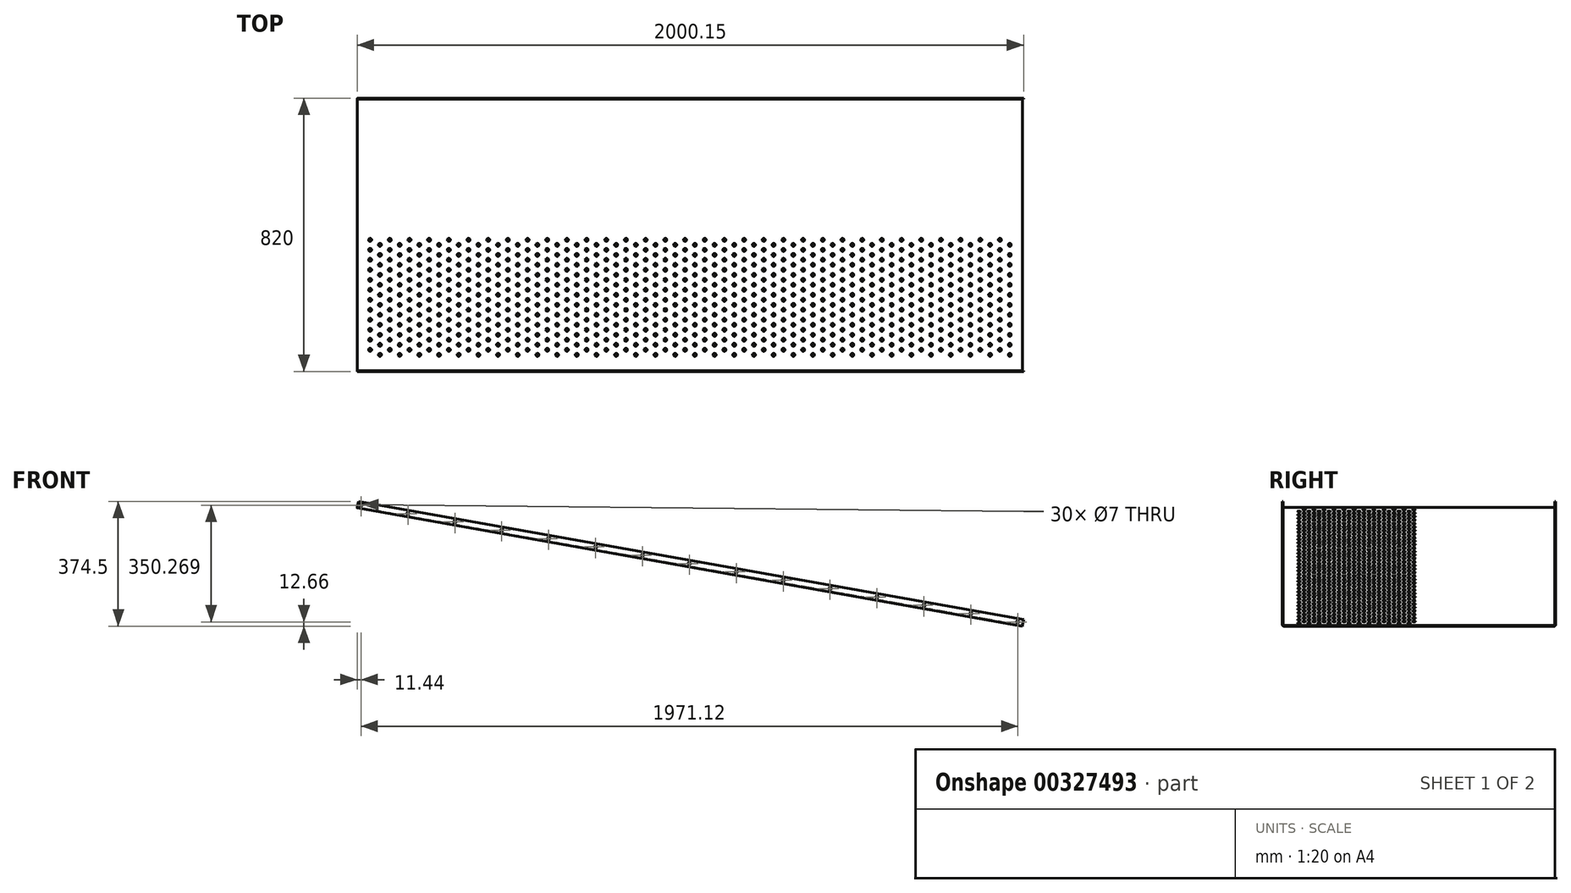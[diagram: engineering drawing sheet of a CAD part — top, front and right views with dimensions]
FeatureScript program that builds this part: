
annotation { "Feature Type Name" : "Feature", "Feature Type Description" : "" }
export const myFeature = defineFeature(function(context is Context, id is Id, definition is map)
    precondition{}
    {
        {
            var Q0;
            Q0=qCreatedBy(makeId("Front.planeOp"),FACE);
            var sketch = newSketch(context, id + "F0", { "sketchPlane" : qUnion([Q0])});
            skLineSegment(sketch, "E0", {"start": v(1435.35, 1.97) * mm, "end": v(-561.3, 356.77) * mm});
            skLineSegment(sketch, "E1", {"start": v(-561.3, 356.77) * mm, "end": v(-561.65, 354.8) * mm});
            skLineSegment(sketch, "E2", {"start": v(-561.65, 354.8) * mm, "end": v(0, 255) * mm});
            skLineSegment(sketch, "E3", {"start": v(1435, 0) * mm, "end": v(1435.35, 1.97) * mm});
            skLineSegment(sketch, "E4", {"start": v(0, 255) * mm, "end": v(1435, 0) * mm});
            skLineSegment(sketch, "E5", {"start": v(0, 255) * mm, "end": v(0, 0) * mm, "construction": true});
            skLineSegment(sketch, "E6", {"start": v(0, 0) * mm, "end": v(1435, 0) * mm, "construction": true});
            skSolve(sketch);
        }
        {
            var Q0;
            Q0=makeQuery(id+"F0.imprint","IMPRINT",FACE,{"disambiguationData":[TD([[makeQuery(id+"F0.imprint","IMPRINT",EDGE,{"derivedFrom":sQuery(id+"F0.wireOp",EDGE,"E0")}),1.0]])]});
            extrude(context, id + "F1", {"entities" : qUnion([Q0]), "depth" : 820 * mm, "symmetric" : true});
        }
        {
            var Q0;
            Q0=makeQuery(id+"F1.opExtrude","CAP_FACE",FACE,{"disambiguationData":[OSD([sQuery(id+"F0.wireOp",EDGE,"E0"),sQuery(id+"F0.wireOp",EDGE,"E1"),sQuery(id+"F0.wireOp",EDGE,"E2"),sQuery(id+"F0.wireOp",EDGE,"E3")])],"isStart":false});
            var sketch = newSketch(context, id + "F2", { "sketchPlane" : qUnion([Q0])});
            skLineSegment(sketch, "E7", {"start": v(-561.65, 354.8) * mm, "end": v(-558.15, 374.5) * mm});
            skLineSegment(sketch, "E8", {"start": v(-558.15, 374.5) * mm, "end": v(1438.5, 19.7) * mm});
            skLineSegment(sketch, "E9", {"start": v(1438.5, 19.7) * mm, "end": v(1435, 0) * mm});
            skLineSegment(sketch, "E10", {"start": v(1435, 0) * mm, "end": v(-561.65, 354.8) * mm});
            skLineSegment(sketch, "E11", {"start": v(-561.65, 354.8) * mm, "end": v(-564.65, 355.34) * mm, "construction": true});
            skLineSegment(sketch, "E12", {"start": v(-564.65, 355.34) * mm, "end": v(-564.65, 375.65) * mm, "construction": true});
            skLineSegment(sketch, "E13", {"start": v(-564.65, 375.65) * mm, "end": v(-558.15, 374.5) * mm, "construction": true});
            skLineSegment(sketch, "E14", {"start": v(1435.35, 20.25) * mm, "end": v(1435.35, 1.97) * mm, "construction": true});
            skLineSegment(sketch, "E15", {"start": v(1435.35, 10.1) * mm, "end": v(1420.91, 12.66) * mm, "construction": true});
            skLineSegment(sketch, "E16", {"start": v(-550.21, 367) * mm, "end": v(-550.21, 358.87) * mm, "construction": true});
            skLineSegment(sketch, "E17", {"start": v(-550.21, 362.93) * mm, "end": v(-564.65, 365.5) * mm, "construction": true});
            skCircle(sketch, "E18", {"center": v(-550.21, 362.93) * mm, "radius": 3.5 * mm});
            skCircle(sketch, "E19.1.0.0", {"center": v(-409.42, 337.91) * mm, "radius": 3.5 * mm});
            skLineSegment(sketch, "E19.1.0.1", {"start": v(-409.42, 341.97) * mm, "end": v(-409.42, 333.85) * mm, "construction": true});
            skCircle(sketch, "E19.2.0.0", {"center": v(-268.62, 312.9) * mm, "radius": 3.5 * mm});
            skLineSegment(sketch, "E19.2.0.1", {"start": v(-268.62, 316.95) * mm, "end": v(-268.62, 308.83) * mm, "construction": true});
            skCircle(sketch, "E19.3.0.0", {"center": v(-127.83, 287.87) * mm, "radius": 3.5 * mm});
            skLineSegment(sketch, "E19.3.0.1", {"start": v(-127.83, 291.93) * mm, "end": v(-127.83, 283.8) * mm, "construction": true});
            skCircle(sketch, "E19.4.0.0", {"center": v(12.97, 262.85) * mm, "radius": 3.5 * mm});
            skLineSegment(sketch, "E19.4.0.1", {"start": v(12.97, 266.92) * mm, "end": v(12.97, 258.79) * mm, "construction": true});
            skCircle(sketch, "E19.5.0.0", {"center": v(153.76, 237.83) * mm, "radius": 3.5 * mm});
            skLineSegment(sketch, "E19.5.0.1", {"start": v(153.76, 241.9) * mm, "end": v(153.76, 233.77) * mm, "construction": true});
            skCircle(sketch, "E19.6.0.0", {"center": v(294.56, 212.81) * mm, "radius": 3.5 * mm});
            skLineSegment(sketch, "E19.6.0.1", {"start": v(294.56, 216.88) * mm, "end": v(294.56, 208.75) * mm, "construction": true});
            skCircle(sketch, "E19.7.0.0", {"center": v(435.35, 187.8) * mm, "radius": 3.5 * mm});
            skLineSegment(sketch, "E19.7.0.1", {"start": v(435.35, 191.86) * mm, "end": v(435.35, 183.73) * mm, "construction": true});
            skCircle(sketch, "E19.8.0.0", {"center": v(576.14, 162.78) * mm, "radius": 3.5 * mm});
            skLineSegment(sketch, "E19.8.0.1", {"start": v(576.14, 166.84) * mm, "end": v(576.14, 158.71) * mm, "construction": true});
            skCircle(sketch, "E19.9.0.0", {"center": v(716.94, 137.76) * mm, "radius": 3.5 * mm});
            skLineSegment(sketch, "E19.9.0.1", {"start": v(716.94, 141.82) * mm, "end": v(716.94, 133.7) * mm, "construction": true});
            skCircle(sketch, "E19.10.0.0", {"center": v(857.73, 112.74) * mm, "radius": 3.5 * mm});
            skLineSegment(sketch, "E19.10.0.1", {"start": v(857.73, 116.8) * mm, "end": v(857.73, 108.67) * mm, "construction": true});
            skCircle(sketch, "E19.11.0.0", {"center": v(998.53, 87.72) * mm, "radius": 3.5 * mm});
            skLineSegment(sketch, "E19.11.0.1", {"start": v(998.53, 91.78) * mm, "end": v(998.53, 83.66) * mm, "construction": true});
            skCircle(sketch, "E19.12.0.0", {"center": v(1139.32, 62.7) * mm, "radius": 3.5 * mm});
            skLineSegment(sketch, "E19.12.0.1", {"start": v(1139.32, 66.76) * mm, "end": v(1139.32, 58.64) * mm, "construction": true});
            skCircle(sketch, "E19.13.0.0", {"center": v(1280.12, 37.68) * mm, "radius": 3.5 * mm});
            skLineSegment(sketch, "E19.13.0.1", {"start": v(1280.12, 41.74) * mm, "end": v(1280.12, 33.62) * mm, "construction": true});
            skCircle(sketch, "E19.14.0.0", {"center": v(1420.91, 12.66) * mm, "radius": 3.5 * mm});
            skLineSegment(sketch, "E19.14.0.1", {"start": v(1420.91, 16.72) * mm, "end": v(1420.91, 8.6) * mm, "construction": true});
            skLineSegment(sketch, "E19.direction1", {"start": v(-550.21, 362.93) * mm, "end": v(-409.42, 337.91) * mm, "construction": true});
            skPoint(sketch, "E20.orphan", {"position": v(1436.75, 9.85) * mm});
            skLineSegment(sketch, "E21.trimOffspring", {"start": v(1420.91, 12.66) * mm, "end": v(-550.21, 362.93) * mm, "construction": true});
            skSolve(sketch);
        }
        {
            var Q0;
            Q0=qSketchRegion(id+"F2",true);
            extrude(context, id + "F3", {"entities" : qUnion([Q0]), "operationType" : NewBodyOperationType.ADD, "oppositeDirection" : true, "depth" : 2 * mm});
        }
        {
            var Q0;
            Q0=makeQuery(id+"F1.opExtrude","CAP_FACE",FACE,{"disambiguationData":[OSD([sQuery(id+"F0.wireOp",EDGE,"E0"),sQuery(id+"F0.wireOp",EDGE,"E1"),sQuery(id+"F0.wireOp",EDGE,"E2"),sQuery(id+"F0.wireOp",EDGE,"E3")])],"isStart":true});
            var sketch = newSketch(context, id + "F4", { "sketchPlane" : qUnion([Q0])});
            skLineSegment(sketch, "E22", {"start": v(561.65, 354.8) * mm, "end": v(558.15, 374.5) * mm});
            skLineSegment(sketch, "E23", {"start": v(558.15, 374.5) * mm, "end": v(-1438.5, 19.7) * mm});
            skLineSegment(sketch, "E24", {"start": v(-1438.5, 19.7) * mm, "end": v(-1435, 0) * mm});
            skLineSegment(sketch, "E25", {"start": v(-1435, 0) * mm, "end": v(561.65, 354.8) * mm});
            skLineSegment(sketch, "E26", {"start": v(561.65, 354.8) * mm, "end": v(564.65, 355.34) * mm, "construction": true});
            skLineSegment(sketch, "E27", {"start": v(564.65, 355.34) * mm, "end": v(564.65, 375.65) * mm, "construction": true});
            skLineSegment(sketch, "E28", {"start": v(564.65, 375.65) * mm, "end": v(558.15, 374.5) * mm, "construction": true});
            skLineSegment(sketch, "E29", {"start": v(-1435.35, 20.25) * mm, "end": v(-1435.35, 1.97) * mm, "construction": true});
            skLineSegment(sketch, "E30", {"start": v(-1435.35, 10.1) * mm, "end": v(-1420.91, 12.66) * mm, "construction": true});
            skLineSegment(sketch, "E31", {"start": v(550.21, 367) * mm, "end": v(550.21, 358.87) * mm, "construction": true});
            skLineSegment(sketch, "E32", {"start": v(550.21, 362.93) * mm, "end": v(564.65, 365.5) * mm, "construction": true});
            skCircle(sketch, "E33", {"center": v(550.21, 362.93) * mm, "radius": 3.5 * mm});
            skCircle(sketch, "E34.1.0.0", {"center": v(409.42, 337.91) * mm, "radius": 3.5 * mm});
            skLineSegment(sketch, "E34.1.0.1", {"start": v(409.42, 341.97) * mm, "end": v(409.42, 333.85) * mm, "construction": true});
            skCircle(sketch, "E34.2.0.0", {"center": v(268.62, 312.9) * mm, "radius": 3.5 * mm});
            skLineSegment(sketch, "E34.2.0.1", {"start": v(268.62, 316.95) * mm, "end": v(268.62, 308.83) * mm, "construction": true});
            skCircle(sketch, "E34.3.0.0", {"center": v(127.83, 287.87) * mm, "radius": 3.5 * mm});
            skLineSegment(sketch, "E34.3.0.1", {"start": v(127.83, 291.93) * mm, "end": v(127.83, 283.8) * mm, "construction": true});
            skCircle(sketch, "E34.4.0.0", {"center": v(-12.97, 262.85) * mm, "radius": 3.5 * mm});
            skLineSegment(sketch, "E34.4.0.1", {"start": v(-12.97, 266.92) * mm, "end": v(-12.97, 258.79) * mm, "construction": true});
            skCircle(sketch, "E34.5.0.0", {"center": v(-153.76, 237.83) * mm, "radius": 3.5 * mm});
            skLineSegment(sketch, "E34.5.0.1", {"start": v(-153.76, 241.9) * mm, "end": v(-153.76, 233.77) * mm, "construction": true});
            skCircle(sketch, "E34.6.0.0", {"center": v(-294.56, 212.81) * mm, "radius": 3.5 * mm});
            skLineSegment(sketch, "E34.6.0.1", {"start": v(-294.56, 216.88) * mm, "end": v(-294.56, 208.75) * mm, "construction": true});
            skCircle(sketch, "E34.7.0.0", {"center": v(-435.35, 187.8) * mm, "radius": 3.5 * mm});
            skLineSegment(sketch, "E34.7.0.1", {"start": v(-435.35, 191.86) * mm, "end": v(-435.35, 183.73) * mm, "construction": true});
            skCircle(sketch, "E34.8.0.0", {"center": v(-576.14, 162.78) * mm, "radius": 3.5 * mm});
            skLineSegment(sketch, "E34.8.0.1", {"start": v(-576.14, 166.84) * mm, "end": v(-576.14, 158.71) * mm, "construction": true});
            skCircle(sketch, "E34.9.0.0", {"center": v(-716.94, 137.76) * mm, "radius": 3.5 * mm});
            skLineSegment(sketch, "E34.9.0.1", {"start": v(-716.94, 141.82) * mm, "end": v(-716.94, 133.7) * mm, "construction": true});
            skCircle(sketch, "E34.10.0.0", {"center": v(-857.73, 112.74) * mm, "radius": 3.5 * mm});
            skLineSegment(sketch, "E34.10.0.1", {"start": v(-857.73, 116.8) * mm, "end": v(-857.73, 108.67) * mm, "construction": true});
            skCircle(sketch, "E34.11.0.0", {"center": v(-998.53, 87.72) * mm, "radius": 3.5 * mm});
            skLineSegment(sketch, "E34.11.0.1", {"start": v(-998.53, 91.78) * mm, "end": v(-998.53, 83.66) * mm, "construction": true});
            skCircle(sketch, "E34.12.0.0", {"center": v(-1139.32, 62.7) * mm, "radius": 3.5 * mm});
            skLineSegment(sketch, "E34.12.0.1", {"start": v(-1139.32, 66.76) * mm, "end": v(-1139.32, 58.64) * mm, "construction": true});
            skCircle(sketch, "E34.13.0.0", {"center": v(-1280.12, 37.68) * mm, "radius": 3.5 * mm});
            skLineSegment(sketch, "E34.13.0.1", {"start": v(-1280.12, 41.74) * mm, "end": v(-1280.12, 33.62) * mm, "construction": true});
            skCircle(sketch, "E34.14.0.0", {"center": v(-1420.91, 12.66) * mm, "radius": 3.5 * mm});
            skLineSegment(sketch, "E34.14.0.1", {"start": v(-1420.91, 16.72) * mm, "end": v(-1420.91, 8.6) * mm, "construction": true});
            skLineSegment(sketch, "E34.direction1", {"start": v(550.21, 362.93) * mm, "end": v(409.42, 337.91) * mm, "construction": true});
            skPoint(sketch, "E35.orphan", {"position": v(-1436.75, 9.85) * mm});
            skLineSegment(sketch, "E36.trimOffspring", {"start": v(-1420.91, 12.66) * mm, "end": v(550.21, 362.93) * mm, "construction": true});
            skSolve(sketch);
        }
        {
            var Q0;
            Q0=qSketchRegion(id+"F4",true);
            extrude(context, id + "F5", {"entities" : qUnion([Q0]), "operationType" : NewBodyOperationType.ADD, "oppositeDirection" : true, "depth" : 2 * mm});
        }
        {
            var Q0;
            Q0=makeQuery(id+"F1.opExtrude","SWEPT_FACE",FACE,{"disambiguationData":[OSD([sQuery(id+"F0.wireOp",EDGE,"E0")])]});
            var sketch = newSketch(context, id + "F6", { "sketchPlane" : qUnion([Q0])});
            skCircle(sketch, "E37", {"center": v(1373.9, -360) * mm, "radius": 4.5 * mm});
            skCircle(sketch, "E38", {"center": v(1343.9, -345) * mm, "radius": 4.5 * mm});
            skLineSegment(sketch, "E39", {"start": v(1412.87, 0) * mm, "end": v(-615.06, 0) * mm, "construction": true});
            skCircle(sketch, "E40.0.1.0", {"center": v(1373.9, -330) * mm, "radius": 4.5 * mm});
            skCircle(sketch, "E40.0.2.0", {"center": v(1373.9, -300) * mm, "radius": 4.5 * mm});
            skCircle(sketch, "E40.0.3.0", {"center": v(1373.9, -270) * mm, "radius": 4.5 * mm});
            skCircle(sketch, "E40.0.4.0", {"center": v(1373.9, -240) * mm, "radius": 4.5 * mm});
            skCircle(sketch, "E40.0.5.0", {"center": v(1373.9, -210) * mm, "radius": 4.5 * mm});
            skCircle(sketch, "E40.0.6.0", {"center": v(1373.9, -180) * mm, "radius": 4.5 * mm});
            skCircle(sketch, "E40.0.7.0", {"center": v(1373.9, -150) * mm, "radius": 4.5 * mm});
            skCircle(sketch, "E40.0.8.0", {"center": v(1373.9, -120) * mm, "radius": 4.5 * mm});
            skCircle(sketch, "E40.0.9.0", {"center": v(1373.9, -90) * mm, "radius": 4.5 * mm});
            skCircle(sketch, "E40.0.10.0", {"center": v(1373.9, -60) * mm, "radius": 4.5 * mm});
            skCircle(sketch, "E40.0.11.0", {"center": v(1373.9, -30) * mm, "radius": 4.5 * mm});
            skCircle(sketch, "E40.0.12.0", {"center": v(1373.9, 0) * mm, "radius": 4.5 * mm});
            skLineSegment(sketch, "E40.direction1", {"start": v(1373.9, -360) * mm, "end": v(1373.9, -360) * mm});
            skLineSegment(sketch, "E40.direction2", {"start": v(1373.9, -360) * mm, "end": v(1373.9, -330) * mm, "construction": true});
            skCircle(sketch, "E41.0.1.0", {"center": v(1343.9, -315) * mm, "radius": 4.5 * mm});
            skCircle(sketch, "E41.0.2.0", {"center": v(1343.9, -285) * mm, "radius": 4.5 * mm});
            skCircle(sketch, "E41.0.3.0", {"center": v(1343.9, -255) * mm, "radius": 4.5 * mm});
            skCircle(sketch, "E41.0.4.0", {"center": v(1343.9, -225) * mm, "radius": 4.5 * mm});
            skCircle(sketch, "E41.0.5.0", {"center": v(1343.9, -195) * mm, "radius": 4.5 * mm});
            skCircle(sketch, "E41.0.6.0", {"center": v(1343.9, -165) * mm, "radius": 4.5 * mm});
            skCircle(sketch, "E41.0.7.0", {"center": v(1343.9, -135) * mm, "radius": 4.5 * mm});
            skCircle(sketch, "E41.0.8.0", {"center": v(1343.9, -105) * mm, "radius": 4.5 * mm});
            skCircle(sketch, "E41.0.9.0", {"center": v(1343.9, -75) * mm, "radius": 4.5 * mm});
            skCircle(sketch, "E41.0.10.0", {"center": v(1343.9, -45) * mm, "radius": 4.5 * mm});
            skCircle(sketch, "E41.0.11.0", {"center": v(1343.9, -15) * mm, "radius": 4.5 * mm});
            skLineSegment(sketch, "E41.direction1", {"start": v(1343.9, -345) * mm, "end": v(1343.9, -345) * mm});
            skLineSegment(sketch, "E41.direction2", {"start": v(1343.9, -345) * mm, "end": v(1343.9, -315) * mm, "construction": true});
            skLineSegment(sketch, "E42.1.0.0", {"start": v(1313.9, -360) * mm, "end": v(1313.9, -330) * mm, "construction": true});
            skCircle(sketch, "E42.1.0.1", {"center": v(1313.9, -60) * mm, "radius": 4.5 * mm});
            skCircle(sketch, "E42.1.0.2", {"center": v(1313.9, -30) * mm, "radius": 4.5 * mm});
            skCircle(sketch, "E42.1.0.3", {"center": v(1313.9, 0) * mm, "radius": 4.5 * mm});
            skCircle(sketch, "E42.1.0.4", {"center": v(1313.9, -240) * mm, "radius": 4.5 * mm});
            skCircle(sketch, "E42.1.0.5", {"center": v(1313.9, -300) * mm, "radius": 4.5 * mm});
            skCircle(sketch, "E42.1.0.6", {"center": v(1283.9, -75) * mm, "radius": 4.5 * mm});
            skCircle(sketch, "E42.1.0.7", {"center": v(1283.9, -285) * mm, "radius": 4.5 * mm});
            skCircle(sketch, "E42.1.0.8", {"center": v(1283.9, -105) * mm, "radius": 4.5 * mm});
            skCircle(sketch, "E42.1.0.9", {"center": v(1283.9, -255) * mm, "radius": 4.5 * mm});
            skCircle(sketch, "E42.1.0.10", {"center": v(1283.9, -195) * mm, "radius": 4.5 * mm});
            skLineSegment(sketch, "E42.1.0.11", {"start": v(1283.9, -345) * mm, "end": v(1283.9, -315) * mm, "construction": true});
            skCircle(sketch, "E42.1.0.12", {"center": v(1283.9, -15) * mm, "radius": 4.5 * mm});
            skCircle(sketch, "E42.1.0.13", {"center": v(1313.9, -120) * mm, "radius": 4.5 * mm});
            skCircle(sketch, "E42.1.0.14", {"center": v(1283.9, -45) * mm, "radius": 4.5 * mm});
            skCircle(sketch, "E42.1.0.15", {"center": v(1313.9, -180) * mm, "radius": 4.5 * mm});
            skCircle(sketch, "E42.1.0.16", {"center": v(1313.9, -150) * mm, "radius": 4.5 * mm});
            skCircle(sketch, "E42.1.0.17", {"center": v(1313.9, -90) * mm, "radius": 4.5 * mm});
            skCircle(sketch, "E42.1.0.18", {"center": v(1283.9, -135) * mm, "radius": 4.5 * mm});
            skCircle(sketch, "E42.1.0.19", {"center": v(1283.9, -225) * mm, "radius": 4.5 * mm});
            skCircle(sketch, "E42.1.0.20", {"center": v(1313.9, -210) * mm, "radius": 4.5 * mm});
            skCircle(sketch, "E42.1.0.21", {"center": v(1283.9, -165) * mm, "radius": 4.5 * mm});
            skCircle(sketch, "E42.1.0.22", {"center": v(1313.9, -270) * mm, "radius": 4.5 * mm});
            skCircle(sketch, "E42.1.0.23", {"center": v(1313.9, -330) * mm, "radius": 4.5 * mm});
            skCircle(sketch, "E42.1.0.24", {"center": v(1283.9, -315) * mm, "radius": 4.5 * mm});
            skCircle(sketch, "E42.1.0.25", {"center": v(1283.9, -345) * mm, "radius": 4.5 * mm});
            skCircle(sketch, "E42.1.0.26", {"center": v(1313.9, -360) * mm, "radius": 4.5 * mm});
            skLineSegment(sketch, "E42.2.0.0", {"start": v(1253.9, -360) * mm, "end": v(1253.9, -330) * mm, "construction": true});
            skCircle(sketch, "E42.2.0.1", {"center": v(1253.9, -60) * mm, "radius": 4.5 * mm});
            skCircle(sketch, "E42.2.0.2", {"center": v(1253.9, -30) * mm, "radius": 4.5 * mm});
            skCircle(sketch, "E42.2.0.3", {"center": v(1253.9, 0) * mm, "radius": 4.5 * mm});
            skCircle(sketch, "E42.2.0.4", {"center": v(1253.9, -240) * mm, "radius": 4.5 * mm});
            skCircle(sketch, "E42.2.0.5", {"center": v(1253.9, -300) * mm, "radius": 4.5 * mm});
            skCircle(sketch, "E42.2.0.6", {"center": v(1223.9, -75) * mm, "radius": 4.5 * mm});
            skCircle(sketch, "E42.2.0.7", {"center": v(1223.9, -285) * mm, "radius": 4.5 * mm});
            skCircle(sketch, "E42.2.0.8", {"center": v(1223.9, -105) * mm, "radius": 4.5 * mm});
            skCircle(sketch, "E42.2.0.9", {"center": v(1223.9, -255) * mm, "radius": 4.5 * mm});
            skCircle(sketch, "E42.2.0.10", {"center": v(1223.9, -195) * mm, "radius": 4.5 * mm});
            skLineSegment(sketch, "E42.2.0.11", {"start": v(1223.9, -345) * mm, "end": v(1223.9, -315) * mm, "construction": true});
            skCircle(sketch, "E42.2.0.12", {"center": v(1223.9, -15) * mm, "radius": 4.5 * mm});
            skCircle(sketch, "E42.2.0.13", {"center": v(1253.9, -120) * mm, "radius": 4.5 * mm});
            skCircle(sketch, "E42.2.0.14", {"center": v(1223.9, -45) * mm, "radius": 4.5 * mm});
            skCircle(sketch, "E42.2.0.15", {"center": v(1253.9, -180) * mm, "radius": 4.5 * mm});
            skCircle(sketch, "E42.2.0.16", {"center": v(1253.9, -150) * mm, "radius": 4.5 * mm});
            skCircle(sketch, "E42.2.0.17", {"center": v(1253.9, -90) * mm, "radius": 4.5 * mm});
            skCircle(sketch, "E42.2.0.18", {"center": v(1223.9, -135) * mm, "radius": 4.5 * mm});
            skCircle(sketch, "E42.2.0.19", {"center": v(1223.9, -225) * mm, "radius": 4.5 * mm});
            skCircle(sketch, "E42.2.0.20", {"center": v(1253.9, -210) * mm, "radius": 4.5 * mm});
            skCircle(sketch, "E42.2.0.21", {"center": v(1223.9, -165) * mm, "radius": 4.5 * mm});
            skCircle(sketch, "E42.2.0.22", {"center": v(1253.9, -270) * mm, "radius": 4.5 * mm});
            skCircle(sketch, "E42.2.0.23", {"center": v(1253.9, -330) * mm, "radius": 4.5 * mm});
            skCircle(sketch, "E42.2.0.24", {"center": v(1223.9, -315) * mm, "radius": 4.5 * mm});
            skCircle(sketch, "E42.2.0.25", {"center": v(1223.9, -345) * mm, "radius": 4.5 * mm});
            skCircle(sketch, "E42.2.0.26", {"center": v(1253.9, -360) * mm, "radius": 4.5 * mm});
            skLineSegment(sketch, "E42.3.0.0", {"start": v(1193.9, -360) * mm, "end": v(1193.9, -330) * mm, "construction": true});
            skCircle(sketch, "E42.3.0.1", {"center": v(1193.9, -60) * mm, "radius": 4.5 * mm});
            skCircle(sketch, "E42.3.0.2", {"center": v(1193.9, -30) * mm, "radius": 4.5 * mm});
            skCircle(sketch, "E42.3.0.3", {"center": v(1193.9, 0) * mm, "radius": 4.5 * mm});
            skCircle(sketch, "E42.3.0.4", {"center": v(1193.9, -240) * mm, "radius": 4.5 * mm});
            skCircle(sketch, "E42.3.0.5", {"center": v(1193.9, -300) * mm, "radius": 4.5 * mm});
            skCircle(sketch, "E42.3.0.6", {"center": v(1163.9, -75) * mm, "radius": 4.5 * mm});
            skCircle(sketch, "E42.3.0.7", {"center": v(1163.9, -285) * mm, "radius": 4.5 * mm});
            skCircle(sketch, "E42.3.0.8", {"center": v(1163.9, -105) * mm, "radius": 4.5 * mm});
            skCircle(sketch, "E42.3.0.9", {"center": v(1163.9, -255) * mm, "radius": 4.5 * mm});
            skCircle(sketch, "E42.3.0.10", {"center": v(1163.9, -195) * mm, "radius": 4.5 * mm});
            skLineSegment(sketch, "E42.3.0.11", {"start": v(1163.9, -345) * mm, "end": v(1163.9, -315) * mm, "construction": true});
            skCircle(sketch, "E42.3.0.12", {"center": v(1163.9, -15) * mm, "radius": 4.5 * mm});
            skCircle(sketch, "E42.3.0.13", {"center": v(1193.9, -120) * mm, "radius": 4.5 * mm});
            skCircle(sketch, "E42.3.0.14", {"center": v(1163.9, -45) * mm, "radius": 4.5 * mm});
            skCircle(sketch, "E42.3.0.15", {"center": v(1193.9, -180) * mm, "radius": 4.5 * mm});
            skCircle(sketch, "E42.3.0.16", {"center": v(1193.9, -150) * mm, "radius": 4.5 * mm});
            skCircle(sketch, "E42.3.0.17", {"center": v(1193.9, -90) * mm, "radius": 4.5 * mm});
            skCircle(sketch, "E42.3.0.18", {"center": v(1163.9, -135) * mm, "radius": 4.5 * mm});
            skCircle(sketch, "E42.3.0.19", {"center": v(1163.9, -225) * mm, "radius": 4.5 * mm});
            skCircle(sketch, "E42.3.0.20", {"center": v(1193.9, -210) * mm, "radius": 4.5 * mm});
            skCircle(sketch, "E42.3.0.21", {"center": v(1163.9, -165) * mm, "radius": 4.5 * mm});
            skCircle(sketch, "E42.3.0.22", {"center": v(1193.9, -270) * mm, "radius": 4.5 * mm});
            skCircle(sketch, "E42.3.0.23", {"center": v(1193.9, -330) * mm, "radius": 4.5 * mm});
            skCircle(sketch, "E42.3.0.24", {"center": v(1163.9, -315) * mm, "radius": 4.5 * mm});
            skCircle(sketch, "E42.3.0.25", {"center": v(1163.9, -345) * mm, "radius": 4.5 * mm});
            skCircle(sketch, "E42.3.0.26", {"center": v(1193.9, -360) * mm, "radius": 4.5 * mm});
            skLineSegment(sketch, "E42.4.0.0", {"start": v(1133.9, -360) * mm, "end": v(1133.9, -330) * mm, "construction": true});
            skCircle(sketch, "E42.4.0.1", {"center": v(1133.9, -60) * mm, "radius": 4.5 * mm});
            skCircle(sketch, "E42.4.0.2", {"center": v(1133.9, -30) * mm, "radius": 4.5 * mm});
            skCircle(sketch, "E42.4.0.3", {"center": v(1133.9, 0) * mm, "radius": 4.5 * mm});
            skCircle(sketch, "E42.4.0.4", {"center": v(1133.9, -240) * mm, "radius": 4.5 * mm});
            skCircle(sketch, "E42.4.0.5", {"center": v(1133.9, -300) * mm, "radius": 4.5 * mm});
            skCircle(sketch, "E42.4.0.6", {"center": v(1103.9, -75) * mm, "radius": 4.5 * mm});
            skCircle(sketch, "E42.4.0.7", {"center": v(1103.9, -285) * mm, "radius": 4.5 * mm});
            skCircle(sketch, "E42.4.0.8", {"center": v(1103.9, -105) * mm, "radius": 4.5 * mm});
            skCircle(sketch, "E42.4.0.9", {"center": v(1103.9, -255) * mm, "radius": 4.5 * mm});
            skCircle(sketch, "E42.4.0.10", {"center": v(1103.9, -195) * mm, "radius": 4.5 * mm});
            skLineSegment(sketch, "E42.4.0.11", {"start": v(1103.9, -345) * mm, "end": v(1103.9, -315) * mm, "construction": true});
            skCircle(sketch, "E42.4.0.12", {"center": v(1103.9, -15) * mm, "radius": 4.5 * mm});
            skCircle(sketch, "E42.4.0.13", {"center": v(1133.9, -120) * mm, "radius": 4.5 * mm});
            skCircle(sketch, "E42.4.0.14", {"center": v(1103.9, -45) * mm, "radius": 4.5 * mm});
            skCircle(sketch, "E42.4.0.15", {"center": v(1133.9, -180) * mm, "radius": 4.5 * mm});
            skCircle(sketch, "E42.4.0.16", {"center": v(1133.9, -150) * mm, "radius": 4.5 * mm});
            skCircle(sketch, "E42.4.0.17", {"center": v(1133.9, -90) * mm, "radius": 4.5 * mm});
            skCircle(sketch, "E42.4.0.18", {"center": v(1103.9, -135) * mm, "radius": 4.5 * mm});
            skCircle(sketch, "E42.4.0.19", {"center": v(1103.9, -225) * mm, "radius": 4.5 * mm});
            skCircle(sketch, "E42.4.0.20", {"center": v(1133.9, -210) * mm, "radius": 4.5 * mm});
            skCircle(sketch, "E42.4.0.21", {"center": v(1103.9, -165) * mm, "radius": 4.5 * mm});
            skCircle(sketch, "E42.4.0.22", {"center": v(1133.9, -270) * mm, "radius": 4.5 * mm});
            skCircle(sketch, "E42.4.0.23", {"center": v(1133.9, -330) * mm, "radius": 4.5 * mm});
            skCircle(sketch, "E42.4.0.24", {"center": v(1103.9, -315) * mm, "radius": 4.5 * mm});
            skCircle(sketch, "E42.4.0.25", {"center": v(1103.9, -345) * mm, "radius": 4.5 * mm});
            skCircle(sketch, "E42.4.0.26", {"center": v(1133.9, -360) * mm, "radius": 4.5 * mm});
            skLineSegment(sketch, "E42.5.0.0", {"start": v(1073.9, -360) * mm, "end": v(1073.9, -330) * mm, "construction": true});
            skCircle(sketch, "E42.5.0.1", {"center": v(1073.9, -60) * mm, "radius": 4.5 * mm});
            skCircle(sketch, "E42.5.0.2", {"center": v(1073.9, -30) * mm, "radius": 4.5 * mm});
            skCircle(sketch, "E42.5.0.3", {"center": v(1073.9, 0) * mm, "radius": 4.5 * mm});
            skCircle(sketch, "E42.5.0.4", {"center": v(1073.9, -240) * mm, "radius": 4.5 * mm});
            skCircle(sketch, "E42.5.0.5", {"center": v(1073.9, -300) * mm, "radius": 4.5 * mm});
            skCircle(sketch, "E42.5.0.6", {"center": v(1043.9, -75) * mm, "radius": 4.5 * mm});
            skCircle(sketch, "E42.5.0.7", {"center": v(1043.9, -285) * mm, "radius": 4.5 * mm});
            skCircle(sketch, "E42.5.0.8", {"center": v(1043.9, -105) * mm, "radius": 4.5 * mm});
            skCircle(sketch, "E42.5.0.9", {"center": v(1043.9, -255) * mm, "radius": 4.5 * mm});
            skCircle(sketch, "E42.5.0.10", {"center": v(1043.9, -195) * mm, "radius": 4.5 * mm});
            skLineSegment(sketch, "E42.5.0.11", {"start": v(1043.9, -345) * mm, "end": v(1043.9, -315) * mm, "construction": true});
            skCircle(sketch, "E42.5.0.12", {"center": v(1043.9, -15) * mm, "radius": 4.5 * mm});
            skCircle(sketch, "E42.5.0.13", {"center": v(1073.9, -120) * mm, "radius": 4.5 * mm});
            skCircle(sketch, "E42.5.0.14", {"center": v(1043.9, -45) * mm, "radius": 4.5 * mm});
            skCircle(sketch, "E42.5.0.15", {"center": v(1073.9, -180) * mm, "radius": 4.5 * mm});
            skCircle(sketch, "E42.5.0.16", {"center": v(1073.9, -150) * mm, "radius": 4.5 * mm});
            skCircle(sketch, "E42.5.0.17", {"center": v(1073.9, -90) * mm, "radius": 4.5 * mm});
            skCircle(sketch, "E42.5.0.18", {"center": v(1043.9, -135) * mm, "radius": 4.5 * mm});
            skCircle(sketch, "E42.5.0.19", {"center": v(1043.9, -225) * mm, "radius": 4.5 * mm});
            skCircle(sketch, "E42.5.0.20", {"center": v(1073.9, -210) * mm, "radius": 4.5 * mm});
            skCircle(sketch, "E42.5.0.21", {"center": v(1043.9, -165) * mm, "radius": 4.5 * mm});
            skCircle(sketch, "E42.5.0.22", {"center": v(1073.9, -270) * mm, "radius": 4.5 * mm});
            skCircle(sketch, "E42.5.0.23", {"center": v(1073.9, -330) * mm, "radius": 4.5 * mm});
            skCircle(sketch, "E42.5.0.24", {"center": v(1043.9, -315) * mm, "radius": 4.5 * mm});
            skCircle(sketch, "E42.5.0.25", {"center": v(1043.9, -345) * mm, "radius": 4.5 * mm});
            skCircle(sketch, "E42.5.0.26", {"center": v(1073.9, -360) * mm, "radius": 4.5 * mm});
            skLineSegment(sketch, "E42.6.0.0", {"start": v(1013.9, -360) * mm, "end": v(1013.9, -330) * mm, "construction": true});
            skCircle(sketch, "E42.6.0.1", {"center": v(1013.9, -60) * mm, "radius": 4.5 * mm});
            skCircle(sketch, "E42.6.0.2", {"center": v(1013.9, -30) * mm, "radius": 4.5 * mm});
            skCircle(sketch, "E42.6.0.3", {"center": v(1013.9, 0) * mm, "radius": 4.5 * mm});
            skCircle(sketch, "E42.6.0.4", {"center": v(1013.9, -240) * mm, "radius": 4.5 * mm});
            skCircle(sketch, "E42.6.0.5", {"center": v(1013.9, -300) * mm, "radius": 4.5 * mm});
            skCircle(sketch, "E42.6.0.6", {"center": v(983.9, -75) * mm, "radius": 4.5 * mm});
            skCircle(sketch, "E42.6.0.7", {"center": v(983.9, -285) * mm, "radius": 4.5 * mm});
            skCircle(sketch, "E42.6.0.8", {"center": v(983.9, -105) * mm, "radius": 4.5 * mm});
            skCircle(sketch, "E42.6.0.9", {"center": v(983.9, -255) * mm, "radius": 4.5 * mm});
            skCircle(sketch, "E42.6.0.10", {"center": v(983.9, -195) * mm, "radius": 4.5 * mm});
            skLineSegment(sketch, "E42.6.0.11", {"start": v(983.9, -345) * mm, "end": v(983.9, -315) * mm, "construction": true});
            skCircle(sketch, "E42.6.0.12", {"center": v(983.9, -15) * mm, "radius": 4.5 * mm});
            skCircle(sketch, "E42.6.0.13", {"center": v(1013.9, -120) * mm, "radius": 4.5 * mm});
            skCircle(sketch, "E42.6.0.14", {"center": v(983.9, -45) * mm, "radius": 4.5 * mm});
            skCircle(sketch, "E42.6.0.15", {"center": v(1013.9, -180) * mm, "radius": 4.5 * mm});
            skCircle(sketch, "E42.6.0.16", {"center": v(1013.9, -150) * mm, "radius": 4.5 * mm});
            skCircle(sketch, "E42.6.0.17", {"center": v(1013.9, -90) * mm, "radius": 4.5 * mm});
            skCircle(sketch, "E42.6.0.18", {"center": v(983.9, -135) * mm, "radius": 4.5 * mm});
            skCircle(sketch, "E42.6.0.19", {"center": v(983.9, -225) * mm, "radius": 4.5 * mm});
            skCircle(sketch, "E42.6.0.20", {"center": v(1013.9, -210) * mm, "radius": 4.5 * mm});
            skCircle(sketch, "E42.6.0.21", {"center": v(983.9, -165) * mm, "radius": 4.5 * mm});
            skCircle(sketch, "E42.6.0.22", {"center": v(1013.9, -270) * mm, "radius": 4.5 * mm});
            skCircle(sketch, "E42.6.0.23", {"center": v(1013.9, -330) * mm, "radius": 4.5 * mm});
            skCircle(sketch, "E42.6.0.24", {"center": v(983.9, -315) * mm, "radius": 4.5 * mm});
            skCircle(sketch, "E42.6.0.25", {"center": v(983.9, -345) * mm, "radius": 4.5 * mm});
            skCircle(sketch, "E42.6.0.26", {"center": v(1013.9, -360) * mm, "radius": 4.5 * mm});
            skLineSegment(sketch, "E42.7.0.0", {"start": v(953.9, -360) * mm, "end": v(953.9, -330) * mm, "construction": true});
            skCircle(sketch, "E42.7.0.1", {"center": v(953.9, -60) * mm, "radius": 4.5 * mm});
            skCircle(sketch, "E42.7.0.2", {"center": v(953.9, -30) * mm, "radius": 4.5 * mm});
            skCircle(sketch, "E42.7.0.3", {"center": v(953.9, 0) * mm, "radius": 4.5 * mm});
            skCircle(sketch, "E42.7.0.4", {"center": v(953.9, -240) * mm, "radius": 4.5 * mm});
            skCircle(sketch, "E42.7.0.5", {"center": v(953.9, -300) * mm, "radius": 4.5 * mm});
            skCircle(sketch, "E42.7.0.6", {"center": v(923.9, -75) * mm, "radius": 4.5 * mm});
            skCircle(sketch, "E42.7.0.7", {"center": v(923.9, -285) * mm, "radius": 4.5 * mm});
            skCircle(sketch, "E42.7.0.8", {"center": v(923.9, -105) * mm, "radius": 4.5 * mm});
            skCircle(sketch, "E42.7.0.9", {"center": v(923.9, -255) * mm, "radius": 4.5 * mm});
            skCircle(sketch, "E42.7.0.10", {"center": v(923.9, -195) * mm, "radius": 4.5 * mm});
            skLineSegment(sketch, "E42.7.0.11", {"start": v(923.9, -345) * mm, "end": v(923.9, -315) * mm, "construction": true});
            skCircle(sketch, "E42.7.0.12", {"center": v(923.9, -15) * mm, "radius": 4.5 * mm});
            skCircle(sketch, "E42.7.0.13", {"center": v(953.9, -120) * mm, "radius": 4.5 * mm});
            skCircle(sketch, "E42.7.0.14", {"center": v(923.9, -45) * mm, "radius": 4.5 * mm});
            skCircle(sketch, "E42.7.0.15", {"center": v(953.9, -180) * mm, "radius": 4.5 * mm});
            skCircle(sketch, "E42.7.0.16", {"center": v(953.9, -150) * mm, "radius": 4.5 * mm});
            skCircle(sketch, "E42.7.0.17", {"center": v(953.9, -90) * mm, "radius": 4.5 * mm});
            skCircle(sketch, "E42.7.0.18", {"center": v(923.9, -135) * mm, "radius": 4.5 * mm});
            skCircle(sketch, "E42.7.0.19", {"center": v(923.9, -225) * mm, "radius": 4.5 * mm});
            skCircle(sketch, "E42.7.0.20", {"center": v(953.9, -210) * mm, "radius": 4.5 * mm});
            skCircle(sketch, "E42.7.0.21", {"center": v(923.9, -165) * mm, "radius": 4.5 * mm});
            skCircle(sketch, "E42.7.0.22", {"center": v(953.9, -270) * mm, "radius": 4.5 * mm});
            skCircle(sketch, "E42.7.0.23", {"center": v(953.9, -330) * mm, "radius": 4.5 * mm});
            skCircle(sketch, "E42.7.0.24", {"center": v(923.9, -315) * mm, "radius": 4.5 * mm});
            skCircle(sketch, "E42.7.0.25", {"center": v(923.9, -345) * mm, "radius": 4.5 * mm});
            skCircle(sketch, "E42.7.0.26", {"center": v(953.9, -360) * mm, "radius": 4.5 * mm});
            skLineSegment(sketch, "E42.8.0.0", {"start": v(893.9, -360) * mm, "end": v(893.9, -330) * mm, "construction": true});
            skCircle(sketch, "E42.8.0.1", {"center": v(893.9, -60) * mm, "radius": 4.5 * mm});
            skCircle(sketch, "E42.8.0.2", {"center": v(893.9, -30) * mm, "radius": 4.5 * mm});
            skCircle(sketch, "E42.8.0.3", {"center": v(893.9, 0) * mm, "radius": 4.5 * mm});
            skCircle(sketch, "E42.8.0.4", {"center": v(893.9, -240) * mm, "radius": 4.5 * mm});
            skCircle(sketch, "E42.8.0.5", {"center": v(893.9, -300) * mm, "radius": 4.5 * mm});
            skCircle(sketch, "E42.8.0.6", {"center": v(863.9, -75) * mm, "radius": 4.5 * mm});
            skCircle(sketch, "E42.8.0.7", {"center": v(863.9, -285) * mm, "radius": 4.5 * mm});
            skCircle(sketch, "E42.8.0.8", {"center": v(863.9, -105) * mm, "radius": 4.5 * mm});
            skCircle(sketch, "E42.8.0.9", {"center": v(863.9, -255) * mm, "radius": 4.5 * mm});
            skCircle(sketch, "E42.8.0.10", {"center": v(863.9, -195) * mm, "radius": 4.5 * mm});
            skLineSegment(sketch, "E42.8.0.11", {"start": v(863.9, -345) * mm, "end": v(863.9, -315) * mm, "construction": true});
            skCircle(sketch, "E42.8.0.12", {"center": v(863.9, -15) * mm, "radius": 4.5 * mm});
            skCircle(sketch, "E42.8.0.13", {"center": v(893.9, -120) * mm, "radius": 4.5 * mm});
            skCircle(sketch, "E42.8.0.14", {"center": v(863.9, -45) * mm, "radius": 4.5 * mm});
            skCircle(sketch, "E42.8.0.15", {"center": v(893.9, -180) * mm, "radius": 4.5 * mm});
            skCircle(sketch, "E42.8.0.16", {"center": v(893.9, -150) * mm, "radius": 4.5 * mm});
            skCircle(sketch, "E42.8.0.17", {"center": v(893.9, -90) * mm, "radius": 4.5 * mm});
            skCircle(sketch, "E42.8.0.18", {"center": v(863.9, -135) * mm, "radius": 4.5 * mm});
            skCircle(sketch, "E42.8.0.19", {"center": v(863.9, -225) * mm, "radius": 4.5 * mm});
            skCircle(sketch, "E42.8.0.20", {"center": v(893.9, -210) * mm, "radius": 4.5 * mm});
            skCircle(sketch, "E42.8.0.21", {"center": v(863.9, -165) * mm, "radius": 4.5 * mm});
            skCircle(sketch, "E42.8.0.22", {"center": v(893.9, -270) * mm, "radius": 4.5 * mm});
            skCircle(sketch, "E42.8.0.23", {"center": v(893.9, -330) * mm, "radius": 4.5 * mm});
            skCircle(sketch, "E42.8.0.24", {"center": v(863.9, -315) * mm, "radius": 4.5 * mm});
            skCircle(sketch, "E42.8.0.25", {"center": v(863.9, -345) * mm, "radius": 4.5 * mm});
            skCircle(sketch, "E42.8.0.26", {"center": v(893.9, -360) * mm, "radius": 4.5 * mm});
            skLineSegment(sketch, "E42.9.0.0", {"start": v(833.9, -360) * mm, "end": v(833.9, -330) * mm, "construction": true});
            skCircle(sketch, "E42.9.0.1", {"center": v(833.9, -60) * mm, "radius": 4.5 * mm});
            skCircle(sketch, "E42.9.0.2", {"center": v(833.9, -30) * mm, "radius": 4.5 * mm});
            skCircle(sketch, "E42.9.0.3", {"center": v(833.9, 0) * mm, "radius": 4.5 * mm});
            skCircle(sketch, "E42.9.0.4", {"center": v(833.9, -240) * mm, "radius": 4.5 * mm});
            skCircle(sketch, "E42.9.0.5", {"center": v(833.9, -300) * mm, "radius": 4.5 * mm});
            skCircle(sketch, "E42.9.0.6", {"center": v(803.9, -75) * mm, "radius": 4.5 * mm});
            skCircle(sketch, "E42.9.0.7", {"center": v(803.9, -285) * mm, "radius": 4.5 * mm});
            skCircle(sketch, "E42.9.0.8", {"center": v(803.9, -105) * mm, "radius": 4.5 * mm});
            skCircle(sketch, "E42.9.0.9", {"center": v(803.9, -255) * mm, "radius": 4.5 * mm});
            skCircle(sketch, "E42.9.0.10", {"center": v(803.9, -195) * mm, "radius": 4.5 * mm});
            skLineSegment(sketch, "E42.9.0.11", {"start": v(803.9, -345) * mm, "end": v(803.9, -315) * mm, "construction": true});
            skCircle(sketch, "E42.9.0.12", {"center": v(803.9, -15) * mm, "radius": 4.5 * mm});
            skCircle(sketch, "E42.9.0.13", {"center": v(833.9, -120) * mm, "radius": 4.5 * mm});
            skCircle(sketch, "E42.9.0.14", {"center": v(803.9, -45) * mm, "radius": 4.5 * mm});
            skCircle(sketch, "E42.9.0.15", {"center": v(833.9, -180) * mm, "radius": 4.5 * mm});
            skCircle(sketch, "E42.9.0.16", {"center": v(833.9, -150) * mm, "radius": 4.5 * mm});
            skCircle(sketch, "E42.9.0.17", {"center": v(833.9, -90) * mm, "radius": 4.5 * mm});
            skCircle(sketch, "E42.9.0.18", {"center": v(803.9, -135) * mm, "radius": 4.5 * mm});
            skCircle(sketch, "E42.9.0.19", {"center": v(803.9, -225) * mm, "radius": 4.5 * mm});
            skCircle(sketch, "E42.9.0.20", {"center": v(833.9, -210) * mm, "radius": 4.5 * mm});
            skCircle(sketch, "E42.9.0.21", {"center": v(803.9, -165) * mm, "radius": 4.5 * mm});
            skCircle(sketch, "E42.9.0.22", {"center": v(833.9, -270) * mm, "radius": 4.5 * mm});
            skCircle(sketch, "E42.9.0.23", {"center": v(833.9, -330) * mm, "radius": 4.5 * mm});
            skCircle(sketch, "E42.9.0.24", {"center": v(803.9, -315) * mm, "radius": 4.5 * mm});
            skCircle(sketch, "E42.9.0.25", {"center": v(803.9, -345) * mm, "radius": 4.5 * mm});
            skCircle(sketch, "E42.9.0.26", {"center": v(833.9, -360) * mm, "radius": 4.5 * mm});
            skLineSegment(sketch, "E42.10.0.0", {"start": v(773.9, -360) * mm, "end": v(773.9, -330) * mm, "construction": true});
            skCircle(sketch, "E42.10.0.1", {"center": v(773.9, -60) * mm, "radius": 4.5 * mm});
            skCircle(sketch, "E42.10.0.2", {"center": v(773.9, -30) * mm, "radius": 4.5 * mm});
            skCircle(sketch, "E42.10.0.3", {"center": v(773.9, 0) * mm, "radius": 4.5 * mm});
            skCircle(sketch, "E42.10.0.4", {"center": v(773.9, -240) * mm, "radius": 4.5 * mm});
            skCircle(sketch, "E42.10.0.5", {"center": v(773.9, -300) * mm, "radius": 4.5 * mm});
            skCircle(sketch, "E42.10.0.6", {"center": v(743.9, -75) * mm, "radius": 4.5 * mm});
            skCircle(sketch, "E42.10.0.7", {"center": v(743.9, -285) * mm, "radius": 4.5 * mm});
            skCircle(sketch, "E42.10.0.8", {"center": v(743.9, -105) * mm, "radius": 4.5 * mm});
            skCircle(sketch, "E42.10.0.9", {"center": v(743.9, -255) * mm, "radius": 4.5 * mm});
            skCircle(sketch, "E42.10.0.10", {"center": v(743.9, -195) * mm, "radius": 4.5 * mm});
            skLineSegment(sketch, "E42.10.0.11", {"start": v(743.9, -345) * mm, "end": v(743.9, -315) * mm, "construction": true});
            skCircle(sketch, "E42.10.0.12", {"center": v(743.9, -15) * mm, "radius": 4.5 * mm});
            skCircle(sketch, "E42.10.0.13", {"center": v(773.9, -120) * mm, "radius": 4.5 * mm});
            skCircle(sketch, "E42.10.0.14", {"center": v(743.9, -45) * mm, "radius": 4.5 * mm});
            skCircle(sketch, "E42.10.0.15", {"center": v(773.9, -180) * mm, "radius": 4.5 * mm});
            skCircle(sketch, "E42.10.0.16", {"center": v(773.9, -150) * mm, "radius": 4.5 * mm});
            skCircle(sketch, "E42.10.0.17", {"center": v(773.9, -90) * mm, "radius": 4.5 * mm});
            skCircle(sketch, "E42.10.0.18", {"center": v(743.9, -135) * mm, "radius": 4.5 * mm});
            skCircle(sketch, "E42.10.0.19", {"center": v(743.9, -225) * mm, "radius": 4.5 * mm});
            skCircle(sketch, "E42.10.0.20", {"center": v(773.9, -210) * mm, "radius": 4.5 * mm});
            skCircle(sketch, "E42.10.0.21", {"center": v(743.9, -165) * mm, "radius": 4.5 * mm});
            skCircle(sketch, "E42.10.0.22", {"center": v(773.9, -270) * mm, "radius": 4.5 * mm});
            skCircle(sketch, "E42.10.0.23", {"center": v(773.9, -330) * mm, "radius": 4.5 * mm});
            skCircle(sketch, "E42.10.0.24", {"center": v(743.9, -315) * mm, "radius": 4.5 * mm});
            skCircle(sketch, "E42.10.0.25", {"center": v(743.9, -345) * mm, "radius": 4.5 * mm});
            skCircle(sketch, "E42.10.0.26", {"center": v(773.9, -360) * mm, "radius": 4.5 * mm});
            skLineSegment(sketch, "E42.11.0.0", {"start": v(713.9, -360) * mm, "end": v(713.9, -330) * mm, "construction": true});
            skCircle(sketch, "E42.11.0.1", {"center": v(713.9, -60) * mm, "radius": 4.5 * mm});
            skCircle(sketch, "E42.11.0.2", {"center": v(713.9, -30) * mm, "radius": 4.5 * mm});
            skCircle(sketch, "E42.11.0.3", {"center": v(713.9, 0) * mm, "radius": 4.5 * mm});
            skCircle(sketch, "E42.11.0.4", {"center": v(713.9, -240) * mm, "radius": 4.5 * mm});
            skCircle(sketch, "E42.11.0.5", {"center": v(713.9, -300) * mm, "radius": 4.5 * mm});
            skCircle(sketch, "E42.11.0.6", {"center": v(683.9, -75) * mm, "radius": 4.5 * mm});
            skCircle(sketch, "E42.11.0.7", {"center": v(683.9, -285) * mm, "radius": 4.5 * mm});
            skCircle(sketch, "E42.11.0.8", {"center": v(683.9, -105) * mm, "radius": 4.5 * mm});
            skCircle(sketch, "E42.11.0.9", {"center": v(683.9, -255) * mm, "radius": 4.5 * mm});
            skCircle(sketch, "E42.11.0.10", {"center": v(683.9, -195) * mm, "radius": 4.5 * mm});
            skLineSegment(sketch, "E42.11.0.11", {"start": v(683.9, -345) * mm, "end": v(683.9, -315) * mm, "construction": true});
            skCircle(sketch, "E42.11.0.12", {"center": v(683.9, -15) * mm, "radius": 4.5 * mm});
            skCircle(sketch, "E42.11.0.13", {"center": v(713.9, -120) * mm, "radius": 4.5 * mm});
            skCircle(sketch, "E42.11.0.14", {"center": v(683.9, -45) * mm, "radius": 4.5 * mm});
            skCircle(sketch, "E42.11.0.15", {"center": v(713.9, -180) * mm, "radius": 4.5 * mm});
            skCircle(sketch, "E42.11.0.16", {"center": v(713.9, -150) * mm, "radius": 4.5 * mm});
            skCircle(sketch, "E42.11.0.17", {"center": v(713.9, -90) * mm, "radius": 4.5 * mm});
            skCircle(sketch, "E42.11.0.18", {"center": v(683.9, -135) * mm, "radius": 4.5 * mm});
            skCircle(sketch, "E42.11.0.19", {"center": v(683.9, -225) * mm, "radius": 4.5 * mm});
            skCircle(sketch, "E42.11.0.20", {"center": v(713.9, -210) * mm, "radius": 4.5 * mm});
            skCircle(sketch, "E42.11.0.21", {"center": v(683.9, -165) * mm, "radius": 4.5 * mm});
            skCircle(sketch, "E42.11.0.22", {"center": v(713.9, -270) * mm, "radius": 4.5 * mm});
            skCircle(sketch, "E42.11.0.23", {"center": v(713.9, -330) * mm, "radius": 4.5 * mm});
            skCircle(sketch, "E42.11.0.24", {"center": v(683.9, -315) * mm, "radius": 4.5 * mm});
            skCircle(sketch, "E42.11.0.25", {"center": v(683.9, -345) * mm, "radius": 4.5 * mm});
            skCircle(sketch, "E42.11.0.26", {"center": v(713.9, -360) * mm, "radius": 4.5 * mm});
            skLineSegment(sketch, "E42.12.0.0", {"start": v(653.9, -360) * mm, "end": v(653.9, -330) * mm, "construction": true});
            skCircle(sketch, "E42.12.0.1", {"center": v(653.9, -60) * mm, "radius": 4.5 * mm});
            skCircle(sketch, "E42.12.0.2", {"center": v(653.9, -30) * mm, "radius": 4.5 * mm});
            skCircle(sketch, "E42.12.0.3", {"center": v(653.9, 0) * mm, "radius": 4.5 * mm});
            skCircle(sketch, "E42.12.0.4", {"center": v(653.9, -240) * mm, "radius": 4.5 * mm});
            skCircle(sketch, "E42.12.0.5", {"center": v(653.9, -300) * mm, "radius": 4.5 * mm});
            skCircle(sketch, "E42.12.0.6", {"center": v(623.9, -75) * mm, "radius": 4.5 * mm});
            skCircle(sketch, "E42.12.0.7", {"center": v(623.9, -285) * mm, "radius": 4.5 * mm});
            skCircle(sketch, "E42.12.0.8", {"center": v(623.9, -105) * mm, "radius": 4.5 * mm});
            skCircle(sketch, "E42.12.0.9", {"center": v(623.9, -255) * mm, "radius": 4.5 * mm});
            skCircle(sketch, "E42.12.0.10", {"center": v(623.9, -195) * mm, "radius": 4.5 * mm});
            skLineSegment(sketch, "E42.12.0.11", {"start": v(623.9, -345) * mm, "end": v(623.9, -315) * mm, "construction": true});
            skCircle(sketch, "E42.12.0.12", {"center": v(623.9, -15) * mm, "radius": 4.5 * mm});
            skCircle(sketch, "E42.12.0.13", {"center": v(653.9, -120) * mm, "radius": 4.5 * mm});
            skCircle(sketch, "E42.12.0.14", {"center": v(623.9, -45) * mm, "radius": 4.5 * mm});
            skCircle(sketch, "E42.12.0.15", {"center": v(653.9, -180) * mm, "radius": 4.5 * mm});
            skCircle(sketch, "E42.12.0.16", {"center": v(653.9, -150) * mm, "radius": 4.5 * mm});
            skCircle(sketch, "E42.12.0.17", {"center": v(653.9, -90) * mm, "radius": 4.5 * mm});
            skCircle(sketch, "E42.12.0.18", {"center": v(623.9, -135) * mm, "radius": 4.5 * mm});
            skCircle(sketch, "E42.12.0.19", {"center": v(623.9, -225) * mm, "radius": 4.5 * mm});
            skCircle(sketch, "E42.12.0.20", {"center": v(653.9, -210) * mm, "radius": 4.5 * mm});
            skCircle(sketch, "E42.12.0.21", {"center": v(623.9, -165) * mm, "radius": 4.5 * mm});
            skCircle(sketch, "E42.12.0.22", {"center": v(653.9, -270) * mm, "radius": 4.5 * mm});
            skCircle(sketch, "E42.12.0.23", {"center": v(653.9, -330) * mm, "radius": 4.5 * mm});
            skCircle(sketch, "E42.12.0.24", {"center": v(623.9, -315) * mm, "radius": 4.5 * mm});
            skCircle(sketch, "E42.12.0.25", {"center": v(623.9, -345) * mm, "radius": 4.5 * mm});
            skCircle(sketch, "E42.12.0.26", {"center": v(653.9, -360) * mm, "radius": 4.5 * mm});
            skLineSegment(sketch, "E42.13.0.0", {"start": v(593.9, -360) * mm, "end": v(593.9, -330) * mm, "construction": true});
            skCircle(sketch, "E42.13.0.1", {"center": v(593.9, -60) * mm, "radius": 4.5 * mm});
            skCircle(sketch, "E42.13.0.2", {"center": v(593.9, -30) * mm, "radius": 4.5 * mm});
            skCircle(sketch, "E42.13.0.3", {"center": v(593.9, 0) * mm, "radius": 4.5 * mm});
            skCircle(sketch, "E42.13.0.4", {"center": v(593.9, -240) * mm, "radius": 4.5 * mm});
            skCircle(sketch, "E42.13.0.5", {"center": v(593.9, -300) * mm, "radius": 4.5 * mm});
            skCircle(sketch, "E42.13.0.6", {"center": v(563.9, -75) * mm, "radius": 4.5 * mm});
            skCircle(sketch, "E42.13.0.7", {"center": v(563.9, -285) * mm, "radius": 4.5 * mm});
            skCircle(sketch, "E42.13.0.8", {"center": v(563.9, -105) * mm, "radius": 4.5 * mm});
            skCircle(sketch, "E42.13.0.9", {"center": v(563.9, -255) * mm, "radius": 4.5 * mm});
            skCircle(sketch, "E42.13.0.10", {"center": v(563.9, -195) * mm, "radius": 4.5 * mm});
            skLineSegment(sketch, "E42.13.0.11", {"start": v(563.9, -345) * mm, "end": v(563.9, -315) * mm, "construction": true});
            skCircle(sketch, "E42.13.0.12", {"center": v(563.9, -15) * mm, "radius": 4.5 * mm});
            skCircle(sketch, "E42.13.0.13", {"center": v(593.9, -120) * mm, "radius": 4.5 * mm});
            skCircle(sketch, "E42.13.0.14", {"center": v(563.9, -45) * mm, "radius": 4.5 * mm});
            skCircle(sketch, "E42.13.0.15", {"center": v(593.9, -180) * mm, "radius": 4.5 * mm});
            skCircle(sketch, "E42.13.0.16", {"center": v(593.9, -150) * mm, "radius": 4.5 * mm});
            skCircle(sketch, "E42.13.0.17", {"center": v(593.9, -90) * mm, "radius": 4.5 * mm});
            skCircle(sketch, "E42.13.0.18", {"center": v(563.9, -135) * mm, "radius": 4.5 * mm});
            skCircle(sketch, "E42.13.0.19", {"center": v(563.9, -225) * mm, "radius": 4.5 * mm});
            skCircle(sketch, "E42.13.0.20", {"center": v(593.9, -210) * mm, "radius": 4.5 * mm});
            skCircle(sketch, "E42.13.0.21", {"center": v(563.9, -165) * mm, "radius": 4.5 * mm});
            skCircle(sketch, "E42.13.0.22", {"center": v(593.9, -270) * mm, "radius": 4.5 * mm});
            skCircle(sketch, "E42.13.0.23", {"center": v(593.9, -330) * mm, "radius": 4.5 * mm});
            skCircle(sketch, "E42.13.0.24", {"center": v(563.9, -315) * mm, "radius": 4.5 * mm});
            skCircle(sketch, "E42.13.0.25", {"center": v(563.9, -345) * mm, "radius": 4.5 * mm});
            skCircle(sketch, "E42.13.0.26", {"center": v(593.9, -360) * mm, "radius": 4.5 * mm});
            skLineSegment(sketch, "E42.14.0.0", {"start": v(533.9, -360) * mm, "end": v(533.9, -330) * mm, "construction": true});
            skCircle(sketch, "E42.14.0.1", {"center": v(533.9, -60) * mm, "radius": 4.5 * mm});
            skCircle(sketch, "E42.14.0.2", {"center": v(533.9, -30) * mm, "radius": 4.5 * mm});
            skCircle(sketch, "E42.14.0.3", {"center": v(533.9, 0) * mm, "radius": 4.5 * mm});
            skCircle(sketch, "E42.14.0.4", {"center": v(533.9, -240) * mm, "radius": 4.5 * mm});
            skCircle(sketch, "E42.14.0.5", {"center": v(533.9, -300) * mm, "radius": 4.5 * mm});
            skCircle(sketch, "E42.14.0.6", {"center": v(503.9, -75) * mm, "radius": 4.5 * mm});
            skCircle(sketch, "E42.14.0.7", {"center": v(503.9, -285) * mm, "radius": 4.5 * mm});
            skCircle(sketch, "E42.14.0.8", {"center": v(503.9, -105) * mm, "radius": 4.5 * mm});
            skCircle(sketch, "E42.14.0.9", {"center": v(503.9, -255) * mm, "radius": 4.5 * mm});
            skCircle(sketch, "E42.14.0.10", {"center": v(503.9, -195) * mm, "radius": 4.5 * mm});
            skLineSegment(sketch, "E42.14.0.11", {"start": v(503.9, -345) * mm, "end": v(503.9, -315) * mm, "construction": true});
            skCircle(sketch, "E42.14.0.12", {"center": v(503.9, -15) * mm, "radius": 4.5 * mm});
            skCircle(sketch, "E42.14.0.13", {"center": v(533.9, -120) * mm, "radius": 4.5 * mm});
            skCircle(sketch, "E42.14.0.14", {"center": v(503.9, -45) * mm, "radius": 4.5 * mm});
            skCircle(sketch, "E42.14.0.15", {"center": v(533.9, -180) * mm, "radius": 4.5 * mm});
            skCircle(sketch, "E42.14.0.16", {"center": v(533.9, -150) * mm, "radius": 4.5 * mm});
            skCircle(sketch, "E42.14.0.17", {"center": v(533.9, -90) * mm, "radius": 4.5 * mm});
            skCircle(sketch, "E42.14.0.18", {"center": v(503.9, -135) * mm, "radius": 4.5 * mm});
            skCircle(sketch, "E42.14.0.19", {"center": v(503.9, -225) * mm, "radius": 4.5 * mm});
            skCircle(sketch, "E42.14.0.20", {"center": v(533.9, -210) * mm, "radius": 4.5 * mm});
            skCircle(sketch, "E42.14.0.21", {"center": v(503.9, -165) * mm, "radius": 4.5 * mm});
            skCircle(sketch, "E42.14.0.22", {"center": v(533.9, -270) * mm, "radius": 4.5 * mm});
            skCircle(sketch, "E42.14.0.23", {"center": v(533.9, -330) * mm, "radius": 4.5 * mm});
            skCircle(sketch, "E42.14.0.24", {"center": v(503.9, -315) * mm, "radius": 4.5 * mm});
            skCircle(sketch, "E42.14.0.25", {"center": v(503.9, -345) * mm, "radius": 4.5 * mm});
            skCircle(sketch, "E42.14.0.26", {"center": v(533.9, -360) * mm, "radius": 4.5 * mm});
            skLineSegment(sketch, "E42.15.0.0", {"start": v(473.9, -360) * mm, "end": v(473.9, -330) * mm, "construction": true});
            skCircle(sketch, "E42.15.0.1", {"center": v(473.9, -60) * mm, "radius": 4.5 * mm});
            skCircle(sketch, "E42.15.0.2", {"center": v(473.9, -30) * mm, "radius": 4.5 * mm});
            skCircle(sketch, "E42.15.0.3", {"center": v(473.9, 0) * mm, "radius": 4.5 * mm});
            skCircle(sketch, "E42.15.0.4", {"center": v(473.9, -240) * mm, "radius": 4.5 * mm});
            skCircle(sketch, "E42.15.0.5", {"center": v(473.9, -300) * mm, "radius": 4.5 * mm});
            skCircle(sketch, "E42.15.0.6", {"center": v(443.9, -75) * mm, "radius": 4.5 * mm});
            skCircle(sketch, "E42.15.0.7", {"center": v(443.9, -285) * mm, "radius": 4.5 * mm});
            skCircle(sketch, "E42.15.0.8", {"center": v(443.9, -105) * mm, "radius": 4.5 * mm});
            skCircle(sketch, "E42.15.0.9", {"center": v(443.9, -255) * mm, "radius": 4.5 * mm});
            skCircle(sketch, "E42.15.0.10", {"center": v(443.9, -195) * mm, "radius": 4.5 * mm});
            skLineSegment(sketch, "E42.15.0.11", {"start": v(443.9, -345) * mm, "end": v(443.9, -315) * mm, "construction": true});
            skCircle(sketch, "E42.15.0.12", {"center": v(443.9, -15) * mm, "radius": 4.5 * mm});
            skCircle(sketch, "E42.15.0.13", {"center": v(473.9, -120) * mm, "radius": 4.5 * mm});
            skCircle(sketch, "E42.15.0.14", {"center": v(443.9, -45) * mm, "radius": 4.5 * mm});
            skCircle(sketch, "E42.15.0.15", {"center": v(473.9, -180) * mm, "radius": 4.5 * mm});
            skCircle(sketch, "E42.15.0.16", {"center": v(473.9, -150) * mm, "radius": 4.5 * mm});
            skCircle(sketch, "E42.15.0.17", {"center": v(473.9, -90) * mm, "radius": 4.5 * mm});
            skCircle(sketch, "E42.15.0.18", {"center": v(443.9, -135) * mm, "radius": 4.5 * mm});
            skCircle(sketch, "E42.15.0.19", {"center": v(443.9, -225) * mm, "radius": 4.5 * mm});
            skCircle(sketch, "E42.15.0.20", {"center": v(473.9, -210) * mm, "radius": 4.5 * mm});
            skCircle(sketch, "E42.15.0.21", {"center": v(443.9, -165) * mm, "radius": 4.5 * mm});
            skCircle(sketch, "E42.15.0.22", {"center": v(473.9, -270) * mm, "radius": 4.5 * mm});
            skCircle(sketch, "E42.15.0.23", {"center": v(473.9, -330) * mm, "radius": 4.5 * mm});
            skCircle(sketch, "E42.15.0.24", {"center": v(443.9, -315) * mm, "radius": 4.5 * mm});
            skCircle(sketch, "E42.15.0.25", {"center": v(443.9, -345) * mm, "radius": 4.5 * mm});
            skCircle(sketch, "E42.15.0.26", {"center": v(473.9, -360) * mm, "radius": 4.5 * mm});
            skLineSegment(sketch, "E42.16.0.0", {"start": v(413.9, -360) * mm, "end": v(413.9, -330) * mm, "construction": true});
            skCircle(sketch, "E42.16.0.1", {"center": v(413.9, -60) * mm, "radius": 4.5 * mm});
            skCircle(sketch, "E42.16.0.2", {"center": v(413.9, -30) * mm, "radius": 4.5 * mm});
            skCircle(sketch, "E42.16.0.3", {"center": v(413.9, 0) * mm, "radius": 4.5 * mm});
            skCircle(sketch, "E42.16.0.4", {"center": v(413.9, -240) * mm, "radius": 4.5 * mm});
            skCircle(sketch, "E42.16.0.5", {"center": v(413.9, -300) * mm, "radius": 4.5 * mm});
            skCircle(sketch, "E42.16.0.6", {"center": v(383.9, -75) * mm, "radius": 4.5 * mm});
            skCircle(sketch, "E42.16.0.7", {"center": v(383.9, -285) * mm, "radius": 4.5 * mm});
            skCircle(sketch, "E42.16.0.8", {"center": v(383.9, -105) * mm, "radius": 4.5 * mm});
            skCircle(sketch, "E42.16.0.9", {"center": v(383.9, -255) * mm, "radius": 4.5 * mm});
            skCircle(sketch, "E42.16.0.10", {"center": v(383.9, -195) * mm, "radius": 4.5 * mm});
            skLineSegment(sketch, "E42.16.0.11", {"start": v(383.9, -345) * mm, "end": v(383.9, -315) * mm, "construction": true});
            skCircle(sketch, "E42.16.0.12", {"center": v(383.9, -15) * mm, "radius": 4.5 * mm});
            skCircle(sketch, "E42.16.0.13", {"center": v(413.9, -120) * mm, "radius": 4.5 * mm});
            skCircle(sketch, "E42.16.0.14", {"center": v(383.9, -45) * mm, "radius": 4.5 * mm});
            skCircle(sketch, "E42.16.0.15", {"center": v(413.9, -180) * mm, "radius": 4.5 * mm});
            skCircle(sketch, "E42.16.0.16", {"center": v(413.9, -150) * mm, "radius": 4.5 * mm});
            skCircle(sketch, "E42.16.0.17", {"center": v(413.9, -90) * mm, "radius": 4.5 * mm});
            skCircle(sketch, "E42.16.0.18", {"center": v(383.9, -135) * mm, "radius": 4.5 * mm});
            skCircle(sketch, "E42.16.0.19", {"center": v(383.9, -225) * mm, "radius": 4.5 * mm});
            skCircle(sketch, "E42.16.0.20", {"center": v(413.9, -210) * mm, "radius": 4.5 * mm});
            skCircle(sketch, "E42.16.0.21", {"center": v(383.9, -165) * mm, "radius": 4.5 * mm});
            skCircle(sketch, "E42.16.0.22", {"center": v(413.9, -270) * mm, "radius": 4.5 * mm});
            skCircle(sketch, "E42.16.0.23", {"center": v(413.9, -330) * mm, "radius": 4.5 * mm});
            skCircle(sketch, "E42.16.0.24", {"center": v(383.9, -315) * mm, "radius": 4.5 * mm});
            skCircle(sketch, "E42.16.0.25", {"center": v(383.9, -345) * mm, "radius": 4.5 * mm});
            skCircle(sketch, "E42.16.0.26", {"center": v(413.9, -360) * mm, "radius": 4.5 * mm});
            skLineSegment(sketch, "E42.17.0.0", {"start": v(353.9, -360) * mm, "end": v(353.9, -330) * mm, "construction": true});
            skCircle(sketch, "E42.17.0.1", {"center": v(353.9, -60) * mm, "radius": 4.5 * mm});
            skCircle(sketch, "E42.17.0.2", {"center": v(353.9, -30) * mm, "radius": 4.5 * mm});
            skCircle(sketch, "E42.17.0.3", {"center": v(353.9, 0) * mm, "radius": 4.5 * mm});
            skCircle(sketch, "E42.17.0.4", {"center": v(353.9, -240) * mm, "radius": 4.5 * mm});
            skCircle(sketch, "E42.17.0.5", {"center": v(353.9, -300) * mm, "radius": 4.5 * mm});
            skCircle(sketch, "E42.17.0.6", {"center": v(323.9, -75) * mm, "radius": 4.5 * mm});
            skCircle(sketch, "E42.17.0.7", {"center": v(323.9, -285) * mm, "radius": 4.5 * mm});
            skCircle(sketch, "E42.17.0.8", {"center": v(323.9, -105) * mm, "radius": 4.5 * mm});
            skCircle(sketch, "E42.17.0.9", {"center": v(323.9, -255) * mm, "radius": 4.5 * mm});
            skCircle(sketch, "E42.17.0.10", {"center": v(323.9, -195) * mm, "radius": 4.5 * mm});
            skLineSegment(sketch, "E42.17.0.11", {"start": v(323.9, -345) * mm, "end": v(323.9, -315) * mm, "construction": true});
            skCircle(sketch, "E42.17.0.12", {"center": v(323.9, -15) * mm, "radius": 4.5 * mm});
            skCircle(sketch, "E42.17.0.13", {"center": v(353.9, -120) * mm, "radius": 4.5 * mm});
            skCircle(sketch, "E42.17.0.14", {"center": v(323.9, -45) * mm, "radius": 4.5 * mm});
            skCircle(sketch, "E42.17.0.15", {"center": v(353.9, -180) * mm, "radius": 4.5 * mm});
            skCircle(sketch, "E42.17.0.16", {"center": v(353.9, -150) * mm, "radius": 4.5 * mm});
            skCircle(sketch, "E42.17.0.17", {"center": v(353.9, -90) * mm, "radius": 4.5 * mm});
            skCircle(sketch, "E42.17.0.18", {"center": v(323.9, -135) * mm, "radius": 4.5 * mm});
            skCircle(sketch, "E42.17.0.19", {"center": v(323.9, -225) * mm, "radius": 4.5 * mm});
            skCircle(sketch, "E42.17.0.20", {"center": v(353.9, -210) * mm, "radius": 4.5 * mm});
            skCircle(sketch, "E42.17.0.21", {"center": v(323.9, -165) * mm, "radius": 4.5 * mm});
            skCircle(sketch, "E42.17.0.22", {"center": v(353.9, -270) * mm, "radius": 4.5 * mm});
            skCircle(sketch, "E42.17.0.23", {"center": v(353.9, -330) * mm, "radius": 4.5 * mm});
            skCircle(sketch, "E42.17.0.24", {"center": v(323.9, -315) * mm, "radius": 4.5 * mm});
            skCircle(sketch, "E42.17.0.25", {"center": v(323.9, -345) * mm, "radius": 4.5 * mm});
            skCircle(sketch, "E42.17.0.26", {"center": v(353.9, -360) * mm, "radius": 4.5 * mm});
            skLineSegment(sketch, "E42.18.0.0", {"start": v(293.9, -360) * mm, "end": v(293.9, -330) * mm, "construction": true});
            skCircle(sketch, "E42.18.0.1", {"center": v(293.9, -60) * mm, "radius": 4.5 * mm});
            skCircle(sketch, "E42.18.0.2", {"center": v(293.9, -30) * mm, "radius": 4.5 * mm});
            skCircle(sketch, "E42.18.0.3", {"center": v(293.9, 0) * mm, "radius": 4.5 * mm});
            skCircle(sketch, "E42.18.0.4", {"center": v(293.9, -240) * mm, "radius": 4.5 * mm});
            skCircle(sketch, "E42.18.0.5", {"center": v(293.9, -300) * mm, "radius": 4.5 * mm});
            skCircle(sketch, "E42.18.0.6", {"center": v(263.9, -75) * mm, "radius": 4.5 * mm});
            skCircle(sketch, "E42.18.0.7", {"center": v(263.9, -285) * mm, "radius": 4.5 * mm});
            skCircle(sketch, "E42.18.0.8", {"center": v(263.9, -105) * mm, "radius": 4.5 * mm});
            skCircle(sketch, "E42.18.0.9", {"center": v(263.9, -255) * mm, "radius": 4.5 * mm});
            skCircle(sketch, "E42.18.0.10", {"center": v(263.9, -195) * mm, "radius": 4.5 * mm});
            skLineSegment(sketch, "E42.18.0.11", {"start": v(263.9, -345) * mm, "end": v(263.9, -315) * mm, "construction": true});
            skCircle(sketch, "E42.18.0.12", {"center": v(263.9, -15) * mm, "radius": 4.5 * mm});
            skCircle(sketch, "E42.18.0.13", {"center": v(293.9, -120) * mm, "radius": 4.5 * mm});
            skCircle(sketch, "E42.18.0.14", {"center": v(263.9, -45) * mm, "radius": 4.5 * mm});
            skCircle(sketch, "E42.18.0.15", {"center": v(293.9, -180) * mm, "radius": 4.5 * mm});
            skCircle(sketch, "E42.18.0.16", {"center": v(293.9, -150) * mm, "radius": 4.5 * mm});
            skCircle(sketch, "E42.18.0.17", {"center": v(293.9, -90) * mm, "radius": 4.5 * mm});
            skCircle(sketch, "E42.18.0.18", {"center": v(263.9, -135) * mm, "radius": 4.5 * mm});
            skCircle(sketch, "E42.18.0.19", {"center": v(263.9, -225) * mm, "radius": 4.5 * mm});
            skCircle(sketch, "E42.18.0.20", {"center": v(293.9, -210) * mm, "radius": 4.5 * mm});
            skCircle(sketch, "E42.18.0.21", {"center": v(263.9, -165) * mm, "radius": 4.5 * mm});
            skCircle(sketch, "E42.18.0.22", {"center": v(293.9, -270) * mm, "radius": 4.5 * mm});
            skCircle(sketch, "E42.18.0.23", {"center": v(293.9, -330) * mm, "radius": 4.5 * mm});
            skCircle(sketch, "E42.18.0.24", {"center": v(263.9, -315) * mm, "radius": 4.5 * mm});
            skCircle(sketch, "E42.18.0.25", {"center": v(263.9, -345) * mm, "radius": 4.5 * mm});
            skCircle(sketch, "E42.18.0.26", {"center": v(293.9, -360) * mm, "radius": 4.5 * mm});
            skLineSegment(sketch, "E42.19.0.0", {"start": v(233.9, -360) * mm, "end": v(233.9, -330) * mm, "construction": true});
            skCircle(sketch, "E42.19.0.1", {"center": v(233.9, -60) * mm, "radius": 4.5 * mm});
            skCircle(sketch, "E42.19.0.2", {"center": v(233.9, -30) * mm, "radius": 4.5 * mm});
            skCircle(sketch, "E42.19.0.3", {"center": v(233.9, 0) * mm, "radius": 4.5 * mm});
            skCircle(sketch, "E42.19.0.4", {"center": v(233.9, -240) * mm, "radius": 4.5 * mm});
            skCircle(sketch, "E42.19.0.5", {"center": v(233.9, -300) * mm, "radius": 4.5 * mm});
            skCircle(sketch, "E42.19.0.6", {"center": v(203.9, -75) * mm, "radius": 4.5 * mm});
            skCircle(sketch, "E42.19.0.7", {"center": v(203.9, -285) * mm, "radius": 4.5 * mm});
            skCircle(sketch, "E42.19.0.8", {"center": v(203.9, -105) * mm, "radius": 4.5 * mm});
            skCircle(sketch, "E42.19.0.9", {"center": v(203.9, -255) * mm, "radius": 4.5 * mm});
            skCircle(sketch, "E42.19.0.10", {"center": v(203.9, -195) * mm, "radius": 4.5 * mm});
            skLineSegment(sketch, "E42.19.0.11", {"start": v(203.9, -345) * mm, "end": v(203.9, -315) * mm, "construction": true});
            skCircle(sketch, "E42.19.0.12", {"center": v(203.9, -15) * mm, "radius": 4.5 * mm});
            skCircle(sketch, "E42.19.0.13", {"center": v(233.9, -120) * mm, "radius": 4.5 * mm});
            skCircle(sketch, "E42.19.0.14", {"center": v(203.9, -45) * mm, "radius": 4.5 * mm});
            skCircle(sketch, "E42.19.0.15", {"center": v(233.9, -180) * mm, "radius": 4.5 * mm});
            skCircle(sketch, "E42.19.0.16", {"center": v(233.9, -150) * mm, "radius": 4.5 * mm});
            skCircle(sketch, "E42.19.0.17", {"center": v(233.9, -90) * mm, "radius": 4.5 * mm});
            skCircle(sketch, "E42.19.0.18", {"center": v(203.9, -135) * mm, "radius": 4.5 * mm});
            skCircle(sketch, "E42.19.0.19", {"center": v(203.9, -225) * mm, "radius": 4.5 * mm});
            skCircle(sketch, "E42.19.0.20", {"center": v(233.9, -210) * mm, "radius": 4.5 * mm});
            skCircle(sketch, "E42.19.0.21", {"center": v(203.9, -165) * mm, "radius": 4.5 * mm});
            skCircle(sketch, "E42.19.0.22", {"center": v(233.9, -270) * mm, "radius": 4.5 * mm});
            skCircle(sketch, "E42.19.0.23", {"center": v(233.9, -330) * mm, "radius": 4.5 * mm});
            skCircle(sketch, "E42.19.0.24", {"center": v(203.9, -315) * mm, "radius": 4.5 * mm});
            skCircle(sketch, "E42.19.0.25", {"center": v(203.9, -345) * mm, "radius": 4.5 * mm});
            skCircle(sketch, "E42.19.0.26", {"center": v(233.9, -360) * mm, "radius": 4.5 * mm});
            skLineSegment(sketch, "E42.20.0.0", {"start": v(173.9, -360) * mm, "end": v(173.9, -330) * mm, "construction": true});
            skCircle(sketch, "E42.20.0.1", {"center": v(173.9, -60) * mm, "radius": 4.5 * mm});
            skCircle(sketch, "E42.20.0.2", {"center": v(173.9, -30) * mm, "radius": 4.5 * mm});
            skCircle(sketch, "E42.20.0.3", {"center": v(173.9, 0) * mm, "radius": 4.5 * mm});
            skCircle(sketch, "E42.20.0.4", {"center": v(173.9, -240) * mm, "radius": 4.5 * mm});
            skCircle(sketch, "E42.20.0.5", {"center": v(173.9, -300) * mm, "radius": 4.5 * mm});
            skCircle(sketch, "E42.20.0.6", {"center": v(143.9, -75) * mm, "radius": 4.5 * mm});
            skCircle(sketch, "E42.20.0.7", {"center": v(143.9, -285) * mm, "radius": 4.5 * mm});
            skCircle(sketch, "E42.20.0.8", {"center": v(143.9, -105) * mm, "radius": 4.5 * mm});
            skCircle(sketch, "E42.20.0.9", {"center": v(143.9, -255) * mm, "radius": 4.5 * mm});
            skCircle(sketch, "E42.20.0.10", {"center": v(143.9, -195) * mm, "radius": 4.5 * mm});
            skLineSegment(sketch, "E42.20.0.11", {"start": v(143.9, -345) * mm, "end": v(143.9, -315) * mm, "construction": true});
            skCircle(sketch, "E42.20.0.12", {"center": v(143.9, -15) * mm, "radius": 4.5 * mm});
            skCircle(sketch, "E42.20.0.13", {"center": v(173.9, -120) * mm, "radius": 4.5 * mm});
            skCircle(sketch, "E42.20.0.14", {"center": v(143.9, -45) * mm, "radius": 4.5 * mm});
            skCircle(sketch, "E42.20.0.15", {"center": v(173.9, -180) * mm, "radius": 4.5 * mm});
            skCircle(sketch, "E42.20.0.16", {"center": v(173.9, -150) * mm, "radius": 4.5 * mm});
            skCircle(sketch, "E42.20.0.17", {"center": v(173.9, -90) * mm, "radius": 4.5 * mm});
            skCircle(sketch, "E42.20.0.18", {"center": v(143.9, -135) * mm, "radius": 4.5 * mm});
            skCircle(sketch, "E42.20.0.19", {"center": v(143.9, -225) * mm, "radius": 4.5 * mm});
            skCircle(sketch, "E42.20.0.20", {"center": v(173.9, -210) * mm, "radius": 4.5 * mm});
            skCircle(sketch, "E42.20.0.21", {"center": v(143.9, -165) * mm, "radius": 4.5 * mm});
            skCircle(sketch, "E42.20.0.22", {"center": v(173.9, -270) * mm, "radius": 4.5 * mm});
            skCircle(sketch, "E42.20.0.23", {"center": v(173.9, -330) * mm, "radius": 4.5 * mm});
            skCircle(sketch, "E42.20.0.24", {"center": v(143.9, -315) * mm, "radius": 4.5 * mm});
            skCircle(sketch, "E42.20.0.25", {"center": v(143.9, -345) * mm, "radius": 4.5 * mm});
            skCircle(sketch, "E42.20.0.26", {"center": v(173.9, -360) * mm, "radius": 4.5 * mm});
            skLineSegment(sketch, "E42.21.0.0", {"start": v(113.9, -360) * mm, "end": v(113.9, -330) * mm, "construction": true});
            skCircle(sketch, "E42.21.0.1", {"center": v(113.9, -60) * mm, "radius": 4.5 * mm});
            skCircle(sketch, "E42.21.0.2", {"center": v(113.9, -30) * mm, "radius": 4.5 * mm});
            skCircle(sketch, "E42.21.0.3", {"center": v(113.9, 0) * mm, "radius": 4.5 * mm});
            skCircle(sketch, "E42.21.0.4", {"center": v(113.9, -240) * mm, "radius": 4.5 * mm});
            skCircle(sketch, "E42.21.0.5", {"center": v(113.9, -300) * mm, "radius": 4.5 * mm});
            skCircle(sketch, "E42.21.0.6", {"center": v(83.9, -75) * mm, "radius": 4.5 * mm});
            skCircle(sketch, "E42.21.0.7", {"center": v(83.9, -285) * mm, "radius": 4.5 * mm});
            skCircle(sketch, "E42.21.0.8", {"center": v(83.9, -105) * mm, "radius": 4.5 * mm});
            skCircle(sketch, "E42.21.0.9", {"center": v(83.9, -255) * mm, "radius": 4.5 * mm});
            skCircle(sketch, "E42.21.0.10", {"center": v(83.9, -195) * mm, "radius": 4.5 * mm});
            skLineSegment(sketch, "E42.21.0.11", {"start": v(83.9, -345) * mm, "end": v(83.9, -315) * mm, "construction": true});
            skCircle(sketch, "E42.21.0.12", {"center": v(83.9, -15) * mm, "radius": 4.5 * mm});
            skCircle(sketch, "E42.21.0.13", {"center": v(113.9, -120) * mm, "radius": 4.5 * mm});
            skCircle(sketch, "E42.21.0.14", {"center": v(83.9, -45) * mm, "radius": 4.5 * mm});
            skCircle(sketch, "E42.21.0.15", {"center": v(113.9, -180) * mm, "radius": 4.5 * mm});
            skCircle(sketch, "E42.21.0.16", {"center": v(113.9, -150) * mm, "radius": 4.5 * mm});
            skCircle(sketch, "E42.21.0.17", {"center": v(113.9, -90) * mm, "radius": 4.5 * mm});
            skCircle(sketch, "E42.21.0.18", {"center": v(83.9, -135) * mm, "radius": 4.5 * mm});
            skCircle(sketch, "E42.21.0.19", {"center": v(83.9, -225) * mm, "radius": 4.5 * mm});
            skCircle(sketch, "E42.21.0.20", {"center": v(113.9, -210) * mm, "radius": 4.5 * mm});
            skCircle(sketch, "E42.21.0.21", {"center": v(83.9, -165) * mm, "radius": 4.5 * mm});
            skCircle(sketch, "E42.21.0.22", {"center": v(113.9, -270) * mm, "radius": 4.5 * mm});
            skCircle(sketch, "E42.21.0.23", {"center": v(113.9, -330) * mm, "radius": 4.5 * mm});
            skCircle(sketch, "E42.21.0.24", {"center": v(83.9, -315) * mm, "radius": 4.5 * mm});
            skCircle(sketch, "E42.21.0.25", {"center": v(83.9, -345) * mm, "radius": 4.5 * mm});
            skCircle(sketch, "E42.21.0.26", {"center": v(113.9, -360) * mm, "radius": 4.5 * mm});
            skLineSegment(sketch, "E42.22.0.0", {"start": v(53.9, -360) * mm, "end": v(53.9, -330) * mm, "construction": true});
            skCircle(sketch, "E42.22.0.1", {"center": v(53.9, -60) * mm, "radius": 4.5 * mm});
            skCircle(sketch, "E42.22.0.2", {"center": v(53.9, -30) * mm, "radius": 4.5 * mm});
            skCircle(sketch, "E42.22.0.3", {"center": v(53.9, 0) * mm, "radius": 4.5 * mm});
            skCircle(sketch, "E42.22.0.4", {"center": v(53.9, -240) * mm, "radius": 4.5 * mm});
            skCircle(sketch, "E42.22.0.5", {"center": v(53.9, -300) * mm, "radius": 4.5 * mm});
            skCircle(sketch, "E42.22.0.6", {"center": v(23.9, -75) * mm, "radius": 4.5 * mm});
            skCircle(sketch, "E42.22.0.7", {"center": v(23.9, -285) * mm, "radius": 4.5 * mm});
            skCircle(sketch, "E42.22.0.8", {"center": v(23.9, -105) * mm, "radius": 4.5 * mm});
            skCircle(sketch, "E42.22.0.9", {"center": v(23.9, -255) * mm, "radius": 4.5 * mm});
            skCircle(sketch, "E42.22.0.10", {"center": v(23.9, -195) * mm, "radius": 4.5 * mm});
            skLineSegment(sketch, "E42.22.0.11", {"start": v(23.9, -345) * mm, "end": v(23.9, -315) * mm, "construction": true});
            skCircle(sketch, "E42.22.0.12", {"center": v(23.9, -15) * mm, "radius": 4.5 * mm});
            skCircle(sketch, "E42.22.0.13", {"center": v(53.9, -120) * mm, "radius": 4.5 * mm});
            skCircle(sketch, "E42.22.0.14", {"center": v(23.9, -45) * mm, "radius": 4.5 * mm});
            skCircle(sketch, "E42.22.0.15", {"center": v(53.9, -180) * mm, "radius": 4.5 * mm});
            skCircle(sketch, "E42.22.0.16", {"center": v(53.9, -150) * mm, "radius": 4.5 * mm});
            skCircle(sketch, "E42.22.0.17", {"center": v(53.9, -90) * mm, "radius": 4.5 * mm});
            skCircle(sketch, "E42.22.0.18", {"center": v(23.9, -135) * mm, "radius": 4.5 * mm});
            skCircle(sketch, "E42.22.0.19", {"center": v(23.9, -225) * mm, "radius": 4.5 * mm});
            skCircle(sketch, "E42.22.0.20", {"center": v(53.9, -210) * mm, "radius": 4.5 * mm});
            skCircle(sketch, "E42.22.0.21", {"center": v(23.9, -165) * mm, "radius": 4.5 * mm});
            skCircle(sketch, "E42.22.0.22", {"center": v(53.9, -270) * mm, "radius": 4.5 * mm});
            skCircle(sketch, "E42.22.0.23", {"center": v(53.9, -330) * mm, "radius": 4.5 * mm});
            skCircle(sketch, "E42.22.0.24", {"center": v(23.9, -315) * mm, "radius": 4.5 * mm});
            skCircle(sketch, "E42.22.0.25", {"center": v(23.9, -345) * mm, "radius": 4.5 * mm});
            skCircle(sketch, "E42.22.0.26", {"center": v(53.9, -360) * mm, "radius": 4.5 * mm});
            skLineSegment(sketch, "E42.23.0.0", {"start": v(-6.1, -360) * mm, "end": v(-6.1, -330) * mm, "construction": true});
            skCircle(sketch, "E42.23.0.1", {"center": v(-6.1, -60) * mm, "radius": 4.5 * mm});
            skCircle(sketch, "E42.23.0.2", {"center": v(-6.1, -30) * mm, "radius": 4.5 * mm});
            skCircle(sketch, "E42.23.0.3", {"center": v(-6.1, 0) * mm, "radius": 4.5 * mm});
            skCircle(sketch, "E42.23.0.4", {"center": v(-6.1, -240) * mm, "radius": 4.5 * mm});
            skCircle(sketch, "E42.23.0.5", {"center": v(-6.1, -300) * mm, "radius": 4.5 * mm});
            skCircle(sketch, "E42.23.0.6", {"center": v(-36.1, -75) * mm, "radius": 4.5 * mm});
            skCircle(sketch, "E42.23.0.7", {"center": v(-36.1, -285) * mm, "radius": 4.5 * mm});
            skCircle(sketch, "E42.23.0.8", {"center": v(-36.1, -105) * mm, "radius": 4.5 * mm});
            skCircle(sketch, "E42.23.0.9", {"center": v(-36.1, -255) * mm, "radius": 4.5 * mm});
            skCircle(sketch, "E42.23.0.10", {"center": v(-36.1, -195) * mm, "radius": 4.5 * mm});
            skLineSegment(sketch, "E42.23.0.11", {"start": v(-36.1, -345) * mm, "end": v(-36.1, -315) * mm, "construction": true});
            skCircle(sketch, "E42.23.0.12", {"center": v(-36.1, -15) * mm, "radius": 4.5 * mm});
            skCircle(sketch, "E42.23.0.13", {"center": v(-6.1, -120) * mm, "radius": 4.5 * mm});
            skCircle(sketch, "E42.23.0.14", {"center": v(-36.1, -45) * mm, "radius": 4.5 * mm});
            skCircle(sketch, "E42.23.0.15", {"center": v(-6.1, -180) * mm, "radius": 4.5 * mm});
            skCircle(sketch, "E42.23.0.16", {"center": v(-6.1, -150) * mm, "radius": 4.5 * mm});
            skCircle(sketch, "E42.23.0.17", {"center": v(-6.1, -90) * mm, "radius": 4.5 * mm});
            skCircle(sketch, "E42.23.0.18", {"center": v(-36.1, -135) * mm, "radius": 4.5 * mm});
            skCircle(sketch, "E42.23.0.19", {"center": v(-36.1, -225) * mm, "radius": 4.5 * mm});
            skCircle(sketch, "E42.23.0.20", {"center": v(-6.1, -210) * mm, "radius": 4.5 * mm});
            skCircle(sketch, "E42.23.0.21", {"center": v(-36.1, -165) * mm, "radius": 4.5 * mm});
            skCircle(sketch, "E42.23.0.22", {"center": v(-6.1, -270) * mm, "radius": 4.5 * mm});
            skCircle(sketch, "E42.23.0.23", {"center": v(-6.1, -330) * mm, "radius": 4.5 * mm});
            skCircle(sketch, "E42.23.0.24", {"center": v(-36.1, -315) * mm, "radius": 4.5 * mm});
            skCircle(sketch, "E42.23.0.25", {"center": v(-36.1, -345) * mm, "radius": 4.5 * mm});
            skCircle(sketch, "E42.23.0.26", {"center": v(-6.1, -360) * mm, "radius": 4.5 * mm});
            skLineSegment(sketch, "E42.24.0.0", {"start": v(-66.1, -360) * mm, "end": v(-66.1, -330) * mm, "construction": true});
            skCircle(sketch, "E42.24.0.1", {"center": v(-66.1, -60) * mm, "radius": 4.5 * mm});
            skCircle(sketch, "E42.24.0.2", {"center": v(-66.1, -30) * mm, "radius": 4.5 * mm});
            skCircle(sketch, "E42.24.0.3", {"center": v(-66.1, 0) * mm, "radius": 4.5 * mm});
            skCircle(sketch, "E42.24.0.4", {"center": v(-66.1, -240) * mm, "radius": 4.5 * mm});
            skCircle(sketch, "E42.24.0.5", {"center": v(-66.1, -300) * mm, "radius": 4.5 * mm});
            skCircle(sketch, "E42.24.0.6", {"center": v(-96.1, -75) * mm, "radius": 4.5 * mm});
            skCircle(sketch, "E42.24.0.7", {"center": v(-96.1, -285) * mm, "radius": 4.5 * mm});
            skCircle(sketch, "E42.24.0.8", {"center": v(-96.1, -105) * mm, "radius": 4.5 * mm});
            skCircle(sketch, "E42.24.0.9", {"center": v(-96.1, -255) * mm, "radius": 4.5 * mm});
            skCircle(sketch, "E42.24.0.10", {"center": v(-96.1, -195) * mm, "radius": 4.5 * mm});
            skLineSegment(sketch, "E42.24.0.11", {"start": v(-96.1, -345) * mm, "end": v(-96.1, -315) * mm, "construction": true});
            skCircle(sketch, "E42.24.0.12", {"center": v(-96.1, -15) * mm, "radius": 4.5 * mm});
            skCircle(sketch, "E42.24.0.13", {"center": v(-66.1, -120) * mm, "radius": 4.5 * mm});
            skCircle(sketch, "E42.24.0.14", {"center": v(-96.1, -45) * mm, "radius": 4.5 * mm});
            skCircle(sketch, "E42.24.0.15", {"center": v(-66.1, -180) * mm, "radius": 4.5 * mm});
            skCircle(sketch, "E42.24.0.16", {"center": v(-66.1, -150) * mm, "radius": 4.5 * mm});
            skCircle(sketch, "E42.24.0.17", {"center": v(-66.1, -90) * mm, "radius": 4.5 * mm});
            skCircle(sketch, "E42.24.0.18", {"center": v(-96.1, -135) * mm, "radius": 4.5 * mm});
            skCircle(sketch, "E42.24.0.19", {"center": v(-96.1, -225) * mm, "radius": 4.5 * mm});
            skCircle(sketch, "E42.24.0.20", {"center": v(-66.1, -210) * mm, "radius": 4.5 * mm});
            skCircle(sketch, "E42.24.0.21", {"center": v(-96.1, -165) * mm, "radius": 4.5 * mm});
            skCircle(sketch, "E42.24.0.22", {"center": v(-66.1, -270) * mm, "radius": 4.5 * mm});
            skCircle(sketch, "E42.24.0.23", {"center": v(-66.1, -330) * mm, "radius": 4.5 * mm});
            skCircle(sketch, "E42.24.0.24", {"center": v(-96.1, -315) * mm, "radius": 4.5 * mm});
            skCircle(sketch, "E42.24.0.25", {"center": v(-96.1, -345) * mm, "radius": 4.5 * mm});
            skCircle(sketch, "E42.24.0.26", {"center": v(-66.1, -360) * mm, "radius": 4.5 * mm});
            skLineSegment(sketch, "E42.25.0.0", {"start": v(-126.1, -360) * mm, "end": v(-126.1, -330) * mm, "construction": true});
            skCircle(sketch, "E42.25.0.1", {"center": v(-126.1, -60) * mm, "radius": 4.5 * mm});
            skCircle(sketch, "E42.25.0.2", {"center": v(-126.1, -30) * mm, "radius": 4.5 * mm});
            skCircle(sketch, "E42.25.0.3", {"center": v(-126.1, 0) * mm, "radius": 4.5 * mm});
            skCircle(sketch, "E42.25.0.4", {"center": v(-126.1, -240) * mm, "radius": 4.5 * mm});
            skCircle(sketch, "E42.25.0.5", {"center": v(-126.1, -300) * mm, "radius": 4.5 * mm});
            skCircle(sketch, "E42.25.0.6", {"center": v(-156.1, -75) * mm, "radius": 4.5 * mm});
            skCircle(sketch, "E42.25.0.7", {"center": v(-156.1, -285) * mm, "radius": 4.5 * mm});
            skCircle(sketch, "E42.25.0.8", {"center": v(-156.1, -105) * mm, "radius": 4.5 * mm});
            skCircle(sketch, "E42.25.0.9", {"center": v(-156.1, -255) * mm, "radius": 4.5 * mm});
            skCircle(sketch, "E42.25.0.10", {"center": v(-156.1, -195) * mm, "radius": 4.5 * mm});
            skLineSegment(sketch, "E42.25.0.11", {"start": v(-156.1, -345) * mm, "end": v(-156.1, -315) * mm, "construction": true});
            skCircle(sketch, "E42.25.0.12", {"center": v(-156.1, -15) * mm, "radius": 4.5 * mm});
            skCircle(sketch, "E42.25.0.13", {"center": v(-126.1, -120) * mm, "radius": 4.5 * mm});
            skCircle(sketch, "E42.25.0.14", {"center": v(-156.1, -45) * mm, "radius": 4.5 * mm});
            skCircle(sketch, "E42.25.0.15", {"center": v(-126.1, -180) * mm, "radius": 4.5 * mm});
            skCircle(sketch, "E42.25.0.16", {"center": v(-126.1, -150) * mm, "radius": 4.5 * mm});
            skCircle(sketch, "E42.25.0.17", {"center": v(-126.1, -90) * mm, "radius": 4.5 * mm});
            skCircle(sketch, "E42.25.0.18", {"center": v(-156.1, -135) * mm, "radius": 4.5 * mm});
            skCircle(sketch, "E42.25.0.19", {"center": v(-156.1, -225) * mm, "radius": 4.5 * mm});
            skCircle(sketch, "E42.25.0.20", {"center": v(-126.1, -210) * mm, "radius": 4.5 * mm});
            skCircle(sketch, "E42.25.0.21", {"center": v(-156.1, -165) * mm, "radius": 4.5 * mm});
            skCircle(sketch, "E42.25.0.22", {"center": v(-126.1, -270) * mm, "radius": 4.5 * mm});
            skCircle(sketch, "E42.25.0.23", {"center": v(-126.1, -330) * mm, "radius": 4.5 * mm});
            skCircle(sketch, "E42.25.0.24", {"center": v(-156.1, -315) * mm, "radius": 4.5 * mm});
            skCircle(sketch, "E42.25.0.25", {"center": v(-156.1, -345) * mm, "radius": 4.5 * mm});
            skCircle(sketch, "E42.25.0.26", {"center": v(-126.1, -360) * mm, "radius": 4.5 * mm});
            skLineSegment(sketch, "E42.26.0.0", {"start": v(-186.1, -360) * mm, "end": v(-186.1, -330) * mm, "construction": true});
            skCircle(sketch, "E42.26.0.1", {"center": v(-186.1, -60) * mm, "radius": 4.5 * mm});
            skCircle(sketch, "E42.26.0.2", {"center": v(-186.1, -30) * mm, "radius": 4.5 * mm});
            skCircle(sketch, "E42.26.0.3", {"center": v(-186.1, 0) * mm, "radius": 4.5 * mm});
            skCircle(sketch, "E42.26.0.4", {"center": v(-186.1, -240) * mm, "radius": 4.5 * mm});
            skCircle(sketch, "E42.26.0.5", {"center": v(-186.1, -300) * mm, "radius": 4.5 * mm});
            skCircle(sketch, "E42.26.0.6", {"center": v(-216.1, -75) * mm, "radius": 4.5 * mm});
            skCircle(sketch, "E42.26.0.7", {"center": v(-216.1, -285) * mm, "radius": 4.5 * mm});
            skCircle(sketch, "E42.26.0.8", {"center": v(-216.1, -105) * mm, "radius": 4.5 * mm});
            skCircle(sketch, "E42.26.0.9", {"center": v(-216.1, -255) * mm, "radius": 4.5 * mm});
            skCircle(sketch, "E42.26.0.10", {"center": v(-216.1, -195) * mm, "radius": 4.5 * mm});
            skLineSegment(sketch, "E42.26.0.11", {"start": v(-216.1, -345) * mm, "end": v(-216.1, -315) * mm, "construction": true});
            skCircle(sketch, "E42.26.0.12", {"center": v(-216.1, -15) * mm, "radius": 4.5 * mm});
            skCircle(sketch, "E42.26.0.13", {"center": v(-186.1, -120) * mm, "radius": 4.5 * mm});
            skCircle(sketch, "E42.26.0.14", {"center": v(-216.1, -45) * mm, "radius": 4.5 * mm});
            skCircle(sketch, "E42.26.0.15", {"center": v(-186.1, -180) * mm, "radius": 4.5 * mm});
            skCircle(sketch, "E42.26.0.16", {"center": v(-186.1, -150) * mm, "radius": 4.5 * mm});
            skCircle(sketch, "E42.26.0.17", {"center": v(-186.1, -90) * mm, "radius": 4.5 * mm});
            skCircle(sketch, "E42.26.0.18", {"center": v(-216.1, -135) * mm, "radius": 4.5 * mm});
            skCircle(sketch, "E42.26.0.19", {"center": v(-216.1, -225) * mm, "radius": 4.5 * mm});
            skCircle(sketch, "E42.26.0.20", {"center": v(-186.1, -210) * mm, "radius": 4.5 * mm});
            skCircle(sketch, "E42.26.0.21", {"center": v(-216.1, -165) * mm, "radius": 4.5 * mm});
            skCircle(sketch, "E42.26.0.22", {"center": v(-186.1, -270) * mm, "radius": 4.5 * mm});
            skCircle(sketch, "E42.26.0.23", {"center": v(-186.1, -330) * mm, "radius": 4.5 * mm});
            skCircle(sketch, "E42.26.0.24", {"center": v(-216.1, -315) * mm, "radius": 4.5 * mm});
            skCircle(sketch, "E42.26.0.25", {"center": v(-216.1, -345) * mm, "radius": 4.5 * mm});
            skCircle(sketch, "E42.26.0.26", {"center": v(-186.1, -360) * mm, "radius": 4.5 * mm});
            skLineSegment(sketch, "E42.27.0.0", {"start": v(-246.1, -360) * mm, "end": v(-246.1, -330) * mm, "construction": true});
            skCircle(sketch, "E42.27.0.1", {"center": v(-246.1, -60) * mm, "radius": 4.5 * mm});
            skCircle(sketch, "E42.27.0.2", {"center": v(-246.1, -30) * mm, "radius": 4.5 * mm});
            skCircle(sketch, "E42.27.0.3", {"center": v(-246.1, 0) * mm, "radius": 4.5 * mm});
            skCircle(sketch, "E42.27.0.4", {"center": v(-246.1, -240) * mm, "radius": 4.5 * mm});
            skCircle(sketch, "E42.27.0.5", {"center": v(-246.1, -300) * mm, "radius": 4.5 * mm});
            skCircle(sketch, "E42.27.0.6", {"center": v(-276.1, -75) * mm, "radius": 4.5 * mm});
            skCircle(sketch, "E42.27.0.7", {"center": v(-276.1, -285) * mm, "radius": 4.5 * mm});
            skCircle(sketch, "E42.27.0.8", {"center": v(-276.1, -105) * mm, "radius": 4.5 * mm});
            skCircle(sketch, "E42.27.0.9", {"center": v(-276.1, -255) * mm, "radius": 4.5 * mm});
            skCircle(sketch, "E42.27.0.10", {"center": v(-276.1, -195) * mm, "radius": 4.5 * mm});
            skLineSegment(sketch, "E42.27.0.11", {"start": v(-276.1, -345) * mm, "end": v(-276.1, -315) * mm, "construction": true});
            skCircle(sketch, "E42.27.0.12", {"center": v(-276.1, -15) * mm, "radius": 4.5 * mm});
            skCircle(sketch, "E42.27.0.13", {"center": v(-246.1, -120) * mm, "radius": 4.5 * mm});
            skCircle(sketch, "E42.27.0.14", {"center": v(-276.1, -45) * mm, "radius": 4.5 * mm});
            skCircle(sketch, "E42.27.0.15", {"center": v(-246.1, -180) * mm, "radius": 4.5 * mm});
            skCircle(sketch, "E42.27.0.16", {"center": v(-246.1, -150) * mm, "radius": 4.5 * mm});
            skCircle(sketch, "E42.27.0.17", {"center": v(-246.1, -90) * mm, "radius": 4.5 * mm});
            skCircle(sketch, "E42.27.0.18", {"center": v(-276.1, -135) * mm, "radius": 4.5 * mm});
            skCircle(sketch, "E42.27.0.19", {"center": v(-276.1, -225) * mm, "radius": 4.5 * mm});
            skCircle(sketch, "E42.27.0.20", {"center": v(-246.1, -210) * mm, "radius": 4.5 * mm});
            skCircle(sketch, "E42.27.0.21", {"center": v(-276.1, -165) * mm, "radius": 4.5 * mm});
            skCircle(sketch, "E42.27.0.22", {"center": v(-246.1, -270) * mm, "radius": 4.5 * mm});
            skCircle(sketch, "E42.27.0.23", {"center": v(-246.1, -330) * mm, "radius": 4.5 * mm});
            skCircle(sketch, "E42.27.0.24", {"center": v(-276.1, -315) * mm, "radius": 4.5 * mm});
            skCircle(sketch, "E42.27.0.25", {"center": v(-276.1, -345) * mm, "radius": 4.5 * mm});
            skCircle(sketch, "E42.27.0.26", {"center": v(-246.1, -360) * mm, "radius": 4.5 * mm});
            skLineSegment(sketch, "E42.28.0.0", {"start": v(-306.1, -360) * mm, "end": v(-306.1, -330) * mm, "construction": true});
            skCircle(sketch, "E42.28.0.1", {"center": v(-306.1, -60) * mm, "radius": 4.5 * mm});
            skCircle(sketch, "E42.28.0.2", {"center": v(-306.1, -30) * mm, "radius": 4.5 * mm});
            skCircle(sketch, "E42.28.0.3", {"center": v(-306.1, 0) * mm, "radius": 4.5 * mm});
            skCircle(sketch, "E42.28.0.4", {"center": v(-306.1, -240) * mm, "radius": 4.5 * mm});
            skCircle(sketch, "E42.28.0.5", {"center": v(-306.1, -300) * mm, "radius": 4.5 * mm});
            skCircle(sketch, "E42.28.0.6", {"center": v(-336.1, -75) * mm, "radius": 4.5 * mm});
            skCircle(sketch, "E42.28.0.7", {"center": v(-336.1, -285) * mm, "radius": 4.5 * mm});
            skCircle(sketch, "E42.28.0.8", {"center": v(-336.1, -105) * mm, "radius": 4.5 * mm});
            skCircle(sketch, "E42.28.0.9", {"center": v(-336.1, -255) * mm, "radius": 4.5 * mm});
            skCircle(sketch, "E42.28.0.10", {"center": v(-336.1, -195) * mm, "radius": 4.5 * mm});
            skLineSegment(sketch, "E42.28.0.11", {"start": v(-336.1, -345) * mm, "end": v(-336.1, -315) * mm, "construction": true});
            skCircle(sketch, "E42.28.0.12", {"center": v(-336.1, -15) * mm, "radius": 4.5 * mm});
            skCircle(sketch, "E42.28.0.13", {"center": v(-306.1, -120) * mm, "radius": 4.5 * mm});
            skCircle(sketch, "E42.28.0.14", {"center": v(-336.1, -45) * mm, "radius": 4.5 * mm});
            skCircle(sketch, "E42.28.0.15", {"center": v(-306.1, -180) * mm, "radius": 4.5 * mm});
            skCircle(sketch, "E42.28.0.16", {"center": v(-306.1, -150) * mm, "radius": 4.5 * mm});
            skCircle(sketch, "E42.28.0.17", {"center": v(-306.1, -90) * mm, "radius": 4.5 * mm});
            skCircle(sketch, "E42.28.0.18", {"center": v(-336.1, -135) * mm, "radius": 4.5 * mm});
            skCircle(sketch, "E42.28.0.19", {"center": v(-336.1, -225) * mm, "radius": 4.5 * mm});
            skCircle(sketch, "E42.28.0.20", {"center": v(-306.1, -210) * mm, "radius": 4.5 * mm});
            skCircle(sketch, "E42.28.0.21", {"center": v(-336.1, -165) * mm, "radius": 4.5 * mm});
            skCircle(sketch, "E42.28.0.22", {"center": v(-306.1, -270) * mm, "radius": 4.5 * mm});
            skCircle(sketch, "E42.28.0.23", {"center": v(-306.1, -330) * mm, "radius": 4.5 * mm});
            skCircle(sketch, "E42.28.0.24", {"center": v(-336.1, -315) * mm, "radius": 4.5 * mm});
            skCircle(sketch, "E42.28.0.25", {"center": v(-336.1, -345) * mm, "radius": 4.5 * mm});
            skCircle(sketch, "E42.28.0.26", {"center": v(-306.1, -360) * mm, "radius": 4.5 * mm});
            skLineSegment(sketch, "E42.29.0.0", {"start": v(-366.1, -360) * mm, "end": v(-366.1, -330) * mm, "construction": true});
            skCircle(sketch, "E42.29.0.1", {"center": v(-366.1, -60) * mm, "radius": 4.5 * mm});
            skCircle(sketch, "E42.29.0.2", {"center": v(-366.1, -30) * mm, "radius": 4.5 * mm});
            skCircle(sketch, "E42.29.0.3", {"center": v(-366.1, 0) * mm, "radius": 4.5 * mm});
            skCircle(sketch, "E42.29.0.4", {"center": v(-366.1, -240) * mm, "radius": 4.5 * mm});
            skCircle(sketch, "E42.29.0.5", {"center": v(-366.1, -300) * mm, "radius": 4.5 * mm});
            skCircle(sketch, "E42.29.0.6", {"center": v(-396.1, -75) * mm, "radius": 4.5 * mm});
            skCircle(sketch, "E42.29.0.7", {"center": v(-396.1, -285) * mm, "radius": 4.5 * mm});
            skCircle(sketch, "E42.29.0.8", {"center": v(-396.1, -105) * mm, "radius": 4.5 * mm});
            skCircle(sketch, "E42.29.0.9", {"center": v(-396.1, -255) * mm, "radius": 4.5 * mm});
            skCircle(sketch, "E42.29.0.10", {"center": v(-396.1, -195) * mm, "radius": 4.5 * mm});
            skLineSegment(sketch, "E42.29.0.11", {"start": v(-396.1, -345) * mm, "end": v(-396.1, -315) * mm, "construction": true});
            skCircle(sketch, "E42.29.0.12", {"center": v(-396.1, -15) * mm, "radius": 4.5 * mm});
            skCircle(sketch, "E42.29.0.13", {"center": v(-366.1, -120) * mm, "radius": 4.5 * mm});
            skCircle(sketch, "E42.29.0.14", {"center": v(-396.1, -45) * mm, "radius": 4.5 * mm});
            skCircle(sketch, "E42.29.0.15", {"center": v(-366.1, -180) * mm, "radius": 4.5 * mm});
            skCircle(sketch, "E42.29.0.16", {"center": v(-366.1, -150) * mm, "radius": 4.5 * mm});
            skCircle(sketch, "E42.29.0.17", {"center": v(-366.1, -90) * mm, "radius": 4.5 * mm});
            skCircle(sketch, "E42.29.0.18", {"center": v(-396.1, -135) * mm, "radius": 4.5 * mm});
            skCircle(sketch, "E42.29.0.19", {"center": v(-396.1, -225) * mm, "radius": 4.5 * mm});
            skCircle(sketch, "E42.29.0.20", {"center": v(-366.1, -210) * mm, "radius": 4.5 * mm});
            skCircle(sketch, "E42.29.0.21", {"center": v(-396.1, -165) * mm, "radius": 4.5 * mm});
            skCircle(sketch, "E42.29.0.22", {"center": v(-366.1, -270) * mm, "radius": 4.5 * mm});
            skCircle(sketch, "E42.29.0.23", {"center": v(-366.1, -330) * mm, "radius": 4.5 * mm});
            skCircle(sketch, "E42.29.0.24", {"center": v(-396.1, -315) * mm, "radius": 4.5 * mm});
            skCircle(sketch, "E42.29.0.25", {"center": v(-396.1, -345) * mm, "radius": 4.5 * mm});
            skCircle(sketch, "E42.29.0.26", {"center": v(-366.1, -360) * mm, "radius": 4.5 * mm});
            skLineSegment(sketch, "E42.30.0.0", {"start": v(-426.1, -360) * mm, "end": v(-426.1, -330) * mm, "construction": true});
            skCircle(sketch, "E42.30.0.1", {"center": v(-426.1, -60) * mm, "radius": 4.5 * mm});
            skCircle(sketch, "E42.30.0.2", {"center": v(-426.1, -30) * mm, "radius": 4.5 * mm});
            skCircle(sketch, "E42.30.0.3", {"center": v(-426.1, 0) * mm, "radius": 4.5 * mm});
            skCircle(sketch, "E42.30.0.4", {"center": v(-426.1, -240) * mm, "radius": 4.5 * mm});
            skCircle(sketch, "E42.30.0.5", {"center": v(-426.1, -300) * mm, "radius": 4.5 * mm});
            skCircle(sketch, "E42.30.0.6", {"center": v(-456.1, -75) * mm, "radius": 4.5 * mm});
            skCircle(sketch, "E42.30.0.7", {"center": v(-456.1, -285) * mm, "radius": 4.5 * mm});
            skCircle(sketch, "E42.30.0.8", {"center": v(-456.1, -105) * mm, "radius": 4.5 * mm});
            skCircle(sketch, "E42.30.0.9", {"center": v(-456.1, -255) * mm, "radius": 4.5 * mm});
            skCircle(sketch, "E42.30.0.10", {"center": v(-456.1, -195) * mm, "radius": 4.5 * mm});
            skLineSegment(sketch, "E42.30.0.11", {"start": v(-456.1, -345) * mm, "end": v(-456.1, -315) * mm, "construction": true});
            skCircle(sketch, "E42.30.0.12", {"center": v(-456.1, -15) * mm, "radius": 4.5 * mm});
            skCircle(sketch, "E42.30.0.13", {"center": v(-426.1, -120) * mm, "radius": 4.5 * mm});
            skCircle(sketch, "E42.30.0.14", {"center": v(-456.1, -45) * mm, "radius": 4.5 * mm});
            skCircle(sketch, "E42.30.0.15", {"center": v(-426.1, -180) * mm, "radius": 4.5 * mm});
            skCircle(sketch, "E42.30.0.16", {"center": v(-426.1, -150) * mm, "radius": 4.5 * mm});
            skCircle(sketch, "E42.30.0.17", {"center": v(-426.1, -90) * mm, "radius": 4.5 * mm});
            skCircle(sketch, "E42.30.0.18", {"center": v(-456.1, -135) * mm, "radius": 4.5 * mm});
            skCircle(sketch, "E42.30.0.19", {"center": v(-456.1, -225) * mm, "radius": 4.5 * mm});
            skCircle(sketch, "E42.30.0.20", {"center": v(-426.1, -210) * mm, "radius": 4.5 * mm});
            skCircle(sketch, "E42.30.0.21", {"center": v(-456.1, -165) * mm, "radius": 4.5 * mm});
            skCircle(sketch, "E42.30.0.22", {"center": v(-426.1, -270) * mm, "radius": 4.5 * mm});
            skCircle(sketch, "E42.30.0.23", {"center": v(-426.1, -330) * mm, "radius": 4.5 * mm});
            skCircle(sketch, "E42.30.0.24", {"center": v(-456.1, -315) * mm, "radius": 4.5 * mm});
            skCircle(sketch, "E42.30.0.25", {"center": v(-456.1, -345) * mm, "radius": 4.5 * mm});
            skCircle(sketch, "E42.30.0.26", {"center": v(-426.1, -360) * mm, "radius": 4.5 * mm});
            skLineSegment(sketch, "E42.31.0.0", {"start": v(-486.1, -360) * mm, "end": v(-486.1, -330) * mm, "construction": true});
            skCircle(sketch, "E42.31.0.1", {"center": v(-486.1, -60) * mm, "radius": 4.5 * mm});
            skCircle(sketch, "E42.31.0.2", {"center": v(-486.1, -30) * mm, "radius": 4.5 * mm});
            skCircle(sketch, "E42.31.0.3", {"center": v(-486.1, 0) * mm, "radius": 4.5 * mm});
            skCircle(sketch, "E42.31.0.4", {"center": v(-486.1, -240) * mm, "radius": 4.5 * mm});
            skCircle(sketch, "E42.31.0.5", {"center": v(-486.1, -300) * mm, "radius": 4.5 * mm});
            skCircle(sketch, "E42.31.0.6", {"center": v(-516.1, -75) * mm, "radius": 4.5 * mm});
            skCircle(sketch, "E42.31.0.7", {"center": v(-516.1, -285) * mm, "radius": 4.5 * mm});
            skCircle(sketch, "E42.31.0.8", {"center": v(-516.1, -105) * mm, "radius": 4.5 * mm});
            skCircle(sketch, "E42.31.0.9", {"center": v(-516.1, -255) * mm, "radius": 4.5 * mm});
            skCircle(sketch, "E42.31.0.10", {"center": v(-516.1, -195) * mm, "radius": 4.5 * mm});
            skLineSegment(sketch, "E42.31.0.11", {"start": v(-516.1, -345) * mm, "end": v(-516.1, -315) * mm, "construction": true});
            skCircle(sketch, "E42.31.0.12", {"center": v(-516.1, -15) * mm, "radius": 4.5 * mm});
            skCircle(sketch, "E42.31.0.13", {"center": v(-486.1, -120) * mm, "radius": 4.5 * mm});
            skCircle(sketch, "E42.31.0.14", {"center": v(-516.1, -45) * mm, "radius": 4.5 * mm});
            skCircle(sketch, "E42.31.0.15", {"center": v(-486.1, -180) * mm, "radius": 4.5 * mm});
            skCircle(sketch, "E42.31.0.16", {"center": v(-486.1, -150) * mm, "radius": 4.5 * mm});
            skCircle(sketch, "E42.31.0.17", {"center": v(-486.1, -90) * mm, "radius": 4.5 * mm});
            skCircle(sketch, "E42.31.0.18", {"center": v(-516.1, -135) * mm, "radius": 4.5 * mm});
            skCircle(sketch, "E42.31.0.19", {"center": v(-516.1, -225) * mm, "radius": 4.5 * mm});
            skCircle(sketch, "E42.31.0.20", {"center": v(-486.1, -210) * mm, "radius": 4.5 * mm});
            skCircle(sketch, "E42.31.0.21", {"center": v(-516.1, -165) * mm, "radius": 4.5 * mm});
            skCircle(sketch, "E42.31.0.22", {"center": v(-486.1, -270) * mm, "radius": 4.5 * mm});
            skCircle(sketch, "E42.31.0.23", {"center": v(-486.1, -330) * mm, "radius": 4.5 * mm});
            skCircle(sketch, "E42.31.0.24", {"center": v(-516.1, -315) * mm, "radius": 4.5 * mm});
            skCircle(sketch, "E42.31.0.25", {"center": v(-516.1, -345) * mm, "radius": 4.5 * mm});
            skCircle(sketch, "E42.31.0.26", {"center": v(-486.1, -360) * mm, "radius": 4.5 * mm});
            skLineSegment(sketch, "E42.32.0.0", {"start": v(-546.1, -360) * mm, "end": v(-546.1, -330) * mm, "construction": true});
            skCircle(sketch, "E42.32.0.1", {"center": v(-546.1, -60) * mm, "radius": 4.5 * mm});
            skCircle(sketch, "E42.32.0.2", {"center": v(-546.1, -30) * mm, "radius": 4.5 * mm});
            skCircle(sketch, "E42.32.0.3", {"center": v(-546.1, 0) * mm, "radius": 4.5 * mm});
            skCircle(sketch, "E42.32.0.4", {"center": v(-546.1, -240) * mm, "radius": 4.5 * mm});
            skCircle(sketch, "E42.32.0.5", {"center": v(-546.1, -300) * mm, "radius": 4.5 * mm});
            skCircle(sketch, "E42.32.0.6", {"center": v(-576.1, -75) * mm, "radius": 4.5 * mm});
            skCircle(sketch, "E42.32.0.7", {"center": v(-576.1, -285) * mm, "radius": 4.5 * mm});
            skCircle(sketch, "E42.32.0.8", {"center": v(-576.1, -105) * mm, "radius": 4.5 * mm});
            skCircle(sketch, "E42.32.0.9", {"center": v(-576.1, -255) * mm, "radius": 4.5 * mm});
            skCircle(sketch, "E42.32.0.10", {"center": v(-576.1, -195) * mm, "radius": 4.5 * mm});
            skLineSegment(sketch, "E42.32.0.11", {"start": v(-576.1, -345) * mm, "end": v(-576.1, -315) * mm, "construction": true});
            skCircle(sketch, "E42.32.0.12", {"center": v(-576.1, -15) * mm, "radius": 4.5 * mm});
            skCircle(sketch, "E42.32.0.13", {"center": v(-546.1, -120) * mm, "radius": 4.5 * mm});
            skCircle(sketch, "E42.32.0.14", {"center": v(-576.1, -45) * mm, "radius": 4.5 * mm});
            skCircle(sketch, "E42.32.0.15", {"center": v(-546.1, -180) * mm, "radius": 4.5 * mm});
            skCircle(sketch, "E42.32.0.16", {"center": v(-546.1, -150) * mm, "radius": 4.5 * mm});
            skCircle(sketch, "E42.32.0.17", {"center": v(-546.1, -90) * mm, "radius": 4.5 * mm});
            skCircle(sketch, "E42.32.0.18", {"center": v(-576.1, -135) * mm, "radius": 4.5 * mm});
            skCircle(sketch, "E42.32.0.19", {"center": v(-576.1, -225) * mm, "radius": 4.5 * mm});
            skCircle(sketch, "E42.32.0.20", {"center": v(-546.1, -210) * mm, "radius": 4.5 * mm});
            skCircle(sketch, "E42.32.0.21", {"center": v(-576.1, -165) * mm, "radius": 4.5 * mm});
            skCircle(sketch, "E42.32.0.22", {"center": v(-546.1, -270) * mm, "radius": 4.5 * mm});
            skCircle(sketch, "E42.32.0.23", {"center": v(-546.1, -330) * mm, "radius": 4.5 * mm});
            skCircle(sketch, "E42.32.0.24", {"center": v(-576.1, -315) * mm, "radius": 4.5 * mm});
            skCircle(sketch, "E42.32.0.25", {"center": v(-576.1, -345) * mm, "radius": 4.5 * mm});
            skCircle(sketch, "E42.32.0.26", {"center": v(-546.1, -360) * mm, "radius": 4.5 * mm});
            skLineSegment(sketch, "E42.direction1", {"start": v(1343.9, -345) * mm, "end": v(1283.9, -345) * mm, "construction": true});
            skLineSegment(sketch, "E43", {"start": v(-576.1, -345) * mm, "end": v(-615.06, -345) * mm, "construction": true});
            skLineSegment(sketch, "E44", {"start": v(1373.9, -330) * mm, "end": v(1412.87, -330) * mm, "construction": true});
            skCircle(sketch, "E45.MirrorC", {"center": v(1343.9, 345) * mm, "radius": 4.5 * mm});
            skLineSegment(sketch, "E46.MirrorCS", {"start": v(1343.9, 345) * mm, "end": v(1283.9, 345) * mm, "construction": true});
            skLineSegment(sketch, "E47.MirrorCS", {"start": v(1373.9, 360) * mm, "end": v(1373.9, 330) * mm, "construction": true});
            skCircle(sketch, "E48.MirrorC", {"center": v(1373.9, 360) * mm, "radius": 4.5 * mm});
            skCircle(sketch, "E49.MirrorC", {"center": v(1373.9, 330) * mm, "radius": 4.5 * mm});
            skCircle(sketch, "E50.MirrorC", {"center": v(-576.1, 345) * mm, "radius": 4.5 * mm});
            skCircle(sketch, "E51.MirrorC", {"center": v(1283.9, 345) * mm, "radius": 4.5 * mm});
            skCircle(sketch, "E52.MirrorC", {"center": v(653.9, 330) * mm, "radius": 4.5 * mm});
            skCircle(sketch, "E53.MirrorC", {"center": v(-546.1, 360) * mm, "radius": 4.5 * mm});
            skCircle(sketch, "E54.MirrorC", {"center": v(23.9, 315) * mm, "radius": 4.5 * mm});
            skCircle(sketch, "E55.MirrorC", {"center": v(203.9, 345) * mm, "radius": 4.5 * mm});
            skLineSegment(sketch, "E56.MirrorCS", {"start": v(1313.9, 360) * mm, "end": v(1313.9, 330) * mm, "construction": true});
            skLineSegment(sketch, "E57.MirrorCS", {"start": v(1343.9, 345) * mm, "end": v(1343.9, 315) * mm, "construction": true});
            skLineSegment(sketch, "E58.MirrorCS", {"start": v(-576.1, 345) * mm, "end": v(-576.1, 315) * mm, "construction": true});
            skCircle(sketch, "E59.MirrorC", {"center": v(1193.9, 360) * mm, "radius": 4.5 * mm});
            skCircle(sketch, "E60.MirrorC", {"center": v(413.9, 360) * mm, "radius": 4.5 * mm});
            skCircle(sketch, "E61.MirrorC", {"center": v(1163.9, 345) * mm, "radius": 4.5 * mm});
            skCircle(sketch, "E62.MirrorC", {"center": v(-486.1, 330) * mm, "radius": 4.5 * mm});
            skCircle(sketch, "E63.MirrorC", {"center": v(-126.1, 330) * mm, "radius": 4.5 * mm});
            skCircle(sketch, "E64.MirrorC", {"center": v(1013.9, 360) * mm, "radius": 4.5 * mm});
            skCircle(sketch, "E65.MirrorC", {"center": v(803.9, 345) * mm, "radius": 4.5 * mm});
            skCircle(sketch, "E66.MirrorC", {"center": v(473.9, 330) * mm, "radius": 4.5 * mm});
            skLineSegment(sketch, "E67.MirrorCS", {"start": v(-426.1, 360) * mm, "end": v(-426.1, 330) * mm, "construction": true});
            skLineSegment(sketch, "E68.MirrorCS", {"start": v(-396.1, 345) * mm, "end": v(-396.1, 315) * mm, "construction": true});
            skCircle(sketch, "E69.MirrorC", {"center": v(623.9, 315) * mm, "radius": 4.5 * mm});
            skCircle(sketch, "E70.MirrorC", {"center": v(983.9, 345) * mm, "radius": 4.5 * mm});
            skCircle(sketch, "E71.MirrorC", {"center": v(593.9, 360) * mm, "radius": 4.5 * mm});
            skLineSegment(sketch, "E72.MirrorCS", {"start": v(743.9, 345) * mm, "end": v(743.9, 315) * mm, "construction": true});
            skLineSegment(sketch, "E73.MirrorCS", {"start": v(713.9, 360) * mm, "end": v(713.9, 330) * mm, "construction": true});
            skLineSegment(sketch, "E74.MirrorCS", {"start": v(173.9, 360) * mm, "end": v(173.9, 330) * mm, "construction": true});
            skCircle(sketch, "E75.MirrorC", {"center": v(1013.9, 330) * mm, "radius": 4.5 * mm});
            skCircle(sketch, "E76.MirrorC", {"center": v(-366.1, 360) * mm, "radius": 4.5 * mm});
            skLineSegment(sketch, "E77.MirrorCS", {"start": v(-216.1, 345) * mm, "end": v(-216.1, 315) * mm, "construction": true});
            skLineSegment(sketch, "E78.MirrorCS", {"start": v(-246.1, 360) * mm, "end": v(-246.1, 330) * mm, "construction": true});
            skCircle(sketch, "E79.MirrorC", {"center": v(53.9, 330) * mm, "radius": 4.5 * mm});
            skCircle(sketch, "E80.MirrorC", {"center": v(1163.9, 315) * mm, "radius": 4.5 * mm});
            skCircle(sketch, "E81.MirrorC", {"center": v(383.9, 315) * mm, "radius": 4.5 * mm});
            skCircle(sketch, "E82.MirrorC", {"center": v(563.9, 345) * mm, "radius": 4.5 * mm});
            skCircle(sketch, "E83.MirrorC", {"center": v(773.9, 360) * mm, "radius": 4.5 * mm});
            skLineSegment(sketch, "E84.MirrorCS", {"start": v(893.9, 360) * mm, "end": v(893.9, 330) * mm, "construction": true});
            skLineSegment(sketch, "E85.MirrorCS", {"start": v(923.9, 345) * mm, "end": v(923.9, 315) * mm, "construction": true});
            skCircle(sketch, "E86.MirrorC", {"center": v(1193.9, 330) * mm, "radius": 4.5 * mm});
            skCircle(sketch, "E87.MirrorC", {"center": v(-396.1, 345) * mm, "radius": 4.5 * mm});
            skCircle(sketch, "E88.MirrorC", {"center": v(-186.1, 360) * mm, "radius": 4.5 * mm});
            skLineSegment(sketch, "E89.MirrorCS", {"start": v(-36.1, 345) * mm, "end": v(-36.1, 315) * mm, "construction": true});
            skLineSegment(sketch, "E90.MirrorCS", {"start": v(-66.1, 360) * mm, "end": v(-66.1, 330) * mm, "construction": true});
            skCircle(sketch, "E91.MirrorC", {"center": v(233.9, 330) * mm, "radius": 4.5 * mm});
            skCircle(sketch, "E92.MirrorC", {"center": v(-576.1, 315) * mm, "radius": 4.5 * mm});
            skLineSegment(sketch, "E93.MirrorCS", {"start": v(203.9, 345) * mm, "end": v(203.9, 315) * mm, "construction": true});
            skCircle(sketch, "E94.MirrorC", {"center": v(563.9, 315) * mm, "radius": 4.5 * mm});
            skCircle(sketch, "E95.MirrorC", {"center": v(743.9, 345) * mm, "radius": 4.5 * mm});
            skCircle(sketch, "E96.MirrorC", {"center": v(953.9, 360) * mm, "radius": 4.5 * mm});
            skCircle(sketch, "E97.MirrorC", {"center": v(623.9, 345) * mm, "radius": 4.5 * mm});
            skLineSegment(sketch, "E98.MirrorCS", {"start": v(1103.9, 345) * mm, "end": v(1103.9, 315) * mm, "construction": true});
            skLineSegment(sketch, "E99.MirrorCS", {"start": v(1073.9, 360) * mm, "end": v(1073.9, 330) * mm, "construction": true});
            skCircle(sketch, "E100.MirrorC", {"center": v(-396.1, 315) * mm, "radius": 4.5 * mm});
            skCircle(sketch, "E101.MirrorC", {"center": v(-216.1, 345) * mm, "radius": 4.5 * mm});
            skCircle(sketch, "E102.MirrorC", {"center": v(-6.1, 360) * mm, "radius": 4.5 * mm});
            skLineSegment(sketch, "E103.MirrorCS", {"start": v(113.9, 360) * mm, "end": v(113.9, 330) * mm, "construction": true});
            skLineSegment(sketch, "E104.MirrorCS", {"start": v(143.9, 345) * mm, "end": v(143.9, 315) * mm, "construction": true});
            skCircle(sketch, "E105.MirrorC", {"center": v(413.9, 330) * mm, "radius": 4.5 * mm});
            skCircle(sketch, "E106.MirrorC", {"center": v(-546.1, 330) * mm, "radius": 4.5 * mm});
            skCircle(sketch, "E107.MirrorC", {"center": v(593.9, 330) * mm, "radius": 4.5 * mm});
            skCircle(sketch, "E108.MirrorC", {"center": v(743.9, 315) * mm, "radius": 4.5 * mm});
            skCircle(sketch, "E109.MirrorC", {"center": v(923.9, 345) * mm, "radius": 4.5 * mm});
            skCircle(sketch, "E110.MirrorC", {"center": v(1133.9, 360) * mm, "radius": 4.5 * mm});
            skLineSegment(sketch, "E111.MirrorCS", {"start": v(1283.9, 345) * mm, "end": v(1283.9, 315) * mm, "construction": true});
            skLineSegment(sketch, "E112.MirrorCS", {"start": v(1253.9, 360) * mm, "end": v(1253.9, 330) * mm, "construction": true});
            skCircle(sketch, "E113.MirrorC", {"center": v(-366.1, 330) * mm, "radius": 4.5 * mm});
            skCircle(sketch, "E114.MirrorC", {"center": v(-216.1, 315) * mm, "radius": 4.5 * mm});
            skCircle(sketch, "E115.MirrorC", {"center": v(-36.1, 345) * mm, "radius": 4.5 * mm});
            skCircle(sketch, "E116.MirrorC", {"center": v(173.9, 360) * mm, "radius": 4.5 * mm});
            skLineSegment(sketch, "E117.MirrorCS", {"start": v(323.9, 345) * mm, "end": v(323.9, 315) * mm, "construction": true});
            skCircle(sketch, "E118.MirrorC", {"center": v(833.9, 360) * mm, "radius": 4.5 * mm});
            skLineSegment(sketch, "E119.MirrorCS", {"start": v(-456.1, 345) * mm, "end": v(-456.1, 315) * mm, "construction": true});
            skCircle(sketch, "E120.MirrorC", {"center": v(-186.1, 330) * mm, "radius": 4.5 * mm});
            skCircle(sketch, "E121.MirrorC", {"center": v(773.9, 330) * mm, "radius": 4.5 * mm});
            skCircle(sketch, "E122.MirrorC", {"center": v(923.9, 315) * mm, "radius": 4.5 * mm});
            skCircle(sketch, "E123.MirrorC", {"center": v(1103.9, 345) * mm, "radius": 4.5 * mm});
            skCircle(sketch, "E124.MirrorC", {"center": v(1313.9, 360) * mm, "radius": 4.5 * mm});
            skCircle(sketch, "E125.MirrorC", {"center": v(-36.1, 315) * mm, "radius": 4.5 * mm});
            skCircle(sketch, "E126.MirrorC", {"center": v(143.9, 345) * mm, "radius": 4.5 * mm});
            skCircle(sketch, "E127.MirrorC", {"center": v(353.9, 360) * mm, "radius": 4.5 * mm});
            skLineSegment(sketch, "E128.MirrorCS", {"start": v(503.9, 345) * mm, "end": v(503.9, 315) * mm, "construction": true});
            skLineSegment(sketch, "E129.MirrorCS", {"start": v(473.9, 360) * mm, "end": v(473.9, 330) * mm, "construction": true});
            skLineSegment(sketch, "E130.MirrorCS", {"start": v(-306.1, 360) * mm, "end": v(-306.1, 330) * mm, "construction": true});
            skLineSegment(sketch, "E131.MirrorCS", {"start": v(-276.1, 345) * mm, "end": v(-276.1, 315) * mm, "construction": true});
            skLineSegment(sketch, "E132.MirrorCS", {"start": v(-486.1, 360) * mm, "end": v(-486.1, 330) * mm, "construction": true});
            skCircle(sketch, "E133.MirrorC", {"center": v(-336.1, 315) * mm, "radius": 4.5 * mm});
            skCircle(sketch, "E134.MirrorC", {"center": v(953.9, 330) * mm, "radius": 4.5 * mm});
            skCircle(sketch, "E135.MirrorC", {"center": v(1103.9, 315) * mm, "radius": 4.5 * mm});
            skCircle(sketch, "E136.MirrorC", {"center": v(-426.1, 360) * mm, "radius": 4.5 * mm});
            skCircle(sketch, "E137.MirrorC", {"center": v(-6.1, 330) * mm, "radius": 4.5 * mm});
            skCircle(sketch, "E138.MirrorC", {"center": v(143.9, 315) * mm, "radius": 4.5 * mm});
            skCircle(sketch, "E139.MirrorC", {"center": v(323.9, 345) * mm, "radius": 4.5 * mm});
            skCircle(sketch, "E140.MirrorC", {"center": v(533.9, 360) * mm, "radius": 4.5 * mm});
            skLineSegment(sketch, "E141.MirrorCS", {"start": v(683.9, 345) * mm, "end": v(683.9, 315) * mm, "construction": true});
            skLineSegment(sketch, "E142.MirrorCS", {"start": v(653.9, 360) * mm, "end": v(653.9, 330) * mm, "construction": true});
            skCircle(sketch, "E143.MirrorC", {"center": v(-246.1, 360) * mm, "radius": 4.5 * mm});
            skLineSegment(sketch, "E144.MirrorCS", {"start": v(-126.1, 360) * mm, "end": v(-126.1, 330) * mm, "construction": true});
            skLineSegment(sketch, "E145.MirrorCS", {"start": v(-96.1, 345) * mm, "end": v(-96.1, 315) * mm, "construction": true});
            skCircle(sketch, "E146.MirrorC", {"center": v(1133.9, 330) * mm, "radius": 4.5 * mm});
            skCircle(sketch, "E147.MirrorC", {"center": v(1283.9, 315) * mm, "radius": 4.5 * mm});
            skCircle(sketch, "E148.MirrorC", {"center": v(-456.1, 345) * mm, "radius": 4.5 * mm});
            skCircle(sketch, "E149.MirrorC", {"center": v(173.9, 330) * mm, "radius": 4.5 * mm});
            skCircle(sketch, "E150.MirrorC", {"center": v(323.9, 315) * mm, "radius": 4.5 * mm});
            skCircle(sketch, "E151.MirrorC", {"center": v(503.9, 345) * mm, "radius": 4.5 * mm});
            skCircle(sketch, "E152.MirrorC", {"center": v(713.9, 360) * mm, "radius": 4.5 * mm});
            skLineSegment(sketch, "E153.MirrorCS", {"start": v(833.9, 360) * mm, "end": v(833.9, 330) * mm, "construction": true});
            skLineSegment(sketch, "E154.MirrorCS", {"start": v(863.9, 345) * mm, "end": v(863.9, 315) * mm, "construction": true});
            skCircle(sketch, "E155.MirrorC", {"center": v(-276.1, 345) * mm, "radius": 4.5 * mm});
            skCircle(sketch, "E156.MirrorC", {"center": v(-66.1, 360) * mm, "radius": 4.5 * mm});
            skLineSegment(sketch, "E157.MirrorCS", {"start": v(53.9, 360) * mm, "end": v(53.9, 330) * mm, "construction": true});
            skLineSegment(sketch, "E158.MirrorCS", {"start": v(83.9, 345) * mm, "end": v(83.9, 315) * mm, "construction": true});
            skCircle(sketch, "E159.MirrorC", {"center": v(1313.9, 330) * mm, "radius": 4.5 * mm});
            skCircle(sketch, "E160.MirrorC", {"center": v(-456.1, 315) * mm, "radius": 4.5 * mm});
            skCircle(sketch, "E161.MirrorC", {"center": v(353.9, 330) * mm, "radius": 4.5 * mm});
            skCircle(sketch, "E162.MirrorC", {"center": v(503.9, 315) * mm, "radius": 4.5 * mm});
            skCircle(sketch, "E163.MirrorC", {"center": v(683.9, 345) * mm, "radius": 4.5 * mm});
            skCircle(sketch, "E164.MirrorC", {"center": v(893.9, 360) * mm, "radius": 4.5 * mm});
            skLineSegment(sketch, "E165.MirrorCS", {"start": v(1043.9, 345) * mm, "end": v(1043.9, 315) * mm, "construction": true});
            skLineSegment(sketch, "E166.MirrorCS", {"start": v(1013.9, 360) * mm, "end": v(1013.9, 330) * mm, "construction": true});
            skCircle(sketch, "E167.MirrorC", {"center": v(-276.1, 315) * mm, "radius": 4.5 * mm});
            skCircle(sketch, "E168.MirrorC", {"center": v(-96.1, 345) * mm, "radius": 4.5 * mm});
            skCircle(sketch, "E169.MirrorC", {"center": v(113.9, 360) * mm, "radius": 4.5 * mm});
            skLineSegment(sketch, "E170.MirrorCS", {"start": v(263.9, 345) * mm, "end": v(263.9, 315) * mm, "construction": true});
            skLineSegment(sketch, "E171.MirrorCS", {"start": v(233.9, 360) * mm, "end": v(233.9, 330) * mm, "construction": true});
            skCircle(sketch, "E172.MirrorC", {"center": v(-426.1, 330) * mm, "radius": 4.5 * mm});
            skCircle(sketch, "E173.MirrorC", {"center": v(533.9, 330) * mm, "radius": 4.5 * mm});
            skCircle(sketch, "E174.MirrorC", {"center": v(683.9, 315) * mm, "radius": 4.5 * mm});
            skCircle(sketch, "E175.MirrorC", {"center": v(863.9, 345) * mm, "radius": 4.5 * mm});
            skCircle(sketch, "E176.MirrorC", {"center": v(1073.9, 360) * mm, "radius": 4.5 * mm});
            skLineSegment(sketch, "E177.MirrorCS", {"start": v(1223.9, 345) * mm, "end": v(1223.9, 315) * mm, "construction": true});
            skLineSegment(sketch, "E178.MirrorCS", {"start": v(293.9, 360) * mm, "end": v(293.9, 330) * mm, "construction": true});
            skLineSegment(sketch, "E179.MirrorCS", {"start": v(1193.9, 360) * mm, "end": v(1193.9, 330) * mm, "construction": true});
            skCircle(sketch, "E180.MirrorC", {"center": v(-156.1, 345) * mm, "radius": 4.5 * mm});
            skCircle(sketch, "E181.MirrorC", {"center": v(-246.1, 330) * mm, "radius": 4.5 * mm});
            skCircle(sketch, "E182.MirrorC", {"center": v(-96.1, 315) * mm, "radius": 4.5 * mm});
            skCircle(sketch, "E183.MirrorC", {"center": v(83.9, 345) * mm, "radius": 4.5 * mm});
            skLineSegment(sketch, "E184.MirrorCS", {"start": v(443.9, 345) * mm, "end": v(443.9, 315) * mm, "construction": true});
            skCircle(sketch, "E185.MirrorC", {"center": v(293.9, 360) * mm, "radius": 4.5 * mm});
            skLineSegment(sketch, "E186.MirrorCS", {"start": v(413.9, 360) * mm, "end": v(413.9, 330) * mm, "construction": true});
            skLineSegment(sketch, "E187.MirrorCS", {"start": v(-516.1, 345) * mm, "end": v(-516.1, 315) * mm, "construction": true});
            skLineSegment(sketch, "E188.MirrorCS", {"start": v(-546.1, 360) * mm, "end": v(-546.1, 330) * mm, "construction": true});
            skCircle(sketch, "E189.MirrorC", {"center": v(713.9, 330) * mm, "radius": 4.5 * mm});
            skCircle(sketch, "E190.MirrorC", {"center": v(863.9, 315) * mm, "radius": 4.5 * mm});
            skCircle(sketch, "E191.MirrorC", {"center": v(53.9, 360) * mm, "radius": 4.5 * mm});
            skCircle(sketch, "E192.MirrorC", {"center": v(1043.9, 345) * mm, "radius": 4.5 * mm});
            skCircle(sketch, "E193.MirrorC", {"center": v(1253.9, 360) * mm, "radius": 4.5 * mm});
            skLineSegment(sketch, "E194.MirrorCS", {"start": v(-366.1, 360) * mm, "end": v(-366.1, 330) * mm, "construction": true});
            skLineSegment(sketch, "E195.MirrorCS", {"start": v(-336.1, 345) * mm, "end": v(-336.1, 315) * mm, "construction": true});
            skCircle(sketch, "E196.MirrorC", {"center": v(-66.1, 330) * mm, "radius": 4.5 * mm});
            skCircle(sketch, "E197.MirrorC", {"center": v(83.9, 315) * mm, "radius": 4.5 * mm});
            skCircle(sketch, "E198.MirrorC", {"center": v(263.9, 345) * mm, "radius": 4.5 * mm});
            skCircle(sketch, "E199.MirrorC", {"center": v(473.9, 360) * mm, "radius": 4.5 * mm});
            skCircle(sketch, "E200.MirrorC", {"center": v(-486.1, 360) * mm, "radius": 4.5 * mm});
            skLineSegment(sketch, "E201.MirrorCS", {"start": v(623.9, 345) * mm, "end": v(623.9, 315) * mm, "construction": true});
            skLineSegment(sketch, "E202.MirrorCS", {"start": v(593.9, 360) * mm, "end": v(593.9, 330) * mm, "construction": true});
            skCircle(sketch, "E203.MirrorC", {"center": v(893.9, 330) * mm, "radius": 4.5 * mm});
            skCircle(sketch, "E204.MirrorC", {"center": v(1043.9, 315) * mm, "radius": 4.5 * mm});
            skCircle(sketch, "E205.MirrorC", {"center": v(1223.9, 345) * mm, "radius": 4.5 * mm});
            skCircle(sketch, "E206.MirrorC", {"center": v(1343.9, 315) * mm, "radius": 4.5 * mm});
            skLineSegment(sketch, "E207.MirrorCS", {"start": v(533.9, 360) * mm, "end": v(533.9, 330) * mm, "construction": true});
            skCircle(sketch, "E208.MirrorC", {"center": v(383.9, 345) * mm, "radius": 4.5 * mm});
            skCircle(sketch, "E209.MirrorC", {"center": v(23.9, 345) * mm, "radius": 4.5 * mm});
            skCircle(sketch, "E210.MirrorC", {"center": v(983.9, 315) * mm, "radius": 4.5 * mm});
            skLineSegment(sketch, "E211.MirrorCS", {"start": v(353.9, 360) * mm, "end": v(353.9, 330) * mm, "construction": true});
            skCircle(sketch, "E212.MirrorC", {"center": v(-156.1, 315) * mm, "radius": 4.5 * mm});
            skCircle(sketch, "E213.MirrorC", {"center": v(-306.1, 330) * mm, "radius": 4.5 * mm});
            skCircle(sketch, "E214.MirrorC", {"center": v(203.9, 315) * mm, "radius": 4.5 * mm});
            skLineSegment(sketch, "E215.MirrorCS", {"start": v(1163.9, 345) * mm, "end": v(1163.9, 315) * mm, "construction": true});
            skCircle(sketch, "E216.MirrorC", {"center": v(-516.1, 315) * mm, "radius": 4.5 * mm});
            skLineSegment(sketch, "E217.MirrorCS", {"start": v(23.9, 345) * mm, "end": v(23.9, 315) * mm, "construction": true});
            skLineSegment(sketch, "E218.MirrorCS", {"start": v(983.9, 345) * mm, "end": v(983.9, 315) * mm, "construction": true});
            skLineSegment(sketch, "E219.MirrorCS", {"start": v(953.9, 360) * mm, "end": v(953.9, 330) * mm, "construction": true});
            skCircle(sketch, "E220.MirrorC", {"center": v(-516.1, 345) * mm, "radius": 4.5 * mm});
            skCircle(sketch, "E221.MirrorC", {"center": v(-336.1, 345) * mm, "radius": 4.5 * mm});
            skCircle(sketch, "E222.MirrorC", {"center": v(653.9, 360) * mm, "radius": 4.5 * mm});
            skCircle(sketch, "E223.MirrorC", {"center": v(263.9, 315) * mm, "radius": 4.5 * mm});
            skCircle(sketch, "E224.MirrorC", {"center": v(443.9, 345) * mm, "radius": 4.5 * mm});
            skLineSegment(sketch, "E225.MirrorCS", {"start": v(-186.1, 360) * mm, "end": v(-186.1, 330) * mm, "construction": true});
            skCircle(sketch, "E226.MirrorC", {"center": v(113.9, 330) * mm, "radius": 4.5 * mm});
            skLineSegment(sketch, "E227.MirrorCS", {"start": v(-156.1, 345) * mm, "end": v(-156.1, 315) * mm, "construction": true});
            skCircle(sketch, "E228.MirrorC", {"center": v(233.9, 360) * mm, "radius": 4.5 * mm});
            skLineSegment(sketch, "E229.MirrorCS", {"start": v(383.9, 345) * mm, "end": v(383.9, 315) * mm, "construction": true});
            skCircle(sketch, "E230.MirrorC", {"center": v(833.9, 330) * mm, "radius": 4.5 * mm});
            skCircle(sketch, "E231.MirrorC", {"center": v(1223.9, 315) * mm, "radius": 4.5 * mm});
            skCircle(sketch, "E232.MirrorC", {"center": v(-126.1, 360) * mm, "radius": 4.5 * mm});
            skCircle(sketch, "E233.MirrorC", {"center": v(803.9, 315) * mm, "radius": 4.5 * mm});
            skLineSegment(sketch, "E234.MirrorCS", {"start": v(773.9, 360) * mm, "end": v(773.9, 330) * mm, "construction": true});
            skLineSegment(sketch, "E235.MirrorCS", {"start": v(803.9, 345) * mm, "end": v(803.9, 315) * mm, "construction": true});
            skCircle(sketch, "E236.MirrorC", {"center": v(1073.9, 330) * mm, "radius": 4.5 * mm});
            skLineSegment(sketch, "E237.MirrorCS", {"start": v(563.9, 345) * mm, "end": v(563.9, 315) * mm, "construction": true});
            skCircle(sketch, "E238.MirrorC", {"center": v(-306.1, 360) * mm, "radius": 4.5 * mm});
            skCircle(sketch, "E239.MirrorC", {"center": v(1253.9, 330) * mm, "radius": 4.5 * mm});
            skCircle(sketch, "E240.MirrorC", {"center": v(443.9, 315) * mm, "radius": 4.5 * mm});
            skLineSegment(sketch, "E241.MirrorCS", {"start": v(1133.9, 360) * mm, "end": v(1133.9, 330) * mm, "construction": true});
            skCircle(sketch, "E242.MirrorC", {"center": v(293.9, 330) * mm, "radius": 4.5 * mm});
            skLineSegment(sketch, "E243.MirrorCS", {"start": v(-6.1, 360) * mm, "end": v(-6.1, 330) * mm, "construction": true});
            skCircle(sketch, "E244.MirrorC", {"center": v(83.9, 165) * mm, "radius": 4.5 * mm});
            skCircle(sketch, "E245.MirrorC", {"center": v(113.9, 240) * mm, "radius": 4.5 * mm});
            skCircle(sketch, "E246.MirrorC", {"center": v(473.9, 270) * mm, "radius": 4.5 * mm});
            skCircle(sketch, "E247.MirrorC", {"center": v(443.9, 75) * mm, "radius": 4.5 * mm});
            skCircle(sketch, "E248.MirrorC", {"center": v(533.9, 90) * mm, "radius": 4.5 * mm});
            skCircle(sketch, "E249.MirrorC", {"center": v(-516.1, 75) * mm, "radius": 4.5 * mm});
            skCircle(sketch, "E250.MirrorC", {"center": v(1253.9, 240) * mm, "radius": 4.5 * mm});
            skCircle(sketch, "E251.MirrorC", {"center": v(-426.1, 60) * mm, "radius": 4.5 * mm});
            skCircle(sketch, "E252.MirrorC", {"center": v(353.9, 150) * mm, "radius": 4.5 * mm});
            skCircle(sketch, "E253.MirrorC", {"center": v(173.9, 180) * mm, "radius": 4.5 * mm});
            skCircle(sketch, "E254.MirrorC", {"center": v(203.9, 105) * mm, "radius": 4.5 * mm});
            skCircle(sketch, "E255.MirrorC", {"center": v(293.9, 240) * mm, "radius": 4.5 * mm});
            skCircle(sketch, "E256.MirrorC", {"center": v(443.9, 165) * mm, "radius": 4.5 * mm});
            skCircle(sketch, "E257.MirrorC", {"center": v(143.9, 45) * mm, "radius": 4.5 * mm});
            skCircle(sketch, "E258.MirrorC", {"center": v(383.9, 255) * mm, "radius": 4.5 * mm});
            skCircle(sketch, "E259.MirrorC", {"center": v(1313.9, 180) * mm, "radius": 4.5 * mm});
            skCircle(sketch, "E260.MirrorC", {"center": v(-156.1, 285) * mm, "radius": 4.5 * mm});
            skCircle(sketch, "E261.MirrorC", {"center": v(-66.1, 30) * mm, "radius": 4.5 * mm});
            skCircle(sketch, "E262.MirrorC", {"center": v(-516.1, 165) * mm, "radius": 4.5 * mm});
            skCircle(sketch, "E263.MirrorC", {"center": v(1133.9, 180) * mm, "radius": 4.5 * mm});
            skCircle(sketch, "E264.MirrorC", {"center": v(923.9, 45) * mm, "radius": 4.5 * mm});
            skCircle(sketch, "E265.MirrorC", {"center": v(-246.1, 60) * mm, "radius": 4.5 * mm});
            skCircle(sketch, "E266.MirrorC", {"center": v(-6.1, 120) * mm, "radius": 4.5 * mm});
            skCircle(sketch, "E267.MirrorC", {"center": v(173.9, 120) * mm, "radius": 4.5 * mm});
            skCircle(sketch, "E268.MirrorC", {"center": v(473.9, 210) * mm, "radius": 4.5 * mm});
            skCircle(sketch, "E269.MirrorC", {"center": v(503.9, 225) * mm, "radius": 4.5 * mm});
            skCircle(sketch, "E270.MirrorC", {"center": v(473.9, 300) * mm, "radius": 4.5 * mm});
            skCircle(sketch, "E271.MirrorC", {"center": v(383.9, 195) * mm, "radius": 4.5 * mm});
            skCircle(sketch, "E272.MirrorC", {"center": v(353.9, 180) * mm, "radius": 4.5 * mm});
            skCircle(sketch, "E273.MirrorC", {"center": v(203.9, 255) * mm, "radius": 4.5 * mm});
            skCircle(sketch, "E274.MirrorC", {"center": v(-426.1, 150) * mm, "radius": 4.5 * mm});
            skCircle(sketch, "E275.MirrorC", {"center": v(1253.9, 210) * mm, "radius": 4.5 * mm});
            skCircle(sketch, "E276.MirrorC", {"center": v(953.9, 120) * mm, "radius": 4.5 * mm});
            skCircle(sketch, "E277.MirrorC", {"center": v(1073.9, 240) * mm, "radius": 4.5 * mm});
            skCircle(sketch, "E278.MirrorC", {"center": v(1163.9, 255) * mm, "radius": 4.5 * mm});
            skCircle(sketch, "E279.MirrorC", {"center": v(1223.9, 165) * mm, "radius": 4.5 * mm});
            skCircle(sketch, "E280.MirrorC", {"center": v(1253.9, 300) * mm, "radius": 4.5 * mm});
            skCircle(sketch, "E281.MirrorC", {"center": v(1313.9, 150) * mm, "radius": 4.5 * mm});
            skCircle(sketch, "E282.MirrorC", {"center": v(-576.1, 195) * mm, "radius": 4.5 * mm});
            skCircle(sketch, "E283.MirrorC", {"center": v(-216.1, 15) * mm, "radius": 4.5 * mm});
            skCircle(sketch, "E284.MirrorC", {"center": v(803.9, 255) * mm, "radius": 4.5 * mm});
            skCircle(sketch, "E285.MirrorC", {"center": v(-246.1, 90) * mm, "radius": 4.5 * mm});
            skCircle(sketch, "E286.MirrorC", {"center": v(383.9, 15) * mm, "radius": 4.5 * mm});
            skCircle(sketch, "E287.MirrorC", {"center": v(443.9, 285) * mm, "radius": 4.5 * mm});
            skCircle(sketch, "E288.MirrorC", {"center": v(293.9, 270) * mm, "radius": 4.5 * mm});
            skCircle(sketch, "E289.MirrorC", {"center": v(-306.1, 270) * mm, "radius": 4.5 * mm});
            skCircle(sketch, "E290.MirrorC", {"center": v(-336.1, 75) * mm, "radius": 4.5 * mm});
            skCircle(sketch, "E291.MirrorC", {"center": v(-486.1, 300) * mm, "radius": 4.5 * mm});
            skCircle(sketch, "E292.MirrorC", {"center": v(-96.1, 135) * mm, "radius": 4.5 * mm});
            skCircle(sketch, "E293.MirrorC", {"center": v(263.9, 75) * mm, "radius": 4.5 * mm});
            skCircle(sketch, "E294.MirrorC", {"center": v(353.9, 90) * mm, "radius": 4.5 * mm});
            skCircle(sketch, "E295.MirrorC", {"center": v(1373.9, 90) * mm, "radius": 4.5 * mm});
            skCircle(sketch, "E296.MirrorC", {"center": v(1373.9, 120) * mm, "radius": 4.5 * mm});
            skCircle(sketch, "E297.MirrorC", {"center": v(1373.9, 150) * mm, "radius": 4.5 * mm});
            skCircle(sketch, "E298.MirrorC", {"center": v(-516.1, 285) * mm, "radius": 4.5 * mm});
            skCircle(sketch, "E299.MirrorC", {"center": v(503.9, 135) * mm, "radius": 4.5 * mm});
            skCircle(sketch, "E300.MirrorC", {"center": v(1373.9, 60) * mm, "radius": 4.5 * mm});
            skCircle(sketch, "E301.MirrorC", {"center": v(1163.9, 195) * mm, "radius": 4.5 * mm});
            skCircle(sketch, "E302.MirrorC", {"center": v(743.9, 45) * mm, "radius": 4.5 * mm});
            skCircle(sketch, "E303.MirrorC", {"center": v(953.9, 180) * mm, "radius": 4.5 * mm});
            skCircle(sketch, "E304.MirrorC", {"center": v(893.9, 240) * mm, "radius": 4.5 * mm});
            skCircle(sketch, "E305.MirrorC", {"center": v(623.9, 105) * mm, "radius": 4.5 * mm});
            skCircle(sketch, "E306.MirrorC", {"center": v(983.9, 195) * mm, "radius": 4.5 * mm});
            skCircle(sketch, "E307.MirrorC", {"center": v(443.9, 105) * mm, "radius": 4.5 * mm});
            skCircle(sketch, "E308.MirrorC", {"center": v(893.9, 210) * mm, "radius": 4.5 * mm});
            skCircle(sketch, "E309.MirrorC", {"center": v(983.9, 255) * mm, "radius": 4.5 * mm});
            skCircle(sketch, "E310.MirrorC", {"center": v(1103.9, 45) * mm, "radius": 4.5 * mm});
            skCircle(sketch, "E311.MirrorC", {"center": v(683.9, 225) * mm, "radius": 4.5 * mm});
            skCircle(sketch, "E312.MirrorC", {"center": v(563.9, 195) * mm, "radius": 4.5 * mm});
            skCircle(sketch, "E313.MirrorC", {"center": v(533.9, 180) * mm, "radius": 4.5 * mm});
            skCircle(sketch, "E314.MirrorC", {"center": v(713.9, 150) * mm, "radius": 4.5 * mm});
            skCircle(sketch, "E315.MirrorC", {"center": v(893.9, 60) * mm, "radius": 4.5 * mm});
            skCircle(sketch, "E316.MirrorC", {"center": v(653.9, 300) * mm, "radius": 4.5 * mm});
            skCircle(sketch, "E317.MirrorC", {"center": v(893.9, 90) * mm, "radius": 4.5 * mm});
            skCircle(sketch, "E318.MirrorC", {"center": v(533.9, 30) * mm, "radius": 4.5 * mm});
            skCircle(sketch, "E319.MirrorC", {"center": v(353.9, 60) * mm, "radius": 4.5 * mm});
            skCircle(sketch, "E320.MirrorC", {"center": v(173.9, 150) * mm, "radius": 4.5 * mm});
            skCircle(sketch, "E321.MirrorC", {"center": v(113.9, 300) * mm, "radius": 4.5 * mm});
            skCircle(sketch, "E322.MirrorC", {"center": v(803.9, 75) * mm, "radius": 4.5 * mm});
            skCircle(sketch, "E323.MirrorC", {"center": v(833.9, 270) * mm, "radius": 4.5 * mm});
            skCircle(sketch, "E324.MirrorC", {"center": v(1043.9, 135) * mm, "radius": 4.5 * mm});
            skCircle(sketch, "E325.MirrorC", {"center": v(983.9, 285) * mm, "radius": 4.5 * mm});
            skCircle(sketch, "E326.MirrorC", {"center": v(923.9, 15) * mm, "radius": 4.5 * mm});
            skCircle(sketch, "E327.MirrorC", {"center": v(-426.1, 180) * mm, "radius": 4.5 * mm});
            skCircle(sketch, "E328.MirrorC", {"center": v(-306.1, 300) * mm, "radius": 4.5 * mm});
            skCircle(sketch, "E329.MirrorC", {"center": v(-336.1, 165) * mm, "radius": 4.5 * mm});
            skCircle(sketch, "E330.MirrorC", {"center": v(-396.1, 195) * mm, "radius": 4.5 * mm});
            skCircle(sketch, "E331.MirrorC", {"center": v(-126.1, 270) * mm, "radius": 4.5 * mm});
            skCircle(sketch, "E332.MirrorC", {"center": v(-246.1, 150) * mm, "radius": 4.5 * mm});
            skCircle(sketch, "E333.MirrorC", {"center": v(-36.1, 15) * mm, "radius": 4.5 * mm});
            skCircle(sketch, "E334.MirrorC", {"center": v(-66.1, 60) * mm, "radius": 4.5 * mm});
            skCircle(sketch, "E335.MirrorC", {"center": v(-66.1, 90) * mm, "radius": 4.5 * mm});
            skCircle(sketch, "E336.MirrorC", {"center": v(-156.1, 75) * mm, "radius": 4.5 * mm});
            skCircle(sketch, "E337.MirrorC", {"center": v(83.9, 135) * mm, "radius": 4.5 * mm});
            skCircle(sketch, "E338.MirrorC", {"center": v(113.9, 30) * mm, "radius": 4.5 * mm});
            skCircle(sketch, "E339.MirrorC", {"center": v(23.9, 285) * mm, "radius": 4.5 * mm});
            skCircle(sketch, "E340.MirrorC", {"center": v(1373.9, 30) * mm, "radius": 4.5 * mm});
            skCircle(sketch, "E341.MirrorC", {"center": v(1373.9, 300) * mm, "radius": 4.5 * mm});
            skCircle(sketch, "E342.MirrorC", {"center": v(1373.9, 270) * mm, "radius": 4.5 * mm});
            skCircle(sketch, "E343.MirrorC", {"center": v(1373.9, 240) * mm, "radius": 4.5 * mm});
            skCircle(sketch, "E344.MirrorC", {"center": v(1373.9, 180) * mm, "radius": 4.5 * mm});
            skCircle(sketch, "E345.MirrorC", {"center": v(1373.9, 210) * mm, "radius": 4.5 * mm});
            skCircle(sketch, "E346.MirrorC", {"center": v(1163.9, 105) * mm, "radius": 4.5 * mm});
            skCircle(sketch, "E347.MirrorC", {"center": v(1133.9, 120) * mm, "radius": 4.5 * mm});
            skCircle(sketch, "E348.MirrorC", {"center": v(713.9, 240) * mm, "radius": 4.5 * mm});
            skCircle(sketch, "E349.MirrorC", {"center": v(1073.9, 30) * mm, "radius": 4.5 * mm});
            skCircle(sketch, "E350.MirrorC", {"center": v(1283.9, 45) * mm, "radius": 4.5 * mm});
            skCircle(sketch, "E351.MirrorC", {"center": v(1343.9, 15) * mm, "radius": 4.5 * mm});
            skCircle(sketch, "E352.MirrorC", {"center": v(1223.9, 225) * mm, "radius": 4.5 * mm});
            skCircle(sketch, "E353.MirrorC", {"center": v(-576.1, 255) * mm, "radius": 4.5 * mm});
            skCircle(sketch, "E354.MirrorC", {"center": v(-486.1, 240) * mm, "radius": 4.5 * mm});
            skCircle(sketch, "E355.MirrorC", {"center": v(-486.1, 210) * mm, "radius": 4.5 * mm});
            skCircle(sketch, "E356.MirrorC", {"center": v(383.9, 105) * mm, "radius": 4.5 * mm});
            skCircle(sketch, "E357.MirrorC", {"center": v(293.9, 30) * mm, "radius": 4.5 * mm});
            skCircle(sketch, "E358.MirrorC", {"center": v(443.9, 225) * mm, "radius": 4.5 * mm});
            skCircle(sketch, "E359.MirrorC", {"center": v(353.9, 120) * mm, "radius": 4.5 * mm});
            skCircle(sketch, "E360.MirrorC", {"center": v(653.9, 210) * mm, "radius": 4.5 * mm});
            skCircle(sketch, "E361.MirrorC", {"center": v(563.9, 255) * mm, "radius": 4.5 * mm});
            skCircle(sketch, "E362.MirrorC", {"center": v(503.9, 45) * mm, "radius": 4.5 * mm});
            skCircle(sketch, "E363.MirrorC", {"center": v(743.9, 195) * mm, "radius": 4.5 * mm});
            skCircle(sketch, "E364.MirrorC", {"center": v(713.9, 180) * mm, "radius": 4.5 * mm});
            skCircle(sketch, "E365.MirrorC", {"center": v(653.9, 240) * mm, "radius": 4.5 * mm});
            skCircle(sketch, "E366.MirrorC", {"center": v(893.9, 150) * mm, "radius": 4.5 * mm});
            skCircle(sketch, "E367.MirrorC", {"center": v(833.9, 300) * mm, "radius": 4.5 * mm});
            skCircle(sketch, "E368.MirrorC", {"center": v(803.9, 165) * mm, "radius": 4.5 * mm});
            skCircle(sketch, "E369.MirrorC", {"center": v(1073.9, 90) * mm, "radius": 4.5 * mm});
            skCircle(sketch, "E370.MirrorC", {"center": v(983.9, 75) * mm, "radius": 4.5 * mm});
            skCircle(sketch, "E371.MirrorC", {"center": v(1013.9, 270) * mm, "radius": 4.5 * mm});
            skCircle(sketch, "E372.MirrorC", {"center": v(1163.9, 285) * mm, "radius": 4.5 * mm});
            skCircle(sketch, "E373.MirrorC", {"center": v(1103.9, 15) * mm, "radius": 4.5 * mm});
            skCircle(sketch, "E374.MirrorC", {"center": v(1073.9, 60) * mm, "radius": 4.5 * mm});
            skCircle(sketch, "E375.MirrorC", {"center": v(-456.1, 45) * mm, "radius": 4.5 * mm});
            skCircle(sketch, "E376.MirrorC", {"center": v(-306.1, 240) * mm, "radius": 4.5 * mm});
            skCircle(sketch, "E377.MirrorC", {"center": v(-306.1, 210) * mm, "radius": 4.5 * mm});
            skCircle(sketch, "E378.MirrorC", {"center": v(-396.1, 255) * mm, "radius": 4.5 * mm});
            skCircle(sketch, "E379.MirrorC", {"center": v(-216.1, 195) * mm, "radius": 4.5 * mm});
            skCircle(sketch, "E380.MirrorC", {"center": v(-156.1, 165) * mm, "radius": 4.5 * mm});
            skCircle(sketch, "E381.MirrorC", {"center": v(-246.1, 180) * mm, "radius": 4.5 * mm});
            skCircle(sketch, "E382.MirrorC", {"center": v(-66.1, 150) * mm, "radius": 4.5 * mm});
            skCircle(sketch, "E383.MirrorC", {"center": v(113.9, 60) * mm, "radius": 4.5 * mm});
            skCircle(sketch, "E384.MirrorC", {"center": v(-126.1, 300) * mm, "radius": 4.5 * mm});
            skCircle(sketch, "E385.MirrorC", {"center": v(23.9, 75) * mm, "radius": 4.5 * mm});
            skCircle(sketch, "E386.MirrorC", {"center": v(113.9, 90) * mm, "radius": 4.5 * mm});
            skCircle(sketch, "E387.MirrorC", {"center": v(53.9, 270) * mm, "radius": 4.5 * mm});
            skCircle(sketch, "E388.MirrorC", {"center": v(713.9, 210) * mm, "radius": 4.5 * mm});
            skCircle(sketch, "E389.MirrorC", {"center": v(263.9, 135) * mm, "radius": 4.5 * mm});
            skCircle(sketch, "E390.MirrorC", {"center": v(203.9, 285) * mm, "radius": 4.5 * mm});
            skCircle(sketch, "E391.MirrorC", {"center": v(143.9, 15) * mm, "radius": 4.5 * mm});
            skCircle(sketch, "E392.MirrorC", {"center": v(1343.9, 45) * mm, "radius": 4.5 * mm});
            skCircle(sketch, "E393.MirrorC", {"center": v(1313.9, 120) * mm, "radius": 4.5 * mm});
            skCircle(sketch, "E394.MirrorC", {"center": v(1253.9, 30) * mm, "radius": 4.5 * mm});
            skCircle(sketch, "E395.MirrorC", {"center": v(623.9, 255) * mm, "radius": 4.5 * mm});
            skCircle(sketch, "E396.MirrorC", {"center": v(1223.9, 135) * mm, "radius": 4.5 * mm});
            skCircle(sketch, "E397.MirrorC", {"center": v(-576.1, 105) * mm, "radius": 4.5 * mm});
            skCircle(sketch, "E398.MirrorC", {"center": v(-516.1, 225) * mm, "radius": 4.5 * mm});
            skCircle(sketch, "E399.MirrorC", {"center": v(443.9, 135) * mm, "radius": 4.5 * mm});
            skCircle(sketch, "E400.MirrorC", {"center": v(473.9, 30) * mm, "radius": 4.5 * mm});
            skCircle(sketch, "E401.MirrorC", {"center": v(623.9, 225) * mm, "radius": 4.5 * mm});
            skCircle(sketch, "E402.MirrorC", {"center": v(563.9, 105) * mm, "radius": 4.5 * mm});
            skCircle(sketch, "E403.MirrorC", {"center": v(533.9, 120) * mm, "radius": 4.5 * mm});
            skCircle(sketch, "E404.MirrorC", {"center": v(743.9, 255) * mm, "radius": 4.5 * mm});
            skCircle(sketch, "E405.MirrorC", {"center": v(683.9, 45) * mm, "radius": 4.5 * mm});
            skCircle(sketch, "E406.MirrorC", {"center": v(893.9, 180) * mm, "radius": 4.5 * mm});
            skCircle(sketch, "E407.MirrorC", {"center": v(833.9, 240) * mm, "radius": 4.5 * mm});
            skCircle(sketch, "E408.MirrorC", {"center": v(1073.9, 150) * mm, "radius": 4.5 * mm});
            skCircle(sketch, "E409.MirrorC", {"center": v(833.9, 210) * mm, "radius": 4.5 * mm});
            skCircle(sketch, "E410.MirrorC", {"center": v(1013.9, 300) * mm, "radius": 4.5 * mm});
            skCircle(sketch, "E411.MirrorC", {"center": v(983.9, 165) * mm, "radius": 4.5 * mm});
            skCircle(sketch, "E412.MirrorC", {"center": v(923.9, 195) * mm, "radius": 4.5 * mm});
            skCircle(sketch, "E413.MirrorC", {"center": v(1193.9, 270) * mm, "radius": 4.5 * mm});
            skCircle(sketch, "E414.MirrorC", {"center": v(1163.9, 75) * mm, "radius": 4.5 * mm});
            skCircle(sketch, "E415.MirrorC", {"center": v(1343.9, 75) * mm, "radius": 4.5 * mm});
            skCircle(sketch, "E416.MirrorC", {"center": v(1253.9, 60) * mm, "radius": 4.5 * mm});
            skCircle(sketch, "E417.MirrorC", {"center": v(1283.9, 15) * mm, "radius": 4.5 * mm});
            skCircle(sketch, "E418.MirrorC", {"center": v(1253.9, 90) * mm, "radius": 4.5 * mm});
            skCircle(sketch, "E419.MirrorC", {"center": v(-336.1, 225) * mm, "radius": 4.5 * mm});
            skCircle(sketch, "E420.MirrorC", {"center": v(-426.1, 120) * mm, "radius": 4.5 * mm});
            skCircle(sketch, "E421.MirrorC", {"center": v(-396.1, 105) * mm, "radius": 4.5 * mm});
            skCircle(sketch, "E422.MirrorC", {"center": v(-126.1, 210) * mm, "radius": 4.5 * mm});
            skCircle(sketch, "E423.MirrorC", {"center": v(-216.1, 255) * mm, "radius": 4.5 * mm});
            skCircle(sketch, "E424.MirrorC", {"center": v(-276.1, 45) * mm, "radius": 4.5 * mm});
            skCircle(sketch, "E425.MirrorC", {"center": v(-36.1, 195) * mm, "radius": 4.5 * mm});
            skCircle(sketch, "E426.MirrorC", {"center": v(-66.1, 180) * mm, "radius": 4.5 * mm});
            skCircle(sketch, "E427.MirrorC", {"center": v(-126.1, 240) * mm, "radius": 4.5 * mm});
            skCircle(sketch, "E428.MirrorC", {"center": v(113.9, 150) * mm, "radius": 4.5 * mm});
            skCircle(sketch, "E429.MirrorC", {"center": v(53.9, 300) * mm, "radius": 4.5 * mm});
            skCircle(sketch, "E430.MirrorC", {"center": v(23.9, 165) * mm, "radius": 4.5 * mm});
            skCircle(sketch, "E431.MirrorC", {"center": v(293.9, 90) * mm, "radius": 4.5 * mm});
            skCircle(sketch, "E432.MirrorC", {"center": v(203.9, 75) * mm, "radius": 4.5 * mm});
            skCircle(sketch, "E433.MirrorC", {"center": v(233.9, 270) * mm, "radius": 4.5 * mm});
            skCircle(sketch, "E434.MirrorC", {"center": v(383.9, 285) * mm, "radius": 4.5 * mm});
            skCircle(sketch, "E435.MirrorC", {"center": v(323.9, 15) * mm, "radius": 4.5 * mm});
            skCircle(sketch, "E436.MirrorC", {"center": v(293.9, 60) * mm, "radius": 4.5 * mm});
            skCircle(sketch, "E437.MirrorC", {"center": v(863.9, 165) * mm, "radius": 4.5 * mm});
            skCircle(sketch, "E438.MirrorC", {"center": v(-576.1, 285) * mm, "radius": 4.5 * mm});
            skCircle(sketch, "E439.MirrorC", {"center": v(-486.1, 30) * mm, "radius": 4.5 * mm});
            skCircle(sketch, "E440.MirrorC", {"center": v(-516.1, 135) * mm, "radius": 4.5 * mm});
            skCircle(sketch, "E441.MirrorC", {"center": v(473.9, 60) * mm, "radius": 4.5 * mm});
            skCircle(sketch, "E442.MirrorC", {"center": v(623.9, 135) * mm, "radius": 4.5 * mm});
            skCircle(sketch, "E443.MirrorC", {"center": v(563.9, 285) * mm, "radius": 4.5 * mm});
            skCircle(sketch, "E444.MirrorC", {"center": v(743.9, 105) * mm, "radius": 4.5 * mm});
            skCircle(sketch, "E445.MirrorC", {"center": v(503.9, 15) * mm, "radius": 4.5 * mm});
            skCircle(sketch, "E446.MirrorC", {"center": v(713.9, 120) * mm, "radius": 4.5 * mm});
            skCircle(sketch, "E447.MirrorC", {"center": v(653.9, 30) * mm, "radius": 4.5 * mm});
            skCircle(sketch, "E448.MirrorC", {"center": v(863.9, 45) * mm, "radius": 4.5 * mm});
            skCircle(sketch, "E449.MirrorC", {"center": v(803.9, 225) * mm, "radius": 4.5 * mm});
            skCircle(sketch, "E450.MirrorC", {"center": v(1013.9, 240) * mm, "radius": 4.5 * mm});
            skCircle(sketch, "E451.MirrorC", {"center": v(1073.9, 180) * mm, "radius": 4.5 * mm});
            skCircle(sketch, "E452.MirrorC", {"center": v(1013.9, 210) * mm, "radius": 4.5 * mm});
            skCircle(sketch, "E453.MirrorC", {"center": v(923.9, 255) * mm, "radius": 4.5 * mm});
            skCircle(sketch, "E454.MirrorC", {"center": v(1163.9, 165) * mm, "radius": 4.5 * mm});
            skCircle(sketch, "E455.MirrorC", {"center": v(1193.9, 300) * mm, "radius": 4.5 * mm});
            skCircle(sketch, "E456.MirrorC", {"center": v(1103.9, 195) * mm, "radius": 4.5 * mm});
            skCircle(sketch, "E457.MirrorC", {"center": v(1343.9, 105) * mm, "radius": 4.5 * mm});
            skCircle(sketch, "E458.MirrorC", {"center": v(1253.9, 150) * mm, "radius": 4.5 * mm});
            skCircle(sketch, "E459.MirrorC", {"center": v(-456.1, 15) * mm, "radius": 4.5 * mm});
            skCircle(sketch, "E460.MirrorC", {"center": v(-336.1, 135) * mm, "radius": 4.5 * mm});
            skCircle(sketch, "E461.MirrorC", {"center": v(803.9, 195) * mm, "radius": 4.5 * mm});
            skCircle(sketch, "E462.MirrorC", {"center": v(-396.1, 285) * mm, "radius": 4.5 * mm});
            skCircle(sketch, "E463.MirrorC", {"center": v(-306.1, 30) * mm, "radius": 4.5 * mm});
            skCircle(sketch, "E464.MirrorC", {"center": v(-156.1, 225) * mm, "radius": 4.5 * mm});
            skCircle(sketch, "E465.MirrorC", {"center": v(-216.1, 105) * mm, "radius": 4.5 * mm});
            skCircle(sketch, "E466.MirrorC", {"center": v(-246.1, 120) * mm, "radius": 4.5 * mm});
            skCircle(sketch, "E467.MirrorC", {"center": v(-96.1, 45) * mm, "radius": 4.5 * mm});
            skCircle(sketch, "E468.MirrorC", {"center": v(-36.1, 255) * mm, "radius": 4.5 * mm});
            skCircle(sketch, "E469.MirrorC", {"center": v(113.9, 180) * mm, "radius": 4.5 * mm});
            skCircle(sketch, "E470.MirrorC", {"center": v(53.9, 240) * mm, "radius": 4.5 * mm});
            skCircle(sketch, "E471.MirrorC", {"center": v(53.9, 210) * mm, "radius": 4.5 * mm});
            skCircle(sketch, "E472.MirrorC", {"center": v(293.9, 150) * mm, "radius": 4.5 * mm});
            skCircle(sketch, "E473.MirrorC", {"center": v(233.9, 300) * mm, "radius": 4.5 * mm});
            skCircle(sketch, "E474.MirrorC", {"center": v(143.9, 195) * mm, "radius": 4.5 * mm});
            skCircle(sketch, "E475.MirrorC", {"center": v(383.9, 75) * mm, "radius": 4.5 * mm});
            skCircle(sketch, "E476.MirrorC", {"center": v(203.9, 165) * mm, "radius": 4.5 * mm});
            skCircle(sketch, "E477.MirrorC", {"center": v(413.9, 270) * mm, "radius": 4.5 * mm});
            skCircle(sketch, "E478.MirrorC", {"center": v(473.9, 90) * mm, "radius": 4.5 * mm});
            skCircle(sketch, "E479.MirrorC", {"center": v(-576.1, 75) * mm, "radius": 4.5 * mm});
            skCircle(sketch, "E480.MirrorC", {"center": v(-546.1, 270) * mm, "radius": 4.5 * mm});
            skCircle(sketch, "E481.MirrorC", {"center": v(-486.1, 60) * mm, "radius": 4.5 * mm});
            skCircle(sketch, "E482.MirrorC", {"center": v(-486.1, 90) * mm, "radius": 4.5 * mm});
            skCircle(sketch, "E483.MirrorC", {"center": v(-396.1, 75) * mm, "radius": 4.5 * mm});
            skCircle(sketch, "E484.MirrorC", {"center": v(-366.1, 270) * mm, "radius": 4.5 * mm});
            skCircle(sketch, "E485.MirrorC", {"center": v(-276.1, 15) * mm, "radius": 4.5 * mm});
            skCircle(sketch, "E486.MirrorC", {"center": v(-306.1, 60) * mm, "radius": 4.5 * mm});
            skCircle(sketch, "E487.MirrorC", {"center": v(833.9, 30) * mm, "radius": 4.5 * mm});
            skCircle(sketch, "E488.MirrorC", {"center": v(-306.1, 90) * mm, "radius": 4.5 * mm});
            skCircle(sketch, "E489.MirrorC", {"center": v(803.9, 135) * mm, "radius": 4.5 * mm});
            skCircle(sketch, "E490.MirrorC", {"center": v(743.9, 285) * mm, "radius": 4.5 * mm});
            skCircle(sketch, "E491.MirrorC", {"center": v(983.9, 225) * mm, "radius": 4.5 * mm});
            skCircle(sketch, "E492.MirrorC", {"center": v(923.9, 105) * mm, "radius": 4.5 * mm});
            skCircle(sketch, "E493.MirrorC", {"center": v(893.9, 120) * mm, "radius": 4.5 * mm});
            skCircle(sketch, "E494.MirrorC", {"center": v(1103.9, 255) * mm, "radius": 4.5 * mm});
            skCircle(sketch, "E495.MirrorC", {"center": v(773.9, 180) * mm, "radius": 4.5 * mm});
            skCircle(sketch, "E496.MirrorC", {"center": v(1043.9, 45) * mm, "radius": 4.5 * mm});
            skCircle(sketch, "E497.MirrorC", {"center": v(1253.9, 180) * mm, "radius": 4.5 * mm});
            skCircle(sketch, "E498.MirrorC", {"center": v(1193.9, 240) * mm, "radius": 4.5 * mm});
            skCircle(sketch, "E499.MirrorC", {"center": v(1193.9, 210) * mm, "radius": 4.5 * mm});
            skCircle(sketch, "E500.MirrorC", {"center": v(1343.9, 135) * mm, "radius": 4.5 * mm});
            skCircle(sketch, "E501.MirrorC", {"center": v(1283.9, 195) * mm, "radius": 4.5 * mm});
            skCircle(sketch, "E502.MirrorC", {"center": v(-66.1, 120) * mm, "radius": 4.5 * mm});
            skCircle(sketch, "E503.MirrorC", {"center": v(-126.1, 30) * mm, "radius": 4.5 * mm});
            skCircle(sketch, "E504.MirrorC", {"center": v(-156.1, 135) * mm, "radius": 4.5 * mm});
            skCircle(sketch, "E505.MirrorC", {"center": v(-216.1, 285) * mm, "radius": 4.5 * mm});
            skCircle(sketch, "E506.MirrorC", {"center": v(23.9, 225) * mm, "radius": 4.5 * mm});
            skCircle(sketch, "E507.MirrorC", {"center": v(233.9, 210) * mm, "radius": 4.5 * mm});
            skCircle(sketch, "E508.MirrorC", {"center": v(-36.1, 105) * mm, "radius": 4.5 * mm});
            skCircle(sketch, "E509.MirrorC", {"center": v(143.9, 255) * mm, "radius": 4.5 * mm});
            skCircle(sketch, "E510.MirrorC", {"center": v(323.9, 195) * mm, "radius": 4.5 * mm});
            skCircle(sketch, "E511.MirrorC", {"center": v(83.9, 45) * mm, "radius": 4.5 * mm});
            skCircle(sketch, "E512.MirrorC", {"center": v(293.9, 180) * mm, "radius": 4.5 * mm});
            skCircle(sketch, "E513.MirrorC", {"center": v(233.9, 240) * mm, "radius": 4.5 * mm});
            skCircle(sketch, "E514.MirrorC", {"center": v(473.9, 150) * mm, "radius": 4.5 * mm});
            skCircle(sketch, "E515.MirrorC", {"center": v(413.9, 300) * mm, "radius": 4.5 * mm});
            skCircle(sketch, "E516.MirrorC", {"center": v(383.9, 165) * mm, "radius": 4.5 * mm});
            skCircle(sketch, "E517.MirrorC", {"center": v(593.9, 270) * mm, "radius": 4.5 * mm});
            skCircle(sketch, "E518.MirrorC", {"center": v(683.9, 15) * mm, "radius": 4.5 * mm});
            skCircle(sketch, "E519.MirrorC", {"center": v(653.9, 60) * mm, "radius": 4.5 * mm});
            skCircle(sketch, "E520.MirrorC", {"center": v(653.9, 90) * mm, "radius": 4.5 * mm});
            skCircle(sketch, "E521.MirrorC", {"center": v(563.9, 75) * mm, "radius": 4.5 * mm});
            skCircle(sketch, "E522.MirrorC", {"center": v(-396.1, 165) * mm, "radius": 4.5 * mm});
            skCircle(sketch, "E523.MirrorC", {"center": v(-366.1, 300) * mm, "radius": 4.5 * mm});
            skCircle(sketch, "E524.MirrorC", {"center": v(-456.1, 195) * mm, "radius": 4.5 * mm});
            skCircle(sketch, "E525.MirrorC", {"center": v(-186.1, 270) * mm, "radius": 4.5 * mm});
            skCircle(sketch, "E526.MirrorC", {"center": v(-306.1, 150) * mm, "radius": 4.5 * mm});
            skCircle(sketch, "E527.MirrorC", {"center": v(-96.1, 15) * mm, "radius": 4.5 * mm});
            skCircle(sketch, "E528.MirrorC", {"center": v(-126.1, 60) * mm, "radius": 4.5 * mm});
            skCircle(sketch, "E529.MirrorC", {"center": v(-126.1, 90) * mm, "radius": 4.5 * mm});
            skCircle(sketch, "E530.MirrorC", {"center": v(-216.1, 75) * mm, "radius": 4.5 * mm});
            skCircle(sketch, "E531.MirrorC", {"center": v(-486.1, 150) * mm, "radius": 4.5 * mm});
            skCircle(sketch, "E532.MirrorC", {"center": v(-546.1, 300) * mm, "radius": 4.5 * mm});
            skCircle(sketch, "E533.MirrorC", {"center": v(-576.1, 15) * mm, "radius": 4.5 * mm});
            skCircle(sketch, "E534.MirrorC", {"center": v(-576.1, 165) * mm, "radius": 4.5 * mm});
            skCircle(sketch, "E535.MirrorC", {"center": v(983.9, 135) * mm, "radius": 4.5 * mm});
            skCircle(sketch, "E536.MirrorC", {"center": v(923.9, 285) * mm, "radius": 4.5 * mm});
            skCircle(sketch, "E537.MirrorC", {"center": v(863.9, 15) * mm, "radius": 4.5 * mm});
            skCircle(sketch, "E538.MirrorC", {"center": v(1103.9, 105) * mm, "radius": 4.5 * mm});
            skCircle(sketch, "E539.MirrorC", {"center": v(1073.9, 120) * mm, "radius": 4.5 * mm});
            skCircle(sketch, "E540.MirrorC", {"center": v(1013.9, 30) * mm, "radius": 4.5 * mm});
            skCircle(sketch, "E541.MirrorC", {"center": v(1223.9, 45) * mm, "radius": 4.5 * mm});
            skCircle(sketch, "E542.MirrorC", {"center": v(1163.9, 225) * mm, "radius": 4.5 * mm});
            skCircle(sketch, "E543.MirrorC", {"center": v(1343.9, 165) * mm, "radius": 4.5 * mm});
            skCircle(sketch, "E544.MirrorC", {"center": v(1283.9, 255) * mm, "radius": 4.5 * mm});
            skCircle(sketch, "E545.MirrorC", {"center": v(-366.1, 120) * mm, "radius": 4.5 * mm});
            skCircle(sketch, "E546.MirrorC", {"center": v(-486.1, 180) * mm, "radius": 4.5 * mm});
            skCircle(sketch, "E547.MirrorC", {"center": v(-546.1, 240) * mm, "radius": 4.5 * mm});
            skCircle(sketch, "E548.MirrorC", {"center": v(-546.1, 210) * mm, "radius": 4.5 * mm});
            skCircle(sketch, "E549.MirrorC", {"center": v(53.9, 30) * mm, "radius": 4.5 * mm});
            skCircle(sketch, "E550.MirrorC", {"center": v(23.9, 135) * mm, "radius": 4.5 * mm});
            skCircle(sketch, "E551.MirrorC", {"center": v(-426.1, 30) * mm, "radius": 4.5 * mm});
            skCircle(sketch, "E552.MirrorC", {"center": v(-36.1, 285) * mm, "radius": 4.5 * mm});
            skCircle(sketch, "E553.MirrorC", {"center": v(203.9, 225) * mm, "radius": 4.5 * mm});
            skCircle(sketch, "E554.MirrorC", {"center": v(143.9, 105) * mm, "radius": 4.5 * mm});
            skCircle(sketch, "E555.MirrorC", {"center": v(113.9, 120) * mm, "radius": 4.5 * mm});
            skCircle(sketch, "E556.MirrorC", {"center": v(323.9, 255) * mm, "radius": 4.5 * mm});
            skCircle(sketch, "E557.MirrorC", {"center": v(263.9, 45) * mm, "radius": 4.5 * mm});
            skCircle(sketch, "E558.MirrorC", {"center": v(473.9, 180) * mm, "radius": 4.5 * mm});
            skCircle(sketch, "E559.MirrorC", {"center": v(413.9, 240) * mm, "radius": 4.5 * mm});
            skCircle(sketch, "E560.MirrorC", {"center": v(413.9, 210) * mm, "radius": 4.5 * mm});
            skCircle(sketch, "E561.MirrorC", {"center": v(563.9, 165) * mm, "radius": 4.5 * mm});
            skCircle(sketch, "E562.MirrorC", {"center": v(503.9, 195) * mm, "radius": 4.5 * mm});
            skCircle(sketch, "E563.MirrorC", {"center": v(653.9, 150) * mm, "radius": 4.5 * mm});
            skCircle(sketch, "E564.MirrorC", {"center": v(593.9, 300) * mm, "radius": 4.5 * mm});
            skCircle(sketch, "E565.MirrorC", {"center": v(833.9, 60) * mm, "radius": 4.5 * mm});
            skCircle(sketch, "E566.MirrorC", {"center": v(833.9, 90) * mm, "radius": 4.5 * mm});
            skCircle(sketch, "E567.MirrorC", {"center": v(743.9, 75) * mm, "radius": 4.5 * mm});
            skCircle(sketch, "E568.MirrorC", {"center": v(773.9, 270) * mm, "radius": 4.5 * mm});
            skCircle(sketch, "E569.MirrorC", {"center": v(-366.1, 210) * mm, "radius": 4.5 * mm});
            skCircle(sketch, "E570.MirrorC", {"center": v(-366.1, 240) * mm, "radius": 4.5 * mm});
            skCircle(sketch, "E571.MirrorC", {"center": v(-456.1, 255) * mm, "radius": 4.5 * mm});
            skCircle(sketch, "E572.MirrorC", {"center": v(-216.1, 165) * mm, "radius": 4.5 * mm});
            skCircle(sketch, "E573.MirrorC", {"center": v(-276.1, 195) * mm, "radius": 4.5 * mm});
            skCircle(sketch, "E574.MirrorC", {"center": v(-306.1, 180) * mm, "radius": 4.5 * mm});
            skCircle(sketch, "E575.MirrorC", {"center": v(-186.1, 300) * mm, "radius": 4.5 * mm});
            skCircle(sketch, "E576.MirrorC", {"center": v(-126.1, 150) * mm, "radius": 4.5 * mm});
            skCircle(sketch, "E577.MirrorC", {"center": v(-36.1, 75) * mm, "radius": 4.5 * mm});
            skCircle(sketch, "E578.MirrorC", {"center": v(53.9, 60) * mm, "radius": 4.5 * mm});
            skCircle(sketch, "E579.MirrorC", {"center": v(53.9, 90) * mm, "radius": 4.5 * mm});
            skCircle(sketch, "E580.MirrorC", {"center": v(-6.1, 270) * mm, "radius": 4.5 * mm});
            skCircle(sketch, "E581.MirrorC", {"center": v(1103.9, 285) * mm, "radius": 4.5 * mm});
            skCircle(sketch, "E582.MirrorC", {"center": v(1043.9, 15) * mm, "radius": 4.5 * mm});
            skCircle(sketch, "E583.MirrorC", {"center": v(1013.9, 60) * mm, "radius": 4.5 * mm});
            skCircle(sketch, "E584.MirrorC", {"center": v(-456.1, 135) * mm, "radius": 4.5 * mm});
            skCircle(sketch, "E585.MirrorC", {"center": v(1253.9, 120) * mm, "radius": 4.5 * mm});
            skCircle(sketch, "E586.MirrorC", {"center": v(1193.9, 30) * mm, "radius": 4.5 * mm});
            skCircle(sketch, "E587.MirrorC", {"center": v(1163.9, 135) * mm, "radius": 4.5 * mm});
            skCircle(sketch, "E588.MirrorC", {"center": v(1343.9, 195) * mm, "radius": 4.5 * mm});
            skCircle(sketch, "E589.MirrorC", {"center": v(1283.9, 105) * mm, "radius": 4.5 * mm});
            skCircle(sketch, "E590.MirrorC", {"center": v(-216.1, 45) * mm, "radius": 4.5 * mm});
            skCircle(sketch, "E591.MirrorC", {"center": v(-516.1, 45) * mm, "radius": 4.5 * mm});
            skCircle(sketch, "E592.MirrorC", {"center": v(-576.1, 225) * mm, "radius": 4.5 * mm});
            skCircle(sketch, "E593.MirrorC", {"center": v(203.9, 135) * mm, "radius": 4.5 * mm});
            skCircle(sketch, "E594.MirrorC", {"center": v(143.9, 285) * mm, "radius": 4.5 * mm});
            skCircle(sketch, "E595.MirrorC", {"center": v(83.9, 15) * mm, "radius": 4.5 * mm});
            skCircle(sketch, "E596.MirrorC", {"center": v(323.9, 105) * mm, "radius": 4.5 * mm});
            skCircle(sketch, "E597.MirrorC", {"center": v(293.9, 120) * mm, "radius": 4.5 * mm});
            skCircle(sketch, "E598.MirrorC", {"center": v(443.9, 45) * mm, "radius": 4.5 * mm});
            skCircle(sketch, "E599.MirrorC", {"center": v(233.9, 30) * mm, "radius": 4.5 * mm});
            skCircle(sketch, "E600.MirrorC", {"center": v(383.9, 225) * mm, "radius": 4.5 * mm});
            skCircle(sketch, "E601.MirrorC", {"center": v(593.9, 210) * mm, "radius": 4.5 * mm});
            skCircle(sketch, "E602.MirrorC", {"center": v(503.9, 255) * mm, "radius": 4.5 * mm});
            skCircle(sketch, "E603.MirrorC", {"center": v(683.9, 195) * mm, "radius": 4.5 * mm});
            skCircle(sketch, "E604.MirrorC", {"center": v(653.9, 180) * mm, "radius": 4.5 * mm});
            skCircle(sketch, "E605.MirrorC", {"center": v(593.9, 240) * mm, "radius": 4.5 * mm});
            skCircle(sketch, "E606.MirrorC", {"center": v(833.9, 150) * mm, "radius": 4.5 * mm});
            skCircle(sketch, "E607.MirrorC", {"center": v(773.9, 300) * mm, "radius": 4.5 * mm});
            skCircle(sketch, "E608.MirrorC", {"center": v(743.9, 165) * mm, "radius": 4.5 * mm});
            skCircle(sketch, "E609.MirrorC", {"center": v(1013.9, 90) * mm, "radius": 4.5 * mm});
            skCircle(sketch, "E610.MirrorC", {"center": v(923.9, 75) * mm, "radius": 4.5 * mm});
            skCircle(sketch, "E611.MirrorC", {"center": v(953.9, 270) * mm, "radius": 4.5 * mm});
            skCircle(sketch, "E612.MirrorC", {"center": v(-456.1, 105) * mm, "radius": 4.5 * mm});
            skCircle(sketch, "E613.MirrorC", {"center": v(-396.1, 225) * mm, "radius": 4.5 * mm});
            skCircle(sketch, "E614.MirrorC", {"center": v(-276.1, 255) * mm, "radius": 4.5 * mm});
            skCircle(sketch, "E615.MirrorC", {"center": v(-186.1, 210) * mm, "radius": 4.5 * mm});
            skCircle(sketch, "E616.MirrorC", {"center": v(-336.1, 45) * mm, "radius": 4.5 * mm});
            skCircle(sketch, "E617.MirrorC", {"center": v(-96.1, 195) * mm, "radius": 4.5 * mm});
            skCircle(sketch, "E618.MirrorC", {"center": v(-126.1, 180) * mm, "radius": 4.5 * mm});
            skCircle(sketch, "E619.MirrorC", {"center": v(-186.1, 240) * mm, "radius": 4.5 * mm});
            skCircle(sketch, "E620.MirrorC", {"center": v(53.9, 150) * mm, "radius": 4.5 * mm});
            skCircle(sketch, "E621.MirrorC", {"center": v(-6.1, 300) * mm, "radius": 4.5 * mm});
            skCircle(sketch, "E622.MirrorC", {"center": v(-36.1, 165) * mm, "radius": 4.5 * mm});
            skCircle(sketch, "E623.MirrorC", {"center": v(233.9, 90) * mm, "radius": 4.5 * mm});
            skCircle(sketch, "E624.MirrorC", {"center": v(143.9, 75) * mm, "radius": 4.5 * mm});
            skCircle(sketch, "E625.MirrorC", {"center": v(173.9, 270) * mm, "radius": 4.5 * mm});
            skCircle(sketch, "E626.MirrorC", {"center": v(-276.1, 225) * mm, "radius": 4.5 * mm});
            skCircle(sketch, "E627.MirrorC", {"center": v(1223.9, 15) * mm, "radius": 4.5 * mm});
            skCircle(sketch, "E628.MirrorC", {"center": v(1193.9, 60) * mm, "radius": 4.5 * mm});
            skCircle(sketch, "E629.MirrorC", {"center": v(1193.9, 90) * mm, "radius": 4.5 * mm});
            skCircle(sketch, "E630.MirrorC", {"center": v(1343.9, 225) * mm, "radius": 4.5 * mm});
            skCircle(sketch, "E631.MirrorC", {"center": v(1283.9, 285) * mm, "radius": 4.5 * mm});
            skCircle(sketch, "E632.MirrorC", {"center": v(-336.1, 105) * mm, "radius": 4.5 * mm});
            skCircle(sketch, "E633.MirrorC", {"center": v(-486.1, 120) * mm, "radius": 4.5 * mm});
            skCircle(sketch, "E634.MirrorC", {"center": v(-546.1, 30) * mm, "radius": 4.5 * mm});
            skCircle(sketch, "E635.MirrorC", {"center": v(-576.1, 135) * mm, "radius": 4.5 * mm});
            skCircle(sketch, "E636.MirrorC", {"center": v(323.9, 285) * mm, "radius": 4.5 * mm});
            skCircle(sketch, "E637.MirrorC", {"center": v(263.9, 15) * mm, "radius": 4.5 * mm});
            skCircle(sketch, "E638.MirrorC", {"center": v(233.9, 60) * mm, "radius": 4.5 * mm});
            skCircle(sketch, "E639.MirrorC", {"center": v(473.9, 120) * mm, "radius": 4.5 * mm});
            skCircle(sketch, "E640.MirrorC", {"center": v(383.9, 135) * mm, "radius": 4.5 * mm});
            skCircle(sketch, "E641.MirrorC", {"center": v(413.9, 30) * mm, "radius": 4.5 * mm});
            skCircle(sketch, "E642.MirrorC", {"center": v(563.9, 225) * mm, "radius": 4.5 * mm});
            skCircle(sketch, "E643.MirrorC", {"center": v(503.9, 105) * mm, "radius": 4.5 * mm});
            skCircle(sketch, "E644.MirrorC", {"center": v(683.9, 255) * mm, "radius": 4.5 * mm});
            skCircle(sketch, "E645.MirrorC", {"center": v(623.9, 45) * mm, "radius": 4.5 * mm});
            skCircle(sketch, "E646.MirrorC", {"center": v(833.9, 180) * mm, "radius": 4.5 * mm});
            skCircle(sketch, "E647.MirrorC", {"center": v(773.9, 240) * mm, "radius": 4.5 * mm});
            skCircle(sketch, "E648.MirrorC", {"center": v(773.9, 210) * mm, "radius": 4.5 * mm});
            skCircle(sketch, "E649.MirrorC", {"center": v(1013.9, 150) * mm, "radius": 4.5 * mm});
            skCircle(sketch, "E650.MirrorC", {"center": v(953.9, 300) * mm, "radius": 4.5 * mm});
            skCircle(sketch, "E651.MirrorC", {"center": v(923.9, 165) * mm, "radius": 4.5 * mm});
            skCircle(sketch, "E652.MirrorC", {"center": v(863.9, 195) * mm, "radius": 4.5 * mm});
            skCircle(sketch, "E653.MirrorC", {"center": v(1103.9, 75) * mm, "radius": 4.5 * mm});
            skCircle(sketch, "E654.MirrorC", {"center": v(1133.9, 270) * mm, "radius": 4.5 * mm});
            skCircle(sketch, "E655.MirrorC", {"center": v(-366.1, 30) * mm, "radius": 4.5 * mm});
            skCircle(sketch, "E656.MirrorC", {"center": v(-396.1, 135) * mm, "radius": 4.5 * mm});
            skCircle(sketch, "E657.MirrorC", {"center": v(-216.1, 225) * mm, "radius": 4.5 * mm});
            skCircle(sketch, "E658.MirrorC", {"center": v(-456.1, 285) * mm, "radius": 4.5 * mm});
            skCircle(sketch, "E659.MirrorC", {"center": v(-276.1, 105) * mm, "radius": 4.5 * mm});
            skCircle(sketch, "E660.MirrorC", {"center": v(-306.1, 120) * mm, "radius": 4.5 * mm});
            skCircle(sketch, "E661.MirrorC", {"center": v(-96.1, 255) * mm, "radius": 4.5 * mm});
            skCircle(sketch, "E662.MirrorC", {"center": v(-156.1, 45) * mm, "radius": 4.5 * mm});
            skCircle(sketch, "E663.MirrorC", {"center": v(53.9, 180) * mm, "radius": 4.5 * mm});
            skCircle(sketch, "E664.MirrorC", {"center": v(-6.1, 240) * mm, "radius": 4.5 * mm});
            skCircle(sketch, "E665.MirrorC", {"center": v(-6.1, 210) * mm, "radius": 4.5 * mm});
            skCircle(sketch, "E666.MirrorC", {"center": v(233.9, 150) * mm, "radius": 4.5 * mm});
            skCircle(sketch, "E667.MirrorC", {"center": v(173.9, 300) * mm, "radius": 4.5 * mm});
            skCircle(sketch, "E668.MirrorC", {"center": v(143.9, 165) * mm, "radius": 4.5 * mm});
            skCircle(sketch, "E669.MirrorC", {"center": v(83.9, 195) * mm, "radius": 4.5 * mm});
            skCircle(sketch, "E670.MirrorC", {"center": v(323.9, 75) * mm, "radius": 4.5 * mm});
            skCircle(sketch, "E671.MirrorC", {"center": v(353.9, 270) * mm, "radius": 4.5 * mm});
            skCircle(sketch, "E672.MirrorC", {"center": v(-66.1, 210) * mm, "radius": 4.5 * mm});
            skCircle(sketch, "E673.MirrorC", {"center": v(-66.1, 240) * mm, "radius": 4.5 * mm});
            skCircle(sketch, "E674.MirrorC", {"center": v(1343.9, 255) * mm, "radius": 4.5 * mm});
            skCircle(sketch, "E675.MirrorC", {"center": v(1283.9, 75) * mm, "radius": 4.5 * mm});
            skCircle(sketch, "E676.MirrorC", {"center": v(-516.1, 15) * mm, "radius": 4.5 * mm});
            skCircle(sketch, "E677.MirrorC", {"center": v(-546.1, 60) * mm, "radius": 4.5 * mm});
            skCircle(sketch, "E678.MirrorC", {"center": v(-546.1, 90) * mm, "radius": 4.5 * mm});
            skCircle(sketch, "E679.MirrorC", {"center": v(443.9, 15) * mm, "radius": 4.5 * mm});
            skCircle(sketch, "E680.MirrorC", {"center": v(413.9, 60) * mm, "radius": 4.5 * mm});
            skCircle(sketch, "E681.MirrorC", {"center": v(413.9, 90) * mm, "radius": 4.5 * mm});
            skCircle(sketch, "E682.MirrorC", {"center": v(563.9, 135) * mm, "radius": 4.5 * mm});
            skCircle(sketch, "E683.MirrorC", {"center": v(503.9, 285) * mm, "radius": 4.5 * mm});
            skCircle(sketch, "E684.MirrorC", {"center": v(683.9, 105) * mm, "radius": 4.5 * mm});
            skCircle(sketch, "E685.MirrorC", {"center": v(653.9, 120) * mm, "radius": 4.5 * mm});
            skCircle(sketch, "E686.MirrorC", {"center": v(593.9, 30) * mm, "radius": 4.5 * mm});
            skCircle(sketch, "E687.MirrorC", {"center": v(803.9, 45) * mm, "radius": 4.5 * mm});
            skCircle(sketch, "E688.MirrorC", {"center": v(-156.1, 255) * mm, "radius": 4.5 * mm});
            skCircle(sketch, "E689.MirrorC", {"center": v(743.9, 225) * mm, "radius": 4.5 * mm});
            skCircle(sketch, "E690.MirrorC", {"center": v(1013.9, 180) * mm, "radius": 4.5 * mm});
            skCircle(sketch, "E691.MirrorC", {"center": v(953.9, 240) * mm, "radius": 4.5 * mm});
            skCircle(sketch, "E692.MirrorC", {"center": v(863.9, 255) * mm, "radius": 4.5 * mm});
            skCircle(sketch, "E693.MirrorC", {"center": v(953.9, 210) * mm, "radius": 4.5 * mm});
            skCircle(sketch, "E694.MirrorC", {"center": v(1133.9, 300) * mm, "radius": 4.5 * mm});
            skCircle(sketch, "E695.MirrorC", {"center": v(1103.9, 165) * mm, "radius": 4.5 * mm});
            skCircle(sketch, "E696.MirrorC", {"center": v(1043.9, 195) * mm, "radius": 4.5 * mm});
            skCircle(sketch, "E697.MirrorC", {"center": v(1313.9, 270) * mm, "radius": 4.5 * mm});
            skCircle(sketch, "E698.MirrorC", {"center": v(1193.9, 150) * mm, "radius": 4.5 * mm});
            skCircle(sketch, "E699.MirrorC", {"center": v(-366.1, 60) * mm, "radius": 4.5 * mm});
            skCircle(sketch, "E700.MirrorC", {"center": v(-456.1, 75) * mm, "radius": 4.5 * mm});
            skCircle(sketch, "E701.MirrorC", {"center": v(-366.1, 90) * mm, "radius": 4.5 * mm});
            skCircle(sketch, "E702.MirrorC", {"center": v(-276.1, 285) * mm, "radius": 4.5 * mm});
            skCircle(sketch, "E703.MirrorC", {"center": v(-216.1, 135) * mm, "radius": 4.5 * mm});
            skCircle(sketch, "E704.MirrorC", {"center": v(-96.1, 105) * mm, "radius": 4.5 * mm});
            skCircle(sketch, "E705.MirrorC", {"center": v(-336.1, 15) * mm, "radius": 4.5 * mm});
            skCircle(sketch, "E706.MirrorC", {"center": v(-186.1, 30) * mm, "radius": 4.5 * mm});
            skCircle(sketch, "E707.MirrorC", {"center": v(-126.1, 120) * mm, "radius": 4.5 * mm});
            skCircle(sketch, "E708.MirrorC", {"center": v(23.9, 45) * mm, "radius": 4.5 * mm});
            skCircle(sketch, "E709.MirrorC", {"center": v(-36.1, 225) * mm, "radius": 4.5 * mm});
            skCircle(sketch, "E710.MirrorC", {"center": v(233.9, 180) * mm, "radius": 4.5 * mm});
            skCircle(sketch, "E711.MirrorC", {"center": v(173.9, 210) * mm, "radius": 4.5 * mm});
            skCircle(sketch, "E712.MirrorC", {"center": v(173.9, 240) * mm, "radius": 4.5 * mm});
            skCircle(sketch, "E713.MirrorC", {"center": v(353.9, 300) * mm, "radius": 4.5 * mm});
            skCircle(sketch, "E714.MirrorC", {"center": v(263.9, 195) * mm, "radius": 4.5 * mm});
            skCircle(sketch, "E715.MirrorC", {"center": v(83.9, 255) * mm, "radius": 4.5 * mm});
            skCircle(sketch, "E716.MirrorC", {"center": v(323.9, 165) * mm, "radius": 4.5 * mm});
            skCircle(sketch, "E717.MirrorC", {"center": v(413.9, 150) * mm, "radius": 4.5 * mm});
            skCircle(sketch, "E718.MirrorC", {"center": v(-426.1, 270) * mm, "radius": 4.5 * mm});
            skCircle(sketch, "E719.MirrorC", {"center": v(-546.1, 150) * mm, "radius": 4.5 * mm});
            skCircle(sketch, "E720.MirrorC", {"center": v(23.9, 195) * mm, "radius": 4.5 * mm});
            skCircle(sketch, "E721.MirrorC", {"center": v(593.9, 90) * mm, "radius": 4.5 * mm});
            skCircle(sketch, "E722.MirrorC", {"center": v(503.9, 75) * mm, "radius": 4.5 * mm});
            skCircle(sketch, "E723.MirrorC", {"center": v(533.9, 270) * mm, "radius": 4.5 * mm});
            skCircle(sketch, "E724.MirrorC", {"center": v(683.9, 285) * mm, "radius": 4.5 * mm});
            skCircle(sketch, "E725.MirrorC", {"center": v(593.9, 60) * mm, "radius": 4.5 * mm});
            skCircle(sketch, "E726.MirrorC", {"center": v(623.9, 15) * mm, "radius": 4.5 * mm});
            skCircle(sketch, "E727.MirrorC", {"center": v(593.9, 120) * mm, "radius": 4.5 * mm});
            skCircle(sketch, "E728.MirrorC", {"center": v(833.9, 120) * mm, "radius": 4.5 * mm});
            skCircle(sketch, "E729.MirrorC", {"center": v(773.9, 30) * mm, "radius": 4.5 * mm});
            skCircle(sketch, "E730.MirrorC", {"center": v(743.9, 135) * mm, "radius": 4.5 * mm});
            skCircle(sketch, "E731.MirrorC", {"center": v(983.9, 45) * mm, "radius": 4.5 * mm});
            skCircle(sketch, "E732.MirrorC", {"center": v(923.9, 225) * mm, "radius": 4.5 * mm});
            skCircle(sketch, "E733.MirrorC", {"center": v(863.9, 105) * mm, "radius": 4.5 * mm});
            skCircle(sketch, "E734.MirrorC", {"center": v(1133.9, 240) * mm, "radius": 4.5 * mm});
            skCircle(sketch, "E735.MirrorC", {"center": v(1133.9, 210) * mm, "radius": 4.5 * mm});
            skCircle(sketch, "E736.MirrorC", {"center": v(-6.1, 180) * mm, "radius": 4.5 * mm});
            skCircle(sketch, "E737.MirrorC", {"center": v(1043.9, 255) * mm, "radius": 4.5 * mm});
            skCircle(sketch, "E738.MirrorC", {"center": v(1283.9, 165) * mm, "radius": 4.5 * mm});
            skCircle(sketch, "E739.MirrorC", {"center": v(1223.9, 195) * mm, "radius": 4.5 * mm});
            skCircle(sketch, "E740.MirrorC", {"center": v(1193.9, 180) * mm, "radius": 4.5 * mm});
            skCircle(sketch, "E741.MirrorC", {"center": v(1343.9, 285) * mm, "radius": 4.5 * mm});
            skCircle(sketch, "E742.MirrorC", {"center": v(1313.9, 300) * mm, "radius": 4.5 * mm});
            skCircle(sketch, "E743.MirrorC", {"center": v(-366.1, 150) * mm, "radius": 4.5 * mm});
            skCircle(sketch, "E744.MirrorC", {"center": v(-186.1, 90) * mm, "radius": 4.5 * mm});
            skCircle(sketch, "E745.MirrorC", {"center": v(-426.1, 300) * mm, "radius": 4.5 * mm});
            skCircle(sketch, "E746.MirrorC", {"center": v(-246.1, 270) * mm, "radius": 4.5 * mm});
            skCircle(sketch, "E747.MirrorC", {"center": v(-96.1, 285) * mm, "radius": 4.5 * mm});
            skCircle(sketch, "E748.MirrorC", {"center": v(-276.1, 75) * mm, "radius": 4.5 * mm});
            skCircle(sketch, "E749.MirrorC", {"center": v(-156.1, 15) * mm, "radius": 4.5 * mm});
            skCircle(sketch, "E750.MirrorC", {"center": v(-186.1, 60) * mm, "radius": 4.5 * mm});
            skCircle(sketch, "E751.MirrorC", {"center": v(53.9, 120) * mm, "radius": 4.5 * mm});
            skCircle(sketch, "E752.MirrorC", {"center": v(-6.1, 30) * mm, "radius": 4.5 * mm});
            skCircle(sketch, "E753.MirrorC", {"center": v(203.9, 45) * mm, "radius": 4.5 * mm});
            skCircle(sketch, "E754.MirrorC", {"center": v(-36.1, 135) * mm, "radius": 4.5 * mm});
            skCircle(sketch, "E755.MirrorC", {"center": v(143.9, 225) * mm, "radius": 4.5 * mm});
            skCircle(sketch, "E756.MirrorC", {"center": v(353.9, 240) * mm, "radius": 4.5 * mm});
            skCircle(sketch, "E757.MirrorC", {"center": v(83.9, 105) * mm, "radius": 4.5 * mm});
            skCircle(sketch, "E758.MirrorC", {"center": v(353.9, 210) * mm, "radius": 4.5 * mm});
            skCircle(sketch, "E759.MirrorC", {"center": v(263.9, 255) * mm, "radius": 4.5 * mm});
            skCircle(sketch, "E760.MirrorC", {"center": v(443.9, 195) * mm, "radius": 4.5 * mm});
            skCircle(sketch, "E761.MirrorC", {"center": v(413.9, 180) * mm, "radius": 4.5 * mm});
            skCircle(sketch, "E762.MirrorC", {"center": v(-456.1, 165) * mm, "radius": 4.5 * mm});
            skCircle(sketch, "E763.MirrorC", {"center": v(-516.1, 195) * mm, "radius": 4.5 * mm});
            skCircle(sketch, "E764.MirrorC", {"center": v(-546.1, 180) * mm, "radius": 4.5 * mm});
            skCircle(sketch, "E765.MirrorC", {"center": v(533.9, 300) * mm, "radius": 4.5 * mm});
            skCircle(sketch, "E766.MirrorC", {"center": v(593.9, 150) * mm, "radius": 4.5 * mm});
            skCircle(sketch, "E767.MirrorC", {"center": v(503.9, 165) * mm, "radius": 4.5 * mm});
            skCircle(sketch, "E768.MirrorC", {"center": v(683.9, 75) * mm, "radius": 4.5 * mm});
            skCircle(sketch, "E769.MirrorC", {"center": v(713.9, 270) * mm, "radius": 4.5 * mm});
            skCircle(sketch, "E770.MirrorC", {"center": v(803.9, 15) * mm, "radius": 4.5 * mm});
            skCircle(sketch, "E771.MirrorC", {"center": v(773.9, 60) * mm, "radius": 4.5 * mm});
            skCircle(sketch, "E772.MirrorC", {"center": v(773.9, 90) * mm, "radius": 4.5 * mm});
            skCircle(sketch, "E773.MirrorC", {"center": v(1013.9, 120) * mm, "radius": 4.5 * mm});
            skCircle(sketch, "E774.MirrorC", {"center": v(953.9, 30) * mm, "radius": 4.5 * mm});
            skCircle(sketch, "E775.MirrorC", {"center": v(923.9, 135) * mm, "radius": 4.5 * mm});
            skCircle(sketch, "E776.MirrorC", {"center": v(863.9, 285) * mm, "radius": 4.5 * mm});
            skCircle(sketch, "E777.MirrorC", {"center": v(1103.9, 225) * mm, "radius": 4.5 * mm});
            skCircle(sketch, "E778.MirrorC", {"center": v(1043.9, 105) * mm, "radius": 4.5 * mm});
            skCircle(sketch, "E779.MirrorC", {"center": v(1313.9, 210) * mm, "radius": 4.5 * mm});
            skCircle(sketch, "E780.MirrorC", {"center": v(1223.9, 255) * mm, "radius": 4.5 * mm});
            skCircle(sketch, "E781.MirrorC", {"center": v(1163.9, 45) * mm, "radius": 4.5 * mm});
            skCircle(sketch, "E782.MirrorC", {"center": v(1313.9, 240) * mm, "radius": 4.5 * mm});
            skCircle(sketch, "E783.MirrorC", {"center": v(1073.9, 210) * mm, "radius": 4.5 * mm});
            skCircle(sketch, "E784.MirrorC", {"center": v(863.9, 225) * mm, "radius": 4.5 * mm});
            skCircle(sketch, "E785.MirrorC", {"center": v(-246.1, 30) * mm, "radius": 4.5 * mm});
            skCircle(sketch, "E786.MirrorC", {"center": v(-96.1, 225) * mm, "radius": 4.5 * mm});
            skCircle(sketch, "E787.MirrorC", {"center": v(-276.1, 135) * mm, "radius": 4.5 * mm});
            skCircle(sketch, "E788.MirrorC", {"center": v(803.9, 285) * mm, "radius": 4.5 * mm});
            skCircle(sketch, "E789.MirrorC", {"center": v(563.9, 15) * mm, "radius": 4.5 * mm});
            skCircle(sketch, "E790.MirrorC", {"center": v(-186.1, 120) * mm, "radius": 4.5 * mm});
            skCircle(sketch, "E791.MirrorC", {"center": v(293.9, 210) * mm, "radius": 4.5 * mm});
            skCircle(sketch, "E792.MirrorC", {"center": v(-396.1, 15) * mm, "radius": 4.5 * mm});
            skCircle(sketch, "E793.MirrorC", {"center": v(203.9, 195) * mm, "radius": 4.5 * mm});
            skCircle(sketch, "E794.MirrorC", {"center": v(-426.1, 90) * mm, "radius": 4.5 * mm});
            skCircle(sketch, "E795.MirrorC", {"center": v(-336.1, 285) * mm, "radius": 4.5 * mm});
            skCircle(sketch, "E796.MirrorC", {"center": v(533.9, 60) * mm, "radius": 4.5 * mm});
            skCircle(sketch, "E797.MirrorC", {"center": v(1313.9, 60) * mm, "radius": 4.5 * mm});
            skCircle(sketch, "E798.MirrorC", {"center": v(-546.1, 120) * mm, "radius": 4.5 * mm});
            skCircle(sketch, "E799.MirrorC", {"center": v(413.9, 120) * mm, "radius": 4.5 * mm});
            skCircle(sketch, "E800.MirrorC", {"center": v(353.9, 30) * mm, "radius": 4.5 * mm});
            skCircle(sketch, "E801.MirrorC", {"center": v(-6.1, 150) * mm, "radius": 4.5 * mm});
            skCircle(sketch, "E802.MirrorC", {"center": v(-516.1, 105) * mm, "radius": 4.5 * mm});
            skCircle(sketch, "E803.MirrorC", {"center": v(1313.9, 90) * mm, "radius": 4.5 * mm});
            skCircle(sketch, "E804.MirrorC", {"center": v(203.9, 15) * mm, "radius": 4.5 * mm});
            skCircle(sketch, "E805.MirrorC", {"center": v(-576.1, 45) * mm, "radius": 4.5 * mm});
            skCircle(sketch, "E806.MirrorC", {"center": v(-516.1, 255) * mm, "radius": 4.5 * mm});
            skCircle(sketch, "E807.MirrorC", {"center": v(-396.1, 45) * mm, "radius": 4.5 * mm});
            skCircle(sketch, "E808.MirrorC", {"center": v(-186.1, 180) * mm, "radius": 4.5 * mm});
            skCircle(sketch, "E809.MirrorC", {"center": v(-246.1, 240) * mm, "radius": 4.5 * mm});
            skCircle(sketch, "E810.MirrorC", {"center": v(-246.1, 210) * mm, "radius": 4.5 * mm});
            skCircle(sketch, "E811.MirrorC", {"center": v(-456.1, 225) * mm, "radius": 4.5 * mm});
            skCircle(sketch, "E812.MirrorC", {"center": v(713.9, 300) * mm, "radius": 4.5 * mm});
            skCircle(sketch, "E813.MirrorC", {"center": v(623.9, 195) * mm, "radius": 4.5 * mm});
            skCircle(sketch, "E814.MirrorC", {"center": v(533.9, 210) * mm, "radius": 4.5 * mm});
            skCircle(sketch, "E815.MirrorC", {"center": v(443.9, 255) * mm, "radius": 4.5 * mm});
            skCircle(sketch, "E816.MirrorC", {"center": v(593.9, 180) * mm, "radius": 4.5 * mm});
            skCircle(sketch, "E817.MirrorC", {"center": v(323.9, 225) * mm, "radius": 4.5 * mm});
            skCircle(sketch, "E818.MirrorC", {"center": v(263.9, 105) * mm, "radius": 4.5 * mm});
            skCircle(sketch, "E819.MirrorC", {"center": v(143.9, 135) * mm, "radius": 4.5 * mm});
            skCircle(sketch, "E820.MirrorC", {"center": v(83.9, 285) * mm, "radius": 4.5 * mm});
            skCircle(sketch, "E821.MirrorC", {"center": v(383.9, 45) * mm, "radius": 4.5 * mm});
            skCircle(sketch, "E822.MirrorC", {"center": v(-66.1, 270) * mm, "radius": 4.5 * mm});
            skCircle(sketch, "E823.MirrorC", {"center": v(-6.1, 90) * mm, "radius": 4.5 * mm});
            skCircle(sketch, "E824.MirrorC", {"center": v(233.9, 120) * mm, "radius": 4.5 * mm});
            skCircle(sketch, "E825.MirrorC", {"center": v(173.9, 30) * mm, "radius": 4.5 * mm});
            skCircle(sketch, "E826.MirrorC", {"center": v(23.9, 15) * mm, "radius": 4.5 * mm});
            skCircle(sketch, "E827.MirrorC", {"center": v(-6.1, 60) * mm, "radius": 4.5 * mm});
            skCircle(sketch, "E828.MirrorC", {"center": v(-96.1, 75) * mm, "radius": 4.5 * mm});
            skCircle(sketch, "E829.MirrorC", {"center": v(-276.1, 165) * mm, "radius": 4.5 * mm});
            skCircle(sketch, "E830.MirrorC", {"center": v(893.9, 270) * mm, "radius": 4.5 * mm});
            skCircle(sketch, "E831.MirrorC", {"center": v(623.9, 75) * mm, "radius": 4.5 * mm});
            skCircle(sketch, "E832.MirrorC", {"center": v(893.9, 30) * mm, "radius": 4.5 * mm});
            skCircle(sketch, "E833.MirrorC", {"center": v(713.9, 90) * mm, "radius": 4.5 * mm});
            skCircle(sketch, "E834.MirrorC", {"center": v(263.9, 225) * mm, "radius": 4.5 * mm});
            skCircle(sketch, "E835.MirrorC", {"center": v(773.9, 120) * mm, "radius": 4.5 * mm});
            skCircle(sketch, "E836.MirrorC", {"center": v(713.9, 60) * mm, "radius": 4.5 * mm});
            skCircle(sketch, "E837.MirrorC", {"center": v(-156.1, 105) * mm, "radius": 4.5 * mm});
            skCircle(sketch, "E838.MirrorC", {"center": v(263.9, 165) * mm, "radius": 4.5 * mm});
            skCircle(sketch, "E839.MirrorC", {"center": v(113.9, 210) * mm, "radius": 4.5 * mm});
            skCircle(sketch, "E840.MirrorC", {"center": v(83.9, 225) * mm, "radius": 4.5 * mm});
            skCircle(sketch, "E841.MirrorC", {"center": v(623.9, 285) * mm, "radius": 4.5 * mm});
            skCircle(sketch, "E842.MirrorC", {"center": v(1253.9, 270) * mm, "radius": 4.5 * mm});
            skCircle(sketch, "E843.MirrorC", {"center": v(83.9, 75) * mm, "radius": 4.5 * mm});
            skCircle(sketch, "E844.MirrorC", {"center": v(1193.9, 120) * mm, "radius": 4.5 * mm});
            skCircle(sketch, "E845.MirrorC", {"center": v(683.9, 165) * mm, "radius": 4.5 * mm});
            skCircle(sketch, "E846.MirrorC", {"center": v(-96.1, 165) * mm, "radius": 4.5 * mm});
            skCircle(sketch, "E847.MirrorC", {"center": v(-66.1, 300) * mm, "radius": 4.5 * mm});
            skCircle(sketch, "E848.MirrorC", {"center": v(-336.1, 255) * mm, "radius": 4.5 * mm});
            skCircle(sketch, "E849.MirrorC", {"center": v(-156.1, 195) * mm, "radius": 4.5 * mm});
            skCircle(sketch, "E850.MirrorC", {"center": v(863.9, 135) * mm, "radius": 4.5 * mm});
            skCircle(sketch, "E851.MirrorC", {"center": v(-486.1, 270) * mm, "radius": 4.5 * mm});
            skCircle(sketch, "E852.MirrorC", {"center": v(1103.9, 135) * mm, "radius": 4.5 * mm});
            skCircle(sketch, "E853.MirrorC", {"center": v(1043.9, 285) * mm, "radius": 4.5 * mm});
            skCircle(sketch, "E854.MirrorC", {"center": v(863.9, 75) * mm, "radius": 4.5 * mm});
            skCircle(sketch, "E855.MirrorC", {"center": v(1133.9, 30) * mm, "radius": 4.5 * mm});
            skCircle(sketch, "E856.MirrorC", {"center": v(743.9, 15) * mm, "radius": 4.5 * mm});
            skCircle(sketch, "E857.MirrorC", {"center": v(23.9, 255) * mm, "radius": 4.5 * mm});
            skCircle(sketch, "E858.MirrorC", {"center": v(713.9, 30) * mm, "radius": 4.5 * mm});
            skCircle(sketch, "E859.MirrorC", {"center": v(323.9, 45) * mm, "radius": 4.5 * mm});
            skCircle(sketch, "E860.MirrorC", {"center": v(-36.1, 45) * mm, "radius": 4.5 * mm});
            skCircle(sketch, "E861.MirrorC", {"center": v(953.9, 90) * mm, "radius": 4.5 * mm});
            skCircle(sketch, "E862.MirrorC", {"center": v(953.9, 60) * mm, "radius": 4.5 * mm});
            skCircle(sketch, "E863.MirrorC", {"center": v(983.9, 105) * mm, "radius": 4.5 * mm});
            skCircle(sketch, "E864.MirrorC", {"center": v(983.9, 15) * mm, "radius": 4.5 * mm});
            skCircle(sketch, "E865.MirrorC", {"center": v(473.9, 240) * mm, "radius": 4.5 * mm});
            skCircle(sketch, "E866.MirrorC", {"center": v(533.9, 240) * mm, "radius": 4.5 * mm});
            skCircle(sketch, "E867.MirrorC", {"center": v(773.9, 150) * mm, "radius": 4.5 * mm});
            skCircle(sketch, "E868.MirrorC", {"center": v(23.9, 105) * mm, "radius": 4.5 * mm});
            skCircle(sketch, "E869.MirrorC", {"center": v(293.9, 300) * mm, "radius": 4.5 * mm});
            skCircle(sketch, "E870.MirrorC", {"center": v(-426.1, 210) * mm, "radius": 4.5 * mm});
            skCircle(sketch, "E871.MirrorC", {"center": v(1283.9, 225) * mm, "radius": 4.5 * mm});
            skCircle(sketch, "E872.MirrorC", {"center": v(1223.9, 105) * mm, "radius": 4.5 * mm});
            skCircle(sketch, "E873.MirrorC", {"center": v(683.9, 135) * mm, "radius": 4.5 * mm});
            skCircle(sketch, "E874.MirrorC", {"center": v(-246.1, 300) * mm, "radius": 4.5 * mm});
            skCircle(sketch, "E875.MirrorC", {"center": v(-336.1, 195) * mm, "radius": 4.5 * mm});
            skCircle(sketch, "E876.MirrorC", {"center": v(-186.1, 150) * mm, "radius": 4.5 * mm});
            skCircle(sketch, "E877.MirrorC", {"center": v(-426.1, 240) * mm, "radius": 4.5 * mm});
            skCircle(sketch, "E878.MirrorC", {"center": v(653.9, 270) * mm, "radius": 4.5 * mm});
            skCircle(sketch, "E879.MirrorC", {"center": v(1283.9, 135) * mm, "radius": 4.5 * mm});
            skCircle(sketch, "E880.MirrorC", {"center": v(893.9, 300) * mm, "radius": 4.5 * mm});
            skCircle(sketch, "E881.MirrorC", {"center": v(113.9, 270) * mm, "radius": 4.5 * mm});
            skCircle(sketch, "E882.MirrorC", {"center": v(1223.9, 75) * mm, "radius": 4.5 * mm});
            skCircle(sketch, "E883.MirrorC", {"center": v(1043.9, 165) * mm, "radius": 4.5 * mm});
            skCircle(sketch, "E884.MirrorC", {"center": v(1133.9, 90) * mm, "radius": 4.5 * mm});
            skCircle(sketch, "E885.MirrorC", {"center": v(1073.9, 270) * mm, "radius": 4.5 * mm});
            skCircle(sketch, "E886.MirrorC", {"center": v(1313.9, 30) * mm, "radius": 4.5 * mm});
            skCircle(sketch, "E887.MirrorC", {"center": v(263.9, 285) * mm, "radius": 4.5 * mm});
            skCircle(sketch, "E888.MirrorC", {"center": v(1073.9, 300) * mm, "radius": 4.5 * mm});
            skCircle(sketch, "E889.MirrorC", {"center": v(323.9, 135) * mm, "radius": 4.5 * mm});
            skCircle(sketch, "E890.MirrorC", {"center": v(533.9, 150) * mm, "radius": 4.5 * mm});
            skCircle(sketch, "E891.MirrorC", {"center": v(803.9, 105) * mm, "radius": 4.5 * mm});
            skCircle(sketch, "E892.MirrorC", {"center": v(-366.1, 180) * mm, "radius": 4.5 * mm});
            skCircle(sketch, "E893.MirrorC", {"center": v(1043.9, 225) * mm, "radius": 4.5 * mm});
            skCircle(sketch, "E894.MirrorC", {"center": v(173.9, 60) * mm, "radius": 4.5 * mm});
            skCircle(sketch, "E895.MirrorC", {"center": v(1133.9, 150) * mm, "radius": 4.5 * mm});
            skCircle(sketch, "E896.MirrorC", {"center": v(173.9, 90) * mm, "radius": 4.5 * mm});
            skCircle(sketch, "E897.MirrorC", {"center": v(563.9, 45) * mm, "radius": 4.5 * mm});
            skCircle(sketch, "E898.MirrorC", {"center": v(623.9, 165) * mm, "radius": 4.5 * mm});
            skCircle(sketch, "E899.MirrorC", {"center": v(953.9, 150) * mm, "radius": 4.5 * mm});
            skCircle(sketch, "E900.MirrorC", {"center": v(1043.9, 75) * mm, "radius": 4.5 * mm});
            skCircle(sketch, "E901.MirrorC", {"center": v(1223.9, 285) * mm, "radius": 4.5 * mm});
            skCircle(sketch, "E902.MirrorC", {"center": v(1133.9, 60) * mm, "radius": 4.5 * mm});
            skCircle(sketch, "E903.MirrorC", {"center": v(1163.9, 15) * mm, "radius": 4.5 * mm});
            skLineSegment(sketch, "E904.MirrorCS", {"start": v(1343.9, 345) * mm, "end": v(1343.9, 345) * mm});
            skLineSegment(sketch, "E905.MirrorCS", {"start": v(1373.9, 360) * mm, "end": v(1373.9, 360) * mm});
            skSolve(sketch);
        }
        {
            var Q0;
            Q0=makeQuery(id+"F6.imprint","IMPRINT",FACE,{"disambiguationData":[TD([[makeQuery(id+"F6.imprint","IMPRINT",EDGE,{"derivedFrom":sQuery(id+"F6.wireOp",EDGE,"E637.MirrorC")}),-1.0]])]});
            var Q1;
            Q1=makeQuery(id+"F6.imprint","IMPRINT",FACE,{"disambiguationData":[TD([[makeQuery(id+"F6.imprint","IMPRINT",EDGE,{"derivedFrom":sQuery(id+"F6.wireOp",EDGE,"E586.MirrorC")}),-1.0]])]});
            var Q2;
            Q2=makeQuery(id+"F6.imprint","IMPRINT",FACE,{"disambiguationData":[TD([[makeQuery(id+"F6.imprint","IMPRINT",EDGE,{"derivedFrom":sQuery(id+"F6.wireOp",EDGE,"E40.0.2.0")}),1.0]])]});
            var Q3;
            Q3=makeQuery(id+"F6.imprint","IMPRINT",FACE,{"disambiguationData":[TD([[makeQuery(id+"F6.imprint","IMPRINT",EDGE,{"derivedFrom":sQuery(id+"F6.wireOp",EDGE,"E392.MirrorC")}),-1.0]])]});
            var Q4;
            Q4=makeQuery(id+"F6.imprint","IMPRINT",FACE,{"disambiguationData":[TD([[makeQuery(id+"F6.imprint","IMPRINT",EDGE,{"derivedFrom":sQuery(id+"F6.wireOp",EDGE,"E40.0.3.0")}),1.0]])]});
            var Q5;
            Q5=makeQuery(id+"F6.imprint","IMPRINT",FACE,{"disambiguationData":[TD([[makeQuery(id+"F6.imprint","IMPRINT",EDGE,{"derivedFrom":sQuery(id+"F6.wireOp",EDGE,"E340.MirrorC")}),-1.0]])]});
            var Q6;
            Q6=makeQuery(id+"F6.imprint","IMPRINT",FACE,{"disambiguationData":[TD([[makeQuery(id+"F6.imprint","IMPRINT",EDGE,{"derivedFrom":sQuery(id+"F6.wireOp",EDGE,"E40.0.4.0")}),1.0]])]});
            var Q7;
            Q7=makeQuery(id+"F6.imprint","IMPRINT",FACE,{"disambiguationData":[TD([[makeQuery(id+"F6.imprint","IMPRINT",EDGE,{"derivedFrom":sQuery(id+"F6.wireOp",EDGE,"E40.0.5.0")}),1.0]])]});
            var Q8;
            Q8=makeQuery(id+"F6.imprint","IMPRINT",FACE,{"disambiguationData":[TD([[makeQuery(id+"F6.imprint","IMPRINT",EDGE,{"derivedFrom":sQuery(id+"F6.wireOp",EDGE,"E739.MirrorC")}),-1.0]])]});
            var Q9;
            Q9=makeQuery(id+"F6.imprint","IMPRINT",FACE,{"disambiguationData":[TD([[makeQuery(id+"F6.imprint","IMPRINT",EDGE,{"derivedFrom":sQuery(id+"F6.wireOp",EDGE,"E40.0.6.0")}),1.0]])]});
            var Q10;
            Q10=makeQuery(id+"F6.imprint","IMPRINT",FACE,{"disambiguationData":[TD([[makeQuery(id+"F6.imprint","IMPRINT",EDGE,{"derivedFrom":sQuery(id+"F6.wireOp",EDGE,"E40.0.7.0")}),1.0]])]});
            var Q11;
            Q11=makeQuery(id+"F6.imprint","IMPRINT",FACE,{"disambiguationData":[TD([[makeQuery(id+"F6.imprint","IMPRINT",EDGE,{"derivedFrom":sQuery(id+"F6.wireOp",EDGE,"E600.MirrorC")}),-1.0]])]});
            var Q12;
            Q12=makeQuery(id+"F6.imprint","IMPRINT",FACE,{"disambiguationData":[TD([[makeQuery(id+"F6.imprint","IMPRINT",EDGE,{"derivedFrom":sQuery(id+"F6.wireOp",EDGE,"E652.MirrorC")}),-1.0]])]});
            var Q13;
            Q13=makeQuery(id+"F6.imprint","IMPRINT",FACE,{"disambiguationData":[TD([[makeQuery(id+"F6.imprint","IMPRINT",EDGE,{"derivedFrom":sQuery(id+"F6.wireOp",EDGE,"E40.0.8.0")}),1.0]])]});
            var Q14;
            Q14=makeQuery(id+"F6.imprint","IMPRINT",FACE,{"disambiguationData":[TD([[makeQuery(id+"F6.imprint","IMPRINT",EDGE,{"derivedFrom":sQuery(id+"F6.wireOp",EDGE,"E354.MirrorC")}),-1.0]])]});
            var Q15;
            Q15=makeQuery(id+"F6.imprint","IMPRINT",FACE,{"disambiguationData":[TD([[makeQuery(id+"F6.imprint","IMPRINT",EDGE,{"derivedFrom":sQuery(id+"F6.wireOp",EDGE,"E40.0.9.0")}),1.0]])]});
            var Q16;
            Q16=makeQuery(id+"F6.imprint","IMPRINT",FACE,{"disambiguationData":[TD([[makeQuery(id+"F6.imprint","IMPRINT",EDGE,{"derivedFrom":sQuery(id+"F6.wireOp",EDGE,"E406.MirrorC")}),-1.0]])]});
            var Q17;
            Q17=makeQuery(id+"F6.imprint","IMPRINT",FACE,{"disambiguationData":[TD([[makeQuery(id+"F6.imprint","IMPRINT",EDGE,{"derivedFrom":sQuery(id+"F6.wireOp",EDGE,"E40.0.10.0")}),1.0]])]});
            var Q18;
            Q18=makeQuery(id+"F6.imprint","IMPRINT",FACE,{"disambiguationData":[TD([[makeQuery(id+"F6.imprint","IMPRINT",EDGE,{"derivedFrom":sQuery(id+"F6.wireOp",EDGE,"E40.0.11.0")}),1.0]])]});
            var Q19;
            Q19=makeQuery(id+"F6.imprint","IMPRINT",FACE,{"disambiguationData":[TD([[makeQuery(id+"F6.imprint","IMPRINT",EDGE,{"derivedFrom":sQuery(id+"F6.wireOp",EDGE,"E807.MirrorC")}),-1.0]])]});
            var Q20;
            Q20=makeQuery(id+"F6.imprint","IMPRINT",FACE,{"disambiguationData":[TD([[makeQuery(id+"F6.imprint","IMPRINT",EDGE,{"derivedFrom":sQuery(id+"F6.wireOp",EDGE,"E607.MirrorC")}),-1.0]])]});
            var Q21;
            Q21=makeQuery(id+"F6.imprint","IMPRINT",FACE,{"disambiguationData":[TD([[makeQuery(id+"F6.imprint","IMPRINT",EDGE,{"derivedFrom":sQuery(id+"F6.wireOp",EDGE,"E360.MirrorC")}),-1.0]])]});
            var Q22;
            Q22=makeQuery(id+"F6.imprint","IMPRINT",FACE,{"disambiguationData":[TD([[makeQuery(id+"F6.imprint","IMPRINT",EDGE,{"derivedFrom":sQuery(id+"F6.wireOp",EDGE,"E555.MirrorC")}),-1.0]])]});
            var Q23;
            Q23=makeQuery(id+"F6.imprint","IMPRINT",FACE,{"disambiguationData":[TD([[makeQuery(id+"F6.imprint","IMPRINT",EDGE,{"derivedFrom":sQuery(id+"F6.wireOp",EDGE,"E346.MirrorC")}),-1.0]])]});
            var Q24;
            Q24=makeQuery(id+"F6.imprint","IMPRINT",FACE,{"disambiguationData":[TD([[makeQuery(id+"F6.imprint","IMPRINT",EDGE,{"derivedFrom":sQuery(id+"F6.wireOp",EDGE,"E761.MirrorC")}),-1.0]])]});
            var Q25;
            Q25=makeQuery(id+"F6.imprint","IMPRINT",FACE,{"disambiguationData":[TD([[makeQuery(id+"F6.imprint","IMPRINT",EDGE,{"derivedFrom":sQuery(id+"F6.wireOp",EDGE,"E570.MirrorC")}),-1.0]])]});
            var Q26;
            Q26=makeQuery(id+"F6.imprint","IMPRINT",FACE,{"disambiguationData":[TD([[makeQuery(id+"F6.imprint","IMPRINT",EDGE,{"derivedFrom":sQuery(id+"F6.wireOp",EDGE,"E622.MirrorC")}),-1.0]])]});
            var Q27;
            Q27=makeQuery(id+"F6.imprint","IMPRINT",FACE,{"disambiguationData":[TD([[makeQuery(id+"F6.imprint","IMPRINT",EDGE,{"derivedFrom":sQuery(id+"F6.wireOp",EDGE,"E376.MirrorC")}),-1.0]])]});
            var Q28;
            Q28=makeQuery(id+"F6.imprint","IMPRINT",FACE,{"disambiguationData":[TD([[makeQuery(id+"F6.imprint","IMPRINT",EDGE,{"derivedFrom":sQuery(id+"F6.wireOp",EDGE,"E698.MirrorC")}),-1.0]])]});
            var Q29;
            Q29=makeQuery(id+"F6.imprint","IMPRINT",FACE,{"disambiguationData":[TD([[makeQuery(id+"F6.imprint","IMPRINT",EDGE,{"derivedFrom":sQuery(id+"F6.wireOp",EDGE,"E452.MirrorC")}),-1.0]])]});
            var Q30;
            Q30=makeQuery(id+"F6.imprint","IMPRINT",FACE,{"disambiguationData":[TD([[makeQuery(id+"F6.imprint","IMPRINT",EDGE,{"derivedFrom":sQuery(id+"F6.wireOp",EDGE,"E400.MirrorC")}),-1.0]])]});
            var Q31;
            Q31=makeQuery(id+"F6.imprint","IMPRINT",FACE,{"disambiguationData":[TD([[makeQuery(id+"F6.imprint","IMPRINT",EDGE,{"derivedFrom":sQuery(id+"F6.wireOp",EDGE,"E382.MirrorC")}),-1.0]])]});
            var Q32;
            Q32=makeQuery(id+"F6.imprint","IMPRINT",FACE,{"disambiguationData":[TD([[makeQuery(id+"F6.imprint","IMPRINT",EDGE,{"derivedFrom":sQuery(id+"F6.wireOp",EDGE,"E800.MirrorC")}),-1.0]])]});
            var Q33;
            Q33=makeQuery(id+"F6.imprint","IMPRINT",FACE,{"disambiguationData":[TD([[makeQuery(id+"F6.imprint","IMPRINT",EDGE,{"derivedFrom":sQuery(id+"F6.wireOp",EDGE,"E661.MirrorC")}),-1.0]])]});
            var Q34;
            Q34=makeQuery(id+"F6.imprint","IMPRINT",FACE,{"disambiguationData":[TD([[makeQuery(id+"F6.imprint","IMPRINT",EDGE,{"derivedFrom":sQuery(id+"F6.wireOp",EDGE,"E713.MirrorC")}),-1.0]])]});
            var Q35;
            Q35=makeQuery(id+"F6.imprint","IMPRINT",FACE,{"disambiguationData":[TD([[makeQuery(id+"F6.imprint","IMPRINT",EDGE,{"derivedFrom":sQuery(id+"F6.wireOp",EDGE,"E415.MirrorC")}),-1.0]])]});
            var Q36;
            Q36=makeQuery(id+"F6.imprint","IMPRINT",FACE,{"disambiguationData":[TD([[makeQuery(id+"F6.imprint","IMPRINT",EDGE,{"derivedFrom":sQuery(id+"F6.wireOp",EDGE,"E468.MirrorC")}),-1.0]])]});
            var Q37;
            Q37=makeQuery(id+"F6.imprint","IMPRINT",FACE,{"disambiguationData":[TD([[makeQuery(id+"F6.imprint","IMPRINT",EDGE,{"derivedFrom":sQuery(id+"F6.wireOp",EDGE,"E815.MirrorC")}),-1.0]])]});
            var Q38;
            Q38=makeQuery(id+"F6.imprint","IMPRINT",FACE,{"disambiguationData":[TD([[makeQuery(id+"F6.imprint","IMPRINT",EDGE,{"derivedFrom":sQuery(id+"F6.wireOp",EDGE,"E867.MirrorC")}),-1.0]])]});
            var Q39;
            Q39=makeQuery(id+"F6.imprint","IMPRINT",FACE,{"disambiguationData":[TD([[makeQuery(id+"F6.imprint","IMPRINT",EDGE,{"derivedFrom":sQuery(id+"F6.wireOp",EDGE,"E615.MirrorC")}),-1.0]])]});
            var Q40;
            Q40=makeQuery(id+"F6.imprint","IMPRINT",FACE,{"disambiguationData":[TD([[makeQuery(id+"F6.imprint","IMPRINT",EDGE,{"derivedFrom":sQuery(id+"F6.wireOp",EDGE,"E667.MirrorC")}),-1.0]])]});
            var Q41;
            Q41=makeQuery(id+"F6.imprint","IMPRINT",FACE,{"disambiguationData":[TD([[makeQuery(id+"F6.imprint","IMPRINT",EDGE,{"derivedFrom":sQuery(id+"F6.wireOp",EDGE,"E369.MirrorC")}),-1.0]])]});
            var Q42;
            Q42=makeQuery(id+"F6.imprint","IMPRINT",FACE,{"disambiguationData":[TD([[makeQuery(id+"F6.imprint","IMPRINT",EDGE,{"derivedFrom":sQuery(id+"F6.wireOp",EDGE,"E421.MirrorC")}),-1.0]])]});
            var Q43;
            Q43=makeQuery(id+"F6.imprint","IMPRINT",FACE,{"disambiguationData":[TD([[makeQuery(id+"F6.imprint","IMPRINT",EDGE,{"derivedFrom":sQuery(id+"F6.wireOp",EDGE,"E352.MirrorC")}),-1.0]])]});
            var Q44;
            Q44=makeQuery(id+"F6.imprint","IMPRINT",FACE,{"disambiguationData":[TD([[makeQuery(id+"F6.imprint","IMPRINT",EDGE,{"derivedFrom":sQuery(id+"F6.wireOp",EDGE,"E770.MirrorC")}),-1.0]])]});
            var Q45;
            Q45=makeQuery(id+"F6.imprint","IMPRINT",FACE,{"disambiguationData":[TD([[makeQuery(id+"F6.imprint","IMPRINT",EDGE,{"derivedFrom":sQuery(id+"F6.wireOp",EDGE,"E821.MirrorC")}),-1.0]])]});
            var Q46;
            Q46=makeQuery(id+"F6.imprint","IMPRINT",FACE,{"disambiguationData":[TD([[makeQuery(id+"F6.imprint","IMPRINT",EDGE,{"derivedFrom":sQuery(id+"F6.wireOp",EDGE,"E630.MirrorC")}),-1.0]])]});
            var Q47;
            Q47=makeQuery(id+"F6.imprint","IMPRINT",FACE,{"disambiguationData":[TD([[makeQuery(id+"F6.imprint","IMPRINT",EDGE,{"derivedFrom":sQuery(id+"F6.wireOp",EDGE,"E683.MirrorC")}),-1.0]])]});
            var Q48;
            Q48=makeQuery(id+"F6.imprint","IMPRINT",FACE,{"disambiguationData":[TD([[makeQuery(id+"F6.imprint","IMPRINT",EDGE,{"derivedFrom":sQuery(id+"F6.wireOp",EDGE,"E385.MirrorC")}),-1.0]])]});
            var Q49;
            Q49=makeQuery(id+"F6.imprint","IMPRINT",FACE,{"disambiguationData":[TD([[makeQuery(id+"F6.imprint","IMPRINT",EDGE,{"derivedFrom":sQuery(id+"F6.wireOp",EDGE,"E437.MirrorC")}),-1.0]])]});
            var Q50;
            Q50=makeQuery(id+"F6.imprint","IMPRINT",FACE,{"disambiguationData":[TD([[makeQuery(id+"F6.imprint","IMPRINT",EDGE,{"derivedFrom":sQuery(id+"F6.wireOp",EDGE,"E366.MirrorC")}),-1.0]])]});
            var Q51;
            Q51=makeQuery(id+"F6.imprint","IMPRINT",FACE,{"disambiguationData":[TD([[makeQuery(id+"F6.imprint","IMPRINT",EDGE,{"derivedFrom":sQuery(id+"F6.wireOp",EDGE,"E836.MirrorC")}),-1.0]])]});
            var Q52;
            Q52=makeQuery(id+"F6.imprint","IMPRINT",FACE,{"disambiguationData":[TD([[makeQuery(id+"F6.imprint","IMPRINT",EDGE,{"derivedFrom":sQuery(id+"F6.wireOp",EDGE,"E785.MirrorC")}),-1.0]])]});
            var Q53;
            Q53=makeQuery(id+"F6.imprint","IMPRINT",FACE,{"disambiguationData":[TD([[makeQuery(id+"F6.imprint","IMPRINT",EDGE,{"derivedFrom":sQuery(id+"F6.wireOp",EDGE,"E513.MirrorC")}),-1.0]])]});
            var Q54;
            Q54=makeQuery(id+"F6.imprint","IMPRINT",FACE,{"disambiguationData":[TD([[makeQuery(id+"F6.imprint","IMPRINT",EDGE,{"derivedFrom":sQuery(id+"F6.wireOp",EDGE,"E461.MirrorC")}),-1.0]])]});
            var Q55;
            Q55=makeQuery(id+"F6.imprint","IMPRINT",FACE,{"disambiguationData":[TD([[makeQuery(id+"F6.imprint","IMPRINT",EDGE,{"derivedFrom":sQuery(id+"F6.wireOp",EDGE,"E443.MirrorC")}),-1.0]])]});
            var Q56;
            Q56=makeQuery(id+"F6.imprint","IMPRINT",FACE,{"disambiguationData":[TD([[makeQuery(id+"F6.imprint","IMPRINT",EDGE,{"derivedFrom":sQuery(id+"F6.wireOp",EDGE,"E860.MirrorC")}),-1.0]])]});
            var Q57;
            Q57=makeQuery(id+"F6.imprint","IMPRINT",FACE,{"disambiguationData":[TD([[makeQuery(id+"F6.imprint","IMPRINT",EDGE,{"derivedFrom":sQuery(id+"F6.wireOp",EDGE,"E707.MirrorC")}),-1.0]])]});
            var Q58;
            Q58=makeQuery(id+"F6.imprint","IMPRINT",FACE,{"disambiguationData":[TD([[makeQuery(id+"F6.imprint","IMPRINT",EDGE,{"derivedFrom":sQuery(id+"F6.wireOp",EDGE,"E476.MirrorC")}),-1.0]])]});
            var Q59;
            Q59=makeQuery(id+"F6.imprint","IMPRINT",FACE,{"disambiguationData":[TD([[makeQuery(id+"F6.imprint","IMPRINT",EDGE,{"derivedFrom":sQuery(id+"F6.wireOp",EDGE,"E529.MirrorC")}),-1.0]])]});
            var Q60;
            Q60=makeQuery(id+"F6.imprint","IMPRINT",FACE,{"disambiguationData":[TD([[makeQuery(id+"F6.imprint","IMPRINT",EDGE,{"derivedFrom":sQuery(id+"F6.wireOp",EDGE,"E875.MirrorC")}),-1.0]])]});
            var Q61;
            Q61=makeQuery(id+"F6.imprint","IMPRINT",FACE,{"disambiguationData":[TD([[makeQuery(id+"F6.imprint","IMPRINT",EDGE,{"derivedFrom":sQuery(id+"F6.wireOp",EDGE,"E458.MirrorC")}),-1.0]])]});
            var Q62;
            Q62=makeQuery(id+"F6.imprint","IMPRINT",FACE,{"disambiguationData":[TD([[makeQuery(id+"F6.imprint","IMPRINT",EDGE,{"derivedFrom":sQuery(id+"F6.wireOp",EDGE,"E722.MirrorC")}),-1.0]])]});
            var Q63;
            Q63=makeQuery(id+"F6.imprint","IMPRINT",FACE,{"disambiguationData":[TD([[makeQuery(id+"F6.imprint","IMPRINT",EDGE,{"derivedFrom":sQuery(id+"F6.wireOp",EDGE,"E483.MirrorC")}),-1.0]])]});
            var Q64;
            Q64=makeQuery(id+"F6.imprint","IMPRINT",FACE,{"disambiguationData":[TD([[makeQuery(id+"F6.imprint","IMPRINT",EDGE,{"derivedFrom":sQuery(id+"F6.wireOp",EDGE,"E676.MirrorC")}),-1.0]])]});
            var Q65;
            Q65=makeQuery(id+"F6.imprint","IMPRINT",FACE,{"disambiguationData":[TD([[makeQuery(id+"F6.imprint","IMPRINT",EDGE,{"derivedFrom":sQuery(id+"F6.wireOp",EDGE,"E430.MirrorC")}),-1.0]])]});
            var Q66;
            Q66=makeQuery(id+"F6.imprint","IMPRINT",FACE,{"disambiguationData":[TD([[makeQuery(id+"F6.imprint","IMPRINT",EDGE,{"derivedFrom":sQuery(id+"F6.wireOp",EDGE,"E882.MirrorC")}),-1.0]])]});
            var Q67;
            Q67=makeQuery(id+"F6.imprint","IMPRINT",FACE,{"disambiguationData":[TD([[makeQuery(id+"F6.imprint","IMPRINT",EDGE,{"derivedFrom":sQuery(id+"F6.wireOp",EDGE,"E729.MirrorC")}),-1.0]])]});
            var Q68;
            Q68=makeQuery(id+"F6.imprint","IMPRINT",FACE,{"disambiguationData":[TD([[makeQuery(id+"F6.imprint","IMPRINT",EDGE,{"derivedFrom":sQuery(id+"F6.wireOp",EDGE,"E412.MirrorC")}),-1.0]])]});
            var Q69;
            Q69=makeQuery(id+"F6.imprint","IMPRINT",FACE,{"disambiguationData":[TD([[makeQuery(id+"F6.imprint","IMPRINT",EDGE,{"derivedFrom":sQuery(id+"F6.wireOp",EDGE,"E830.MirrorC")}),-1.0]])]});
            var Q70;
            Q70=makeQuery(id+"F6.imprint","IMPRINT",FACE,{"disambiguationData":[TD([[makeQuery(id+"F6.imprint","IMPRINT",EDGE,{"derivedFrom":sQuery(id+"F6.wireOp",EDGE,"E446.MirrorC")}),-1.0]])]});
            var Q71;
            Q71=makeQuery(id+"F6.imprint","IMPRINT",FACE,{"disambiguationData":[TD([[makeQuery(id+"F6.imprint","IMPRINT",EDGE,{"derivedFrom":sQuery(id+"F6.wireOp",EDGE,"E498.MirrorC")}),-1.0]])]});
            var Q72;
            Q72=makeQuery(id+"F6.imprint","IMPRINT",FACE,{"disambiguationData":[TD([[makeQuery(id+"F6.imprint","IMPRINT",EDGE,{"derivedFrom":sQuery(id+"F6.wireOp",EDGE,"E898.MirrorC")}),-1.0]])]});
            var Q73;
            Q73=makeQuery(id+"F6.imprint","IMPRINT",FACE,{"disambiguationData":[TD([[makeQuery(id+"F6.imprint","IMPRINT",EDGE,{"derivedFrom":sQuery(id+"F6.wireOp",EDGE,"E845.MirrorC")}),-1.0]])]});
            var Q74;
            Q74=makeQuery(id+"F6.imprint","IMPRINT",FACE,{"disambiguationData":[TD([[makeQuery(id+"F6.imprint","IMPRINT",EDGE,{"derivedFrom":sQuery(id+"F6.wireOp",EDGE,"E691.MirrorC")}),-1.0]])]});
            var Q75;
            Q75=makeQuery(id+"F6.imprint","IMPRINT",FACE,{"disambiguationData":[TD([[makeQuery(id+"F6.imprint","IMPRINT",EDGE,{"derivedFrom":sQuery(id+"F6.wireOp",EDGE,"E427.MirrorC")}),-1.0]])]});
            var Q76;
            Q76=makeQuery(id+"F6.imprint","IMPRINT",FACE,{"disambiguationData":[TD([[makeQuery(id+"F6.imprint","IMPRINT",EDGE,{"derivedFrom":sQuery(id+"F6.wireOp",EDGE,"E575.MirrorC")}),-1.0]])]});
            var Q77;
            Q77=makeQuery(id+"F6.imprint","IMPRINT",FACE,{"disambiguationData":[TD([[makeQuery(id+"F6.imprint","IMPRINT",EDGE,{"derivedFrom":sQuery(id+"F6.wireOp",EDGE,"E522.MirrorC")}),-1.0]])]});
            var Q78;
            Q78=makeQuery(id+"F6.imprint","IMPRINT",FACE,{"disambiguationData":[TD([[makeQuery(id+"F6.imprint","IMPRINT",EDGE,{"derivedFrom":sQuery(id+"F6.wireOp",EDGE,"E504.MirrorC")}),-1.0]])]});
            var Q79;
            Q79=makeQuery(id+"F6.imprint","IMPRINT",FACE,{"disambiguationData":[TD([[makeQuery(id+"F6.imprint","IMPRINT",EDGE,{"derivedFrom":sQuery(id+"F6.wireOp",EDGE,"E538.MirrorC")}),-1.0]])]});
            var Q80;
            Q80=makeQuery(id+"F6.imprint","IMPRINT",FACE,{"disambiguationData":[TD([[makeQuery(id+"F6.imprint","IMPRINT",EDGE,{"derivedFrom":sQuery(id+"F6.wireOp",EDGE,"E591.MirrorC")}),-1.0]])]});
            var Q81;
            Q81=makeQuery(id+"F6.imprint","IMPRINT",FACE,{"disambiguationData":[TD([[makeQuery(id+"F6.imprint","IMPRINT",EDGE,{"derivedFrom":sQuery(id+"F6.wireOp",EDGE,"E519.MirrorC")}),-1.0]])]});
            var Q82;
            Q82=makeQuery(id+"F6.imprint","IMPRINT",FACE,{"disambiguationData":[TD([[makeQuery(id+"F6.imprint","IMPRINT",EDGE,{"derivedFrom":sQuery(id+"F6.wireOp",EDGE,"E744.MirrorC")}),-1.0]])]});
            var Q83;
            Q83=makeQuery(id+"F6.imprint","IMPRINT",FACE,{"disambiguationData":[TD([[makeQuery(id+"F6.imprint","IMPRINT",EDGE,{"derivedFrom":sQuery(id+"F6.wireOp",EDGE,"E492.MirrorC")}),-1.0]])]});
            var Q84;
            Q84=makeQuery(id+"F6.imprint","IMPRINT",FACE,{"disambiguationData":[TD([[makeQuery(id+"F6.imprint","IMPRINT",EDGE,{"derivedFrom":sQuery(id+"F6.wireOp",EDGE,"E544.MirrorC")}),-1.0]])]});
            var Q85;
            Q85=makeQuery(id+"F6.imprint","IMPRINT",FACE,{"disambiguationData":[TD([[makeQuery(id+"F6.imprint","IMPRINT",EDGE,{"derivedFrom":sQuery(id+"F6.wireOp",EDGE,"E473.MirrorC")}),-1.0]])]});
            var Q86;
            Q86=makeQuery(id+"F6.imprint","IMPRINT",FACE,{"disambiguationData":[TD([[makeQuery(id+"F6.imprint","IMPRINT",EDGE,{"derivedFrom":sQuery(id+"F6.wireOp",EDGE,"E891.MirrorC")}),-1.0]])]});
            var Q87;
            Q87=makeQuery(id+"F6.imprint","IMPRINT",FACE,{"disambiguationData":[TD([[makeQuery(id+"F6.imprint","IMPRINT",EDGE,{"derivedFrom":sQuery(id+"F6.wireOp",EDGE,"E506.MirrorC")}),-1.0]])]});
            var Q88;
            Q88=makeQuery(id+"F6.imprint","IMPRINT",FACE,{"disambiguationData":[TD([[makeQuery(id+"F6.imprint","IMPRINT",EDGE,{"derivedFrom":sQuery(id+"F6.wireOp",EDGE,"E559.MirrorC")}),-1.0]])]});
            var Q89;
            Q89=makeQuery(id+"F6.imprint","IMPRINT",FACE,{"disambiguationData":[TD([[makeQuery(id+"F6.imprint","IMPRINT",EDGE,{"derivedFrom":sQuery(id+"F6.wireOp",EDGE,"E489.MirrorC")}),-1.0]])]});
            var Q90;
            Q90=makeQuery(id+"F6.imprint","IMPRINT",FACE,{"disambiguationData":[TD([[makeQuery(id+"F6.imprint","IMPRINT",EDGE,{"derivedFrom":sQuery(id+"F6.wireOp",EDGE,"E581.MirrorC")}),-1.0]])]});
            var Q91;
            Q91=makeQuery(id+"F6.imprint","IMPRINT",FACE,{"disambiguationData":[TD([[makeQuery(id+"F6.imprint","IMPRINT",EDGE,{"derivedFrom":sQuery(id+"F6.wireOp",EDGE,"E790.MirrorC")}),-1.0]])]});
            var Q92;
            Q92=makeQuery(id+"F6.imprint","IMPRINT",FACE,{"disambiguationData":[TD([[makeQuery(id+"F6.imprint","IMPRINT",EDGE,{"derivedFrom":sQuery(id+"F6.wireOp",EDGE,"E737.MirrorC")}),-1.0]])]});
            var Q93;
            Q93=makeQuery(id+"F6.imprint","IMPRINT",FACE,{"disambiguationData":[TD([[makeQuery(id+"F6.imprint","IMPRINT",EDGE,{"derivedFrom":sQuery(id+"F6.wireOp",EDGE,"E635.MirrorC")}),-1.0]])]});
            var Q94;
            Q94=makeQuery(id+"F6.imprint","IMPRINT",FACE,{"disambiguationData":[TD([[makeQuery(id+"F6.imprint","IMPRINT",EDGE,{"derivedFrom":sQuery(id+"F6.wireOp",EDGE,"E584.MirrorC")}),-1.0]])]});
            var Q95;
            Q95=makeQuery(id+"F6.imprint","IMPRINT",FACE,{"disambiguationData":[TD([[makeQuery(id+"F6.imprint","IMPRINT",EDGE,{"derivedFrom":sQuery(id+"F6.wireOp",EDGE,"E596.MirrorC")}),-1.0]])]});
            var Q96;
            Q96=makeQuery(id+"F6.imprint","IMPRINT",FACE,{"disambiguationData":[TD([[makeQuery(id+"F6.imprint","IMPRINT",EDGE,{"derivedFrom":sQuery(id+"F6.wireOp",EDGE,"E753.MirrorC")}),-1.0]])]});
            var Q97;
            Q97=makeQuery(id+"F6.imprint","IMPRINT",FACE,{"disambiguationData":[TD([[makeQuery(id+"F6.imprint","IMPRINT",EDGE,{"derivedFrom":sQuery(id+"F6.wireOp",EDGE,"E805.MirrorC")}),-1.0]])]});
            var Q98;
            Q98=makeQuery(id+"F6.imprint","IMPRINT",FACE,{"disambiguationData":[TD([[makeQuery(id+"F6.imprint","IMPRINT",EDGE,{"derivedFrom":sQuery(id+"F6.wireOp",EDGE,"E599.MirrorC")}),-1.0]])]});
            var Q99;
            Q99=makeQuery(id+"F6.imprint","IMPRINT",FACE,{"disambiguationData":[TD([[makeQuery(id+"F6.imprint","IMPRINT",EDGE,{"derivedFrom":sQuery(id+"F6.wireOp",EDGE,"E650.MirrorC")}),-1.0]])]});
            var Q100;
            Q100=makeQuery(id+"F6.imprint","IMPRINT",FACE,{"disambiguationData":[TD([[makeQuery(id+"F6.imprint","IMPRINT",EDGE,{"derivedFrom":sQuery(id+"F6.wireOp",EDGE,"E553.MirrorC")}),-1.0]])]});
            var Q101;
            Q101=makeQuery(id+"F6.imprint","IMPRINT",FACE,{"disambiguationData":[TD([[makeQuery(id+"F6.imprint","IMPRINT",EDGE,{"derivedFrom":sQuery(id+"F6.wireOp",EDGE,"E759.MirrorC")}),-1.0]])]});
            var Q102;
            Q102=makeQuery(id+"F6.imprint","IMPRINT",FACE,{"disambiguationData":[TD([[makeQuery(id+"F6.imprint","IMPRINT",EDGE,{"derivedFrom":sQuery(id+"F6.wireOp",EDGE,"E535.MirrorC")}),-1.0]])]});
            var Q103;
            Q103=makeQuery(id+"F6.imprint","IMPRINT",FACE,{"disambiguationData":[TD([[makeQuery(id+"F6.imprint","IMPRINT",EDGE,{"derivedFrom":sQuery(id+"F6.wireOp",EDGE,"E605.MirrorC")}),-1.0]])]});
            var Q104;
            Q104=makeQuery(id+"F6.imprint","IMPRINT",FACE,{"disambiguationData":[TD([[makeQuery(id+"F6.imprint","IMPRINT",EDGE,{"derivedFrom":sQuery(id+"F6.wireOp",EDGE,"E565.MirrorC")}),-1.0]])]});
            var Q105;
            Q105=makeQuery(id+"F6.imprint","IMPRINT",FACE,{"disambiguationData":[TD([[makeQuery(id+"F6.imprint","IMPRINT",EDGE,{"derivedFrom":sQuery(id+"F6.wireOp",EDGE,"E775.MirrorC")}),-1.0]])]});
            var Q106;
            Q106=makeQuery(id+"F6.imprint","IMPRINT",FACE,{"disambiguationData":[TD([[makeQuery(id+"F6.imprint","IMPRINT",EDGE,{"derivedFrom":sQuery(id+"F6.wireOp",EDGE,"E550.MirrorC")}),-1.0]])]});
            var Q107;
            Q107=makeQuery(id+"F6.imprint","IMPRINT",FACE,{"disambiguationData":[TD([[makeQuery(id+"F6.imprint","IMPRINT",EDGE,{"derivedFrom":sQuery(id+"F6.wireOp",EDGE,"E568.MirrorC")}),-1.0]])]});
            var Q108;
            Q108=makeQuery(id+"F6.imprint","IMPRINT",FACE,{"disambiguationData":[TD([[makeQuery(id+"F6.imprint","IMPRINT",EDGE,{"derivedFrom":sQuery(id+"F6.wireOp",EDGE,"E620.MirrorC")}),-1.0]])]});
            var Q109;
            Q109=makeQuery(id+"F6.imprint","IMPRINT",FACE,{"disambiguationData":[TD([[makeQuery(id+"F6.imprint","IMPRINT",EDGE,{"derivedFrom":sQuery(id+"F6.wireOp",EDGE,"E641.MirrorC")}),-1.0]])]});
            var Q110;
            Q110=makeQuery(id+"F6.imprint","IMPRINT",FACE,{"disambiguationData":[TD([[makeQuery(id+"F6.imprint","IMPRINT",EDGE,{"derivedFrom":sQuery(id+"F6.wireOp",EDGE,"E850.MirrorC")}),-1.0]])]});
            var Q111;
            Q111=makeQuery(id+"F6.imprint","IMPRINT",FACE,{"disambiguationData":[TD([[makeQuery(id+"F6.imprint","IMPRINT",EDGE,{"derivedFrom":sQuery(id+"F6.wireOp",EDGE,"E798.MirrorC")}),-1.0]])]});
            var Q112;
            Q112=makeQuery(id+"F6.imprint","IMPRINT",FACE,{"disambiguationData":[TD([[makeQuery(id+"F6.imprint","IMPRINT",EDGE,{"derivedFrom":sQuery(id+"F6.wireOp",EDGE,"E696.MirrorC")}),-1.0]])]});
            var Q113;
            Q113=makeQuery(id+"F6.imprint","IMPRINT",FACE,{"disambiguationData":[TD([[makeQuery(id+"F6.imprint","IMPRINT",EDGE,{"derivedFrom":sQuery(id+"F6.wireOp",EDGE,"E644.MirrorC")}),-1.0]])]});
            var Q114;
            Q114=makeQuery(id+"F6.imprint","IMPRINT",FACE,{"disambiguationData":[TD([[makeQuery(id+"F6.imprint","IMPRINT",EDGE,{"derivedFrom":sQuery(id+"F6.wireOp",EDGE,"E880.MirrorC")}),-1.0]])]});
            var Q115;
            Q115=makeQuery(id+"F6.imprint","IMPRINT",FACE,{"disambiguationData":[TD([[makeQuery(id+"F6.imprint","IMPRINT",EDGE,{"derivedFrom":sQuery(id+"F6.wireOp",EDGE,"E656.MirrorC")}),-1.0]])]});
            var Q116;
            Q116=makeQuery(id+"F6.imprint","IMPRINT",FACE,{"disambiguationData":[TD([[makeQuery(id+"F6.imprint","IMPRINT",EDGE,{"derivedFrom":sQuery(id+"F6.wireOp",EDGE,"E813.MirrorC")}),-1.0]])]});
            var Q117;
            Q117=makeQuery(id+"F6.imprint","IMPRINT",FACE,{"disambiguationData":[TD([[makeQuery(id+"F6.imprint","IMPRINT",EDGE,{"derivedFrom":sQuery(id+"F6.wireOp",EDGE,"E865.MirrorC")}),-1.0]])]});
            var Q118;
            Q118=makeQuery(id+"F6.imprint","IMPRINT",FACE,{"disambiguationData":[TD([[makeQuery(id+"F6.imprint","IMPRINT",EDGE,{"derivedFrom":sQuery(id+"F6.wireOp",EDGE,"E659.MirrorC")}),-1.0]])]});
            var Q119;
            Q119=makeQuery(id+"F6.imprint","IMPRINT",FACE,{"disambiguationData":[TD([[makeQuery(id+"F6.imprint","IMPRINT",EDGE,{"derivedFrom":sQuery(id+"F6.wireOp",EDGE,"E711.MirrorC")}),-1.0]])]});
            var Q120;
            Q120=makeQuery(id+"F6.imprint","IMPRINT",FACE,{"disambiguationData":[TD([[makeQuery(id+"F6.imprint","IMPRINT",EDGE,{"derivedFrom":sQuery(id+"F6.wireOp",EDGE,"E611.MirrorC")}),-1.0]])]});
            var Q121;
            Q121=makeQuery(id+"F6.imprint","IMPRINT",FACE,{"disambiguationData":[TD([[makeQuery(id+"F6.imprint","IMPRINT",EDGE,{"derivedFrom":sQuery(id+"F6.wireOp",EDGE,"E768.MirrorC")}),-1.0]])]});
            var Q122;
            Q122=makeQuery(id+"F6.imprint","IMPRINT",FACE,{"disambiguationData":[TD([[makeQuery(id+"F6.imprint","IMPRINT",EDGE,{"derivedFrom":sQuery(id+"F6.wireOp",EDGE,"E820.MirrorC")}),-1.0]])]});
            var Q123;
            Q123=makeQuery(id+"F6.imprint","IMPRINT",FACE,{"disambiguationData":[TD([[makeQuery(id+"F6.imprint","IMPRINT",EDGE,{"derivedFrom":sQuery(id+"F6.wireOp",EDGE,"E613.MirrorC")}),-1.0]])]});
            var Q124;
            Q124=makeQuery(id+"F6.imprint","IMPRINT",FACE,{"disambiguationData":[TD([[makeQuery(id+"F6.imprint","IMPRINT",EDGE,{"derivedFrom":sQuery(id+"F6.wireOp",EDGE,"E665.MirrorC")}),-1.0]])]});
            var Q125;
            Q125=makeQuery(id+"F6.imprint","IMPRINT",FACE,{"disambiguationData":[TD([[makeQuery(id+"F6.imprint","IMPRINT",EDGE,{"derivedFrom":sQuery(id+"F6.wireOp",EDGE,"E783.MirrorC")}),-1.0]])]});
            var Q126;
            Q126=makeQuery(id+"F6.imprint","IMPRINT",FACE,{"disambiguationData":[TD([[makeQuery(id+"F6.imprint","IMPRINT",EDGE,{"derivedFrom":sQuery(id+"F6.wireOp",EDGE,"E834.MirrorC")}),-1.0]])]});
            var Q127;
            Q127=makeQuery(id+"F6.imprint","IMPRINT",FACE,{"disambiguationData":[TD([[makeQuery(id+"F6.imprint","IMPRINT",EDGE,{"derivedFrom":sQuery(id+"F6.wireOp",EDGE,"E628.MirrorC")}),-1.0]])]});
            var Q128;
            Q128=makeQuery(id+"F6.imprint","IMPRINT",FACE,{"disambiguationData":[TD([[makeQuery(id+"F6.imprint","IMPRINT",EDGE,{"derivedFrom":sQuery(id+"F6.wireOp",EDGE,"E681.MirrorC")}),-1.0]])]});
            var Q129;
            Q129=makeQuery(id+"F6.imprint","IMPRINT",FACE,{"disambiguationData":[TD([[makeQuery(id+"F6.imprint","IMPRINT",EDGE,{"derivedFrom":sQuery(id+"F6.wireOp",EDGE,"E702.MirrorC")}),-1.0]])]});
            var Q130;
            Q130=makeQuery(id+"F6.imprint","IMPRINT",FACE,{"disambiguationData":[TD([[makeQuery(id+"F6.imprint","IMPRINT",EDGE,{"derivedFrom":sQuery(id+"F6.wireOp",EDGE,"E874.MirrorC")}),-1.0]])]});
            var Q131;
            Q131=makeQuery(id+"F6.imprint","IMPRINT",FACE,{"disambiguationData":[TD([[makeQuery(id+"F6.imprint","IMPRINT",EDGE,{"derivedFrom":sQuery(id+"F6.wireOp",EDGE,"E705.MirrorC")}),-1.0]])]});
            var Q132;
            Q132=makeQuery(id+"F6.imprint","IMPRINT",FACE,{"disambiguationData":[TD([[makeQuery(id+"F6.imprint","IMPRINT",EDGE,{"derivedFrom":sQuery(id+"F6.wireOp",EDGE,"E717.MirrorC")}),-1.0]])]});
            var Q133;
            Q133=makeQuery(id+"F6.imprint","IMPRINT",FACE,{"disambiguationData":[TD([[makeQuery(id+"F6.imprint","IMPRINT",EDGE,{"derivedFrom":sQuery(id+"F6.wireOp",EDGE,"E889.MirrorC")}),-1.0]])]});
            var Q134;
            Q134=makeQuery(id+"F6.imprint","IMPRINT",FACE,{"disambiguationData":[TD([[makeQuery(id+"F6.imprint","IMPRINT",EDGE,{"derivedFrom":sQuery(id+"F6.wireOp",EDGE,"E720.MirrorC")}),-1.0]])]});
            var Q135;
            Q135=makeQuery(id+"F6.imprint","IMPRINT",FACE,{"disambiguationData":[TD([[makeQuery(id+"F6.imprint","IMPRINT",EDGE,{"derivedFrom":sQuery(id+"F6.wireOp",EDGE,"E843.MirrorC")}),-1.0]])]});
            var Q136;
            Q136=makeQuery(id+"F6.imprint","IMPRINT",FACE,{"disambiguationData":[TD([[makeQuery(id+"F6.imprint","IMPRINT",EDGE,{"derivedFrom":sQuery(id+"F6.wireOp",EDGE,"E896.MirrorC")}),-1.0]])]});
            var Q137;
            Q137=makeQuery(id+"F6.imprint","IMPRINT",FACE,{"disambiguationData":[TD([[makeQuery(id+"F6.imprint","IMPRINT",EDGE,{"derivedFrom":sQuery(id+"F6.wireOp",EDGE,"E671.MirrorC")}),-1.0]])]});
            var Q138;
            Q138=makeQuery(id+"F6.imprint","IMPRINT",FACE,{"disambiguationData":[TD([[makeQuery(id+"F6.imprint","IMPRINT",EDGE,{"derivedFrom":sQuery(id+"F6.wireOp",EDGE,"E727.MirrorC")}),-1.0]])]});
            var Q139;
            Q139=makeQuery(id+"F6.imprint","IMPRINT",FACE,{"disambiguationData":[TD([[makeQuery(id+"F6.imprint","IMPRINT",EDGE,{"derivedFrom":sQuery(id+"F6.wireOp",EDGE,"E828.MirrorC")}),-1.0]])]});
            var Q140;
            Q140=makeQuery(id+"F6.imprint","IMPRINT",FACE,{"disambiguationData":[TD([[makeQuery(id+"F6.imprint","IMPRINT",EDGE,{"derivedFrom":sQuery(id+"F6.wireOp",EDGE,"E674.MirrorC")}),-1.0]])]});
            var Q141;
            Q141=makeQuery(id+"F6.imprint","IMPRINT",FACE,{"disambiguationData":[TD([[makeQuery(id+"F6.imprint","IMPRINT",EDGE,{"derivedFrom":sQuery(id+"F6.wireOp",EDGE,"E687.MirrorC")}),-1.0]])]});
            var Q142;
            Q142=makeQuery(id+"F6.imprint","IMPRINT",FACE,{"disambiguationData":[TD([[makeQuery(id+"F6.imprint","IMPRINT",EDGE,{"derivedFrom":sQuery(id+"F6.wireOp",EDGE,"E858.MirrorC")}),-1.0]])]});
            var Q143;
            Q143=makeQuery(id+"F6.imprint","IMPRINT",FACE,{"disambiguationData":[TD([[makeQuery(id+"F6.imprint","IMPRINT",EDGE,{"derivedFrom":sQuery(id+"F6.wireOp",EDGE,"E689.MirrorC")}),-1.0]])]});
            var Q144;
            Q144=makeQuery(id+"F6.imprint","IMPRINT",FACE,{"disambiguationData":[TD([[makeQuery(id+"F6.imprint","IMPRINT",EDGE,{"derivedFrom":sQuery(id+"F6.wireOp",EDGE,"E757.MirrorC")}),-1.0]])]});
            var Q145;
            Q145=makeQuery(id+"F6.imprint","IMPRINT",FACE,{"disambiguationData":[TD([[makeQuery(id+"F6.imprint","IMPRINT",EDGE,{"derivedFrom":sQuery(id+"F6.wireOp",EDGE,"E742.MirrorC")}),-1.0]])]});
            var Q146;
            Q146=makeQuery(id+"F6.imprint","IMPRINT",FACE,{"disambiguationData":[TD([[makeQuery(id+"F6.imprint","IMPRINT",EDGE,{"derivedFrom":sQuery(id+"F6.wireOp",EDGE,"E732.MirrorC")}),-1.0]])]});
            var Q147;
            Q147=makeQuery(id+"F6.imprint","IMPRINT",FACE,{"disambiguationData":[TD([[makeQuery(id+"F6.imprint","IMPRINT",EDGE,{"derivedFrom":sQuery(id+"F6.wireOp",EDGE,"E380.MirrorC")}),-1.0]])]});
            var Q148;
            Q148=makeQuery(id+"F6.imprint","IMPRINT",FACE,{"disambiguationData":[TD([[makeQuery(id+"F6.imprint","IMPRINT",EDGE,{"derivedFrom":sQuery(id+"F6.wireOp",EDGE,"E343.MirrorC")}),-1.0]])]});
            var Q149;
            Q149=makeQuery(id+"F6.imprint","IMPRINT",FACE,{"disambiguationData":[TD([[makeQuery(id+"F6.imprint","IMPRINT",EDGE,{"derivedFrom":sQuery(id+"F6.wireOp",EDGE,"E396.MirrorC")}),-1.0]])]});
            var Q150;
            Q150=makeQuery(id+"F6.imprint","IMPRINT",FACE,{"disambiguationData":[TD([[makeQuery(id+"F6.imprint","IMPRINT",EDGE,{"derivedFrom":sQuery(id+"F6.wireOp",EDGE,"E350.MirrorC")}),-1.0]])]});
            var Q151;
            Q151=makeQuery(id+"F6.imprint","IMPRINT",FACE,{"disambiguationData":[TD([[makeQuery(id+"F6.imprint","IMPRINT",EDGE,{"derivedFrom":sQuery(id+"F6.wireOp",EDGE,"E364.MirrorC")}),-1.0]])]});
            var Q152;
            Q152=makeQuery(id+"F6.imprint","IMPRINT",FACE,{"disambiguationData":[TD([[makeQuery(id+"F6.imprint","IMPRINT",EDGE,{"derivedFrom":sQuery(id+"F6.wireOp",EDGE,"E441.MirrorC")}),-1.0]])]});
            var Q153;
            Q153=makeQuery(id+"F6.imprint","IMPRINT",FACE,{"disambiguationData":[TD([[makeQuery(id+"F6.imprint","IMPRINT",EDGE,{"derivedFrom":sQuery(id+"F6.wireOp",EDGE,"E389.MirrorC")}),-1.0]])]});
            var Q154;
            Q154=makeQuery(id+"F6.imprint","IMPRINT",FACE,{"disambiguationData":[TD([[makeQuery(id+"F6.imprint","IMPRINT",EDGE,{"derivedFrom":sQuery(id+"F6.wireOp",EDGE,"E456.MirrorC")}),-1.0]])]});
            var Q155;
            Q155=makeQuery(id+"F6.imprint","IMPRINT",FACE,{"disambiguationData":[TD([[makeQuery(id+"F6.imprint","IMPRINT",EDGE,{"derivedFrom":sQuery(id+"F6.wireOp",EDGE,"E404.MirrorC")}),-1.0]])]});
            var Q156;
            Q156=makeQuery(id+"F6.imprint","IMPRINT",FACE,{"disambiguationData":[TD([[makeQuery(id+"F6.imprint","IMPRINT",EDGE,{"derivedFrom":sQuery(id+"F6.wireOp",EDGE,"E358.MirrorC")}),-1.0]])]});
            var Q157;
            Q157=makeQuery(id+"F6.imprint","IMPRINT",FACE,{"disambiguationData":[TD([[makeQuery(id+"F6.imprint","IMPRINT",EDGE,{"derivedFrom":sQuery(id+"F6.wireOp",EDGE,"E410.MirrorC")}),-1.0]])]});
            var Q158;
            Q158=makeQuery(id+"F6.imprint","IMPRINT",FACE,{"disambiguationData":[TD([[makeQuery(id+"F6.imprint","IMPRINT",EDGE,{"derivedFrom":sQuery(id+"F6.wireOp",EDGE,"E373.MirrorC")}),-1.0]])]});
            var Q159;
            Q159=makeQuery(id+"F6.imprint","IMPRINT",FACE,{"disambiguationData":[TD([[makeQuery(id+"F6.imprint","IMPRINT",EDGE,{"derivedFrom":sQuery(id+"F6.wireOp",EDGE,"E425.MirrorC")}),-1.0]])]});
            var Q160;
            Q160=makeQuery(id+"F6.imprint","IMPRINT",FACE,{"disambiguationData":[TD([[makeQuery(id+"F6.imprint","IMPRINT",EDGE,{"derivedFrom":sQuery(id+"F6.wireOp",EDGE,"E502.MirrorC")}),-1.0]])]});
            var Q161;
            Q161=makeQuery(id+"F6.imprint","IMPRINT",FACE,{"disambiguationData":[TD([[makeQuery(id+"F6.imprint","IMPRINT",EDGE,{"derivedFrom":sQuery(id+"F6.wireOp",EDGE,"E449.MirrorC")}),-1.0]])]});
            var Q162;
            Q162=makeQuery(id+"F6.imprint","IMPRINT",FACE,{"disambiguationData":[TD([[makeQuery(id+"F6.imprint","IMPRINT",EDGE,{"derivedFrom":sQuery(id+"F6.wireOp",EDGE,"E517.MirrorC")}),-1.0]])]});
            var Q163;
            Q163=makeQuery(id+"F6.imprint","IMPRINT",FACE,{"disambiguationData":[TD([[makeQuery(id+"F6.imprint","IMPRINT",EDGE,{"derivedFrom":sQuery(id+"F6.wireOp",EDGE,"E465.MirrorC")}),-1.0]])]});
            var Q164;
            Q164=makeQuery(id+"F6.imprint","IMPRINT",FACE,{"disambiguationData":[TD([[makeQuery(id+"F6.imprint","IMPRINT",EDGE,{"derivedFrom":sQuery(id+"F6.wireOp",EDGE,"E471.MirrorC")}),-1.0]])]});
            var Q165;
            Q165=makeQuery(id+"F6.imprint","IMPRINT",FACE,{"disambiguationData":[TD([[makeQuery(id+"F6.imprint","IMPRINT",EDGE,{"derivedFrom":sQuery(id+"F6.wireOp",EDGE,"E487.MirrorC")}),-1.0]])]});
            var Q166;
            Q166=makeQuery(id+"F6.imprint","IMPRINT",FACE,{"disambiguationData":[TD([[makeQuery(id+"F6.imprint","IMPRINT",EDGE,{"derivedFrom":sQuery(id+"F6.wireOp",EDGE,"E434.MirrorC")}),-1.0]])]});
            var Q167;
            Q167=makeQuery(id+"F6.imprint","IMPRINT",FACE,{"disambiguationData":[TD([[makeQuery(id+"F6.imprint","IMPRINT",EDGE,{"derivedFrom":sQuery(id+"F6.wireOp",EDGE,"E563.MirrorC")}),-1.0]])]});
            var Q168;
            Q168=makeQuery(id+"F6.imprint","IMPRINT",FACE,{"disambiguationData":[TD([[makeQuery(id+"F6.imprint","IMPRINT",EDGE,{"derivedFrom":sQuery(id+"F6.wireOp",EDGE,"E510.MirrorC")}),-1.0]])]});
            var Q169;
            Q169=makeQuery(id+"F6.imprint","IMPRINT",FACE,{"disambiguationData":[TD([[makeQuery(id+"F6.imprint","IMPRINT",EDGE,{"derivedFrom":sQuery(id+"F6.wireOp",EDGE,"E526.MirrorC")}),-1.0]])]});
            var Q170;
            Q170=makeQuery(id+"F6.imprint","IMPRINT",FACE,{"disambiguationData":[TD([[makeQuery(id+"F6.imprint","IMPRINT",EDGE,{"derivedFrom":sQuery(id+"F6.wireOp",EDGE,"E579.MirrorC")}),-1.0]])]});
            var Q171;
            Q171=makeQuery(id+"F6.imprint","IMPRINT",FACE,{"disambiguationData":[TD([[makeQuery(id+"F6.imprint","IMPRINT",EDGE,{"derivedFrom":sQuery(id+"F6.wireOp",EDGE,"E480.MirrorC")}),-1.0]])]});
            var Q172;
            Q172=makeQuery(id+"F6.imprint","IMPRINT",FACE,{"disambiguationData":[TD([[makeQuery(id+"F6.imprint","IMPRINT",EDGE,{"derivedFrom":sQuery(id+"F6.wireOp",EDGE,"E533.MirrorC")}),-1.0]])]});
            var Q173;
            Q173=makeQuery(id+"F6.imprint","IMPRINT",FACE,{"disambiguationData":[TD([[makeQuery(id+"F6.imprint","IMPRINT",EDGE,{"derivedFrom":sQuery(id+"F6.wireOp",EDGE,"E496.MirrorC")}),-1.0]])]});
            var Q174;
            Q174=makeQuery(id+"F6.imprint","IMPRINT",FACE,{"disambiguationData":[TD([[makeQuery(id+"F6.imprint","IMPRINT",EDGE,{"derivedFrom":sQuery(id+"F6.wireOp",EDGE,"E548.MirrorC")}),-1.0]])]});
            var Q175;
            Q175=makeQuery(id+"F6.imprint","IMPRINT",FACE,{"disambiguationData":[TD([[makeQuery(id+"F6.imprint","IMPRINT",EDGE,{"derivedFrom":sQuery(id+"F6.wireOp",EDGE,"E639.MirrorC")}),-1.0]])]});
            var Q176;
            Q176=makeQuery(id+"F6.imprint","IMPRINT",FACE,{"disambiguationData":[TD([[makeQuery(id+"F6.imprint","IMPRINT",EDGE,{"derivedFrom":sQuery(id+"F6.wireOp",EDGE,"E588.MirrorC")}),-1.0]])]});
            var Q177;
            Q177=makeQuery(id+"F6.imprint","IMPRINT",FACE,{"disambiguationData":[TD([[makeQuery(id+"F6.imprint","IMPRINT",EDGE,{"derivedFrom":sQuery(id+"F6.wireOp",EDGE,"E378.MirrorC")}),-1.0]])]});
            var Q178;
            Q178=makeQuery(id+"F6.imprint","IMPRINT",FACE,{"disambiguationData":[TD([[makeQuery(id+"F6.imprint","IMPRINT",EDGE,{"derivedFrom":sQuery(id+"F6.wireOp",EDGE,"E602.MirrorC")}),-1.0]])]});
            var Q179;
            Q179=makeQuery(id+"F6.imprint","IMPRINT",FACE,{"disambiguationData":[TD([[makeQuery(id+"F6.imprint","IMPRINT",EDGE,{"derivedFrom":sQuery(id+"F6.wireOp",EDGE,"E654.MirrorC")}),-1.0]])]});
            var Q180;
            Q180=makeQuery(id+"F6.imprint","IMPRINT",FACE,{"disambiguationData":[TD([[makeQuery(id+"F6.imprint","IMPRINT",EDGE,{"derivedFrom":sQuery(id+"F6.wireOp",EDGE,"E394.MirrorC")}),-1.0]])]});
            var Q181;
            Q181=makeQuery(id+"F6.imprint","IMPRINT",FACE,{"disambiguationData":[TD([[makeQuery(id+"F6.imprint","IMPRINT",EDGE,{"derivedFrom":sQuery(id+"F6.wireOp",EDGE,"E341.MirrorC")}),-1.0]])]});
            var Q182;
            Q182=makeQuery(id+"F6.imprint","IMPRINT",FACE,{"disambiguationData":[TD([[makeQuery(id+"F6.imprint","IMPRINT",EDGE,{"derivedFrom":sQuery(id+"F6.wireOp",EDGE,"E609.MirrorC")}),-1.0]])]});
            var Q183;
            Q183=makeQuery(id+"F6.imprint","IMPRINT",FACE,{"disambiguationData":[TD([[makeQuery(id+"F6.imprint","IMPRINT",EDGE,{"derivedFrom":sQuery(id+"F6.wireOp",EDGE,"E594.MirrorC")}),-1.0]])]});
            var Q184;
            Q184=makeQuery(id+"F6.imprint","IMPRINT",FACE,{"disambiguationData":[TD([[makeQuery(id+"F6.imprint","IMPRINT",EDGE,{"derivedFrom":sQuery(id+"F6.wireOp",EDGE,"E348.MirrorC")}),-1.0]])]});
            var Q185;
            Q185=makeQuery(id+"F6.imprint","IMPRINT",FACE,{"disambiguationData":[TD([[makeQuery(id+"F6.imprint","IMPRINT",EDGE,{"derivedFrom":sQuery(id+"F6.wireOp",EDGE,"E624.MirrorC")}),-1.0]])]});
            var Q186;
            Q186=makeQuery(id+"F6.imprint","IMPRINT",FACE,{"disambiguationData":[TD([[makeQuery(id+"F6.imprint","IMPRINT",EDGE,{"derivedFrom":sQuery(id+"F6.wireOp",EDGE,"E572.MirrorC")}),-1.0]])]});
            var Q187;
            Q187=makeQuery(id+"F6.imprint","IMPRINT",FACE,{"disambiguationData":[TD([[makeQuery(id+"F6.imprint","IMPRINT",EDGE,{"derivedFrom":sQuery(id+"F6.wireOp",EDGE,"E362.MirrorC")}),-1.0]])]});
            var Q188;
            Q188=makeQuery(id+"F6.imprint","IMPRINT",FACE,{"disambiguationData":[TD([[makeQuery(id+"F6.imprint","IMPRINT",EDGE,{"derivedFrom":sQuery(id+"F6.wireOp",EDGE,"E557.MirrorC")}),-1.0]])]});
            var Q189;
            Q189=makeQuery(id+"F6.imprint","IMPRINT",FACE,{"disambiguationData":[TD([[makeQuery(id+"F6.imprint","IMPRINT",EDGE,{"derivedFrom":sQuery(id+"F6.wireOp",EDGE,"E647.MirrorC")}),-1.0]])]});
            var Q190;
            Q190=makeQuery(id+"F6.imprint","IMPRINT",FACE,{"disambiguationData":[TD([[makeQuery(id+"F6.imprint","IMPRINT",EDGE,{"derivedFrom":sQuery(id+"F6.wireOp",EDGE,"E700.MirrorC")}),-1.0]])]});
            var Q191;
            Q191=makeQuery(id+"F6.imprint","IMPRINT",FACE,{"disambiguationData":[TD([[makeQuery(id+"F6.imprint","IMPRINT",EDGE,{"derivedFrom":sQuery(id+"F6.wireOp",EDGE,"E387.MirrorC")}),-1.0]])]});
            var Q192;
            Q192=makeQuery(id+"F6.imprint","IMPRINT",FACE,{"disambiguationData":[TD([[makeQuery(id+"F6.imprint","IMPRINT",EDGE,{"derivedFrom":sQuery(id+"F6.wireOp",EDGE,"E439.MirrorC")}),-1.0]])]});
            var Q193;
            Q193=makeQuery(id+"F6.imprint","IMPRINT",FACE,{"disambiguationData":[TD([[makeQuery(id+"F6.imprint","IMPRINT",EDGE,{"derivedFrom":sQuery(id+"F6.wireOp",EDGE,"E715.MirrorC")}),-1.0]])]});
            var Q194;
            Q194=makeQuery(id+"F6.imprint","IMPRINT",FACE,{"disambiguationData":[TD([[makeQuery(id+"F6.imprint","IMPRINT",EDGE,{"derivedFrom":sQuery(id+"F6.wireOp",EDGE,"E454.MirrorC")}),-1.0]])]});
            var Q195;
            Q195=makeQuery(id+"F6.imprint","IMPRINT",FACE,{"disambiguationData":[TD([[makeQuery(id+"F6.imprint","IMPRINT",EDGE,{"derivedFrom":sQuery(id+"F6.wireOp",EDGE,"E402.MirrorC")}),-1.0]])]});
            var Q196;
            Q196=makeQuery(id+"F6.imprint","IMPRINT",FACE,{"disambiguationData":[TD([[makeQuery(id+"F6.imprint","IMPRINT",EDGE,{"derivedFrom":sQuery(id+"F6.wireOp",EDGE,"E617.MirrorC")}),-1.0]])]});
            var Q197;
            Q197=makeQuery(id+"F6.imprint","IMPRINT",FACE,{"disambiguationData":[TD([[makeQuery(id+"F6.imprint","IMPRINT",EDGE,{"derivedFrom":sQuery(id+"F6.wireOp",EDGE,"E669.MirrorC")}),-1.0]])]});
            var Q198;
            Q198=makeQuery(id+"F6.imprint","IMPRINT",FACE,{"disambiguationData":[TD([[makeQuery(id+"F6.imprint","IMPRINT",EDGE,{"derivedFrom":sQuery(id+"F6.wireOp",EDGE,"E356.MirrorC")}),-1.0]])]});
            var Q199;
            Q199=makeQuery(id+"F6.imprint","IMPRINT",FACE,{"disambiguationData":[TD([[makeQuery(id+"F6.imprint","IMPRINT",EDGE,{"derivedFrom":sQuery(id+"F6.wireOp",EDGE,"E408.MirrorC")}),-1.0]])]});
            var Q200;
            Q200=makeQuery(id+"F6.imprint","IMPRINT",FACE,{"disambiguationData":[TD([[makeQuery(id+"F6.imprint","IMPRINT",EDGE,{"derivedFrom":sQuery(id+"F6.wireOp",EDGE,"E685.MirrorC")}),-1.0]])]});
            var Q201;
            Q201=makeQuery(id+"F6.imprint","IMPRINT",FACE,{"disambiguationData":[TD([[makeQuery(id+"F6.imprint","IMPRINT",EDGE,{"derivedFrom":sQuery(id+"F6.wireOp",EDGE,"E632.MirrorC")}),-1.0]])]});
            var Q202;
            Q202=makeQuery(id+"F6.imprint","IMPRINT",FACE,{"disambiguationData":[TD([[makeQuery(id+"F6.imprint","IMPRINT",EDGE,{"derivedFrom":sQuery(id+"F6.wireOp",EDGE,"E371.MirrorC")}),-1.0]])]});
            var Q203;
            Q203=makeQuery(id+"F6.imprint","IMPRINT",FACE,{"disambiguationData":[TD([[makeQuery(id+"F6.imprint","IMPRINT",EDGE,{"derivedFrom":sQuery(id+"F6.wireOp",EDGE,"E423.MirrorC")}),-1.0]])]});
            var Q204;
            Q204=makeQuery(id+"F6.imprint","IMPRINT",FACE,{"disambiguationData":[TD([[makeQuery(id+"F6.imprint","IMPRINT",EDGE,{"derivedFrom":sQuery(id+"F6.wireOp",EDGE,"E515.MirrorC")}),-1.0]])]});
            var Q205;
            Q205=makeQuery(id+"F6.imprint","IMPRINT",FACE,{"disambiguationData":[TD([[makeQuery(id+"F6.imprint","IMPRINT",EDGE,{"derivedFrom":sQuery(id+"F6.wireOp",EDGE,"E463.MirrorC")}),-1.0]])]});
            var Q206;
            Q206=makeQuery(id+"F6.imprint","IMPRINT",FACE,{"disambiguationData":[TD([[makeQuery(id+"F6.imprint","IMPRINT",EDGE,{"derivedFrom":sQuery(id+"F6.wireOp",EDGE,"E724.MirrorC")}),-1.0]])]});
            var Q207;
            Q207=makeQuery(id+"F6.imprint","IMPRINT",FACE,{"disambiguationData":[TD([[makeQuery(id+"F6.imprint","IMPRINT",EDGE,{"derivedFrom":sQuery(id+"F6.wireOp",EDGE,"E478.MirrorC")}),-1.0]])]});
            var Q208;
            Q208=makeQuery(id+"F6.imprint","IMPRINT",FACE,{"disambiguationData":[TD([[makeQuery(id+"F6.imprint","IMPRINT",EDGE,{"derivedFrom":sQuery(id+"F6.wireOp",EDGE,"E531.MirrorC")}),-1.0]])]});
            var Q209;
            Q209=makeQuery(id+"F6.imprint","IMPRINT",FACE,{"disambiguationData":[TD([[makeQuery(id+"F6.imprint","IMPRINT",EDGE,{"derivedFrom":sQuery(id+"F6.wireOp",EDGE,"E731.MirrorC")}),-1.0]])]});
            var Q210;
            Q210=makeQuery(id+"F6.imprint","IMPRINT",FACE,{"disambiguationData":[TD([[makeQuery(id+"F6.imprint","IMPRINT",EDGE,{"derivedFrom":sQuery(id+"F6.wireOp",EDGE,"E485.MirrorC")}),-1.0]])]});
            var Q211;
            Q211=makeQuery(id+"F6.imprint","IMPRINT",FACE,{"disambiguationData":[TD([[makeQuery(id+"F6.imprint","IMPRINT",EDGE,{"derivedFrom":sQuery(id+"F6.wireOp",EDGE,"E678.MirrorC")}),-1.0]])]});
            var Q212;
            Q212=makeQuery(id+"F6.imprint","IMPRINT",FACE,{"disambiguationData":[TD([[makeQuery(id+"F6.imprint","IMPRINT",EDGE,{"derivedFrom":sQuery(id+"F6.wireOp",EDGE,"E417.MirrorC")}),-1.0]])]});
            var Q213;
            Q213=makeQuery(id+"F6.imprint","IMPRINT",FACE,{"disambiguationData":[TD([[makeQuery(id+"F6.imprint","IMPRINT",EDGE,{"derivedFrom":sQuery(id+"F6.wireOp",EDGE,"E469.MirrorC")}),-1.0]])]});
            var Q214;
            Q214=makeQuery(id+"F6.imprint","IMPRINT",FACE,{"disambiguationData":[TD([[makeQuery(id+"F6.imprint","IMPRINT",EDGE,{"derivedFrom":sQuery(id+"F6.wireOp",EDGE,"E693.MirrorC")}),-1.0]])]});
            var Q215;
            Q215=makeQuery(id+"F6.imprint","IMPRINT",FACE,{"disambiguationData":[TD([[makeQuery(id+"F6.imprint","IMPRINT",EDGE,{"derivedFrom":sQuery(id+"F6.wireOp",EDGE,"E448.MirrorC")}),-1.0]])]});
            var Q216;
            Q216=makeQuery(id+"F6.imprint","IMPRINT",FACE,{"disambiguationData":[TD([[makeQuery(id+"F6.imprint","IMPRINT",EDGE,{"derivedFrom":sQuery(id+"F6.wireOp",EDGE,"E500.MirrorC")}),-1.0]])]});
            var Q217;
            Q217=makeQuery(id+"F6.imprint","IMPRINT",FACE,{"disambiguationData":[TD([[makeQuery(id+"F6.imprint","IMPRINT",EDGE,{"derivedFrom":sQuery(id+"F6.wireOp",EDGE,"E432.MirrorC")}),-1.0]])]});
            var Q218;
            Q218=makeQuery(id+"F6.imprint","IMPRINT",FACE,{"disambiguationData":[TD([[makeQuery(id+"F6.imprint","IMPRINT",EDGE,{"derivedFrom":sQuery(id+"F6.wireOp",EDGE,"E577.MirrorC")}),-1.0]])]});
            var Q219;
            Q219=makeQuery(id+"F6.imprint","IMPRINT",FACE,{"disambiguationData":[TD([[makeQuery(id+"F6.imprint","IMPRINT",EDGE,{"derivedFrom":sQuery(id+"F6.wireOp",EDGE,"E524.MirrorC")}),-1.0]])]});
            var Q220;
            Q220=makeQuery(id+"F6.imprint","IMPRINT",FACE,{"disambiguationData":[TD([[makeQuery(id+"F6.imprint","IMPRINT",EDGE,{"derivedFrom":sQuery(id+"F6.wireOp",EDGE,"E746.MirrorC")}),-1.0]])]});
            var Q221;
            Q221=makeQuery(id+"F6.imprint","IMPRINT",FACE,{"disambiguationData":[TD([[makeQuery(id+"F6.imprint","IMPRINT",EDGE,{"derivedFrom":sQuery(id+"F6.wireOp",EDGE,"E540.MirrorC")}),-1.0]])]});
            var Q222;
            Q222=makeQuery(id+"F6.imprint","IMPRINT",FACE,{"disambiguationData":[TD([[makeQuery(id+"F6.imprint","IMPRINT",EDGE,{"derivedFrom":sQuery(id+"F6.wireOp",EDGE,"E592.MirrorC")}),-1.0]])]});
            var Q223;
            Q223=makeQuery(id+"F6.imprint","IMPRINT",FACE,{"disambiguationData":[TD([[makeQuery(id+"F6.imprint","IMPRINT",EDGE,{"derivedFrom":sQuery(id+"F6.wireOp",EDGE,"E494.MirrorC")}),-1.0]])]});
            var Q224;
            Q224=makeQuery(id+"F6.imprint","IMPRINT",FACE,{"disambiguationData":[TD([[makeQuery(id+"F6.imprint","IMPRINT",EDGE,{"derivedFrom":sQuery(id+"F6.wireOp",EDGE,"E546.MirrorC")}),-1.0]])]});
            var Q225;
            Q225=makeQuery(id+"F6.imprint","IMPRINT",FACE,{"disambiguationData":[TD([[makeQuery(id+"F6.imprint","IMPRINT",EDGE,{"derivedFrom":sQuery(id+"F6.wireOp",EDGE,"E508.MirrorC")}),-1.0]])]});
            var Q226;
            Q226=makeQuery(id+"F6.imprint","IMPRINT",FACE,{"disambiguationData":[TD([[makeQuery(id+"F6.imprint","IMPRINT",EDGE,{"derivedFrom":sQuery(id+"F6.wireOp",EDGE,"E561.MirrorC")}),-1.0]])]});
            var Q227;
            Q227=makeQuery(id+"F6.imprint","IMPRINT",FACE,{"disambiguationData":[TD([[makeQuery(id+"F6.imprint","IMPRINT",EDGE,{"derivedFrom":sQuery(id+"F6.wireOp",EDGE,"E612.MirrorC")}),-1.0]])]});
            var Q228;
            Q228=makeQuery(id+"F6.imprint","IMPRINT",FACE,{"disambiguationData":[TD([[makeQuery(id+"F6.imprint","IMPRINT",EDGE,{"derivedFrom":sQuery(id+"F6.wireOp",EDGE,"E627.MirrorC")}),-1.0]])]});
            var Q229;
            Q229=makeQuery(id+"F6.imprint","IMPRINT",FACE,{"disambiguationData":[TD([[makeQuery(id+"F6.imprint","IMPRINT",EDGE,{"derivedFrom":sQuery(id+"F6.wireOp",EDGE,"E583.MirrorC")}),-1.0]])]});
            var Q230;
            Q230=makeQuery(id+"F6.imprint","IMPRINT",FACE,{"disambiguationData":[TD([[makeQuery(id+"F6.imprint","IMPRINT",EDGE,{"derivedFrom":sQuery(id+"F6.wireOp",EDGE,"E598.MirrorC")}),-1.0]])]});
            var Q231;
            Q231=makeQuery(id+"F6.imprint","IMPRINT",FACE,{"disambiguationData":[TD([[makeQuery(id+"F6.imprint","IMPRINT",EDGE,{"derivedFrom":sQuery(id+"F6.wireOp",EDGE,"E673.MirrorC")}),-1.0]])]});
            var Q232;
            Q232=makeQuery(id+"F6.imprint","IMPRINT",FACE,{"disambiguationData":[TD([[makeQuery(id+"F6.imprint","IMPRINT",EDGE,{"derivedFrom":sQuery(id+"F6.wireOp",EDGE,"E643.MirrorC")}),-1.0]])]});
            var Q233;
            Q233=makeQuery(id+"F6.imprint","IMPRINT",FACE,{"disambiguationData":[TD([[makeQuery(id+"F6.imprint","IMPRINT",EDGE,{"derivedFrom":sQuery(id+"F6.wireOp",EDGE,"E658.MirrorC")}),-1.0]])]});
            var Q234;
            Q234=makeQuery(id+"F6.imprint","IMPRINT",FACE,{"disambiguationData":[TD([[makeQuery(id+"F6.imprint","IMPRINT",EDGE,{"derivedFrom":sQuery(id+"F6.wireOp",EDGE,"E734.MirrorC")}),-1.0]])]});
            var Q235;
            Q235=makeQuery(id+"F6.imprint","IMPRINT",FACE,{"disambiguationData":[TD([[makeQuery(id+"F6.imprint","IMPRINT",EDGE,{"derivedFrom":sQuery(id+"F6.wireOp",EDGE,"E704.MirrorC")}),-1.0]])]});
            var Q236;
            Q236=makeQuery(id+"F6.imprint","IMPRINT",FACE,{"disambiguationData":[TD([[makeQuery(id+"F6.imprint","IMPRINT",EDGE,{"derivedFrom":sQuery(id+"F6.wireOp",EDGE,"E719.MirrorC")}),-1.0]])]});
            var Q237;
            Q237=makeQuery(id+"F6.imprint","IMPRINT",FACE,{"disambiguationData":[TD([[makeQuery(id+"F6.imprint","IMPRINT",EDGE,{"derivedFrom":sQuery(id+"F6.wireOp",EDGE,"E765.MirrorC")}),-1.0]])]});
            var Q238;
            Q238=makeQuery(id+"F6.imprint","IMPRINT",FACE,{"disambiguationData":[TD([[makeQuery(id+"F6.imprint","IMPRINT",EDGE,{"derivedFrom":sQuery(id+"F6.wireOp",EDGE,"E780.MirrorC")}),-1.0]])]});
            var Q239;
            Q239=makeQuery(id+"F6.imprint","IMPRINT",FACE,{"disambiguationData":[TD([[makeQuery(id+"F6.imprint","IMPRINT",EDGE,{"derivedFrom":sQuery(id+"F6.wireOp",EDGE,"E750.MirrorC")}),-1.0]])]});
            var Q240;
            Q240=makeQuery(id+"F6.imprint","IMPRINT",FACE,{"disambiguationData":[TD([[makeQuery(id+"F6.imprint","IMPRINT",EDGE,{"derivedFrom":sQuery(id+"F6.wireOp",EDGE,"E825.MirrorC")}),-1.0]])]});
            var Q241;
            Q241=makeQuery(id+"F6.imprint","IMPRINT",FACE,{"disambiguationData":[TD([[makeQuery(id+"F6.imprint","IMPRINT",EDGE,{"derivedFrom":sQuery(id+"F6.wireOp",EDGE,"E855.MirrorC")}),-1.0]])]});
            var Q242;
            Q242=makeQuery(id+"F6.imprint","IMPRINT",FACE,{"disambiguationData":[TD([[makeQuery(id+"F6.imprint","IMPRINT",EDGE,{"derivedFrom":sQuery(id+"F6.wireOp",EDGE,"E840.MirrorC")}),-1.0]])]});
            var Q243;
            Q243=makeQuery(id+"F6.imprint","IMPRINT",FACE,{"disambiguationData":[TD([[makeQuery(id+"F6.imprint","IMPRINT",EDGE,{"derivedFrom":sQuery(id+"F6.wireOp",EDGE,"E795.MirrorC")}),-1.0]])]});
            var Q244;
            Q244=makeQuery(id+"F6.imprint","IMPRINT",FACE,{"disambiguationData":[TD([[makeQuery(id+"F6.imprint","IMPRINT",EDGE,{"derivedFrom":sQuery(id+"F6.wireOp",EDGE,"E381.MirrorC")}),-1.0]])]});
            var Q245;
            Q245=makeQuery(id+"F6.imprint","IMPRINT",FACE,{"disambiguationData":[TD([[makeQuery(id+"F6.imprint","IMPRINT",EDGE,{"derivedFrom":sQuery(id+"F6.wireOp",EDGE,"E902.MirrorC")}),-1.0]])]});
            var Q246;
            Q246=makeQuery(id+"F6.imprint","IMPRINT",FACE,{"disambiguationData":[TD([[makeQuery(id+"F6.imprint","IMPRINT",EDGE,{"derivedFrom":sQuery(id+"F6.wireOp",EDGE,"E344.MirrorC")}),-1.0]])]});
            var Q247;
            Q247=makeQuery(id+"F6.imprint","IMPRINT",FACE,{"disambiguationData":[TD([[makeQuery(id+"F6.imprint","IMPRINT",EDGE,{"derivedFrom":sQuery(id+"F6.wireOp",EDGE,"E397.MirrorC")}),-1.0]])]});
            var Q248;
            Q248=makeQuery(id+"F6.imprint","IMPRINT",FACE,{"disambiguationData":[TD([[makeQuery(id+"F6.imprint","IMPRINT",EDGE,{"derivedFrom":sQuery(id+"F6.wireOp",EDGE,"E351.MirrorC")}),-1.0]])]});
            var Q249;
            Q249=makeQuery(id+"F6.imprint","IMPRINT",FACE,{"disambiguationData":[TD([[makeQuery(id+"F6.imprint","IMPRINT",EDGE,{"derivedFrom":sQuery(id+"F6.wireOp",EDGE,"E871.MirrorC")}),-1.0]])]});
            var Q250;
            Q250=makeQuery(id+"F6.imprint","IMPRINT",FACE,{"disambiguationData":[TD([[makeQuery(id+"F6.imprint","IMPRINT",EDGE,{"derivedFrom":sQuery(id+"F6.wireOp",EDGE,"E365.MirrorC")}),-1.0]])]});
            var Q251;
            Q251=makeQuery(id+"F6.imprint","IMPRINT",FACE,{"disambiguationData":[TD([[makeQuery(id+"F6.imprint","IMPRINT",EDGE,{"derivedFrom":sQuery(id+"F6.wireOp",EDGE,"E886.MirrorC")}),-1.0]])]});
            var Q252;
            Q252=makeQuery(id+"F6.imprint","IMPRINT",FACE,{"disambiguationData":[TD([[makeQuery(id+"F6.imprint","IMPRINT",EDGE,{"derivedFrom":sQuery(id+"F6.wireOp",EDGE,"E442.MirrorC")}),-1.0]])]});
            var Q253;
            Q253=makeQuery(id+"F6.imprint","IMPRINT",FACE,{"disambiguationData":[TD([[makeQuery(id+"F6.imprint","IMPRINT",EDGE,{"derivedFrom":sQuery(id+"F6.wireOp",EDGE,"E390.MirrorC")}),-1.0]])]});
            var Q254;
            Q254=makeQuery(id+"F6.imprint","IMPRINT",FACE,{"disambiguationData":[TD([[makeQuery(id+"F6.imprint","IMPRINT",EDGE,{"derivedFrom":sQuery(id+"F6.wireOp",EDGE,"E457.MirrorC")}),-1.0]])]});
            var Q255;
            Q255=makeQuery(id+"F6.imprint","IMPRINT",FACE,{"disambiguationData":[TD([[makeQuery(id+"F6.imprint","IMPRINT",EDGE,{"derivedFrom":sQuery(id+"F6.wireOp",EDGE,"E405.MirrorC")}),-1.0]])]});
            var Q256;
            Q256=makeQuery(id+"F6.imprint","IMPRINT",FACE,{"disambiguationData":[TD([[makeQuery(id+"F6.imprint","IMPRINT",EDGE,{"derivedFrom":sQuery(id+"F6.wireOp",EDGE,"E359.MirrorC")}),-1.0]])]});
            var Q257;
            Q257=makeQuery(id+"F6.imprint","IMPRINT",FACE,{"disambiguationData":[TD([[makeQuery(id+"F6.imprint","IMPRINT",EDGE,{"derivedFrom":sQuery(id+"F6.wireOp",EDGE,"E411.MirrorC")}),-1.0]])]});
            var Q258;
            Q258=makeQuery(id+"F6.imprint","IMPRINT",FACE,{"disambiguationData":[TD([[makeQuery(id+"F6.imprint","IMPRINT",EDGE,{"derivedFrom":sQuery(id+"F6.wireOp",EDGE,"E374.MirrorC")}),-1.0]])]});
            var Q259;
            Q259=makeQuery(id+"F6.imprint","IMPRINT",FACE,{"disambiguationData":[TD([[makeQuery(id+"F6.imprint","IMPRINT",EDGE,{"derivedFrom":sQuery(id+"F6.wireOp",EDGE,"E426.MirrorC")}),-1.0]])]});
            var Q260;
            Q260=makeQuery(id+"F6.imprint","IMPRINT",FACE,{"disambiguationData":[TD([[makeQuery(id+"F6.imprint","IMPRINT",EDGE,{"derivedFrom":sQuery(id+"F6.wireOp",EDGE,"E751.MirrorC")}),-1.0]])]});
            var Q261;
            Q261=makeQuery(id+"F6.imprint","IMPRINT",FACE,{"disambiguationData":[TD([[makeQuery(id+"F6.imprint","IMPRINT",EDGE,{"derivedFrom":sQuery(id+"F6.wireOp",EDGE,"E803.MirrorC")}),-1.0]])]});
            var Q262;
            Q262=makeQuery(id+"F6.imprint","IMPRINT",FACE,{"disambiguationData":[TD([[makeQuery(id+"F6.imprint","IMPRINT",EDGE,{"derivedFrom":sQuery(id+"F6.wireOp",EDGE,"E766.MirrorC")}),-1.0]])]});
            var Q263;
            Q263=makeQuery(id+"F6.imprint","IMPRINT",FACE,{"disambiguationData":[TD([[makeQuery(id+"F6.imprint","IMPRINT",EDGE,{"derivedFrom":sQuery(id+"F6.wireOp",EDGE,"E818.MirrorC")}),-1.0]])]});
            var Q264;
            Q264=makeQuery(id+"F6.imprint","IMPRINT",FACE,{"disambiguationData":[TD([[makeQuery(id+"F6.imprint","IMPRINT",EDGE,{"derivedFrom":sQuery(id+"F6.wireOp",EDGE,"E748.MirrorC")}),-1.0]])]});
            var Q265;
            Q265=makeQuery(id+"F6.imprint","IMPRINT",FACE,{"disambiguationData":[TD([[makeQuery(id+"F6.imprint","IMPRINT",EDGE,{"derivedFrom":sQuery(id+"F6.wireOp",EDGE,"E773.MirrorC")}),-1.0]])]});
            var Q266;
            Q266=makeQuery(id+"F6.imprint","IMPRINT",FACE,{"disambiguationData":[TD([[makeQuery(id+"F6.imprint","IMPRINT",EDGE,{"derivedFrom":sQuery(id+"F6.wireOp",EDGE,"E788.MirrorC")}),-1.0]])]});
            var Q267;
            Q267=makeQuery(id+"F6.imprint","IMPRINT",FACE,{"disambiguationData":[TD([[makeQuery(id+"F6.imprint","IMPRINT",EDGE,{"derivedFrom":sQuery(id+"F6.wireOp",EDGE,"E735.MirrorC")}),-1.0]])]});
            var Q268;
            Q268=makeQuery(id+"F6.imprint","IMPRINT",FACE,{"disambiguationData":[TD([[makeQuery(id+"F6.imprint","IMPRINT",EDGE,{"derivedFrom":sQuery(id+"F6.wireOp",EDGE,"E811.MirrorC")}),-1.0]])]});
            var Q269;
            Q269=makeQuery(id+"F6.imprint","IMPRINT",FACE,{"disambiguationData":[TD([[makeQuery(id+"F6.imprint","IMPRINT",EDGE,{"derivedFrom":sQuery(id+"F6.wireOp",EDGE,"E863.MirrorC")}),-1.0]])]});
            var Q270;
            Q270=makeQuery(id+"F6.imprint","IMPRINT",FACE,{"disambiguationData":[TD([[makeQuery(id+"F6.imprint","IMPRINT",EDGE,{"derivedFrom":sQuery(id+"F6.wireOp",EDGE,"E793.MirrorC")}),-1.0]])]});
            var Q271;
            Q271=makeQuery(id+"F6.imprint","IMPRINT",FACE,{"disambiguationData":[TD([[makeQuery(id+"F6.imprint","IMPRINT",EDGE,{"derivedFrom":sQuery(id+"F6.wireOp",EDGE,"E878.MirrorC")}),-1.0]])]});
            var Q272;
            Q272=makeQuery(id+"F6.imprint","IMPRINT",FACE,{"disambiguationData":[TD([[makeQuery(id+"F6.imprint","IMPRINT",EDGE,{"derivedFrom":sQuery(id+"F6.wireOp",EDGE,"E826.MirrorC")}),-1.0]])]});
            var Q273;
            Q273=makeQuery(id+"F6.imprint","IMPRINT",FACE,{"disambiguationData":[TD([[makeQuery(id+"F6.imprint","IMPRINT",EDGE,{"derivedFrom":sQuery(id+"F6.wireOp",EDGE,"E809.MirrorC")}),-1.0]])]});
            var Q274;
            Q274=makeQuery(id+"F6.imprint","IMPRINT",FACE,{"disambiguationData":[TD([[makeQuery(id+"F6.imprint","IMPRINT",EDGE,{"derivedFrom":sQuery(id+"F6.wireOp",EDGE,"E781.MirrorC")}),-1.0]])]});
            var Q275;
            Q275=makeQuery(id+"F6.imprint","IMPRINT",FACE,{"disambiguationData":[TD([[makeQuery(id+"F6.imprint","IMPRINT",EDGE,{"derivedFrom":sQuery(id+"F6.wireOp",EDGE,"E832.MirrorC")}),-1.0]])]});
            var Q276;
            Q276=makeQuery(id+"F6.imprint","IMPRINT",FACE,{"disambiguationData":[TD([[makeQuery(id+"F6.imprint","IMPRINT",EDGE,{"derivedFrom":sQuery(id+"F6.wireOp",EDGE,"E763.MirrorC")}),-1.0]])]});
            var Q277;
            Q277=makeQuery(id+"F6.imprint","IMPRINT",FACE,{"disambiguationData":[TD([[makeQuery(id+"F6.imprint","IMPRINT",EDGE,{"derivedFrom":sQuery(id+"F6.wireOp",EDGE,"E848.MirrorC")}),-1.0]])]});
            var Q278;
            Q278=makeQuery(id+"F6.imprint","IMPRINT",FACE,{"disambiguationData":[TD([[makeQuery(id+"F6.imprint","IMPRINT",EDGE,{"derivedFrom":sQuery(id+"F6.wireOp",EDGE,"E796.MirrorC")}),-1.0]])]});
            var Q279;
            Q279=makeQuery(id+"F6.imprint","IMPRINT",FACE,{"disambiguationData":[TD([[makeQuery(id+"F6.imprint","IMPRINT",EDGE,{"derivedFrom":sQuery(id+"F6.wireOp",EDGE,"E778.MirrorC")}),-1.0]])]});
            var Q280;
            Q280=makeQuery(id+"F6.imprint","IMPRINT",FACE,{"disambiguationData":[TD([[makeQuery(id+"F6.imprint","IMPRINT",EDGE,{"derivedFrom":sQuery(id+"F6.wireOp",EDGE,"E872.MirrorC")}),-1.0]])]});
            var Q281;
            Q281=makeQuery(id+"F6.imprint","IMPRINT",FACE,{"disambiguationData":[TD([[makeQuery(id+"F6.imprint","IMPRINT",EDGE,{"derivedFrom":sQuery(id+"F6.wireOp",EDGE,"E853.MirrorC")}),-1.0]])]});
            var Q282;
            Q282=makeQuery(id+"F6.imprint","IMPRINT",FACE,{"disambiguationData":[TD([[makeQuery(id+"F6.imprint","IMPRINT",EDGE,{"derivedFrom":sQuery(id+"F6.wireOp",EDGE,"E887.MirrorC")}),-1.0]])]});
            var Q283;
            Q283=makeQuery(id+"F6.imprint","IMPRINT",FACE,{"disambiguationData":[TD([[makeQuery(id+"F6.imprint","IMPRINT",EDGE,{"derivedFrom":sQuery(id+"F6.wireOp",EDGE,"E869.MirrorC")}),-1.0]])]});
            var Q284;
            Q284=makeQuery(id+"F6.imprint","IMPRINT",FACE,{"disambiguationData":[TD([[makeQuery(id+"F6.imprint","IMPRINT",EDGE,{"derivedFrom":sQuery(id+"F6.wireOp",EDGE,"E841.MirrorC")}),-1.0]])]});
            var Q285;
            Q285=makeQuery(id+"F6.imprint","IMPRINT",FACE,{"disambiguationData":[TD([[makeQuery(id+"F6.imprint","IMPRINT",EDGE,{"derivedFrom":sQuery(id+"F6.wireOp",EDGE,"E894.MirrorC")}),-1.0]])]});
            var Q286;
            Q286=makeQuery(id+"F6.imprint","IMPRINT",FACE,{"disambiguationData":[TD([[makeQuery(id+"F6.imprint","IMPRINT",EDGE,{"derivedFrom":sQuery(id+"F6.wireOp",EDGE,"E823.MirrorC")}),-1.0]])]});
            var Q287;
            Q287=makeQuery(id+"F6.imprint","IMPRINT",FACE,{"disambiguationData":[TD([[makeQuery(id+"F6.imprint","IMPRINT",EDGE,{"derivedFrom":sQuery(id+"F6.wireOp",EDGE,"E856.MirrorC")}),-1.0]])]});
            var Q288;
            Q288=makeQuery(id+"F6.imprint","IMPRINT",FACE,{"disambiguationData":[TD([[makeQuery(id+"F6.imprint","IMPRINT",EDGE,{"derivedFrom":sQuery(id+"F6.wireOp",EDGE,"E838.MirrorC")}),-1.0]])]});
            var Q289;
            Q289=makeQuery(id+"F6.imprint","IMPRINT",FACE,{"disambiguationData":[TD([[makeQuery(id+"F6.imprint","IMPRINT",EDGE,{"derivedFrom":sQuery(id+"F6.wireOp",EDGE,"E903.MirrorC")}),-1.0]])]});
            var Q290;
            Q290=makeQuery(id+"F6.imprint","IMPRINT",FACE,{"disambiguationData":[TD([[makeQuery(id+"F6.imprint","IMPRINT",EDGE,{"derivedFrom":sQuery(id+"F6.wireOp",EDGE,"E884.MirrorC")}),-1.0]])]});
            var Q291;
            Q291=makeQuery(id+"F6.imprint","IMPRINT",FACE,{"disambiguationData":[TD([[makeQuery(id+"F6.imprint","IMPRINT",EDGE,{"derivedFrom":sQuery(id+"F6.wireOp",EDGE,"E900.MirrorC")}),-1.0]])]});
            var Q292;
            Q292=makeQuery(id+"F6.imprint","IMPRINT",FACE,{"disambiguationData":[TD([[makeQuery(id+"F6.imprint","IMPRINT",EDGE,{"derivedFrom":sQuery(id+"F6.wireOp",EDGE,"E353.MirrorC")}),-1.0]])]});
            var Q293;
            Q293=makeQuery(id+"F6.imprint","IMPRINT",FACE,{"disambiguationData":[TD([[makeQuery(id+"F6.imprint","IMPRINT",EDGE,{"derivedFrom":sQuery(id+"F6.wireOp",EDGE,"E368.MirrorC")}),-1.0]])]});
            var Q294;
            Q294=makeQuery(id+"F6.imprint","IMPRINT",FACE,{"disambiguationData":[TD([[makeQuery(id+"F6.imprint","IMPRINT",EDGE,{"derivedFrom":sQuery(id+"F6.wireOp",EDGE,"E414.MirrorC")}),-1.0]])]});
            var Q295;
            Q295=makeQuery(id+"F6.imprint","IMPRINT",FACE,{"disambiguationData":[TD([[makeQuery(id+"F6.imprint","IMPRINT",EDGE,{"derivedFrom":sQuery(id+"F6.wireOp",EDGE,"E429.MirrorC")}),-1.0]])]});
            var Q296;
            Q296=makeQuery(id+"F6.imprint","IMPRINT",FACE,{"disambiguationData":[TD([[makeQuery(id+"F6.imprint","IMPRINT",EDGE,{"derivedFrom":sQuery(id+"F6.wireOp",EDGE,"E384.MirrorC")}),-1.0]])]});
            var Q297;
            Q297=makeQuery(id+"F6.imprint","IMPRINT",FACE,{"disambiguationData":[TD([[makeQuery(id+"F6.imprint","IMPRINT",EDGE,{"derivedFrom":sQuery(id+"F6.wireOp",EDGE,"E399.MirrorC")}),-1.0]])]});
            var Q298;
            Q298=makeQuery(id+"F6.imprint","IMPRINT",FACE,{"disambiguationData":[TD([[makeQuery(id+"F6.imprint","IMPRINT",EDGE,{"derivedFrom":sQuery(id+"F6.wireOp",EDGE,"E491.MirrorC")}),-1.0]])]});
            var Q299;
            Q299=makeQuery(id+"F6.imprint","IMPRINT",FACE,{"disambiguationData":[TD([[makeQuery(id+"F6.imprint","IMPRINT",EDGE,{"derivedFrom":sQuery(id+"F6.wireOp",EDGE,"E505.MirrorC")}),-1.0]])]});
            var Q300;
            Q300=makeQuery(id+"F6.imprint","IMPRINT",FACE,{"disambiguationData":[TD([[makeQuery(id+"F6.imprint","IMPRINT",EDGE,{"derivedFrom":sQuery(id+"F6.wireOp",EDGE,"E460.MirrorC")}),-1.0]])]});
            var Q301;
            Q301=makeQuery(id+"F6.imprint","IMPRINT",FACE,{"disambiguationData":[TD([[makeQuery(id+"F6.imprint","IMPRINT",EDGE,{"derivedFrom":sQuery(id+"F6.wireOp",EDGE,"E445.MirrorC")}),-1.0]])]});
            var Q302;
            Q302=makeQuery(id+"F6.imprint","IMPRINT",FACE,{"disambiguationData":[TD([[makeQuery(id+"F6.imprint","IMPRINT",EDGE,{"derivedFrom":sQuery(id+"F6.wireOp",EDGE,"E475.MirrorC")}),-1.0]])]});
            var Q303;
            Q303=makeQuery(id+"F6.imprint","IMPRINT",FACE,{"disambiguationData":[TD([[makeQuery(id+"F6.imprint","IMPRINT",EDGE,{"derivedFrom":sQuery(id+"F6.wireOp",EDGE,"E552.MirrorC")}),-1.0]])]});
            var Q304;
            Q304=makeQuery(id+"F6.imprint","IMPRINT",FACE,{"disambiguationData":[TD([[makeQuery(id+"F6.imprint","IMPRINT",EDGE,{"derivedFrom":sQuery(id+"F6.wireOp",EDGE,"E567.MirrorC")}),-1.0]])]});
            var Q305;
            Q305=makeQuery(id+"F6.imprint","IMPRINT",FACE,{"disambiguationData":[TD([[makeQuery(id+"F6.imprint","IMPRINT",EDGE,{"derivedFrom":sQuery(id+"F6.wireOp",EDGE,"E521.MirrorC")}),-1.0]])]});
            var Q306;
            Q306=makeQuery(id+"F6.imprint","IMPRINT",FACE,{"disambiguationData":[TD([[makeQuery(id+"F6.imprint","IMPRINT",EDGE,{"derivedFrom":sQuery(id+"F6.wireOp",EDGE,"E537.MirrorC")}),-1.0]])]});
            var Q307;
            Q307=makeQuery(id+"F6.imprint","IMPRINT",FACE,{"disambiguationData":[TD([[makeQuery(id+"F6.imprint","IMPRINT",EDGE,{"derivedFrom":sQuery(id+"F6.wireOp",EDGE,"E708.MirrorC")}),-1.0]])]});
            var Q308;
            Q308=makeQuery(id+"F6.imprint","IMPRINT",FACE,{"disambiguationData":[TD([[makeQuery(id+"F6.imprint","IMPRINT",EDGE,{"derivedFrom":sQuery(id+"F6.wireOp",EDGE,"E514.MirrorC")}),-1.0]])]});
            var Q309;
            Q309=makeQuery(id+"F6.imprint","IMPRINT",FACE,{"disambiguationData":[TD([[makeQuery(id+"F6.imprint","IMPRINT",EDGE,{"derivedFrom":sQuery(id+"F6.wireOp",EDGE,"E462.MirrorC")}),-1.0]])]});
            var Q310;
            Q310=makeQuery(id+"F6.imprint","IMPRINT",FACE,{"disambiguationData":[TD([[makeQuery(id+"F6.imprint","IMPRINT",EDGE,{"derivedFrom":sQuery(id+"F6.wireOp",EDGE,"E444.MirrorC")}),-1.0]])]});
            var Q311;
            Q311=makeQuery(id+"F6.imprint","IMPRINT",FACE,{"disambiguationData":[TD([[makeQuery(id+"F6.imprint","IMPRINT",EDGE,{"derivedFrom":sQuery(id+"F6.wireOp",EDGE,"E861.MirrorC")}),-1.0]])]});
            var Q312;
            Q312=makeQuery(id+"F6.imprint","IMPRINT",FACE,{"disambiguationData":[TD([[makeQuery(id+"F6.imprint","IMPRINT",EDGE,{"derivedFrom":sQuery(id+"F6.wireOp",EDGE,"E723.MirrorC")}),-1.0]])]});
            var Q313;
            Q313=makeQuery(id+"F6.imprint","IMPRINT",FACE,{"disambiguationData":[TD([[makeQuery(id+"F6.imprint","IMPRINT",EDGE,{"derivedFrom":sQuery(id+"F6.wireOp",EDGE,"E477.MirrorC")}),-1.0]])]});
            var Q314;
            Q314=makeQuery(id+"F6.imprint","IMPRINT",FACE,{"disambiguationData":[TD([[makeQuery(id+"F6.imprint","IMPRINT",EDGE,{"derivedFrom":sQuery(id+"F6.wireOp",EDGE,"E530.MirrorC")}),-1.0]])]});
            var Q315;
            Q315=makeQuery(id+"F6.imprint","IMPRINT",FACE,{"disambiguationData":[TD([[makeQuery(id+"F6.imprint","IMPRINT",EDGE,{"derivedFrom":sQuery(id+"F6.wireOp",EDGE,"E876.MirrorC")}),-1.0]])]});
            var Q316;
            Q316=makeQuery(id+"F6.imprint","IMPRINT",FACE,{"disambiguationData":[TD([[makeQuery(id+"F6.imprint","IMPRINT",EDGE,{"derivedFrom":sQuery(id+"F6.wireOp",EDGE,"E459.MirrorC")}),-1.0]])]});
            var Q317;
            Q317=makeQuery(id+"F6.imprint","IMPRINT",FACE,{"disambiguationData":[TD([[makeQuery(id+"F6.imprint","IMPRINT",EDGE,{"derivedFrom":sQuery(id+"F6.wireOp",EDGE,"E677.MirrorC")}),-1.0]])]});
            var Q318;
            Q318=makeQuery(id+"F6.imprint","IMPRINT",FACE,{"disambiguationData":[TD([[makeQuery(id+"F6.imprint","IMPRINT",EDGE,{"derivedFrom":sQuery(id+"F6.wireOp",EDGE,"E730.MirrorC")}),-1.0]])]});
            var Q319;
            Q319=makeQuery(id+"F6.imprint","IMPRINT",FACE,{"disambiguationData":[TD([[makeQuery(id+"F6.imprint","IMPRINT",EDGE,{"derivedFrom":sQuery(id+"F6.wireOp",EDGE,"E431.MirrorC")}),-1.0]])]});
            var Q320;
            Q320=makeQuery(id+"F6.imprint","IMPRINT",FACE,{"disambiguationData":[TD([[makeQuery(id+"F6.imprint","IMPRINT",EDGE,{"derivedFrom":sQuery(id+"F6.wireOp",EDGE,"E484.MirrorC")}),-1.0]])]});
            var Q321;
            Q321=makeQuery(id+"F6.imprint","IMPRINT",FACE,{"disambiguationData":[TD([[makeQuery(id+"F6.imprint","IMPRINT",EDGE,{"derivedFrom":sQuery(id+"F6.wireOp",EDGE,"E413.MirrorC")}),-1.0]])]});
            var Q322;
            Q322=makeQuery(id+"F6.imprint","IMPRINT",FACE,{"disambiguationData":[TD([[makeQuery(id+"F6.imprint","IMPRINT",EDGE,{"derivedFrom":sQuery(id+"F6.wireOp",EDGE,"E883.MirrorC")}),-1.0]])]});
            var Q323;
            Q323=makeQuery(id+"F6.imprint","IMPRINT",FACE,{"disambiguationData":[TD([[makeQuery(id+"F6.imprint","IMPRINT",EDGE,{"derivedFrom":sQuery(id+"F6.wireOp",EDGE,"E692.MirrorC")}),-1.0]])]});
            var Q324;
            Q324=makeQuery(id+"F6.imprint","IMPRINT",FACE,{"disambiguationData":[TD([[makeQuery(id+"F6.imprint","IMPRINT",EDGE,{"derivedFrom":sQuery(id+"F6.wireOp",EDGE,"E447.MirrorC")}),-1.0]])]});
            var Q325;
            Q325=makeQuery(id+"F6.imprint","IMPRINT",FACE,{"disambiguationData":[TD([[makeQuery(id+"F6.imprint","IMPRINT",EDGE,{"derivedFrom":sQuery(id+"F6.wireOp",EDGE,"E499.MirrorC")}),-1.0]])]});
            var Q326;
            Q326=makeQuery(id+"F6.imprint","IMPRINT",FACE,{"disambiguationData":[TD([[makeQuery(id+"F6.imprint","IMPRINT",EDGE,{"derivedFrom":sQuery(id+"F6.wireOp",EDGE,"E428.MirrorC")}),-1.0]])]});
            var Q327;
            Q327=makeQuery(id+"F6.imprint","IMPRINT",FACE,{"disambiguationData":[TD([[makeQuery(id+"F6.imprint","IMPRINT",EDGE,{"derivedFrom":sQuery(id+"F6.wireOp",EDGE,"E899.MirrorC")}),-1.0]])]});
            var Q328;
            Q328=makeQuery(id+"F6.imprint","IMPRINT",FACE,{"disambiguationData":[TD([[makeQuery(id+"F6.imprint","IMPRINT",EDGE,{"derivedFrom":sQuery(id+"F6.wireOp",EDGE,"E846.MirrorC")}),-1.0]])]});
            var Q329;
            Q329=makeQuery(id+"F6.imprint","IMPRINT",FACE,{"disambiguationData":[TD([[makeQuery(id+"F6.imprint","IMPRINT",EDGE,{"derivedFrom":sQuery(id+"F6.wireOp",EDGE,"E576.MirrorC")}),-1.0]])]});
            var Q330;
            Q330=makeQuery(id+"F6.imprint","IMPRINT",FACE,{"disambiguationData":[TD([[makeQuery(id+"F6.imprint","IMPRINT",EDGE,{"derivedFrom":sQuery(id+"F6.wireOp",EDGE,"E523.MirrorC")}),-1.0]])]});
            var Q331;
            Q331=makeQuery(id+"F6.imprint","IMPRINT",FACE,{"disambiguationData":[TD([[makeQuery(id+"F6.imprint","IMPRINT",EDGE,{"derivedFrom":sQuery(id+"F6.wireOp",EDGE,"E539.MirrorC")}),-1.0]])]});
            var Q332;
            Q332=makeQuery(id+"F6.imprint","IMPRINT",FACE,{"disambiguationData":[TD([[makeQuery(id+"F6.imprint","IMPRINT",EDGE,{"derivedFrom":sQuery(id+"F6.wireOp",EDGE,"E345.MirrorC")}),-1.0]])]});
            var Q333;
            Q333=makeQuery(id+"F6.imprint","IMPRINT",FACE,{"disambiguationData":[TD([[makeQuery(id+"F6.imprint","IMPRINT",EDGE,{"derivedFrom":sQuery(id+"F6.wireOp",EDGE,"E520.MirrorC")}),-1.0]])]});
            var Q334;
            Q334=makeQuery(id+"F6.imprint","IMPRINT",FACE,{"disambiguationData":[TD([[makeQuery(id+"F6.imprint","IMPRINT",EDGE,{"derivedFrom":sQuery(id+"F6.wireOp",EDGE,"E745.MirrorC")}),-1.0]])]});
            var Q335;
            Q335=makeQuery(id+"F6.imprint","IMPRINT",FACE,{"disambiguationData":[TD([[makeQuery(id+"F6.imprint","IMPRINT",EDGE,{"derivedFrom":sQuery(id+"F6.wireOp",EDGE,"E545.MirrorC")}),-1.0]])]});
            var Q336;
            Q336=makeQuery(id+"F6.imprint","IMPRINT",FACE,{"disambiguationData":[TD([[makeQuery(id+"F6.imprint","IMPRINT",EDGE,{"derivedFrom":sQuery(id+"F6.wireOp",EDGE,"E493.MirrorC")}),-1.0]])]});
            var Q337;
            Q337=makeQuery(id+"F6.imprint","IMPRINT",FACE,{"disambiguationData":[TD([[makeQuery(id+"F6.imprint","IMPRINT",EDGE,{"derivedFrom":sQuery(id+"F6.wireOp",EDGE,"E474.MirrorC")}),-1.0]])]});
            var Q338;
            Q338=makeQuery(id+"F6.imprint","IMPRINT",FACE,{"disambiguationData":[TD([[makeQuery(id+"F6.imprint","IMPRINT",EDGE,{"derivedFrom":sQuery(id+"F6.wireOp",EDGE,"E892.MirrorC")}),-1.0]])]});
            var Q339;
            Q339=makeQuery(id+"F6.imprint","IMPRINT",FACE,{"disambiguationData":[TD([[makeQuery(id+"F6.imprint","IMPRINT",EDGE,{"derivedFrom":sQuery(id+"F6.wireOp",EDGE,"E507.MirrorC")}),-1.0]])]});
            var Q340;
            Q340=makeQuery(id+"F6.imprint","IMPRINT",FACE,{"disambiguationData":[TD([[makeQuery(id+"F6.imprint","IMPRINT",EDGE,{"derivedFrom":sQuery(id+"F6.wireOp",EDGE,"E560.MirrorC")}),-1.0]])]});
            var Q341;
            Q341=makeQuery(id+"F6.imprint","IMPRINT",FACE,{"disambiguationData":[TD([[makeQuery(id+"F6.imprint","IMPRINT",EDGE,{"derivedFrom":sQuery(id+"F6.wireOp",EDGE,"E490.MirrorC")}),-1.0]])]});
            var Q342;
            Q342=makeQuery(id+"F6.imprint","IMPRINT",FACE,{"disambiguationData":[TD([[makeQuery(id+"F6.imprint","IMPRINT",EDGE,{"derivedFrom":sQuery(id+"F6.wireOp",EDGE,"E42.4.0.18")}),1.0]])]});
            var Q343;
            Q343=makeQuery(id+"F6.imprint","IMPRINT",FACE,{"disambiguationData":[TD([[makeQuery(id+"F6.imprint","IMPRINT",EDGE,{"derivedFrom":sQuery(id+"F6.wireOp",EDGE,"E42.3.0.9")}),1.0]])]});
            var Q344;
            Q344=makeQuery(id+"F6.imprint","IMPRINT",FACE,{"disambiguationData":[TD([[makeQuery(id+"F6.imprint","IMPRINT",EDGE,{"derivedFrom":sQuery(id+"F6.wireOp",EDGE,"E42.2.0.18")}),1.0]])]});
            var Q345;
            Q345=makeQuery(id+"F6.imprint","IMPRINT",FACE,{"disambiguationData":[TD([[makeQuery(id+"F6.imprint","IMPRINT",EDGE,{"derivedFrom":sQuery(id+"F6.wireOp",EDGE,"E42.7.0.9")}),1.0]])]});
            var Q346;
            Q346=makeQuery(id+"F6.imprint","IMPRINT",FACE,{"disambiguationData":[TD([[makeQuery(id+"F6.imprint","IMPRINT",EDGE,{"derivedFrom":sQuery(id+"F6.wireOp",EDGE,"E636.MirrorC")}),-1.0]])]});
            var Q347;
            Q347=makeQuery(id+"F6.imprint","IMPRINT",FACE,{"disambiguationData":[TD([[makeQuery(id+"F6.imprint","IMPRINT",EDGE,{"derivedFrom":sQuery(id+"F6.wireOp",EDGE,"E42.6.0.18")}),1.0]])]});
            var Q348;
            Q348=makeQuery(id+"F6.imprint","IMPRINT",FACE,{"disambiguationData":[TD([[makeQuery(id+"F6.imprint","IMPRINT",EDGE,{"derivedFrom":sQuery(id+"F6.wireOp",EDGE,"E42.5.0.9")}),1.0]])]});
            var Q349;
            Q349=makeQuery(id+"F6.imprint","IMPRINT",FACE,{"disambiguationData":[TD([[makeQuery(id+"F6.imprint","IMPRINT",EDGE,{"derivedFrom":sQuery(id+"F6.wireOp",EDGE,"E585.MirrorC")}),-1.0]])]});
            var Q350;
            Q350=makeQuery(id+"F6.imprint","IMPRINT",FACE,{"disambiguationData":[TD([[makeQuery(id+"F6.imprint","IMPRINT",EDGE,{"derivedFrom":sQuery(id+"F6.wireOp",EDGE,"E42.9.0.9")}),1.0]])]});
            var Q351;
            Q351=makeQuery(id+"F6.imprint","IMPRINT",FACE,{"disambiguationData":[TD([[makeQuery(id+"F6.imprint","IMPRINT",EDGE,{"derivedFrom":sQuery(id+"F6.wireOp",EDGE,"E42.8.0.18")}),1.0]])]});
            var Q352;
            Q352=makeQuery(id+"F6.imprint","IMPRINT",FACE,{"disambiguationData":[TD([[makeQuery(id+"F6.imprint","IMPRINT",EDGE,{"derivedFrom":sQuery(id+"F6.wireOp",EDGE,"E42.12.0.18")}),1.0]])]});
            var Q353;
            Q353=makeQuery(id+"F6.imprint","IMPRINT",FACE,{"disambiguationData":[TD([[makeQuery(id+"F6.imprint","IMPRINT",EDGE,{"derivedFrom":sQuery(id+"F6.wireOp",EDGE,"E391.MirrorC")}),-1.0]])]});
            var Q354;
            Q354=makeQuery(id+"F6.imprint","IMPRINT",FACE,{"disambiguationData":[TD([[makeQuery(id+"F6.imprint","IMPRINT",EDGE,{"derivedFrom":sQuery(id+"F6.wireOp",EDGE,"E42.11.0.9")}),1.0]])]});
            var Q355;
            Q355=makeQuery(id+"F6.imprint","IMPRINT",FACE,{"disambiguationData":[TD([[makeQuery(id+"F6.imprint","IMPRINT",EDGE,{"derivedFrom":sQuery(id+"F6.wireOp",EDGE,"E42.10.0.18")}),1.0]])]});
            var Q356;
            Q356=makeQuery(id+"F6.imprint","IMPRINT",FACE,{"disambiguationData":[TD([[makeQuery(id+"F6.imprint","IMPRINT",EDGE,{"derivedFrom":sQuery(id+"F6.wireOp",EDGE,"E42.15.0.9")}),1.0]])]});
            var Q357;
            Q357=makeQuery(id+"F6.imprint","IMPRINT",FACE,{"disambiguationData":[TD([[makeQuery(id+"F6.imprint","IMPRINT",EDGE,{"derivedFrom":sQuery(id+"F6.wireOp",EDGE,"E42.14.0.18")}),1.0]])]});
            var Q358;
            Q358=makeQuery(id+"F6.imprint","IMPRINT",FACE,{"disambiguationData":[TD([[makeQuery(id+"F6.imprint","IMPRINT",EDGE,{"derivedFrom":sQuery(id+"F6.wireOp",EDGE,"E42.13.0.9")}),1.0]])]});
            var Q359;
            Q359=makeQuery(id+"F6.imprint","IMPRINT",FACE,{"disambiguationData":[TD([[makeQuery(id+"F6.imprint","IMPRINT",EDGE,{"derivedFrom":sQuery(id+"F6.wireOp",EDGE,"E42.17.0.9")}),1.0]])]});
            var Q360;
            Q360=makeQuery(id+"F6.imprint","IMPRINT",FACE,{"disambiguationData":[TD([[makeQuery(id+"F6.imprint","IMPRINT",EDGE,{"derivedFrom":sQuery(id+"F6.wireOp",EDGE,"E566.MirrorC")}),-1.0]])]});
            var Q361;
            Q361=makeQuery(id+"F6.imprint","IMPRINT",FACE,{"disambiguationData":[TD([[makeQuery(id+"F6.imprint","IMPRINT",EDGE,{"derivedFrom":sQuery(id+"F6.wireOp",EDGE,"E42.16.0.18")}),1.0]])]});
            var Q362;
            Q362=makeQuery(id+"F6.imprint","IMPRINT",FACE,{"disambiguationData":[TD([[makeQuery(id+"F6.imprint","IMPRINT",EDGE,{"derivedFrom":sQuery(id+"F6.wireOp",EDGE,"E791.MirrorC")}),-1.0]])]});
            var Q363;
            Q363=makeQuery(id+"F6.imprint","IMPRINT",FACE,{"disambiguationData":[TD([[makeQuery(id+"F6.imprint","IMPRINT",EDGE,{"derivedFrom":sQuery(id+"F6.wireOp",EDGE,"E42.19.0.9")}),1.0]])]});
            var Q364;
            Q364=makeQuery(id+"F6.imprint","IMPRINT",FACE,{"disambiguationData":[TD([[makeQuery(id+"F6.imprint","IMPRINT",EDGE,{"derivedFrom":sQuery(id+"F6.wireOp",EDGE,"E42.18.0.18")}),1.0]])]});
            var Q365;
            Q365=makeQuery(id+"F6.imprint","IMPRINT",FACE,{"disambiguationData":[TD([[makeQuery(id+"F6.imprint","IMPRINT",EDGE,{"derivedFrom":sQuery(id+"F6.wireOp",EDGE,"E738.MirrorC")}),-1.0]])]});
            var Q366;
            Q366=makeQuery(id+"F6.imprint","IMPRINT",FACE,{"disambiguationData":[TD([[makeQuery(id+"F6.imprint","IMPRINT",EDGE,{"derivedFrom":sQuery(id+"F6.wireOp",EDGE,"E323.MirrorC")}),-1.0]])]});
            var Q367;
            Q367=makeQuery(id+"F6.imprint","IMPRINT",FACE,{"disambiguationData":[TD([[makeQuery(id+"F6.imprint","IMPRINT",EDGE,{"derivedFrom":sQuery(id+"F6.wireOp",EDGE,"E651.MirrorC")}),-1.0]])]});
            var Q368;
            Q368=makeQuery(id+"F6.imprint","IMPRINT",FACE,{"disambiguationData":[TD([[makeQuery(id+"F6.imprint","IMPRINT",EDGE,{"derivedFrom":sQuery(id+"F6.wireOp",EDGE,"E339.MirrorC")}),-1.0]])]});
            var Q369;
            Q369=makeQuery(id+"F6.imprint","IMPRINT",FACE,{"disambiguationData":[TD([[makeQuery(id+"F6.imprint","IMPRINT",EDGE,{"derivedFrom":sQuery(id+"F6.wireOp",EDGE,"E276.MirrorC")}),-1.0]])]});
            var Q370;
            Q370=makeQuery(id+"F6.imprint","IMPRINT",FACE,{"disambiguationData":[TD([[makeQuery(id+"F6.imprint","IMPRINT",EDGE,{"derivedFrom":sQuery(id+"F6.wireOp",EDGE,"E260.MirrorC")}),-1.0]])]});
            var Q371;
            Q371=makeQuery(id+"F6.imprint","IMPRINT",FACE,{"disambiguationData":[TD([[makeQuery(id+"F6.imprint","IMPRINT",EDGE,{"derivedFrom":sQuery(id+"F6.wireOp",EDGE,"E247.MirrorC")}),-1.0]])]});
            var Q372;
            Q372=makeQuery(id+"F6.imprint","IMPRINT",FACE,{"disambiguationData":[TD([[makeQuery(id+"F6.imprint","IMPRINT",EDGE,{"derivedFrom":sQuery(id+"F6.wireOp",EDGE,"E308.MirrorC")}),-1.0]])]});
            var Q373;
            Q373=makeQuery(id+"F6.imprint","IMPRINT",FACE,{"disambiguationData":[TD([[makeQuery(id+"F6.imprint","IMPRINT",EDGE,{"derivedFrom":sQuery(id+"F6.wireOp",EDGE,"E292.MirrorC")}),-1.0]])]});
            var Q374;
            Q374=makeQuery(id+"F6.imprint","IMPRINT",FACE,{"disambiguationData":[TD([[makeQuery(id+"F6.imprint","IMPRINT",EDGE,{"derivedFrom":sQuery(id+"F6.wireOp",EDGE,"E582.MirrorC")}),-1.0]])]});
            var Q375;
            Q375=makeQuery(id+"F6.imprint","IMPRINT",FACE,{"disambiguationData":[TD([[makeQuery(id+"F6.imprint","IMPRINT",EDGE,{"derivedFrom":sQuery(id+"F6.wireOp",EDGE,"E754.MirrorC")}),-1.0]])]});
            var Q376;
            Q376=makeQuery(id+"F6.imprint","IMPRINT",FACE,{"disambiguationData":[TD([[makeQuery(id+"F6.imprint","IMPRINT",EDGE,{"derivedFrom":sQuery(id+"F6.wireOp",EDGE,"E806.MirrorC")}),-1.0]])]});
            var Q377;
            Q377=makeQuery(id+"F6.imprint","IMPRINT",FACE,{"disambiguationData":[TD([[makeQuery(id+"F6.imprint","IMPRINT",EDGE,{"derivedFrom":sQuery(id+"F6.wireOp",EDGE,"E42.1.0.9")}),1.0]])]});
            var Q378;
            Q378=makeQuery(id+"F6.imprint","IMPRINT",FACE,{"disambiguationData":[TD([[makeQuery(id+"F6.imprint","IMPRINT",EDGE,{"derivedFrom":sQuery(id+"F6.wireOp",EDGE,"E554.MirrorC")}),-1.0]])]});
            var Q379;
            Q379=makeQuery(id+"F6.imprint","IMPRINT",FACE,{"disambiguationData":[TD([[makeQuery(id+"F6.imprint","IMPRINT",EDGE,{"derivedFrom":sQuery(id+"F6.wireOp",EDGE,"E606.MirrorC")}),-1.0]])]});
            var Q380;
            Q380=makeQuery(id+"F6.imprint","IMPRINT",FACE,{"disambiguationData":[TD([[makeQuery(id+"F6.imprint","IMPRINT",EDGE,{"derivedFrom":sQuery(id+"F6.wireOp",EDGE,"E536.MirrorC")}),-1.0]])]});
            var Q381;
            Q381=makeQuery(id+"F6.imprint","IMPRINT",FACE,{"disambiguationData":[TD([[makeQuery(id+"F6.imprint","IMPRINT",EDGE,{"derivedFrom":sQuery(id+"F6.wireOp",EDGE,"E760.MirrorC")}),-1.0]])]});
            var Q382;
            Q382=makeQuery(id+"F6.imprint","IMPRINT",FACE,{"disambiguationData":[TD([[makeQuery(id+"F6.imprint","IMPRINT",EDGE,{"derivedFrom":sQuery(id+"F6.wireOp",EDGE,"E42.21.0.9")}),1.0]])]});
            var Q383;
            Q383=makeQuery(id+"F6.imprint","IMPRINT",FACE,{"disambiguationData":[TD([[makeQuery(id+"F6.imprint","IMPRINT",EDGE,{"derivedFrom":sQuery(id+"F6.wireOp",EDGE,"E42.20.0.18")}),1.0]])]});
            var Q384;
            Q384=makeQuery(id+"F6.imprint","IMPRINT",FACE,{"disambiguationData":[TD([[makeQuery(id+"F6.imprint","IMPRINT",EDGE,{"derivedFrom":sQuery(id+"F6.wireOp",EDGE,"E42.24.0.18")}),1.0]])]});
            var Q385;
            Q385=makeQuery(id+"F6.imprint","IMPRINT",FACE,{"disambiguationData":[TD([[makeQuery(id+"F6.imprint","IMPRINT",EDGE,{"derivedFrom":sQuery(id+"F6.wireOp",EDGE,"E42.23.0.9")}),1.0]])]});
            var Q386;
            Q386=makeQuery(id+"F6.imprint","IMPRINT",FACE,{"disambiguationData":[TD([[makeQuery(id+"F6.imprint","IMPRINT",EDGE,{"derivedFrom":sQuery(id+"F6.wireOp",EDGE,"E569.MirrorC")}),-1.0]])]});
            var Q387;
            Q387=makeQuery(id+"F6.imprint","IMPRINT",FACE,{"disambiguationData":[TD([[makeQuery(id+"F6.imprint","IMPRINT",EDGE,{"derivedFrom":sQuery(id+"F6.wireOp",EDGE,"E621.MirrorC")}),-1.0]])]});
            var Q388;
            Q388=makeQuery(id+"F6.imprint","IMPRINT",FACE,{"disambiguationData":[TD([[makeQuery(id+"F6.imprint","IMPRINT",EDGE,{"derivedFrom":sQuery(id+"F6.wireOp",EDGE,"E42.22.0.18")}),1.0]])]});
            var Q389;
            Q389=makeQuery(id+"F6.imprint","IMPRINT",FACE,{"disambiguationData":[TD([[makeQuery(id+"F6.imprint","IMPRINT",EDGE,{"derivedFrom":sQuery(id+"F6.wireOp",EDGE,"E42.27.0.9")}),1.0]])]});
            var Q390;
            Q390=makeQuery(id+"F6.imprint","IMPRINT",FACE,{"disambiguationData":[TD([[makeQuery(id+"F6.imprint","IMPRINT",EDGE,{"derivedFrom":sQuery(id+"F6.wireOp",EDGE,"E42.26.0.18")}),1.0]])]});
            var Q391;
            Q391=makeQuery(id+"F6.imprint","IMPRINT",FACE,{"disambiguationData":[TD([[makeQuery(id+"F6.imprint","IMPRINT",EDGE,{"derivedFrom":sQuery(id+"F6.wireOp",EDGE,"E42.25.0.9")}),1.0]])]});
            var Q392;
            Q392=makeQuery(id+"F6.imprint","IMPRINT",FACE,{"disambiguationData":[TD([[makeQuery(id+"F6.imprint","IMPRINT",EDGE,{"derivedFrom":sQuery(id+"F6.wireOp",EDGE,"E42.29.0.9")}),1.0]])]});
            var Q393;
            Q393=makeQuery(id+"F6.imprint","IMPRINT",FACE,{"disambiguationData":[TD([[makeQuery(id+"F6.imprint","IMPRINT",EDGE,{"derivedFrom":sQuery(id+"F6.wireOp",EDGE,"E42.28.0.18")}),1.0]])]});
            var Q394;
            Q394=makeQuery(id+"F6.imprint","IMPRINT",FACE,{"disambiguationData":[TD([[makeQuery(id+"F6.imprint","IMPRINT",EDGE,{"derivedFrom":sQuery(id+"F6.wireOp",EDGE,"E375.MirrorC")}),-1.0]])]});
            var Q395;
            Q395=makeQuery(id+"F6.imprint","IMPRINT",FACE,{"disambiguationData":[TD([[makeQuery(id+"F6.imprint","IMPRINT",EDGE,{"derivedFrom":sQuery(id+"F6.wireOp",EDGE,"E42.32.0.18")}),1.0]])]});
            var Q396;
            Q396=makeQuery(id+"F6.imprint","IMPRINT",FACE,{"disambiguationData":[TD([[makeQuery(id+"F6.imprint","IMPRINT",EDGE,{"derivedFrom":sQuery(id+"F6.wireOp",EDGE,"E551.MirrorC")}),-1.0]])]});
            var Q397;
            Q397=makeQuery(id+"F6.imprint","IMPRINT",FACE,{"disambiguationData":[TD([[makeQuery(id+"F6.imprint","IMPRINT",EDGE,{"derivedFrom":sQuery(id+"F6.wireOp",EDGE,"E42.31.0.9")}),1.0]])]});
            var Q398;
            Q398=makeQuery(id+"F6.imprint","IMPRINT",FACE,{"disambiguationData":[TD([[makeQuery(id+"F6.imprint","IMPRINT",EDGE,{"derivedFrom":sQuery(id+"F6.wireOp",EDGE,"E42.30.0.18")}),1.0]])]});
            var Q399;
            Q399=makeQuery(id+"F6.imprint","IMPRINT",FACE,{"disambiguationData":[TD([[makeQuery(id+"F6.imprint","IMPRINT",EDGE,{"derivedFrom":sQuery(id+"F6.wireOp",EDGE,"E776.MirrorC")}),-1.0]])]});
            var Q400;
            Q400=makeQuery(id+"F6.imprint","IMPRINT",FACE,{"disambiguationData":[TD([[makeQuery(id+"F6.imprint","IMPRINT",EDGE,{"derivedFrom":sQuery(id+"F6.wireOp",EDGE,"E451.MirrorC")}),-1.0]])]});
            var Q401;
            Q401=makeQuery(id+"F6.imprint","IMPRINT",FACE,{"disambiguationData":[TD([[makeQuery(id+"F6.imprint","IMPRINT",EDGE,{"derivedFrom":sQuery(id+"F6.wireOp",EDGE,"E642.MirrorC")}),-1.0]])]});
            var Q402;
            Q402=makeQuery(id+"F6.imprint","IMPRINT",FACE,{"disambiguationData":[TD([[makeQuery(id+"F6.imprint","IMPRINT",EDGE,{"derivedFrom":sQuery(id+"F6.wireOp",EDGE,"E851.MirrorC")}),-1.0]])]});
            var Q403;
            Q403=makeQuery(id+"F6.imprint","IMPRINT",FACE,{"disambiguationData":[TD([[makeQuery(id+"F6.imprint","IMPRINT",EDGE,{"derivedFrom":sQuery(id+"F6.wireOp",EDGE,"E799.MirrorC")}),-1.0]])]});
            var Q404;
            Q404=makeQuery(id+"F6.imprint","IMPRINT",FACE,{"disambiguationData":[TD([[makeQuery(id+"F6.imprint","IMPRINT",EDGE,{"derivedFrom":sQuery(id+"F6.wireOp",EDGE,"E697.MirrorC")}),-1.0]])]});
            var Q405;
            Q405=makeQuery(id+"F6.imprint","IMPRINT",FACE,{"disambiguationData":[TD([[makeQuery(id+"F6.imprint","IMPRINT",EDGE,{"derivedFrom":sQuery(id+"F6.wireOp",EDGE,"E645.MirrorC")}),-1.0]])]});
            var Q406;
            Q406=makeQuery(id+"F6.imprint","IMPRINT",FACE,{"disambiguationData":[TD([[makeQuery(id+"F6.imprint","IMPRINT",EDGE,{"derivedFrom":sQuery(id+"F6.wireOp",EDGE,"E467.MirrorC")}),-1.0]])]});
            var Q407;
            Q407=makeQuery(id+"F6.imprint","IMPRINT",FACE,{"disambiguationData":[TD([[makeQuery(id+"F6.imprint","IMPRINT",EDGE,{"derivedFrom":sQuery(id+"F6.wireOp",EDGE,"E657.MirrorC")}),-1.0]])]});
            var Q408;
            Q408=makeQuery(id+"F6.imprint","IMPRINT",FACE,{"disambiguationData":[TD([[makeQuery(id+"F6.imprint","IMPRINT",EDGE,{"derivedFrom":sQuery(id+"F6.wireOp",EDGE,"E814.MirrorC")}),-1.0]])]});
            var Q409;
            Q409=makeQuery(id+"F6.imprint","IMPRINT",FACE,{"disambiguationData":[TD([[makeQuery(id+"F6.imprint","IMPRINT",EDGE,{"derivedFrom":sQuery(id+"F6.wireOp",EDGE,"E866.MirrorC")}),-1.0]])]});
            var Q410;
            Q410=makeQuery(id+"F6.imprint","IMPRINT",FACE,{"disambiguationData":[TD([[makeQuery(id+"F6.imprint","IMPRINT",EDGE,{"derivedFrom":sQuery(id+"F6.wireOp",EDGE,"E660.MirrorC")}),-1.0]])]});
            var Q411;
            Q411=makeQuery(id+"F6.imprint","IMPRINT",FACE,{"disambiguationData":[TD([[makeQuery(id+"F6.imprint","IMPRINT",EDGE,{"derivedFrom":sQuery(id+"F6.wireOp",EDGE,"E712.MirrorC")}),-1.0]])]});
            var Q412;
            Q412=makeQuery(id+"F6.imprint","IMPRINT",FACE,{"disambiguationData":[TD([[makeQuery(id+"F6.imprint","IMPRINT",EDGE,{"derivedFrom":sQuery(id+"F6.wireOp",EDGE,"E420.MirrorC")}),-1.0]])]});
            var Q413;
            Q413=makeQuery(id+"F6.imprint","IMPRINT",FACE,{"disambiguationData":[TD([[makeQuery(id+"F6.imprint","IMPRINT",EDGE,{"derivedFrom":sQuery(id+"F6.wireOp",EDGE,"E321.MirrorC")}),-1.0]])]});
            var Q414;
            Q414=makeQuery(id+"F6.imprint","IMPRINT",FACE,{"disambiguationData":[TD([[makeQuery(id+"F6.imprint","IMPRINT",EDGE,{"derivedFrom":sQuery(id+"F6.wireOp",EDGE,"E614.MirrorC")}),-1.0]])]});
            var Q415;
            Q415=makeQuery(id+"F6.imprint","IMPRINT",FACE,{"disambiguationData":[TD([[makeQuery(id+"F6.imprint","IMPRINT",EDGE,{"derivedFrom":sQuery(id+"F6.wireOp",EDGE,"E337.MirrorC")}),-1.0]])]});
            var Q416;
            Q416=makeQuery(id+"F6.imprint","IMPRINT",FACE,{"disambiguationData":[TD([[makeQuery(id+"F6.imprint","IMPRINT",EDGE,{"derivedFrom":sQuery(id+"F6.wireOp",EDGE,"E245.MirrorC")}),-1.0]])]});
            var Q417;
            Q417=makeQuery(id+"F6.imprint","IMPRINT",FACE,{"disambiguationData":[TD([[makeQuery(id+"F6.imprint","IMPRINT",EDGE,{"derivedFrom":sQuery(id+"F6.wireOp",EDGE,"E306.MirrorC")}),-1.0]])]});
            var Q418;
            Q418=makeQuery(id+"F6.imprint","IMPRINT",FACE,{"disambiguationData":[TD([[makeQuery(id+"F6.imprint","IMPRINT",EDGE,{"derivedFrom":sQuery(id+"F6.wireOp",EDGE,"E290.MirrorC")}),-1.0]])]});
            var Q419;
            Q419=makeQuery(id+"F6.imprint","IMPRINT",FACE,{"disambiguationData":[TD([[makeQuery(id+"F6.imprint","IMPRINT",EDGE,{"derivedFrom":sQuery(id+"F6.wireOp",EDGE,"E274.MirrorC")}),-1.0]])]});
            var Q420;
            Q420=makeQuery(id+"F6.imprint","IMPRINT",FACE,{"disambiguationData":[TD([[makeQuery(id+"F6.imprint","IMPRINT",EDGE,{"derivedFrom":sQuery(id+"F6.wireOp",EDGE,"E597.MirrorC")}),-1.0]])]});
            var Q421;
            Q421=makeQuery(id+"F6.imprint","IMPRINT",FACE,{"disambiguationData":[TD([[makeQuery(id+"F6.imprint","IMPRINT",EDGE,{"derivedFrom":sQuery(id+"F6.wireOp",EDGE,"E42.1.0.7")}),1.0]])]});
            var Q422;
            Q422=makeQuery(id+"F6.imprint","IMPRINT",FACE,{"disambiguationData":[TD([[makeQuery(id+"F6.imprint","IMPRINT",EDGE,{"derivedFrom":sQuery(id+"F6.wireOp",EDGE,"E42.3.0.7")}),1.0]])]});
            var Q423;
            Q423=makeQuery(id+"F6.imprint","IMPRINT",FACE,{"disambiguationData":[TD([[makeQuery(id+"F6.imprint","IMPRINT",EDGE,{"derivedFrom":sQuery(id+"F6.wireOp",EDGE,"E666.MirrorC")}),-1.0]])]});
            var Q424;
            Q424=makeQuery(id+"F6.imprint","IMPRINT",FACE,{"disambiguationData":[TD([[makeQuery(id+"F6.imprint","IMPRINT",EDGE,{"derivedFrom":sQuery(id+"F6.wireOp",EDGE,"E42.2.0.16")}),1.0]])]});
            var Q425;
            Q425=makeQuery(id+"F6.imprint","IMPRINT",FACE,{"disambiguationData":[TD([[makeQuery(id+"F6.imprint","IMPRINT",EDGE,{"derivedFrom":sQuery(id+"F6.wireOp",EDGE,"E42.6.0.16")}),1.0]])]});
            var Q426;
            Q426=makeQuery(id+"F6.imprint","IMPRINT",FACE,{"disambiguationData":[TD([[makeQuery(id+"F6.imprint","IMPRINT",EDGE,{"derivedFrom":sQuery(id+"F6.wireOp",EDGE,"E769.MirrorC")}),-1.0]])]});
            var Q427;
            Q427=makeQuery(id+"F6.imprint","IMPRINT",FACE,{"disambiguationData":[TD([[makeQuery(id+"F6.imprint","IMPRINT",EDGE,{"derivedFrom":sQuery(id+"F6.wireOp",EDGE,"E42.5.0.7")}),1.0]])]});
            var Q428;
            Q428=makeQuery(id+"F6.imprint","IMPRINT",FACE,{"disambiguationData":[TD([[makeQuery(id+"F6.imprint","IMPRINT",EDGE,{"derivedFrom":sQuery(id+"F6.wireOp",EDGE,"E42.4.0.16")}),1.0]])]});
            var Q429;
            Q429=makeQuery(id+"F6.imprint","IMPRINT",FACE,{"disambiguationData":[TD([[makeQuery(id+"F6.imprint","IMPRINT",EDGE,{"derivedFrom":sQuery(id+"F6.wireOp",EDGE,"E436.MirrorC")}),-1.0]])]});
            var Q430;
            Q430=makeQuery(id+"F6.imprint","IMPRINT",FACE,{"disambiguationData":[TD([[makeQuery(id+"F6.imprint","IMPRINT",EDGE,{"derivedFrom":sQuery(id+"F6.wireOp",EDGE,"E626.MirrorC")}),-1.0]])]});
            var Q431;
            Q431=makeQuery(id+"F6.imprint","IMPRINT",FACE,{"disambiguationData":[TD([[makeQuery(id+"F6.imprint","IMPRINT",EDGE,{"derivedFrom":sQuery(id+"F6.wireOp",EDGE,"E784.MirrorC")}),-1.0]])]});
            var Q432;
            Q432=makeQuery(id+"F6.imprint","IMPRINT",FACE,{"disambiguationData":[TD([[makeQuery(id+"F6.imprint","IMPRINT",EDGE,{"derivedFrom":sQuery(id+"F6.wireOp",EDGE,"E835.MirrorC")}),-1.0]])]});
            var Q433;
            Q433=makeQuery(id+"F6.imprint","IMPRINT",FACE,{"disambiguationData":[TD([[makeQuery(id+"F6.imprint","IMPRINT",EDGE,{"derivedFrom":sQuery(id+"F6.wireOp",EDGE,"E629.MirrorC")}),-1.0]])]});
            var Q434;
            Q434=makeQuery(id+"F6.imprint","IMPRINT",FACE,{"disambiguationData":[TD([[makeQuery(id+"F6.imprint","IMPRINT",EDGE,{"derivedFrom":sQuery(id+"F6.wireOp",EDGE,"E682.MirrorC")}),-1.0]])]});
            var Q435;
            Q435=makeQuery(id+"F6.imprint","IMPRINT",FACE,{"disambiguationData":[TD([[makeQuery(id+"F6.imprint","IMPRINT",EDGE,{"derivedFrom":sQuery(id+"F6.wireOp",EDGE,"E42.26.0.16")}),1.0]])]});
            var Q436;
            Q436=makeQuery(id+"F6.imprint","IMPRINT",FACE,{"disambiguationData":[TD([[makeQuery(id+"F6.imprint","IMPRINT",EDGE,{"derivedFrom":sQuery(id+"F6.wireOp",EDGE,"E42.25.0.7")}),1.0]])]});
            var Q437;
            Q437=makeQuery(id+"F6.imprint","IMPRINT",FACE,{"disambiguationData":[TD([[makeQuery(id+"F6.imprint","IMPRINT",EDGE,{"derivedFrom":sQuery(id+"F6.wireOp",EDGE,"E42.24.0.16")}),1.0]])]});
            var Q438;
            Q438=makeQuery(id+"F6.imprint","IMPRINT",FACE,{"disambiguationData":[TD([[makeQuery(id+"F6.imprint","IMPRINT",EDGE,{"derivedFrom":sQuery(id+"F6.wireOp",EDGE,"E42.29.0.7")}),1.0]])]});
            var Q439;
            Q439=makeQuery(id+"F6.imprint","IMPRINT",FACE,{"disambiguationData":[TD([[makeQuery(id+"F6.imprint","IMPRINT",EDGE,{"derivedFrom":sQuery(id+"F6.wireOp",EDGE,"E512.MirrorC")}),-1.0]])]});
            var Q440;
            Q440=makeQuery(id+"F6.imprint","IMPRINT",FACE,{"disambiguationData":[TD([[makeQuery(id+"F6.imprint","IMPRINT",EDGE,{"derivedFrom":sQuery(id+"F6.wireOp",EDGE,"E42.28.0.16")}),1.0]])]});
            var Q441;
            Q441=makeQuery(id+"F6.imprint","IMPRINT",FACE,{"disambiguationData":[TD([[makeQuery(id+"F6.imprint","IMPRINT",EDGE,{"derivedFrom":sQuery(id+"F6.wireOp",EDGE,"E42.27.0.7")}),1.0]])]});
            var Q442;
            Q442=makeQuery(id+"F6.imprint","IMPRINT",FACE,{"disambiguationData":[TD([[makeQuery(id+"F6.imprint","IMPRINT",EDGE,{"derivedFrom":sQuery(id+"F6.wireOp",EDGE,"E42.31.0.7")}),1.0]])]});
            var Q443;
            Q443=makeQuery(id+"F6.imprint","IMPRINT",FACE,{"disambiguationData":[TD([[makeQuery(id+"F6.imprint","IMPRINT",EDGE,{"derivedFrom":sQuery(id+"F6.wireOp",EDGE,"E42.30.0.16")}),1.0]])]});
            var Q444;
            Q444=makeQuery(id+"F6.imprint","IMPRINT",FACE,{"disambiguationData":[TD([[makeQuery(id+"F6.imprint","IMPRINT",EDGE,{"derivedFrom":sQuery(id+"F6.wireOp",EDGE,"E703.MirrorC")}),-1.0]])]});
            var Q445;
            Q445=makeQuery(id+"F6.imprint","IMPRINT",FACE,{"disambiguationData":[TD([[makeQuery(id+"F6.imprint","IMPRINT",EDGE,{"derivedFrom":sQuery(id+"F6.wireOp",EDGE,"E42.32.0.16")}),1.0]])]});
            var Q446;
            Q446=makeQuery(id+"F6.imprint","IMPRINT",FACE,{"disambiguationData":[TD([[makeQuery(id+"F6.imprint","IMPRINT",EDGE,{"derivedFrom":sQuery(id+"F6.wireOp",EDGE,"E859.MirrorC")}),-1.0]])]});
            var Q447;
            Q447=makeQuery(id+"F6.imprint","IMPRINT",FACE,{"disambiguationData":[TD([[makeQuery(id+"F6.imprint","IMPRINT",EDGE,{"derivedFrom":sQuery(id+"F6.wireOp",EDGE,"E706.MirrorC")}),-1.0]])]});
            var Q448;
            Q448=makeQuery(id+"F6.imprint","IMPRINT",FACE,{"disambiguationData":[TD([[makeQuery(id+"F6.imprint","IMPRINT",EDGE,{"derivedFrom":sQuery(id+"F6.wireOp",EDGE,"E42.9.0.7")}),1.0]])]});
            var Q449;
            Q449=makeQuery(id+"F6.imprint","IMPRINT",FACE,{"disambiguationData":[TD([[makeQuery(id+"F6.imprint","IMPRINT",EDGE,{"derivedFrom":sQuery(id+"F6.wireOp",EDGE,"E42.8.0.16")}),1.0]])]});
            var Q450;
            Q450=makeQuery(id+"F6.imprint","IMPRINT",FACE,{"disambiguationData":[TD([[makeQuery(id+"F6.imprint","IMPRINT",EDGE,{"derivedFrom":sQuery(id+"F6.wireOp",EDGE,"E42.7.0.7")}),1.0]])]});
            var Q451;
            Q451=makeQuery(id+"F6.imprint","IMPRINT",FACE,{"disambiguationData":[TD([[makeQuery(id+"F6.imprint","IMPRINT",EDGE,{"derivedFrom":sQuery(id+"F6.wireOp",EDGE,"E528.MirrorC")}),-1.0]])]});
            var Q452;
            Q452=makeQuery(id+"F6.imprint","IMPRINT",FACE,{"disambiguationData":[TD([[makeQuery(id+"F6.imprint","IMPRINT",EDGE,{"derivedFrom":sQuery(id+"F6.wireOp",EDGE,"E42.11.0.7")}),1.0]])]});
            var Q453;
            Q453=makeQuery(id+"F6.imprint","IMPRINT",FACE,{"disambiguationData":[TD([[makeQuery(id+"F6.imprint","IMPRINT",EDGE,{"derivedFrom":sQuery(id+"F6.wireOp",EDGE,"E42.10.0.16")}),1.0]])]});
            var Q454;
            Q454=makeQuery(id+"F6.imprint","IMPRINT",FACE,{"disambiguationData":[TD([[makeQuery(id+"F6.imprint","IMPRINT",EDGE,{"derivedFrom":sQuery(id+"F6.wireOp",EDGE,"E42.14.0.16")}),1.0]])]});
            var Q455;
            Q455=makeQuery(id+"F6.imprint","IMPRINT",FACE,{"disambiguationData":[TD([[makeQuery(id+"F6.imprint","IMPRINT",EDGE,{"derivedFrom":sQuery(id+"F6.wireOp",EDGE,"E42.13.0.7")}),1.0]])]});
            var Q456;
            Q456=makeQuery(id+"F6.imprint","IMPRINT",FACE,{"disambiguationData":[TD([[makeQuery(id+"F6.imprint","IMPRINT",EDGE,{"derivedFrom":sQuery(id+"F6.wireOp",EDGE,"E42.12.0.16")}),1.0]])]});
            var Q457;
            Q457=makeQuery(id+"F6.imprint","IMPRINT",FACE,{"disambiguationData":[TD([[makeQuery(id+"F6.imprint","IMPRINT",EDGE,{"derivedFrom":sQuery(id+"F6.wireOp",EDGE,"E718.MirrorC")}),-1.0]])]});
            var Q458;
            Q458=makeQuery(id+"F6.imprint","IMPRINT",FACE,{"disambiguationData":[TD([[makeQuery(id+"F6.imprint","IMPRINT",EDGE,{"derivedFrom":sQuery(id+"F6.wireOp",EDGE,"E42.17.0.7")}),1.0]])]});
            var Q459;
            Q459=makeQuery(id+"F6.imprint","IMPRINT",FACE,{"disambiguationData":[TD([[makeQuery(id+"F6.imprint","IMPRINT",EDGE,{"derivedFrom":sQuery(id+"F6.wireOp",EDGE,"E42.16.0.16")}),1.0]])]});
            var Q460;
            Q460=makeQuery(id+"F6.imprint","IMPRINT",FACE,{"disambiguationData":[TD([[makeQuery(id+"F6.imprint","IMPRINT",EDGE,{"derivedFrom":sQuery(id+"F6.wireOp",EDGE,"E42.15.0.7")}),1.0]])]});
            var Q461;
            Q461=makeQuery(id+"F6.imprint","IMPRINT",FACE,{"disambiguationData":[TD([[makeQuery(id+"F6.imprint","IMPRINT",EDGE,{"derivedFrom":sQuery(id+"F6.wireOp",EDGE,"E42.18.0.16")}),1.0]])]});
            var Q462;
            Q462=makeQuery(id+"F6.imprint","IMPRINT",FACE,{"disambiguationData":[TD([[makeQuery(id+"F6.imprint","IMPRINT",EDGE,{"derivedFrom":sQuery(id+"F6.wireOp",EDGE,"E42.21.0.7")}),1.0]])]});
            var Q463;
            Q463=makeQuery(id+"F6.imprint","IMPRINT",FACE,{"disambiguationData":[TD([[makeQuery(id+"F6.imprint","IMPRINT",EDGE,{"derivedFrom":sQuery(id+"F6.wireOp",EDGE,"E42.20.0.16")}),1.0]])]});
            var Q464;
            Q464=makeQuery(id+"F6.imprint","IMPRINT",FACE,{"disambiguationData":[TD([[makeQuery(id+"F6.imprint","IMPRINT",EDGE,{"derivedFrom":sQuery(id+"F6.wireOp",EDGE,"E42.19.0.7")}),1.0]])]});
            var Q465;
            Q465=makeQuery(id+"F6.imprint","IMPRINT",FACE,{"disambiguationData":[TD([[makeQuery(id+"F6.imprint","IMPRINT",EDGE,{"derivedFrom":sQuery(id+"F6.wireOp",EDGE,"E721.MirrorC")}),-1.0]])]});
            var Q466;
            Q466=makeQuery(id+"F6.imprint","IMPRINT",FACE,{"disambiguationData":[TD([[makeQuery(id+"F6.imprint","IMPRINT",EDGE,{"derivedFrom":sQuery(id+"F6.wireOp",EDGE,"E42.23.0.7")}),1.0]])]});
            var Q467;
            Q467=makeQuery(id+"F6.imprint","IMPRINT",FACE,{"disambiguationData":[TD([[makeQuery(id+"F6.imprint","IMPRINT",EDGE,{"derivedFrom":sQuery(id+"F6.wireOp",EDGE,"E42.22.0.16")}),1.0]])]});
            var Q468;
            Q468=makeQuery(id+"F6.imprint","IMPRINT",FACE,{"disambiguationData":[TD([[makeQuery(id+"F6.imprint","IMPRINT",EDGE,{"derivedFrom":sQuery(id+"F6.wireOp",EDGE,"E338.MirrorC")}),-1.0]])]});
            var Q469;
            Q469=makeQuery(id+"F6.imprint","IMPRINT",FACE,{"disambiguationData":[TD([[makeQuery(id+"F6.imprint","IMPRINT",EDGE,{"derivedFrom":sQuery(id+"F6.wireOp",EDGE,"E246.MirrorC")}),-1.0]])]});
            var Q470;
            Q470=makeQuery(id+"F6.imprint","IMPRINT",FACE,{"disambiguationData":[TD([[makeQuery(id+"F6.imprint","IMPRINT",EDGE,{"derivedFrom":sQuery(id+"F6.wireOp",EDGE,"E482.MirrorC")}),-1.0]])]});
            var Q471;
            Q471=makeQuery(id+"F6.imprint","IMPRINT",FACE,{"disambiguationData":[TD([[makeQuery(id+"F6.imprint","IMPRINT",EDGE,{"derivedFrom":sQuery(id+"F6.wireOp",EDGE,"E672.MirrorC")}),-1.0]])]});
            var Q472;
            Q472=makeQuery(id+"F6.imprint","IMPRINT",FACE,{"disambiguationData":[TD([[makeQuery(id+"F6.imprint","IMPRINT",EDGE,{"derivedFrom":sQuery(id+"F6.wireOp",EDGE,"E307.MirrorC")}),-1.0]])]});
            var Q473;
            Q473=makeQuery(id+"F6.imprint","IMPRINT",FACE,{"disambiguationData":[TD([[makeQuery(id+"F6.imprint","IMPRINT",EDGE,{"derivedFrom":sQuery(id+"F6.wireOp",EDGE,"E291.MirrorC")}),-1.0]])]});
            var Q474;
            Q474=makeQuery(id+"F6.imprint","IMPRINT",FACE,{"disambiguationData":[TD([[makeQuery(id+"F6.imprint","IMPRINT",EDGE,{"derivedFrom":sQuery(id+"F6.wireOp",EDGE,"E275.MirrorC")}),-1.0]])]});
            var Q475;
            Q475=makeQuery(id+"F6.imprint","IMPRINT",FACE,{"disambiguationData":[TD([[makeQuery(id+"F6.imprint","IMPRINT",EDGE,{"derivedFrom":sQuery(id+"F6.wireOp",EDGE,"E42.1.0.8")}),1.0]])]});
            var Q476;
            Q476=makeQuery(id+"F6.imprint","IMPRINT",FACE,{"disambiguationData":[TD([[makeQuery(id+"F6.imprint","IMPRINT",EDGE,{"derivedFrom":sQuery(id+"F6.wireOp",EDGE,"E829.MirrorC")}),-1.0]])]});
            var Q477;
            Q477=makeQuery(id+"F6.imprint","IMPRINT",FACE,{"disambiguationData":[TD([[makeQuery(id+"F6.imprint","IMPRINT",EDGE,{"derivedFrom":sQuery(id+"F6.wireOp",EDGE,"E42.3.0.8")}),1.0]])]});
            var Q478;
            Q478=makeQuery(id+"F6.imprint","IMPRINT",FACE,{"disambiguationData":[TD([[makeQuery(id+"F6.imprint","IMPRINT",EDGE,{"derivedFrom":sQuery(id+"F6.wireOp",EDGE,"E42.2.0.17")}),1.0]])]});
            var Q479;
            Q479=makeQuery(id+"F6.imprint","IMPRINT",FACE,{"disambiguationData":[TD([[makeQuery(id+"F6.imprint","IMPRINT",EDGE,{"derivedFrom":sQuery(id+"F6.wireOp",EDGE,"E881.MirrorC")}),-1.0]])]});
            var Q480;
            Q480=makeQuery(id+"F6.imprint","IMPRINT",FACE,{"disambiguationData":[TD([[makeQuery(id+"F6.imprint","IMPRINT",EDGE,{"derivedFrom":sQuery(id+"F6.wireOp",EDGE,"E42.6.0.17")}),1.0]])]});
            var Q481;
            Q481=makeQuery(id+"F6.imprint","IMPRINT",FACE,{"disambiguationData":[TD([[makeQuery(id+"F6.imprint","IMPRINT",EDGE,{"derivedFrom":sQuery(id+"F6.wireOp",EDGE,"E675.MirrorC")}),-1.0]])]});
            var Q482;
            Q482=makeQuery(id+"F6.imprint","IMPRINT",FACE,{"disambiguationData":[TD([[makeQuery(id+"F6.imprint","IMPRINT",EDGE,{"derivedFrom":sQuery(id+"F6.wireOp",EDGE,"E42.5.0.8")}),1.0]])]});
            var Q483;
            Q483=makeQuery(id+"F6.imprint","IMPRINT",FACE,{"disambiguationData":[TD([[makeQuery(id+"F6.imprint","IMPRINT",EDGE,{"derivedFrom":sQuery(id+"F6.wireOp",EDGE,"E42.4.0.17")}),1.0]])]});
            var Q484;
            Q484=makeQuery(id+"F6.imprint","IMPRINT",FACE,{"disambiguationData":[TD([[makeQuery(id+"F6.imprint","IMPRINT",EDGE,{"derivedFrom":sQuery(id+"F6.wireOp",EDGE,"E42.9.0.8")}),1.0]])]});
            var Q485;
            Q485=makeQuery(id+"F6.imprint","IMPRINT",FACE,{"disambiguationData":[TD([[makeQuery(id+"F6.imprint","IMPRINT",EDGE,{"derivedFrom":sQuery(id+"F6.wireOp",EDGE,"E42.8.0.17")}),1.0]])]});
            var Q486;
            Q486=makeQuery(id+"F6.imprint","IMPRINT",FACE,{"disambiguationData":[TD([[makeQuery(id+"F6.imprint","IMPRINT",EDGE,{"derivedFrom":sQuery(id+"F6.wireOp",EDGE,"E728.MirrorC")}),-1.0]])]});
            var Q487;
            Q487=makeQuery(id+"F6.imprint","IMPRINT",FACE,{"disambiguationData":[TD([[makeQuery(id+"F6.imprint","IMPRINT",EDGE,{"derivedFrom":sQuery(id+"F6.wireOp",EDGE,"E42.7.0.8")}),1.0]])]});
            var Q488;
            Q488=makeQuery(id+"F6.imprint","IMPRINT",FACE,{"disambiguationData":[TD([[makeQuery(id+"F6.imprint","IMPRINT",EDGE,{"derivedFrom":sQuery(id+"F6.wireOp",EDGE,"E497.MirrorC")}),-1.0]])]});
            var Q489;
            Q489=makeQuery(id+"F6.imprint","IMPRINT",FACE,{"disambiguationData":[TD([[makeQuery(id+"F6.imprint","IMPRINT",EDGE,{"derivedFrom":sQuery(id+"F6.wireOp",EDGE,"E688.MirrorC")}),-1.0]])]});
            var Q490;
            Q490=makeQuery(id+"F6.imprint","IMPRINT",FACE,{"disambiguationData":[TD([[makeQuery(id+"F6.imprint","IMPRINT",EDGE,{"derivedFrom":sQuery(id+"F6.wireOp",EDGE,"E844.MirrorC")}),-1.0]])]});
            var Q491;
            Q491=makeQuery(id+"F6.imprint","IMPRINT",FACE,{"disambiguationData":[TD([[makeQuery(id+"F6.imprint","IMPRINT",EDGE,{"derivedFrom":sQuery(id+"F6.wireOp",EDGE,"E897.MirrorC")}),-1.0]])]});
            var Q492;
            Q492=makeQuery(id+"F6.imprint","IMPRINT",FACE,{"disambiguationData":[TD([[makeQuery(id+"F6.imprint","IMPRINT",EDGE,{"derivedFrom":sQuery(id+"F6.wireOp",EDGE,"E690.MirrorC")}),-1.0]])]});
            var Q493;
            Q493=makeQuery(id+"F6.imprint","IMPRINT",FACE,{"disambiguationData":[TD([[makeQuery(id+"F6.imprint","IMPRINT",EDGE,{"derivedFrom":sQuery(id+"F6.wireOp",EDGE,"E322.MirrorC")}),-1.0]])]});
            var Q494;
            Q494=makeQuery(id+"F6.imprint","IMPRINT",FACE,{"disambiguationData":[TD([[makeQuery(id+"F6.imprint","IMPRINT",EDGE,{"derivedFrom":sQuery(id+"F6.wireOp",EDGE,"E42.29.0.8")}),1.0]])]});
            var Q495;
            Q495=makeQuery(id+"F6.imprint","IMPRINT",FACE,{"disambiguationData":[TD([[makeQuery(id+"F6.imprint","IMPRINT",EDGE,{"derivedFrom":sQuery(id+"F6.wireOp",EDGE,"E42.28.0.17")}),1.0]])]});
            var Q496;
            Q496=makeQuery(id+"F6.imprint","IMPRINT",FACE,{"disambiguationData":[TD([[makeQuery(id+"F6.imprint","IMPRINT",EDGE,{"derivedFrom":sQuery(id+"F6.wireOp",EDGE,"E42.27.0.8")}),1.0]])]});
            var Q497;
            Q497=makeQuery(id+"F6.imprint","IMPRINT",FACE,{"disambiguationData":[TD([[makeQuery(id+"F6.imprint","IMPRINT",EDGE,{"derivedFrom":sQuery(id+"F6.wireOp",EDGE,"E42.31.0.8")}),1.0]])]});
            var Q498;
            Q498=makeQuery(id+"F6.imprint","IMPRINT",FACE,{"disambiguationData":[TD([[makeQuery(id+"F6.imprint","IMPRINT",EDGE,{"derivedFrom":sQuery(id+"F6.wireOp",EDGE,"E42.30.0.17")}),1.0]])]});
            var Q499;
            Q499=makeQuery(id+"F6.imprint","IMPRINT",FACE,{"disambiguationData":[TD([[makeQuery(id+"F6.imprint","IMPRINT",EDGE,{"derivedFrom":sQuery(id+"F6.wireOp",EDGE,"E42.32.0.17")}),1.0]])]});
            var Q500;
            Q500=makeQuery(id+"F6.imprint","IMPRINT",FACE,{"disambiguationData":[TD([[makeQuery(id+"F6.imprint","IMPRINT",EDGE,{"derivedFrom":sQuery(id+"F6.wireOp",EDGE,"E574.MirrorC")}),-1.0]])]});
            var Q501;
            Q501=makeQuery(id+"F6.imprint","IMPRINT",FACE,{"disambiguationData":[TD([[makeQuery(id+"F6.imprint","IMPRINT",EDGE,{"derivedFrom":sQuery(id+"F6.wireOp",EDGE,"E42.11.0.8")}),1.0]])]});
            var Q502;
            Q502=makeQuery(id+"F6.imprint","IMPRINT",FACE,{"disambiguationData":[TD([[makeQuery(id+"F6.imprint","IMPRINT",EDGE,{"derivedFrom":sQuery(id+"F6.wireOp",EDGE,"E42.10.0.17")}),1.0]])]});
            var Q503;
            Q503=makeQuery(id+"F6.imprint","IMPRINT",FACE,{"disambiguationData":[TD([[makeQuery(id+"F6.imprint","IMPRINT",EDGE,{"derivedFrom":sQuery(id+"F6.wireOp",EDGE,"E42.14.0.17")}),1.0]])]});
            var Q504;
            Q504=makeQuery(id+"F6.imprint","IMPRINT",FACE,{"disambiguationData":[TD([[makeQuery(id+"F6.imprint","IMPRINT",EDGE,{"derivedFrom":sQuery(id+"F6.wireOp",EDGE,"E42.13.0.8")}),1.0]])]});
            var Q505;
            Q505=makeQuery(id+"F6.imprint","IMPRINT",FACE,{"disambiguationData":[TD([[makeQuery(id+"F6.imprint","IMPRINT",EDGE,{"derivedFrom":sQuery(id+"F6.wireOp",EDGE,"E42.12.0.17")}),1.0]])]});
            var Q506;
            Q506=makeQuery(id+"F6.imprint","IMPRINT",FACE,{"disambiguationData":[TD([[makeQuery(id+"F6.imprint","IMPRINT",EDGE,{"derivedFrom":sQuery(id+"F6.wireOp",EDGE,"E42.17.0.8")}),1.0]])]});
            var Q507;
            Q507=makeQuery(id+"F6.imprint","IMPRINT",FACE,{"disambiguationData":[TD([[makeQuery(id+"F6.imprint","IMPRINT",EDGE,{"derivedFrom":sQuery(id+"F6.wireOp",EDGE,"E42.16.0.17")}),1.0]])]});
            var Q508;
            Q508=makeQuery(id+"F6.imprint","IMPRINT",FACE,{"disambiguationData":[TD([[makeQuery(id+"F6.imprint","IMPRINT",EDGE,{"derivedFrom":sQuery(id+"F6.wireOp",EDGE,"E42.15.0.8")}),1.0]])]});
            var Q509;
            Q509=makeQuery(id+"F6.imprint","IMPRINT",FACE,{"disambiguationData":[TD([[makeQuery(id+"F6.imprint","IMPRINT",EDGE,{"derivedFrom":sQuery(id+"F6.wireOp",EDGE,"E42.18.0.17")}),1.0]])]});
            var Q510;
            Q510=makeQuery(id+"F6.imprint","IMPRINT",FACE,{"disambiguationData":[TD([[makeQuery(id+"F6.imprint","IMPRINT",EDGE,{"derivedFrom":sQuery(id+"F6.wireOp",EDGE,"E743.MirrorC")}),-1.0]])]});
            var Q511;
            Q511=makeQuery(id+"F6.imprint","IMPRINT",FACE,{"disambiguationData":[TD([[makeQuery(id+"F6.imprint","IMPRINT",EDGE,{"derivedFrom":sQuery(id+"F6.wireOp",EDGE,"E42.21.0.8")}),1.0]])]});
            var Q512;
            Q512=makeQuery(id+"F6.imprint","IMPRINT",FACE,{"disambiguationData":[TD([[makeQuery(id+"F6.imprint","IMPRINT",EDGE,{"derivedFrom":sQuery(id+"F6.wireOp",EDGE,"E42.20.0.17")}),1.0]])]});
            var Q513;
            Q513=makeQuery(id+"F6.imprint","IMPRINT",FACE,{"disambiguationData":[TD([[makeQuery(id+"F6.imprint","IMPRINT",EDGE,{"derivedFrom":sQuery(id+"F6.wireOp",EDGE,"E42.19.0.8")}),1.0]])]});
            var Q514;
            Q514=makeQuery(id+"F6.imprint","IMPRINT",FACE,{"disambiguationData":[TD([[makeQuery(id+"F6.imprint","IMPRINT",EDGE,{"derivedFrom":sQuery(id+"F6.wireOp",EDGE,"E590.MirrorC")}),-1.0]])]});
            var Q515;
            Q515=makeQuery(id+"F6.imprint","IMPRINT",FACE,{"disambiguationData":[TD([[makeQuery(id+"F6.imprint","IMPRINT",EDGE,{"derivedFrom":sQuery(id+"F6.wireOp",EDGE,"E42.23.0.8")}),1.0]])]});
            var Q516;
            Q516=makeQuery(id+"F6.imprint","IMPRINT",FACE,{"disambiguationData":[TD([[makeQuery(id+"F6.imprint","IMPRINT",EDGE,{"derivedFrom":sQuery(id+"F6.wireOp",EDGE,"E42.22.0.17")}),1.0]])]});
            var Q517;
            Q517=makeQuery(id+"F6.imprint","IMPRINT",FACE,{"disambiguationData":[TD([[makeQuery(id+"F6.imprint","IMPRINT",EDGE,{"derivedFrom":sQuery(id+"F6.wireOp",EDGE,"E42.26.0.17")}),1.0]])]});
            var Q518;
            Q518=makeQuery(id+"F6.imprint","IMPRINT",FACE,{"disambiguationData":[TD([[makeQuery(id+"F6.imprint","IMPRINT",EDGE,{"derivedFrom":sQuery(id+"F6.wireOp",EDGE,"E42.25.0.8")}),1.0]])]});
            var Q519;
            Q519=makeQuery(id+"F6.imprint","IMPRINT",FACE,{"disambiguationData":[TD([[makeQuery(id+"F6.imprint","IMPRINT",EDGE,{"derivedFrom":sQuery(id+"F6.wireOp",EDGE,"E42.24.0.17")}),1.0]])]});
            var Q520;
            Q520=makeQuery(id+"F6.imprint","IMPRINT",FACE,{"disambiguationData":[TD([[makeQuery(id+"F6.imprint","IMPRINT",EDGE,{"derivedFrom":sQuery(id+"F6.wireOp",EDGE,"E733.MirrorC")}),-1.0]])]});
            var Q521;
            Q521=makeQuery(id+"F6.imprint","IMPRINT",FACE,{"disambiguationData":[TD([[makeQuery(id+"F6.imprint","IMPRINT",EDGE,{"derivedFrom":sQuery(id+"F6.wireOp",EDGE,"E890.MirrorC")}),-1.0]])]});
            var Q522;
            Q522=makeQuery(id+"F6.imprint","IMPRINT",FACE,{"disambiguationData":[TD([[makeQuery(id+"F6.imprint","IMPRINT",EDGE,{"derivedFrom":sQuery(id+"F6.wireOp",EDGE,"E543.MirrorC")}),-1.0]])]});
            var Q523;
            Q523=makeQuery(id+"F6.imprint","IMPRINT",FACE,{"disambiguationData":[TD([[makeQuery(id+"F6.imprint","IMPRINT",EDGE,{"derivedFrom":sQuery(id+"F6.wireOp",EDGE,"E558.MirrorC")}),-1.0]])]});
            var Q524;
            Q524=makeQuery(id+"F6.imprint","IMPRINT",FACE,{"disambiguationData":[TD([[makeQuery(id+"F6.imprint","IMPRINT",EDGE,{"derivedFrom":sQuery(id+"F6.wireOp",EDGE,"E789.MirrorC")}),-1.0]])]});
            var Q525;
            Q525=makeQuery(id+"F6.imprint","IMPRINT",FACE,{"disambiguationData":[TD([[makeQuery(id+"F6.imprint","IMPRINT",EDGE,{"derivedFrom":sQuery(id+"F6.wireOp",EDGE,"E736.MirrorC")}),-1.0]])]});
            var Q526;
            Q526=makeQuery(id+"F6.imprint","IMPRINT",FACE,{"disambiguationData":[TD([[makeQuery(id+"F6.imprint","IMPRINT",EDGE,{"derivedFrom":sQuery(id+"F6.wireOp",EDGE,"E634.MirrorC")}),-1.0]])]});
            var Q527;
            Q527=makeQuery(id+"F6.imprint","IMPRINT",FACE,{"disambiguationData":[TD([[makeQuery(id+"F6.imprint","IMPRINT",EDGE,{"derivedFrom":sQuery(id+"F6.wireOp",EDGE,"E749.MirrorC")}),-1.0]])]});
            var Q528;
            Q528=makeQuery(id+"F6.imprint","IMPRINT",FACE,{"disambiguationData":[TD([[makeQuery(id+"F6.imprint","IMPRINT",EDGE,{"derivedFrom":sQuery(id+"F6.wireOp",EDGE,"E819.MirrorC")}),-1.0]])]});
            var Q529;
            Q529=makeQuery(id+"F6.imprint","IMPRINT",FACE,{"disambiguationData":[TD([[makeQuery(id+"F6.imprint","IMPRINT",EDGE,{"derivedFrom":sQuery(id+"F6.wireOp",EDGE,"E752.MirrorC")}),-1.0]])]});
            var Q530;
            Q530=makeQuery(id+"F6.imprint","IMPRINT",FACE,{"disambiguationData":[TD([[makeQuery(id+"F6.imprint","IMPRINT",EDGE,{"derivedFrom":sQuery(id+"F6.wireOp",EDGE,"E804.MirrorC")}),-1.0]])]});
            var Q531;
            Q531=makeQuery(id+"F6.imprint","IMPRINT",FACE,{"disambiguationData":[TD([[makeQuery(id+"F6.imprint","IMPRINT",EDGE,{"derivedFrom":sQuery(id+"F6.wireOp",EDGE,"E649.MirrorC")}),-1.0]])]});
            var Q532;
            Q532=makeQuery(id+"F6.imprint","IMPRINT",FACE,{"disambiguationData":[TD([[makeQuery(id+"F6.imprint","IMPRINT",EDGE,{"derivedFrom":sQuery(id+"F6.wireOp",EDGE,"E758.MirrorC")}),-1.0]])]});
            var Q533;
            Q533=makeQuery(id+"F6.imprint","IMPRINT",FACE,{"disambiguationData":[TD([[makeQuery(id+"F6.imprint","IMPRINT",EDGE,{"derivedFrom":sQuery(id+"F6.wireOp",EDGE,"E604.MirrorC")}),-1.0]])]});
            var Q534;
            Q534=makeQuery(id+"F6.imprint","IMPRINT",FACE,{"disambiguationData":[TD([[makeQuery(id+"F6.imprint","IMPRINT",EDGE,{"derivedFrom":sQuery(id+"F6.wireOp",EDGE,"E774.MirrorC")}),-1.0]])]});
            var Q535;
            Q535=makeQuery(id+"F6.imprint","IMPRINT",FACE,{"disambiguationData":[TD([[makeQuery(id+"F6.imprint","IMPRINT",EDGE,{"derivedFrom":sQuery(id+"F6.wireOp",EDGE,"E619.MirrorC")}),-1.0]])]});
            var Q536;
            Q536=makeQuery(id+"F6.imprint","IMPRINT",FACE,{"disambiguationData":[TD([[makeQuery(id+"F6.imprint","IMPRINT",EDGE,{"derivedFrom":sQuery(id+"F6.wireOp",EDGE,"E812.MirrorC")}),-1.0]])]});
            var Q537;
            Q537=makeQuery(id+"F6.imprint","IMPRINT",FACE,{"disambiguationData":[TD([[makeQuery(id+"F6.imprint","IMPRINT",EDGE,{"derivedFrom":sQuery(id+"F6.wireOp",EDGE,"E864.MirrorC")}),-1.0]])]});
            var Q538;
            Q538=makeQuery(id+"F6.imprint","IMPRINT",FACE,{"disambiguationData":[TD([[makeQuery(id+"F6.imprint","IMPRINT",EDGE,{"derivedFrom":sQuery(id+"F6.wireOp",EDGE,"E695.MirrorC")}),-1.0]])]});
            var Q539;
            Q539=makeQuery(id+"F6.imprint","IMPRINT",FACE,{"disambiguationData":[TD([[makeQuery(id+"F6.imprint","IMPRINT",EDGE,{"derivedFrom":sQuery(id+"F6.wireOp",EDGE,"E794.MirrorC")}),-1.0]])]});
            var Q540;
            Q540=makeQuery(id+"F6.imprint","IMPRINT",FACE,{"disambiguationData":[TD([[makeQuery(id+"F6.imprint","IMPRINT",EDGE,{"derivedFrom":sQuery(id+"F6.wireOp",EDGE,"E827.MirrorC")}),-1.0]])]});
            var Q541;
            Q541=makeQuery(id+"F6.imprint","IMPRINT",FACE,{"disambiguationData":[TD([[makeQuery(id+"F6.imprint","IMPRINT",EDGE,{"derivedFrom":sQuery(id+"F6.wireOp",EDGE,"E879.MirrorC")}),-1.0]])]});
            var Q542;
            Q542=makeQuery(id+"F6.imprint","IMPRINT",FACE,{"disambiguationData":[TD([[makeQuery(id+"F6.imprint","IMPRINT",EDGE,{"derivedFrom":sQuery(id+"F6.wireOp",EDGE,"E710.MirrorC")}),-1.0]])]});
            var Q543;
            Q543=makeQuery(id+"F6.imprint","IMPRINT",FACE,{"disambiguationData":[TD([[makeQuery(id+"F6.imprint","IMPRINT",EDGE,{"derivedFrom":sQuery(id+"F6.wireOp",EDGE,"E810.MirrorC")}),-1.0]])]});
            var Q544;
            Q544=makeQuery(id+"F6.imprint","IMPRINT",FACE,{"disambiguationData":[TD([[makeQuery(id+"F6.imprint","IMPRINT",EDGE,{"derivedFrom":sQuery(id+"F6.wireOp",EDGE,"E764.MirrorC")}),-1.0]])]});
            var Q545;
            Q545=makeQuery(id+"F6.imprint","IMPRINT",FACE,{"disambiguationData":[TD([[makeQuery(id+"F6.imprint","IMPRINT",EDGE,{"derivedFrom":sQuery(id+"F6.wireOp",EDGE,"E782.MirrorC")}),-1.0]])]});
            var Q546;
            Q546=makeQuery(id+"F6.imprint","IMPRINT",FACE,{"disambiguationData":[TD([[makeQuery(id+"F6.imprint","IMPRINT",EDGE,{"derivedFrom":sQuery(id+"F6.wireOp",EDGE,"E833.MirrorC")}),-1.0]])]});
            var Q547;
            Q547=makeQuery(id+"F6.imprint","IMPRINT",FACE,{"disambiguationData":[TD([[makeQuery(id+"F6.imprint","IMPRINT",EDGE,{"derivedFrom":sQuery(id+"F6.wireOp",EDGE,"E309.MirrorC")}),-1.0]])]});
            var Q548;
            Q548=makeQuery(id+"F6.imprint","IMPRINT",FACE,{"disambiguationData":[TD([[makeQuery(id+"F6.imprint","IMPRINT",EDGE,{"derivedFrom":sQuery(id+"F6.wireOp",EDGE,"E324.MirrorC")}),-1.0]])]});
            var Q549;
            Q549=makeQuery(id+"F6.imprint","IMPRINT",FACE,{"disambiguationData":[TD([[makeQuery(id+"F6.imprint","IMPRINT",EDGE,{"derivedFrom":sQuery(id+"F6.wireOp",EDGE,"E664.MirrorC")}),-1.0]])]});
            var Q550;
            Q550=makeQuery(id+"F6.imprint","IMPRINT",FACE,{"disambiguationData":[TD([[makeQuery(id+"F6.imprint","IMPRINT",EDGE,{"derivedFrom":sQuery(id+"F6.wireOp",EDGE,"E767.MirrorC")}),-1.0]])]});
            var Q551;
            Q551=makeQuery(id+"F6.imprint","IMPRINT",FACE,{"disambiguationData":[TD([[makeQuery(id+"F6.imprint","IMPRINT",EDGE,{"derivedFrom":sQuery(id+"F6.wireOp",EDGE,"E261.MirrorC")}),-1.0]])]});
            var Q552;
            Q552=makeQuery(id+"F6.imprint","IMPRINT",FACE,{"disambiguationData":[TD([[makeQuery(id+"F6.imprint","IMPRINT",EDGE,{"derivedFrom":sQuery(id+"F6.wireOp",EDGE,"E248.MirrorC")}),-1.0]])]});
            var Q553;
            Q553=makeQuery(id+"F6.imprint","IMPRINT",FACE,{"disambiguationData":[TD([[makeQuery(id+"F6.imprint","IMPRINT",EDGE,{"derivedFrom":sQuery(id+"F6.wireOp",EDGE,"E293.MirrorC")}),-1.0]])]});
            var Q554;
            Q554=makeQuery(id+"F6.imprint","IMPRINT",FACE,{"disambiguationData":[TD([[makeQuery(id+"F6.imprint","IMPRINT",EDGE,{"derivedFrom":sQuery(id+"F6.wireOp",EDGE,"E277.MirrorC")}),-1.0]])]});
            var Q555;
            Q555=makeQuery(id+"F6.imprint","IMPRINT",FACE,{"disambiguationData":[TD([[makeQuery(id+"F6.imprint","IMPRINT",EDGE,{"derivedFrom":sQuery(id+"F6.wireOp",EDGE,"E849.MirrorC")}),-1.0]])]});
            var Q556;
            Q556=makeQuery(id+"F6.imprint","IMPRINT",FACE,{"disambiguationData":[TD([[makeQuery(id+"F6.imprint","IMPRINT",EDGE,{"derivedFrom":sQuery(id+"F6.wireOp",EDGE,"E797.MirrorC")}),-1.0]])]});
            var Q557;
            Q557=makeQuery(id+"F6.imprint","IMPRINT",FACE,{"disambiguationData":[TD([[makeQuery(id+"F6.imprint","IMPRINT",EDGE,{"derivedFrom":sQuery(id+"F6.wireOp",EDGE,"E680.MirrorC")}),-1.0]])]});
            var Q558;
            Q558=makeQuery(id+"F6.imprint","IMPRINT",FACE,{"disambiguationData":[TD([[makeQuery(id+"F6.imprint","IMPRINT",EDGE,{"derivedFrom":sQuery(id+"F6.wireOp",EDGE,"E779.MirrorC")}),-1.0]])]});
            var Q559;
            Q559=makeQuery(id+"F6.imprint","IMPRINT",FACE,{"disambiguationData":[TD([[makeQuery(id+"F6.imprint","IMPRINT",EDGE,{"derivedFrom":sQuery(id+"F6.wireOp",EDGE,"E42.18.0.19")}),1.0]])]});
            var Q560;
            Q560=makeQuery(id+"F6.imprint","IMPRINT",FACE,{"disambiguationData":[TD([[makeQuery(id+"F6.imprint","IMPRINT",EDGE,{"derivedFrom":sQuery(id+"F6.wireOp",EDGE,"E42.18.0.1")}),1.0]])]});
            var Q561;
            Q561=makeQuery(id+"F6.imprint","IMPRINT",FACE,{"disambiguationData":[TD([[makeQuery(id+"F6.imprint","IMPRINT",EDGE,{"derivedFrom":sQuery(id+"F6.wireOp",EDGE,"E42.17.0.10")}),1.0]])]});
            var Q562;
            Q562=makeQuery(id+"F6.imprint","IMPRINT",FACE,{"disambiguationData":[TD([[makeQuery(id+"F6.imprint","IMPRINT",EDGE,{"derivedFrom":sQuery(id+"F6.wireOp",EDGE,"E42.21.0.10")}),1.0]])]});
            var Q563;
            Q563=makeQuery(id+"F6.imprint","IMPRINT",FACE,{"disambiguationData":[TD([[makeQuery(id+"F6.imprint","IMPRINT",EDGE,{"derivedFrom":sQuery(id+"F6.wireOp",EDGE,"E42.20.0.19")}),1.0]])]});
            var Q564;
            Q564=makeQuery(id+"F6.imprint","IMPRINT",FACE,{"disambiguationData":[TD([[makeQuery(id+"F6.imprint","IMPRINT",EDGE,{"derivedFrom":sQuery(id+"F6.wireOp",EDGE,"E42.20.0.1")}),1.0]])]});
            var Q565;
            Q565=makeQuery(id+"F6.imprint","IMPRINT",FACE,{"disambiguationData":[TD([[makeQuery(id+"F6.imprint","IMPRINT",EDGE,{"derivedFrom":sQuery(id+"F6.wireOp",EDGE,"E42.19.0.10")}),1.0]])]});
            var Q566;
            Q566=makeQuery(id+"F6.imprint","IMPRINT",FACE,{"disambiguationData":[TD([[makeQuery(id+"F6.imprint","IMPRINT",EDGE,{"derivedFrom":sQuery(id+"F6.wireOp",EDGE,"E42.24.0.1")}),1.0]])]});
            var Q567;
            Q567=makeQuery(id+"F6.imprint","IMPRINT",FACE,{"disambiguationData":[TD([[makeQuery(id+"F6.imprint","IMPRINT",EDGE,{"derivedFrom":sQuery(id+"F6.wireOp",EDGE,"E42.23.0.10")}),1.0]])]});
            var Q568;
            Q568=makeQuery(id+"F6.imprint","IMPRINT",FACE,{"disambiguationData":[TD([[makeQuery(id+"F6.imprint","IMPRINT",EDGE,{"derivedFrom":sQuery(id+"F6.wireOp",EDGE,"E42.22.0.19")}),1.0]])]});
            var Q569;
            Q569=makeQuery(id+"F6.imprint","IMPRINT",FACE,{"disambiguationData":[TD([[makeQuery(id+"F6.imprint","IMPRINT",EDGE,{"derivedFrom":sQuery(id+"F6.wireOp",EDGE,"E42.22.0.1")}),1.0]])]});
            var Q570;
            Q570=makeQuery(id+"F6.imprint","IMPRINT",FACE,{"disambiguationData":[TD([[makeQuery(id+"F6.imprint","IMPRINT",EDGE,{"derivedFrom":sQuery(id+"F6.wireOp",EDGE,"E42.26.0.19")}),1.0]])]});
            var Q571;
            Q571=makeQuery(id+"F6.imprint","IMPRINT",FACE,{"disambiguationData":[TD([[makeQuery(id+"F6.imprint","IMPRINT",EDGE,{"derivedFrom":sQuery(id+"F6.wireOp",EDGE,"E42.26.0.1")}),1.0]])]});
            var Q572;
            Q572=makeQuery(id+"F6.imprint","IMPRINT",FACE,{"disambiguationData":[TD([[makeQuery(id+"F6.imprint","IMPRINT",EDGE,{"derivedFrom":sQuery(id+"F6.wireOp",EDGE,"E42.25.0.10")}),1.0]])]});
            var Q573;
            Q573=makeQuery(id+"F6.imprint","IMPRINT",FACE,{"disambiguationData":[TD([[makeQuery(id+"F6.imprint","IMPRINT",EDGE,{"derivedFrom":sQuery(id+"F6.wireOp",EDGE,"E42.24.0.19")}),1.0]])]});
            var Q574;
            Q574=makeQuery(id+"F6.imprint","IMPRINT",FACE,{"disambiguationData":[TD([[makeQuery(id+"F6.imprint","IMPRINT",EDGE,{"derivedFrom":sQuery(id+"F6.wireOp",EDGE,"E42.29.0.10")}),1.0]])]});
            var Q575;
            Q575=makeQuery(id+"F6.imprint","IMPRINT",FACE,{"disambiguationData":[TD([[makeQuery(id+"F6.imprint","IMPRINT",EDGE,{"derivedFrom":sQuery(id+"F6.wireOp",EDGE,"E42.28.0.19")}),1.0]])]});
            var Q576;
            Q576=makeQuery(id+"F6.imprint","IMPRINT",FACE,{"disambiguationData":[TD([[makeQuery(id+"F6.imprint","IMPRINT",EDGE,{"derivedFrom":sQuery(id+"F6.wireOp",EDGE,"E42.28.0.1")}),1.0]])]});
            var Q577;
            Q577=makeQuery(id+"F6.imprint","IMPRINT",FACE,{"disambiguationData":[TD([[makeQuery(id+"F6.imprint","IMPRINT",EDGE,{"derivedFrom":sQuery(id+"F6.wireOp",EDGE,"E42.27.0.10")}),1.0]])]});
            var Q578;
            Q578=makeQuery(id+"F6.imprint","IMPRINT",FACE,{"disambiguationData":[TD([[makeQuery(id+"F6.imprint","IMPRINT",EDGE,{"derivedFrom":sQuery(id+"F6.wireOp",EDGE,"E42.32.0.1")}),1.0]])]});
            var Q579;
            Q579=makeQuery(id+"F6.imprint","IMPRINT",FACE,{"disambiguationData":[TD([[makeQuery(id+"F6.imprint","IMPRINT",EDGE,{"derivedFrom":sQuery(id+"F6.wireOp",EDGE,"E42.31.0.10")}),1.0]])]});
            var Q580;
            Q580=makeQuery(id+"F6.imprint","IMPRINT",FACE,{"disambiguationData":[TD([[makeQuery(id+"F6.imprint","IMPRINT",EDGE,{"derivedFrom":sQuery(id+"F6.wireOp",EDGE,"E42.30.0.19")}),1.0]])]});
            var Q581;
            Q581=makeQuery(id+"F6.imprint","IMPRINT",FACE,{"disambiguationData":[TD([[makeQuery(id+"F6.imprint","IMPRINT",EDGE,{"derivedFrom":sQuery(id+"F6.wireOp",EDGE,"E42.30.0.1")}),1.0]])]});
            var Q582;
            Q582=makeQuery(id+"F6.imprint","IMPRINT",FACE,{"disambiguationData":[TD([[makeQuery(id+"F6.imprint","IMPRINT",EDGE,{"derivedFrom":sQuery(id+"F6.wireOp",EDGE,"E503.MirrorC")}),-1.0]])]});
            var Q583;
            Q583=makeQuery(id+"F6.imprint","IMPRINT",FACE,{"disambiguationData":[TD([[makeQuery(id+"F6.imprint","IMPRINT",EDGE,{"derivedFrom":sQuery(id+"F6.wireOp",EDGE,"E450.MirrorC")}),-1.0]])]});
            var Q584;
            Q584=makeQuery(id+"F6.imprint","IMPRINT",FACE,{"disambiguationData":[TD([[makeQuery(id+"F6.imprint","IMPRINT",EDGE,{"derivedFrom":sQuery(id+"F6.wireOp",EDGE,"E42.32.0.19")}),1.0]])]});
            var Q585;
            Q585=makeQuery(id+"F6.imprint","IMPRINT",FACE,{"disambiguationData":[TD([[makeQuery(id+"F6.imprint","IMPRINT",EDGE,{"derivedFrom":sQuery(id+"F6.wireOp",EDGE,"E42.1.0.10")}),1.0]])]});
            var Q586;
            Q586=makeQuery(id+"F6.imprint","IMPRINT",FACE,{"disambiguationData":[TD([[makeQuery(id+"F6.imprint","IMPRINT",EDGE,{"derivedFrom":sQuery(id+"F6.wireOp",EDGE,"E41.0.4.0")}),1.0]])]});
            var Q587;
            Q587=makeQuery(id+"F6.imprint","IMPRINT",FACE,{"disambiguationData":[TD([[makeQuery(id+"F6.imprint","IMPRINT",EDGE,{"derivedFrom":sQuery(id+"F6.wireOp",EDGE,"E42.4.0.1")}),1.0]])]});
            var Q588;
            Q588=makeQuery(id+"F6.imprint","IMPRINT",FACE,{"disambiguationData":[TD([[makeQuery(id+"F6.imprint","IMPRINT",EDGE,{"derivedFrom":sQuery(id+"F6.wireOp",EDGE,"E42.3.0.10")}),1.0]])]});
            var Q589;
            Q589=makeQuery(id+"F6.imprint","IMPRINT",FACE,{"disambiguationData":[TD([[makeQuery(id+"F6.imprint","IMPRINT",EDGE,{"derivedFrom":sQuery(id+"F6.wireOp",EDGE,"E42.2.0.19")}),1.0]])]});
            var Q590;
            Q590=makeQuery(id+"F6.imprint","IMPRINT",FACE,{"disambiguationData":[TD([[makeQuery(id+"F6.imprint","IMPRINT",EDGE,{"derivedFrom":sQuery(id+"F6.wireOp",EDGE,"E42.2.0.1")}),1.0]])]});
            var Q591;
            Q591=makeQuery(id+"F6.imprint","IMPRINT",FACE,{"disambiguationData":[TD([[makeQuery(id+"F6.imprint","IMPRINT",EDGE,{"derivedFrom":sQuery(id+"F6.wireOp",EDGE,"E42.6.0.19")}),1.0]])]});
            var Q592;
            Q592=makeQuery(id+"F6.imprint","IMPRINT",FACE,{"disambiguationData":[TD([[makeQuery(id+"F6.imprint","IMPRINT",EDGE,{"derivedFrom":sQuery(id+"F6.wireOp",EDGE,"E42.6.0.1")}),1.0]])]});
            var Q593;
            Q593=makeQuery(id+"F6.imprint","IMPRINT",FACE,{"disambiguationData":[TD([[makeQuery(id+"F6.imprint","IMPRINT",EDGE,{"derivedFrom":sQuery(id+"F6.wireOp",EDGE,"E42.5.0.10")}),1.0]])]});
            var Q594;
            Q594=makeQuery(id+"F6.imprint","IMPRINT",FACE,{"disambiguationData":[TD([[makeQuery(id+"F6.imprint","IMPRINT",EDGE,{"derivedFrom":sQuery(id+"F6.wireOp",EDGE,"E42.4.0.19")}),1.0]])]});
            var Q595;
            Q595=makeQuery(id+"F6.imprint","IMPRINT",FACE,{"disambiguationData":[TD([[makeQuery(id+"F6.imprint","IMPRINT",EDGE,{"derivedFrom":sQuery(id+"F6.wireOp",EDGE,"E42.9.0.10")}),1.0]])]});
            var Q596;
            Q596=makeQuery(id+"F6.imprint","IMPRINT",FACE,{"disambiguationData":[TD([[makeQuery(id+"F6.imprint","IMPRINT",EDGE,{"derivedFrom":sQuery(id+"F6.wireOp",EDGE,"E42.8.0.19")}),1.0]])]});
            var Q597;
            Q597=makeQuery(id+"F6.imprint","IMPRINT",FACE,{"disambiguationData":[TD([[makeQuery(id+"F6.imprint","IMPRINT",EDGE,{"derivedFrom":sQuery(id+"F6.wireOp",EDGE,"E42.8.0.1")}),1.0]])]});
            var Q598;
            Q598=makeQuery(id+"F6.imprint","IMPRINT",FACE,{"disambiguationData":[TD([[makeQuery(id+"F6.imprint","IMPRINT",EDGE,{"derivedFrom":sQuery(id+"F6.wireOp",EDGE,"E42.7.0.10")}),1.0]])]});
            var Q599;
            Q599=makeQuery(id+"F6.imprint","IMPRINT",FACE,{"disambiguationData":[TD([[makeQuery(id+"F6.imprint","IMPRINT",EDGE,{"derivedFrom":sQuery(id+"F6.wireOp",EDGE,"E42.12.0.1")}),1.0]])]});
            var Q600;
            Q600=makeQuery(id+"F6.imprint","IMPRINT",FACE,{"disambiguationData":[TD([[makeQuery(id+"F6.imprint","IMPRINT",EDGE,{"derivedFrom":sQuery(id+"F6.wireOp",EDGE,"E42.11.0.10")}),1.0]])]});
            var Q601;
            Q601=makeQuery(id+"F6.imprint","IMPRINT",FACE,{"disambiguationData":[TD([[makeQuery(id+"F6.imprint","IMPRINT",EDGE,{"derivedFrom":sQuery(id+"F6.wireOp",EDGE,"E42.10.0.19")}),1.0]])]});
            var Q602;
            Q602=makeQuery(id+"F6.imprint","IMPRINT",FACE,{"disambiguationData":[TD([[makeQuery(id+"F6.imprint","IMPRINT",EDGE,{"derivedFrom":sQuery(id+"F6.wireOp",EDGE,"E42.10.0.1")}),1.0]])]});
            var Q603;
            Q603=makeQuery(id+"F6.imprint","IMPRINT",FACE,{"disambiguationData":[TD([[makeQuery(id+"F6.imprint","IMPRINT",EDGE,{"derivedFrom":sQuery(id+"F6.wireOp",EDGE,"E42.14.0.19")}),1.0]])]});
            var Q604;
            Q604=makeQuery(id+"F6.imprint","IMPRINT",FACE,{"disambiguationData":[TD([[makeQuery(id+"F6.imprint","IMPRINT",EDGE,{"derivedFrom":sQuery(id+"F6.wireOp",EDGE,"E42.14.0.1")}),1.0]])]});
            var Q605;
            Q605=makeQuery(id+"F6.imprint","IMPRINT",FACE,{"disambiguationData":[TD([[makeQuery(id+"F6.imprint","IMPRINT",EDGE,{"derivedFrom":sQuery(id+"F6.wireOp",EDGE,"E42.13.0.10")}),1.0]])]});
            var Q606;
            Q606=makeQuery(id+"F6.imprint","IMPRINT",FACE,{"disambiguationData":[TD([[makeQuery(id+"F6.imprint","IMPRINT",EDGE,{"derivedFrom":sQuery(id+"F6.wireOp",EDGE,"E42.12.0.19")}),1.0]])]});
            var Q607;
            Q607=makeQuery(id+"F6.imprint","IMPRINT",FACE,{"disambiguationData":[TD([[makeQuery(id+"F6.imprint","IMPRINT",EDGE,{"derivedFrom":sQuery(id+"F6.wireOp",EDGE,"E42.16.0.19")}),1.0]])]});
            var Q608;
            Q608=makeQuery(id+"F6.imprint","IMPRINT",FACE,{"disambiguationData":[TD([[makeQuery(id+"F6.imprint","IMPRINT",EDGE,{"derivedFrom":sQuery(id+"F6.wireOp",EDGE,"E42.16.0.1")}),1.0]])]});
            var Q609;
            Q609=makeQuery(id+"F6.imprint","IMPRINT",FACE,{"disambiguationData":[TD([[makeQuery(id+"F6.imprint","IMPRINT",EDGE,{"derivedFrom":sQuery(id+"F6.wireOp",EDGE,"E466.MirrorC")}),-1.0]])]});
            var Q610;
            Q610=makeQuery(id+"F6.imprint","IMPRINT",FACE,{"disambiguationData":[TD([[makeQuery(id+"F6.imprint","IMPRINT",EDGE,{"derivedFrom":sQuery(id+"F6.wireOp",EDGE,"E42.15.0.10")}),1.0]])]});
            var Q611;
            Q611=makeQuery(id+"F6.imprint","IMPRINT",FACE,{"disambiguationData":[TD([[makeQuery(id+"F6.imprint","IMPRINT",EDGE,{"derivedFrom":sQuery(id+"F6.wireOp",EDGE,"E518.MirrorC")}),-1.0]])]});
            var Q612;
            Q612=makeQuery(id+"F6.imprint","IMPRINT",FACE,{"disambiguationData":[TD([[makeQuery(id+"F6.imprint","IMPRINT",EDGE,{"derivedFrom":sQuery(id+"F6.wireOp",EDGE,"E310.MirrorC")}),-1.0]])]});
            var Q613;
            Q613=makeQuery(id+"F6.imprint","IMPRINT",FACE,{"disambiguationData":[TD([[makeQuery(id+"F6.imprint","IMPRINT",EDGE,{"derivedFrom":sQuery(id+"F6.wireOp",EDGE,"E325.MirrorC")}),-1.0]])]});
            var Q614;
            Q614=makeQuery(id+"F6.imprint","IMPRINT",FACE,{"disambiguationData":[TD([[makeQuery(id+"F6.imprint","IMPRINT",EDGE,{"derivedFrom":sQuery(id+"F6.wireOp",EDGE,"E262.MirrorC")}),-1.0]])]});
            var Q615;
            Q615=makeQuery(id+"F6.imprint","IMPRINT",FACE,{"disambiguationData":[TD([[makeQuery(id+"F6.imprint","IMPRINT",EDGE,{"derivedFrom":sQuery(id+"F6.wireOp",EDGE,"E249.MirrorC")}),-1.0]])]});
            var Q616;
            Q616=makeQuery(id+"F6.imprint","IMPRINT",FACE,{"disambiguationData":[TD([[makeQuery(id+"F6.imprint","IMPRINT",EDGE,{"derivedFrom":sQuery(id+"F6.wireOp",EDGE,"E419.MirrorC")}),-1.0]])]});
            var Q617;
            Q617=makeQuery(id+"F6.imprint","IMPRINT",FACE,{"disambiguationData":[TD([[makeQuery(id+"F6.imprint","IMPRINT",EDGE,{"derivedFrom":sQuery(id+"F6.wireOp",EDGE,"E472.MirrorC")}),-1.0]])]});
            var Q618;
            Q618=makeQuery(id+"F6.imprint","IMPRINT",FACE,{"disambiguationData":[TD([[makeQuery(id+"F6.imprint","IMPRINT",EDGE,{"derivedFrom":sQuery(id+"F6.wireOp",EDGE,"E294.MirrorC")}),-1.0]])]});
            var Q619;
            Q619=makeQuery(id+"F6.imprint","IMPRINT",FACE,{"disambiguationData":[TD([[makeQuery(id+"F6.imprint","IMPRINT",EDGE,{"derivedFrom":sQuery(id+"F6.wireOp",EDGE,"E278.MirrorC")}),-1.0]])]});
            var Q620;
            Q620=makeQuery(id+"F6.imprint","IMPRINT",FACE,{"disambiguationData":[TD([[makeQuery(id+"F6.imprint","IMPRINT",EDGE,{"derivedFrom":sQuery(id+"F6.wireOp",EDGE,"E435.MirrorC")}),-1.0]])]});
            var Q621;
            Q621=makeQuery(id+"F6.imprint","IMPRINT",FACE,{"disambiguationData":[TD([[makeQuery(id+"F6.imprint","IMPRINT",EDGE,{"derivedFrom":sQuery(id+"F6.wireOp",EDGE,"E488.MirrorC")}),-1.0]])]});
            var Q622;
            Q622=makeQuery(id+"F6.imprint","IMPRINT",FACE,{"disambiguationData":[TD([[makeQuery(id+"F6.imprint","IMPRINT",EDGE,{"derivedFrom":sQuery(id+"F6.wireOp",EDGE,"E42.18.0.20")}),1.0]])]});
            var Q623;
            Q623=makeQuery(id+"F6.imprint","IMPRINT",FACE,{"disambiguationData":[TD([[makeQuery(id+"F6.imprint","IMPRINT",EDGE,{"derivedFrom":sQuery(id+"F6.wireOp",EDGE,"E42.18.0.2")}),1.0]])]});
            var Q624;
            Q624=makeQuery(id+"F6.imprint","IMPRINT",FACE,{"disambiguationData":[TD([[makeQuery(id+"F6.imprint","IMPRINT",EDGE,{"derivedFrom":sQuery(id+"F6.wireOp",EDGE,"E42.17.0.12")}),1.0]])]});
            var Q625;
            Q625=makeQuery(id+"F6.imprint","IMPRINT",FACE,{"disambiguationData":[TD([[makeQuery(id+"F6.imprint","IMPRINT",EDGE,{"derivedFrom":sQuery(id+"F6.wireOp",EDGE,"E42.21.0.12")}),1.0]])]});
            var Q626;
            Q626=makeQuery(id+"F6.imprint","IMPRINT",FACE,{"disambiguationData":[TD([[makeQuery(id+"F6.imprint","IMPRINT",EDGE,{"derivedFrom":sQuery(id+"F6.wireOp",EDGE,"E42.20.0.20")}),1.0]])]});
            var Q627;
            Q627=makeQuery(id+"F6.imprint","IMPRINT",FACE,{"disambiguationData":[TD([[makeQuery(id+"F6.imprint","IMPRINT",EDGE,{"derivedFrom":sQuery(id+"F6.wireOp",EDGE,"E42.20.0.2")}),1.0]])]});
            var Q628;
            Q628=makeQuery(id+"F6.imprint","IMPRINT",FACE,{"disambiguationData":[TD([[makeQuery(id+"F6.imprint","IMPRINT",EDGE,{"derivedFrom":sQuery(id+"F6.wireOp",EDGE,"E42.19.0.12")}),1.0]])]});
            var Q629;
            Q629=makeQuery(id+"F6.imprint","IMPRINT",FACE,{"disambiguationData":[TD([[makeQuery(id+"F6.imprint","IMPRINT",EDGE,{"derivedFrom":sQuery(id+"F6.wireOp",EDGE,"E42.24.0.2")}),1.0]])]});
            var Q630;
            Q630=makeQuery(id+"F6.imprint","IMPRINT",FACE,{"disambiguationData":[TD([[makeQuery(id+"F6.imprint","IMPRINT",EDGE,{"derivedFrom":sQuery(id+"F6.wireOp",EDGE,"E42.23.0.12")}),1.0]])]});
            var Q631;
            Q631=makeQuery(id+"F6.imprint","IMPRINT",FACE,{"disambiguationData":[TD([[makeQuery(id+"F6.imprint","IMPRINT",EDGE,{"derivedFrom":sQuery(id+"F6.wireOp",EDGE,"E42.22.0.20")}),1.0]])]});
            var Q632;
            Q632=makeQuery(id+"F6.imprint","IMPRINT",FACE,{"disambiguationData":[TD([[makeQuery(id+"F6.imprint","IMPRINT",EDGE,{"derivedFrom":sQuery(id+"F6.wireOp",EDGE,"E42.22.0.2")}),1.0]])]});
            var Q633;
            Q633=makeQuery(id+"F6.imprint","IMPRINT",FACE,{"disambiguationData":[TD([[makeQuery(id+"F6.imprint","IMPRINT",EDGE,{"derivedFrom":sQuery(id+"F6.wireOp",EDGE,"E42.26.0.20")}),1.0]])]});
            var Q634;
            Q634=makeQuery(id+"F6.imprint","IMPRINT",FACE,{"disambiguationData":[TD([[makeQuery(id+"F6.imprint","IMPRINT",EDGE,{"derivedFrom":sQuery(id+"F6.wireOp",EDGE,"E42.26.0.2")}),1.0]])]});
            var Q635;
            Q635=makeQuery(id+"F6.imprint","IMPRINT",FACE,{"disambiguationData":[TD([[makeQuery(id+"F6.imprint","IMPRINT",EDGE,{"derivedFrom":sQuery(id+"F6.wireOp",EDGE,"E42.25.0.12")}),1.0]])]});
            var Q636;
            Q636=makeQuery(id+"F6.imprint","IMPRINT",FACE,{"disambiguationData":[TD([[makeQuery(id+"F6.imprint","IMPRINT",EDGE,{"derivedFrom":sQuery(id+"F6.wireOp",EDGE,"E42.24.0.20")}),1.0]])]});
            var Q637;
            Q637=makeQuery(id+"F6.imprint","IMPRINT",FACE,{"disambiguationData":[TD([[makeQuery(id+"F6.imprint","IMPRINT",EDGE,{"derivedFrom":sQuery(id+"F6.wireOp",EDGE,"E564.MirrorC")}),-1.0]])]});
            var Q638;
            Q638=makeQuery(id+"F6.imprint","IMPRINT",FACE,{"disambiguationData":[TD([[makeQuery(id+"F6.imprint","IMPRINT",EDGE,{"derivedFrom":sQuery(id+"F6.wireOp",EDGE,"E42.29.0.12")}),1.0]])]});
            var Q639;
            Q639=makeQuery(id+"F6.imprint","IMPRINT",FACE,{"disambiguationData":[TD([[makeQuery(id+"F6.imprint","IMPRINT",EDGE,{"derivedFrom":sQuery(id+"F6.wireOp",EDGE,"E42.28.0.20")}),1.0]])]});
            var Q640;
            Q640=makeQuery(id+"F6.imprint","IMPRINT",FACE,{"disambiguationData":[TD([[makeQuery(id+"F6.imprint","IMPRINT",EDGE,{"derivedFrom":sQuery(id+"F6.wireOp",EDGE,"E42.28.0.2")}),1.0]])]});
            var Q641;
            Q641=makeQuery(id+"F6.imprint","IMPRINT",FACE,{"disambiguationData":[TD([[makeQuery(id+"F6.imprint","IMPRINT",EDGE,{"derivedFrom":sQuery(id+"F6.wireOp",EDGE,"E511.MirrorC")}),-1.0]])]});
            var Q642;
            Q642=makeQuery(id+"F6.imprint","IMPRINT",FACE,{"disambiguationData":[TD([[makeQuery(id+"F6.imprint","IMPRINT",EDGE,{"derivedFrom":sQuery(id+"F6.wireOp",EDGE,"E42.27.0.12")}),1.0]])]});
            var Q643;
            Q643=makeQuery(id+"F6.imprint","IMPRINT",FACE,{"disambiguationData":[TD([[makeQuery(id+"F6.imprint","IMPRINT",EDGE,{"derivedFrom":sQuery(id+"F6.wireOp",EDGE,"E42.32.0.2")}),1.0]])]});
            var Q644;
            Q644=makeQuery(id+"F6.imprint","IMPRINT",FACE,{"disambiguationData":[TD([[makeQuery(id+"F6.imprint","IMPRINT",EDGE,{"derivedFrom":sQuery(id+"F6.wireOp",EDGE,"E42.31.0.12")}),1.0]])]});
            var Q645;
            Q645=makeQuery(id+"F6.imprint","IMPRINT",FACE,{"disambiguationData":[TD([[makeQuery(id+"F6.imprint","IMPRINT",EDGE,{"derivedFrom":sQuery(id+"F6.wireOp",EDGE,"E42.30.0.20")}),1.0]])]});
            var Q646;
            Q646=makeQuery(id+"F6.imprint","IMPRINT",FACE,{"disambiguationData":[TD([[makeQuery(id+"F6.imprint","IMPRINT",EDGE,{"derivedFrom":sQuery(id+"F6.wireOp",EDGE,"E42.30.0.2")}),1.0]])]});
            var Q647;
            Q647=makeQuery(id+"F6.imprint","IMPRINT",FACE,{"disambiguationData":[TD([[makeQuery(id+"F6.imprint","IMPRINT",EDGE,{"derivedFrom":sQuery(id+"F6.wireOp",EDGE,"E42.32.0.20")}),1.0]])]});
            var Q648;
            Q648=makeQuery(id+"F6.imprint","IMPRINT",FACE,{"disambiguationData":[TD([[makeQuery(id+"F6.imprint","IMPRINT",EDGE,{"derivedFrom":sQuery(id+"F6.wireOp",EDGE,"E42.1.0.12")}),1.0]])]});
            var Q649;
            Q649=makeQuery(id+"F6.imprint","IMPRINT",FACE,{"disambiguationData":[TD([[makeQuery(id+"F6.imprint","IMPRINT",EDGE,{"derivedFrom":sQuery(id+"F6.wireOp",EDGE,"E41.0.5.0")}),1.0]])]});
            var Q650;
            Q650=makeQuery(id+"F6.imprint","IMPRINT",FACE,{"disambiguationData":[TD([[makeQuery(id+"F6.imprint","IMPRINT",EDGE,{"derivedFrom":sQuery(id+"F6.wireOp",EDGE,"E42.4.0.2")}),1.0]])]});
            var Q651;
            Q651=makeQuery(id+"F6.imprint","IMPRINT",FACE,{"disambiguationData":[TD([[makeQuery(id+"F6.imprint","IMPRINT",EDGE,{"derivedFrom":sQuery(id+"F6.wireOp",EDGE,"E42.3.0.12")}),1.0]])]});
            var Q652;
            Q652=makeQuery(id+"F6.imprint","IMPRINT",FACE,{"disambiguationData":[TD([[makeQuery(id+"F6.imprint","IMPRINT",EDGE,{"derivedFrom":sQuery(id+"F6.wireOp",EDGE,"E42.2.0.20")}),1.0]])]});
            var Q653;
            Q653=makeQuery(id+"F6.imprint","IMPRINT",FACE,{"disambiguationData":[TD([[makeQuery(id+"F6.imprint","IMPRINT",EDGE,{"derivedFrom":sQuery(id+"F6.wireOp",EDGE,"E42.2.0.2")}),1.0]])]});
            var Q654;
            Q654=makeQuery(id+"F6.imprint","IMPRINT",FACE,{"disambiguationData":[TD([[makeQuery(id+"F6.imprint","IMPRINT",EDGE,{"derivedFrom":sQuery(id+"F6.wireOp",EDGE,"E42.6.0.20")}),1.0]])]});
            var Q655;
            Q655=makeQuery(id+"F6.imprint","IMPRINT",FACE,{"disambiguationData":[TD([[makeQuery(id+"F6.imprint","IMPRINT",EDGE,{"derivedFrom":sQuery(id+"F6.wireOp",EDGE,"E42.6.0.2")}),1.0]])]});
            var Q656;
            Q656=makeQuery(id+"F6.imprint","IMPRINT",FACE,{"disambiguationData":[TD([[makeQuery(id+"F6.imprint","IMPRINT",EDGE,{"derivedFrom":sQuery(id+"F6.wireOp",EDGE,"E42.5.0.12")}),1.0]])]});
            var Q657;
            Q657=makeQuery(id+"F6.imprint","IMPRINT",FACE,{"disambiguationData":[TD([[makeQuery(id+"F6.imprint","IMPRINT",EDGE,{"derivedFrom":sQuery(id+"F6.wireOp",EDGE,"E42.4.0.20")}),1.0]])]});
            var Q658;
            Q658=makeQuery(id+"F6.imprint","IMPRINT",FACE,{"disambiguationData":[TD([[makeQuery(id+"F6.imprint","IMPRINT",EDGE,{"derivedFrom":sQuery(id+"F6.wireOp",EDGE,"E42.9.0.12")}),1.0]])]});
            var Q659;
            Q659=makeQuery(id+"F6.imprint","IMPRINT",FACE,{"disambiguationData":[TD([[makeQuery(id+"F6.imprint","IMPRINT",EDGE,{"derivedFrom":sQuery(id+"F6.wireOp",EDGE,"E42.8.0.20")}),1.0]])]});
            var Q660;
            Q660=makeQuery(id+"F6.imprint","IMPRINT",FACE,{"disambiguationData":[TD([[makeQuery(id+"F6.imprint","IMPRINT",EDGE,{"derivedFrom":sQuery(id+"F6.wireOp",EDGE,"E42.8.0.2")}),1.0]])]});
            var Q661;
            Q661=makeQuery(id+"F6.imprint","IMPRINT",FACE,{"disambiguationData":[TD([[makeQuery(id+"F6.imprint","IMPRINT",EDGE,{"derivedFrom":sQuery(id+"F6.wireOp",EDGE,"E42.7.0.12")}),1.0]])]});
            var Q662;
            Q662=makeQuery(id+"F6.imprint","IMPRINT",FACE,{"disambiguationData":[TD([[makeQuery(id+"F6.imprint","IMPRINT",EDGE,{"derivedFrom":sQuery(id+"F6.wireOp",EDGE,"E42.12.0.2")}),1.0]])]});
            var Q663;
            Q663=makeQuery(id+"F6.imprint","IMPRINT",FACE,{"disambiguationData":[TD([[makeQuery(id+"F6.imprint","IMPRINT",EDGE,{"derivedFrom":sQuery(id+"F6.wireOp",EDGE,"E42.11.0.12")}),1.0]])]});
            var Q664;
            Q664=makeQuery(id+"F6.imprint","IMPRINT",FACE,{"disambiguationData":[TD([[makeQuery(id+"F6.imprint","IMPRINT",EDGE,{"derivedFrom":sQuery(id+"F6.wireOp",EDGE,"E42.10.0.20")}),1.0]])]});
            var Q665;
            Q665=makeQuery(id+"F6.imprint","IMPRINT",FACE,{"disambiguationData":[TD([[makeQuery(id+"F6.imprint","IMPRINT",EDGE,{"derivedFrom":sQuery(id+"F6.wireOp",EDGE,"E527.MirrorC")}),-1.0]])]});
            var Q666;
            Q666=makeQuery(id+"F6.imprint","IMPRINT",FACE,{"disambiguationData":[TD([[makeQuery(id+"F6.imprint","IMPRINT",EDGE,{"derivedFrom":sQuery(id+"F6.wireOp",EDGE,"E580.MirrorC")}),-1.0]])]});
            var Q667;
            Q667=makeQuery(id+"F6.imprint","IMPRINT",FACE,{"disambiguationData":[TD([[makeQuery(id+"F6.imprint","IMPRINT",EDGE,{"derivedFrom":sQuery(id+"F6.wireOp",EDGE,"E42.10.0.2")}),1.0]])]});
            var Q668;
            Q668=makeQuery(id+"F6.imprint","IMPRINT",FACE,{"disambiguationData":[TD([[makeQuery(id+"F6.imprint","IMPRINT",EDGE,{"derivedFrom":sQuery(id+"F6.wireOp",EDGE,"E42.14.0.20")}),1.0]])]});
            var Q669;
            Q669=makeQuery(id+"F6.imprint","IMPRINT",FACE,{"disambiguationData":[TD([[makeQuery(id+"F6.imprint","IMPRINT",EDGE,{"derivedFrom":sQuery(id+"F6.wireOp",EDGE,"E42.14.0.2")}),1.0]])]});
            var Q670;
            Q670=makeQuery(id+"F6.imprint","IMPRINT",FACE,{"disambiguationData":[TD([[makeQuery(id+"F6.imprint","IMPRINT",EDGE,{"derivedFrom":sQuery(id+"F6.wireOp",EDGE,"E42.13.0.12")}),1.0]])]});
            var Q671;
            Q671=makeQuery(id+"F6.imprint","IMPRINT",FACE,{"disambiguationData":[TD([[makeQuery(id+"F6.imprint","IMPRINT",EDGE,{"derivedFrom":sQuery(id+"F6.wireOp",EDGE,"E42.12.0.20")}),1.0]])]});
            var Q672;
            Q672=makeQuery(id+"F6.imprint","IMPRINT",FACE,{"disambiguationData":[TD([[makeQuery(id+"F6.imprint","IMPRINT",EDGE,{"derivedFrom":sQuery(id+"F6.wireOp",EDGE,"E42.16.0.20")}),1.0]])]});
            var Q673;
            Q673=makeQuery(id+"F6.imprint","IMPRINT",FACE,{"disambiguationData":[TD([[makeQuery(id+"F6.imprint","IMPRINT",EDGE,{"derivedFrom":sQuery(id+"F6.wireOp",EDGE,"E42.16.0.2")}),1.0]])]});
            var Q674;
            Q674=makeQuery(id+"F6.imprint","IMPRINT",FACE,{"disambiguationData":[TD([[makeQuery(id+"F6.imprint","IMPRINT",EDGE,{"derivedFrom":sQuery(id+"F6.wireOp",EDGE,"E42.15.0.12")}),1.0]])]});
            var Q675;
            Q675=makeQuery(id+"F6.imprint","IMPRINT",FACE,{"disambiguationData":[TD([[makeQuery(id+"F6.imprint","IMPRINT",EDGE,{"derivedFrom":sQuery(id+"F6.wireOp",EDGE,"E311.MirrorC")}),-1.0]])]});
            var Q676;
            Q676=makeQuery(id+"F6.imprint","IMPRINT",FACE,{"disambiguationData":[TD([[makeQuery(id+"F6.imprint","IMPRINT",EDGE,{"derivedFrom":sQuery(id+"F6.wireOp",EDGE,"E326.MirrorC")}),-1.0]])]});
            var Q677;
            Q677=makeQuery(id+"F6.imprint","IMPRINT",FACE,{"disambiguationData":[TD([[makeQuery(id+"F6.imprint","IMPRINT",EDGE,{"derivedFrom":sQuery(id+"F6.wireOp",EDGE,"E263.MirrorC")}),-1.0]])]});
            var Q678;
            Q678=makeQuery(id+"F6.imprint","IMPRINT",FACE,{"disambiguationData":[TD([[makeQuery(id+"F6.imprint","IMPRINT",EDGE,{"derivedFrom":sQuery(id+"F6.wireOp",EDGE,"E250.MirrorC")}),-1.0]])]});
            var Q679;
            Q679=makeQuery(id+"F6.imprint","IMPRINT",FACE,{"disambiguationData":[TD([[makeQuery(id+"F6.imprint","IMPRINT",EDGE,{"derivedFrom":sQuery(id+"F6.wireOp",EDGE,"E295.MirrorC")}),-1.0]])]});
            var Q680;
            Q680=makeQuery(id+"F6.imprint","IMPRINT",FACE,{"disambiguationData":[TD([[makeQuery(id+"F6.imprint","IMPRINT",EDGE,{"derivedFrom":sQuery(id+"F6.wireOp",EDGE,"E279.MirrorC")}),-1.0]])]});
            var Q681;
            Q681=makeQuery(id+"F6.imprint","IMPRINT",FACE,{"disambiguationData":[TD([[makeQuery(id+"F6.imprint","IMPRINT",EDGE,{"derivedFrom":sQuery(id+"F6.wireOp",EDGE,"E42.1.0.13")}),1.0]])]});
            var Q682;
            Q682=makeQuery(id+"F6.imprint","IMPRINT",FACE,{"disambiguationData":[TD([[makeQuery(id+"F6.imprint","IMPRINT",EDGE,{"derivedFrom":sQuery(id+"F6.wireOp",EDGE,"E481.MirrorC")}),-1.0]])]});
            var Q683;
            Q683=makeQuery(id+"F6.imprint","IMPRINT",FACE,{"disambiguationData":[TD([[makeQuery(id+"F6.imprint","IMPRINT",EDGE,{"derivedFrom":sQuery(id+"F6.wireOp",EDGE,"E41.0.6.0")}),1.0]])]});
            var Q684;
            Q684=makeQuery(id+"F6.imprint","IMPRINT",FACE,{"disambiguationData":[TD([[makeQuery(id+"F6.imprint","IMPRINT",EDGE,{"derivedFrom":sQuery(id+"F6.wireOp",EDGE,"E534.MirrorC")}),-1.0]])]});
            var Q685;
            Q685=makeQuery(id+"F6.imprint","IMPRINT",FACE,{"disambiguationData":[TD([[makeQuery(id+"F6.imprint","IMPRINT",EDGE,{"derivedFrom":sQuery(id+"F6.wireOp",EDGE,"E549.MirrorC")}),-1.0]])]});
            var Q686;
            Q686=makeQuery(id+"F6.imprint","IMPRINT",FACE,{"disambiguationData":[TD([[makeQuery(id+"F6.imprint","IMPRINT",EDGE,{"derivedFrom":sQuery(id+"F6.wireOp",EDGE,"E42.21.0.13")}),1.0]])]});
            var Q687;
            Q687=makeQuery(id+"F6.imprint","IMPRINT",FACE,{"disambiguationData":[TD([[makeQuery(id+"F6.imprint","IMPRINT",EDGE,{"derivedFrom":sQuery(id+"F6.wireOp",EDGE,"E42.20.0.21")}),1.0]])]});
            var Q688;
            Q688=makeQuery(id+"F6.imprint","IMPRINT",FACE,{"disambiguationData":[TD([[makeQuery(id+"F6.imprint","IMPRINT",EDGE,{"derivedFrom":sQuery(id+"F6.wireOp",EDGE,"E42.20.0.4")}),1.0]])]});
            var Q689;
            Q689=makeQuery(id+"F6.imprint","IMPRINT",FACE,{"disambiguationData":[TD([[makeQuery(id+"F6.imprint","IMPRINT",EDGE,{"derivedFrom":sQuery(id+"F6.wireOp",EDGE,"E42.19.0.13")}),1.0]])]});
            var Q690;
            Q690=makeQuery(id+"F6.imprint","IMPRINT",FACE,{"disambiguationData":[TD([[makeQuery(id+"F6.imprint","IMPRINT",EDGE,{"derivedFrom":sQuery(id+"F6.wireOp",EDGE,"E42.24.0.4")}),1.0]])]});
            var Q691;
            Q691=makeQuery(id+"F6.imprint","IMPRINT",FACE,{"disambiguationData":[TD([[makeQuery(id+"F6.imprint","IMPRINT",EDGE,{"derivedFrom":sQuery(id+"F6.wireOp",EDGE,"E42.23.0.13")}),1.0]])]});
            var Q692;
            Q692=makeQuery(id+"F6.imprint","IMPRINT",FACE,{"disambiguationData":[TD([[makeQuery(id+"F6.imprint","IMPRINT",EDGE,{"derivedFrom":sQuery(id+"F6.wireOp",EDGE,"E42.22.0.21")}),1.0]])]});
            var Q693;
            Q693=makeQuery(id+"F6.imprint","IMPRINT",FACE,{"disambiguationData":[TD([[makeQuery(id+"F6.imprint","IMPRINT",EDGE,{"derivedFrom":sQuery(id+"F6.wireOp",EDGE,"E42.22.0.4")}),1.0]])]});
            var Q694;
            Q694=makeQuery(id+"F6.imprint","IMPRINT",FACE,{"disambiguationData":[TD([[makeQuery(id+"F6.imprint","IMPRINT",EDGE,{"derivedFrom":sQuery(id+"F6.wireOp",EDGE,"E42.26.0.21")}),1.0]])]});
            var Q695;
            Q695=makeQuery(id+"F6.imprint","IMPRINT",FACE,{"disambiguationData":[TD([[makeQuery(id+"F6.imprint","IMPRINT",EDGE,{"derivedFrom":sQuery(id+"F6.wireOp",EDGE,"E42.26.0.4")}),1.0]])]});
            var Q696;
            Q696=makeQuery(id+"F6.imprint","IMPRINT",FACE,{"disambiguationData":[TD([[makeQuery(id+"F6.imprint","IMPRINT",EDGE,{"derivedFrom":sQuery(id+"F6.wireOp",EDGE,"E42.25.0.13")}),1.0]])]});
            var Q697;
            Q697=makeQuery(id+"F6.imprint","IMPRINT",FACE,{"disambiguationData":[TD([[makeQuery(id+"F6.imprint","IMPRINT",EDGE,{"derivedFrom":sQuery(id+"F6.wireOp",EDGE,"E42.24.0.21")}),1.0]])]});
            var Q698;
            Q698=makeQuery(id+"F6.imprint","IMPRINT",FACE,{"disambiguationData":[TD([[makeQuery(id+"F6.imprint","IMPRINT",EDGE,{"derivedFrom":sQuery(id+"F6.wireOp",EDGE,"E42.29.0.13")}),1.0]])]});
            var Q699;
            Q699=makeQuery(id+"F6.imprint","IMPRINT",FACE,{"disambiguationData":[TD([[makeQuery(id+"F6.imprint","IMPRINT",EDGE,{"derivedFrom":sQuery(id+"F6.wireOp",EDGE,"E42.28.0.21")}),1.0]])]});
            var Q700;
            Q700=makeQuery(id+"F6.imprint","IMPRINT",FACE,{"disambiguationData":[TD([[makeQuery(id+"F6.imprint","IMPRINT",EDGE,{"derivedFrom":sQuery(id+"F6.wireOp",EDGE,"E42.28.0.4")}),1.0]])]});
            var Q701;
            Q701=makeQuery(id+"F6.imprint","IMPRINT",FACE,{"disambiguationData":[TD([[makeQuery(id+"F6.imprint","IMPRINT",EDGE,{"derivedFrom":sQuery(id+"F6.wireOp",EDGE,"E42.27.0.13")}),1.0]])]});
            var Q702;
            Q702=makeQuery(id+"F6.imprint","IMPRINT",FACE,{"disambiguationData":[TD([[makeQuery(id+"F6.imprint","IMPRINT",EDGE,{"derivedFrom":sQuery(id+"F6.wireOp",EDGE,"E42.32.0.4")}),1.0]])]});
            var Q703;
            Q703=makeQuery(id+"F6.imprint","IMPRINT",FACE,{"disambiguationData":[TD([[makeQuery(id+"F6.imprint","IMPRINT",EDGE,{"derivedFrom":sQuery(id+"F6.wireOp",EDGE,"E42.31.0.13")}),1.0]])]});
            var Q704;
            Q704=makeQuery(id+"F6.imprint","IMPRINT",FACE,{"disambiguationData":[TD([[makeQuery(id+"F6.imprint","IMPRINT",EDGE,{"derivedFrom":sQuery(id+"F6.wireOp",EDGE,"E42.30.0.21")}),1.0]])]});
            var Q705;
            Q705=makeQuery(id+"F6.imprint","IMPRINT",FACE,{"disambiguationData":[TD([[makeQuery(id+"F6.imprint","IMPRINT",EDGE,{"derivedFrom":sQuery(id+"F6.wireOp",EDGE,"E42.30.0.4")}),1.0]])]});
            var Q706;
            Q706=makeQuery(id+"F6.imprint","IMPRINT",FACE,{"disambiguationData":[TD([[makeQuery(id+"F6.imprint","IMPRINT",EDGE,{"derivedFrom":sQuery(id+"F6.wireOp",EDGE,"E625.MirrorC")}),-1.0]])]});
            var Q707;
            Q707=makeQuery(id+"F6.imprint","IMPRINT",FACE,{"disambiguationData":[TD([[makeQuery(id+"F6.imprint","IMPRINT",EDGE,{"derivedFrom":sQuery(id+"F6.wireOp",EDGE,"E573.MirrorC")}),-1.0]])]});
            var Q708;
            Q708=makeQuery(id+"F6.imprint","IMPRINT",FACE,{"disambiguationData":[TD([[makeQuery(id+"F6.imprint","IMPRINT",EDGE,{"derivedFrom":sQuery(id+"F6.wireOp",EDGE,"E42.32.0.21")}),1.0]])]});
            var Q709;
            Q709=makeQuery(id+"F6.imprint","IMPRINT",FACE,{"disambiguationData":[TD([[makeQuery(id+"F6.imprint","IMPRINT",EDGE,{"derivedFrom":sQuery(id+"F6.wireOp",EDGE,"E379.MirrorC")}),-1.0]])]});
            var Q710;
            Q710=makeQuery(id+"F6.imprint","IMPRINT",FACE,{"disambiguationData":[TD([[makeQuery(id+"F6.imprint","IMPRINT",EDGE,{"derivedFrom":sQuery(id+"F6.wireOp",EDGE,"E42.4.0.4")}),1.0]])]});
            var Q711;
            Q711=makeQuery(id+"F6.imprint","IMPRINT",FACE,{"disambiguationData":[TD([[makeQuery(id+"F6.imprint","IMPRINT",EDGE,{"derivedFrom":sQuery(id+"F6.wireOp",EDGE,"E42.3.0.13")}),1.0]])]});
            var Q712;
            Q712=makeQuery(id+"F6.imprint","IMPRINT",FACE,{"disambiguationData":[TD([[makeQuery(id+"F6.imprint","IMPRINT",EDGE,{"derivedFrom":sQuery(id+"F6.wireOp",EDGE,"E42.2.0.21")}),1.0]])]});
            var Q713;
            Q713=makeQuery(id+"F6.imprint","IMPRINT",FACE,{"disambiguationData":[TD([[makeQuery(id+"F6.imprint","IMPRINT",EDGE,{"derivedFrom":sQuery(id+"F6.wireOp",EDGE,"E42.2.0.4")}),1.0]])]});
            var Q714;
            Q714=makeQuery(id+"F6.imprint","IMPRINT",FACE,{"disambiguationData":[TD([[makeQuery(id+"F6.imprint","IMPRINT",EDGE,{"derivedFrom":sQuery(id+"F6.wireOp",EDGE,"E42.6.0.21")}),1.0]])]});
            var Q715;
            Q715=makeQuery(id+"F6.imprint","IMPRINT",FACE,{"disambiguationData":[TD([[makeQuery(id+"F6.imprint","IMPRINT",EDGE,{"derivedFrom":sQuery(id+"F6.wireOp",EDGE,"E42.6.0.4")}),1.0]])]});
            var Q716;
            Q716=makeQuery(id+"F6.imprint","IMPRINT",FACE,{"disambiguationData":[TD([[makeQuery(id+"F6.imprint","IMPRINT",EDGE,{"derivedFrom":sQuery(id+"F6.wireOp",EDGE,"E42.5.0.13")}),1.0]])]});
            var Q717;
            Q717=makeQuery(id+"F6.imprint","IMPRINT",FACE,{"disambiguationData":[TD([[makeQuery(id+"F6.imprint","IMPRINT",EDGE,{"derivedFrom":sQuery(id+"F6.wireOp",EDGE,"E42.4.0.21")}),1.0]])]});
            var Q718;
            Q718=makeQuery(id+"F6.imprint","IMPRINT",FACE,{"disambiguationData":[TD([[makeQuery(id+"F6.imprint","IMPRINT",EDGE,{"derivedFrom":sQuery(id+"F6.wireOp",EDGE,"E42.9.0.13")}),1.0]])]});
            var Q719;
            Q719=makeQuery(id+"F6.imprint","IMPRINT",FACE,{"disambiguationData":[TD([[makeQuery(id+"F6.imprint","IMPRINT",EDGE,{"derivedFrom":sQuery(id+"F6.wireOp",EDGE,"E42.8.0.21")}),1.0]])]});
            var Q720;
            Q720=makeQuery(id+"F6.imprint","IMPRINT",FACE,{"disambiguationData":[TD([[makeQuery(id+"F6.imprint","IMPRINT",EDGE,{"derivedFrom":sQuery(id+"F6.wireOp",EDGE,"E42.8.0.4")}),1.0]])]});
            var Q721;
            Q721=makeQuery(id+"F6.imprint","IMPRINT",FACE,{"disambiguationData":[TD([[makeQuery(id+"F6.imprint","IMPRINT",EDGE,{"derivedFrom":sQuery(id+"F6.wireOp",EDGE,"E42.7.0.13")}),1.0]])]});
            var Q722;
            Q722=makeQuery(id+"F6.imprint","IMPRINT",FACE,{"disambiguationData":[TD([[makeQuery(id+"F6.imprint","IMPRINT",EDGE,{"derivedFrom":sQuery(id+"F6.wireOp",EDGE,"E42.12.0.4")}),1.0]])]});
            var Q723;
            Q723=makeQuery(id+"F6.imprint","IMPRINT",FACE,{"disambiguationData":[TD([[makeQuery(id+"F6.imprint","IMPRINT",EDGE,{"derivedFrom":sQuery(id+"F6.wireOp",EDGE,"E42.11.0.13")}),1.0]])]});
            var Q724;
            Q724=makeQuery(id+"F6.imprint","IMPRINT",FACE,{"disambiguationData":[TD([[makeQuery(id+"F6.imprint","IMPRINT",EDGE,{"derivedFrom":sQuery(id+"F6.wireOp",EDGE,"E42.10.0.21")}),1.0]])]});
            var Q725;
            Q725=makeQuery(id+"F6.imprint","IMPRINT",FACE,{"disambiguationData":[TD([[makeQuery(id+"F6.imprint","IMPRINT",EDGE,{"derivedFrom":sQuery(id+"F6.wireOp",EDGE,"E42.10.0.4")}),1.0]])]});
            var Q726;
            Q726=makeQuery(id+"F6.imprint","IMPRINT",FACE,{"disambiguationData":[TD([[makeQuery(id+"F6.imprint","IMPRINT",EDGE,{"derivedFrom":sQuery(id+"F6.wireOp",EDGE,"E42.14.0.21")}),1.0]])]});
            var Q727;
            Q727=makeQuery(id+"F6.imprint","IMPRINT",FACE,{"disambiguationData":[TD([[makeQuery(id+"F6.imprint","IMPRINT",EDGE,{"derivedFrom":sQuery(id+"F6.wireOp",EDGE,"E42.14.0.4")}),1.0]])]});
            var Q728;
            Q728=makeQuery(id+"F6.imprint","IMPRINT",FACE,{"disambiguationData":[TD([[makeQuery(id+"F6.imprint","IMPRINT",EDGE,{"derivedFrom":sQuery(id+"F6.wireOp",EDGE,"E42.13.0.13")}),1.0]])]});
            var Q729;
            Q729=makeQuery(id+"F6.imprint","IMPRINT",FACE,{"disambiguationData":[TD([[makeQuery(id+"F6.imprint","IMPRINT",EDGE,{"derivedFrom":sQuery(id+"F6.wireOp",EDGE,"E42.12.0.21")}),1.0]])]});
            var Q730;
            Q730=makeQuery(id+"F6.imprint","IMPRINT",FACE,{"disambiguationData":[TD([[makeQuery(id+"F6.imprint","IMPRINT",EDGE,{"derivedFrom":sQuery(id+"F6.wireOp",EDGE,"E42.16.0.21")}),1.0]])]});
            var Q731;
            Q731=makeQuery(id+"F6.imprint","IMPRINT",FACE,{"disambiguationData":[TD([[makeQuery(id+"F6.imprint","IMPRINT",EDGE,{"derivedFrom":sQuery(id+"F6.wireOp",EDGE,"E42.16.0.4")}),1.0]])]});
            var Q732;
            Q732=makeQuery(id+"F6.imprint","IMPRINT",FACE,{"disambiguationData":[TD([[makeQuery(id+"F6.imprint","IMPRINT",EDGE,{"derivedFrom":sQuery(id+"F6.wireOp",EDGE,"E640.MirrorC")}),-1.0]])]});
            var Q733;
            Q733=makeQuery(id+"F6.imprint","IMPRINT",FACE,{"disambiguationData":[TD([[makeQuery(id+"F6.imprint","IMPRINT",EDGE,{"derivedFrom":sQuery(id+"F6.wireOp",EDGE,"E42.15.0.13")}),1.0]])]});
            var Q734;
            Q734=makeQuery(id+"F6.imprint","IMPRINT",FACE,{"disambiguationData":[TD([[makeQuery(id+"F6.imprint","IMPRINT",EDGE,{"derivedFrom":sQuery(id+"F6.wireOp",EDGE,"E589.MirrorC")}),-1.0]])]});
            var Q735;
            Q735=makeQuery(id+"F6.imprint","IMPRINT",FACE,{"disambiguationData":[TD([[makeQuery(id+"F6.imprint","IMPRINT",EDGE,{"derivedFrom":sQuery(id+"F6.wireOp",EDGE,"E42.18.0.21")}),1.0]])]});
            var Q736;
            Q736=makeQuery(id+"F6.imprint","IMPRINT",FACE,{"disambiguationData":[TD([[makeQuery(id+"F6.imprint","IMPRINT",EDGE,{"derivedFrom":sQuery(id+"F6.wireOp",EDGE,"E395.MirrorC")}),-1.0]])]});
            var Q737;
            Q737=makeQuery(id+"F6.imprint","IMPRINT",FACE,{"disambiguationData":[TD([[makeQuery(id+"F6.imprint","IMPRINT",EDGE,{"derivedFrom":sQuery(id+"F6.wireOp",EDGE,"E42.18.0.4")}),1.0]])]});
            var Q738;
            Q738=makeQuery(id+"F6.imprint","IMPRINT",FACE,{"disambiguationData":[TD([[makeQuery(id+"F6.imprint","IMPRINT",EDGE,{"derivedFrom":sQuery(id+"F6.wireOp",EDGE,"E42.17.0.13")}),1.0]])]});
            var Q739;
            Q739=makeQuery(id+"F6.imprint","IMPRINT",FACE,{"disambiguationData":[TD([[makeQuery(id+"F6.imprint","IMPRINT",EDGE,{"derivedFrom":sQuery(id+"F6.wireOp",EDGE,"E342.MirrorC")}),-1.0]])]});
            var Q740;
            Q740=makeQuery(id+"F6.imprint","IMPRINT",FACE,{"disambiguationData":[TD([[makeQuery(id+"F6.imprint","IMPRINT",EDGE,{"derivedFrom":sQuery(id+"F6.wireOp",EDGE,"E312.MirrorC")}),-1.0]])]});
            var Q741;
            Q741=makeQuery(id+"F6.imprint","IMPRINT",FACE,{"disambiguationData":[TD([[makeQuery(id+"F6.imprint","IMPRINT",EDGE,{"derivedFrom":sQuery(id+"F6.wireOp",EDGE,"E327.MirrorC")}),-1.0]])]});
            var Q742;
            Q742=makeQuery(id+"F6.imprint","IMPRINT",FACE,{"disambiguationData":[TD([[makeQuery(id+"F6.imprint","IMPRINT",EDGE,{"derivedFrom":sQuery(id+"F6.wireOp",EDGE,"E264.MirrorC")}),-1.0]])]});
            var Q743;
            Q743=makeQuery(id+"F6.imprint","IMPRINT",FACE,{"disambiguationData":[TD([[makeQuery(id+"F6.imprint","IMPRINT",EDGE,{"derivedFrom":sQuery(id+"F6.wireOp",EDGE,"E542.MirrorC")}),-1.0]])]});
            var Q744;
            Q744=makeQuery(id+"F6.imprint","IMPRINT",FACE,{"disambiguationData":[TD([[makeQuery(id+"F6.imprint","IMPRINT",EDGE,{"derivedFrom":sQuery(id+"F6.wireOp",EDGE,"E296.MirrorC")}),-1.0]])]});
            var Q745;
            Q745=makeQuery(id+"F6.imprint","IMPRINT",FACE,{"disambiguationData":[TD([[makeQuery(id+"F6.imprint","IMPRINT",EDGE,{"derivedFrom":sQuery(id+"F6.wireOp",EDGE,"E595.MirrorC")}),-1.0]])]});
            var Q746;
            Q746=makeQuery(id+"F6.imprint","IMPRINT",FACE,{"disambiguationData":[TD([[makeQuery(id+"F6.imprint","IMPRINT",EDGE,{"derivedFrom":sQuery(id+"F6.wireOp",EDGE,"E280.MirrorC")}),-1.0]])]});
            var Q747;
            Q747=makeQuery(id+"F6.imprint","IMPRINT",FACE,{"disambiguationData":[TD([[makeQuery(id+"F6.imprint","IMPRINT",EDGE,{"derivedFrom":sQuery(id+"F6.wireOp",EDGE,"E42.1.0.14")}),1.0]])]});
            var Q748;
            Q748=makeQuery(id+"F6.imprint","IMPRINT",FACE,{"disambiguationData":[TD([[makeQuery(id+"F6.imprint","IMPRINT",EDGE,{"derivedFrom":sQuery(id+"F6.wireOp",EDGE,"E349.MirrorC")}),-1.0]])]});
            var Q749;
            Q749=makeQuery(id+"F6.imprint","IMPRINT",FACE,{"disambiguationData":[TD([[makeQuery(id+"F6.imprint","IMPRINT",EDGE,{"derivedFrom":sQuery(id+"F6.wireOp",EDGE,"E41.0.7.0")}),1.0]])]});
            var Q750;
            Q750=makeQuery(id+"F6.imprint","IMPRINT",FACE,{"disambiguationData":[TD([[makeQuery(id+"F6.imprint","IMPRINT",EDGE,{"derivedFrom":sQuery(id+"F6.wireOp",EDGE,"E42.4.0.5")}),1.0]])]});
            var Q751;
            Q751=makeQuery(id+"F6.imprint","IMPRINT",FACE,{"disambiguationData":[TD([[makeQuery(id+"F6.imprint","IMPRINT",EDGE,{"derivedFrom":sQuery(id+"F6.wireOp",EDGE,"E42.3.0.14")}),1.0]])]});
            var Q752;
            Q752=makeQuery(id+"F6.imprint","IMPRINT",FACE,{"disambiguationData":[TD([[makeQuery(id+"F6.imprint","IMPRINT",EDGE,{"derivedFrom":sQuery(id+"F6.wireOp",EDGE,"E42.2.0.22")}),1.0]])]});
            var Q753;
            Q753=makeQuery(id+"F6.imprint","IMPRINT",FACE,{"disambiguationData":[TD([[makeQuery(id+"F6.imprint","IMPRINT",EDGE,{"derivedFrom":sQuery(id+"F6.wireOp",EDGE,"E42.2.0.5")}),1.0]])]});
            var Q754;
            Q754=makeQuery(id+"F6.imprint","IMPRINT",FACE,{"disambiguationData":[TD([[makeQuery(id+"F6.imprint","IMPRINT",EDGE,{"derivedFrom":sQuery(id+"F6.wireOp",EDGE,"E610.MirrorC")}),-1.0]])]});
            var Q755;
            Q755=makeQuery(id+"F6.imprint","IMPRINT",FACE,{"disambiguationData":[TD([[makeQuery(id+"F6.imprint","IMPRINT",EDGE,{"derivedFrom":sQuery(id+"F6.wireOp",EDGE,"E363.MirrorC")}),-1.0]])]});
            var Q756;
            Q756=makeQuery(id+"F6.imprint","IMPRINT",FACE,{"disambiguationData":[TD([[makeQuery(id+"F6.imprint","IMPRINT",EDGE,{"derivedFrom":sQuery(id+"F6.wireOp",EDGE,"E42.24.0.5")}),1.0]])]});
            var Q757;
            Q757=makeQuery(id+"F6.imprint","IMPRINT",FACE,{"disambiguationData":[TD([[makeQuery(id+"F6.imprint","IMPRINT",EDGE,{"derivedFrom":sQuery(id+"F6.wireOp",EDGE,"E42.23.0.14")}),1.0]])]});
            var Q758;
            Q758=makeQuery(id+"F6.imprint","IMPRINT",FACE,{"disambiguationData":[TD([[makeQuery(id+"F6.imprint","IMPRINT",EDGE,{"derivedFrom":sQuery(id+"F6.wireOp",EDGE,"E42.22.0.22")}),1.0]])]});
            var Q759;
            Q759=makeQuery(id+"F6.imprint","IMPRINT",FACE,{"disambiguationData":[TD([[makeQuery(id+"F6.imprint","IMPRINT",EDGE,{"derivedFrom":sQuery(id+"F6.wireOp",EDGE,"E42.22.0.5")}),1.0]])]});
            var Q760;
            Q760=makeQuery(id+"F6.imprint","IMPRINT",FACE,{"disambiguationData":[TD([[makeQuery(id+"F6.imprint","IMPRINT",EDGE,{"derivedFrom":sQuery(id+"F6.wireOp",EDGE,"E42.26.0.22")}),1.0]])]});
            var Q761;
            Q761=makeQuery(id+"F6.imprint","IMPRINT",FACE,{"disambiguationData":[TD([[makeQuery(id+"F6.imprint","IMPRINT",EDGE,{"derivedFrom":sQuery(id+"F6.wireOp",EDGE,"E42.26.0.5")}),1.0]])]});
            var Q762;
            Q762=makeQuery(id+"F6.imprint","IMPRINT",FACE,{"disambiguationData":[TD([[makeQuery(id+"F6.imprint","IMPRINT",EDGE,{"derivedFrom":sQuery(id+"F6.wireOp",EDGE,"E42.25.0.14")}),1.0]])]});
            var Q763;
            Q763=makeQuery(id+"F6.imprint","IMPRINT",FACE,{"disambiguationData":[TD([[makeQuery(id+"F6.imprint","IMPRINT",EDGE,{"derivedFrom":sQuery(id+"F6.wireOp",EDGE,"E42.24.0.22")}),1.0]])]});
            var Q764;
            Q764=makeQuery(id+"F6.imprint","IMPRINT",FACE,{"disambiguationData":[TD([[makeQuery(id+"F6.imprint","IMPRINT",EDGE,{"derivedFrom":sQuery(id+"F6.wireOp",EDGE,"E42.29.0.14")}),1.0]])]});
            var Q765;
            Q765=makeQuery(id+"F6.imprint","IMPRINT",FACE,{"disambiguationData":[TD([[makeQuery(id+"F6.imprint","IMPRINT",EDGE,{"derivedFrom":sQuery(id+"F6.wireOp",EDGE,"E42.28.0.22")}),1.0]])]});
            var Q766;
            Q766=makeQuery(id+"F6.imprint","IMPRINT",FACE,{"disambiguationData":[TD([[makeQuery(id+"F6.imprint","IMPRINT",EDGE,{"derivedFrom":sQuery(id+"F6.wireOp",EDGE,"E42.28.0.5")}),1.0]])]});
            var Q767;
            Q767=makeQuery(id+"F6.imprint","IMPRINT",FACE,{"disambiguationData":[TD([[makeQuery(id+"F6.imprint","IMPRINT",EDGE,{"derivedFrom":sQuery(id+"F6.wireOp",EDGE,"E701.MirrorC")}),-1.0]])]});
            var Q768;
            Q768=makeQuery(id+"F6.imprint","IMPRINT",FACE,{"disambiguationData":[TD([[makeQuery(id+"F6.imprint","IMPRINT",EDGE,{"derivedFrom":sQuery(id+"F6.wireOp",EDGE,"E648.MirrorC")}),-1.0]])]});
            var Q769;
            Q769=makeQuery(id+"F6.imprint","IMPRINT",FACE,{"disambiguationData":[TD([[makeQuery(id+"F6.imprint","IMPRINT",EDGE,{"derivedFrom":sQuery(id+"F6.wireOp",EDGE,"E42.27.0.14")}),1.0]])]});
            var Q770;
            Q770=makeQuery(id+"F6.imprint","IMPRINT",FACE,{"disambiguationData":[TD([[makeQuery(id+"F6.imprint","IMPRINT",EDGE,{"derivedFrom":sQuery(id+"F6.wireOp",EDGE,"E42.32.0.5")}),1.0]])]});
            var Q771;
            Q771=makeQuery(id+"F6.imprint","IMPRINT",FACE,{"disambiguationData":[TD([[makeQuery(id+"F6.imprint","IMPRINT",EDGE,{"derivedFrom":sQuery(id+"F6.wireOp",EDGE,"E42.31.0.14")}),1.0]])]});
            var Q772;
            Q772=makeQuery(id+"F6.imprint","IMPRINT",FACE,{"disambiguationData":[TD([[makeQuery(id+"F6.imprint","IMPRINT",EDGE,{"derivedFrom":sQuery(id+"F6.wireOp",EDGE,"E42.30.0.22")}),1.0]])]});
            var Q773;
            Q773=makeQuery(id+"F6.imprint","IMPRINT",FACE,{"disambiguationData":[TD([[makeQuery(id+"F6.imprint","IMPRINT",EDGE,{"derivedFrom":sQuery(id+"F6.wireOp",EDGE,"E42.30.0.5")}),1.0]])]});
            var Q774;
            Q774=makeQuery(id+"F6.imprint","IMPRINT",FACE,{"disambiguationData":[TD([[makeQuery(id+"F6.imprint","IMPRINT",EDGE,{"derivedFrom":sQuery(id+"F6.wireOp",EDGE,"E388.MirrorC")}),-1.0]])]});
            var Q775;
            Q775=makeQuery(id+"F6.imprint","IMPRINT",FACE,{"disambiguationData":[TD([[makeQuery(id+"F6.imprint","IMPRINT",EDGE,{"derivedFrom":sQuery(id+"F6.wireOp",EDGE,"E440.MirrorC")}),-1.0]])]});
            var Q776;
            Q776=makeQuery(id+"F6.imprint","IMPRINT",FACE,{"disambiguationData":[TD([[makeQuery(id+"F6.imprint","IMPRINT",EDGE,{"derivedFrom":sQuery(id+"F6.wireOp",EDGE,"E42.32.0.22")}),1.0]])]});
            var Q777;
            Q777=makeQuery(id+"F6.imprint","IMPRINT",FACE,{"disambiguationData":[TD([[makeQuery(id+"F6.imprint","IMPRINT",EDGE,{"derivedFrom":sQuery(id+"F6.wireOp",EDGE,"E42.6.0.22")}),1.0]])]});
            var Q778;
            Q778=makeQuery(id+"F6.imprint","IMPRINT",FACE,{"disambiguationData":[TD([[makeQuery(id+"F6.imprint","IMPRINT",EDGE,{"derivedFrom":sQuery(id+"F6.wireOp",EDGE,"E42.6.0.5")}),1.0]])]});
            var Q779;
            Q779=makeQuery(id+"F6.imprint","IMPRINT",FACE,{"disambiguationData":[TD([[makeQuery(id+"F6.imprint","IMPRINT",EDGE,{"derivedFrom":sQuery(id+"F6.wireOp",EDGE,"E42.5.0.14")}),1.0]])]});
            var Q780;
            Q780=makeQuery(id+"F6.imprint","IMPRINT",FACE,{"disambiguationData":[TD([[makeQuery(id+"F6.imprint","IMPRINT",EDGE,{"derivedFrom":sQuery(id+"F6.wireOp",EDGE,"E42.4.0.22")}),1.0]])]});
            var Q781;
            Q781=makeQuery(id+"F6.imprint","IMPRINT",FACE,{"disambiguationData":[TD([[makeQuery(id+"F6.imprint","IMPRINT",EDGE,{"derivedFrom":sQuery(id+"F6.wireOp",EDGE,"E42.9.0.14")}),1.0]])]});
            var Q782;
            Q782=makeQuery(id+"F6.imprint","IMPRINT",FACE,{"disambiguationData":[TD([[makeQuery(id+"F6.imprint","IMPRINT",EDGE,{"derivedFrom":sQuery(id+"F6.wireOp",EDGE,"E42.8.0.22")}),1.0]])]});
            var Q783;
            Q783=makeQuery(id+"F6.imprint","IMPRINT",FACE,{"disambiguationData":[TD([[makeQuery(id+"F6.imprint","IMPRINT",EDGE,{"derivedFrom":sQuery(id+"F6.wireOp",EDGE,"E42.8.0.5")}),1.0]])]});
            var Q784;
            Q784=makeQuery(id+"F6.imprint","IMPRINT",FACE,{"disambiguationData":[TD([[makeQuery(id+"F6.imprint","IMPRINT",EDGE,{"derivedFrom":sQuery(id+"F6.wireOp",EDGE,"E42.7.0.14")}),1.0]])]});
            var Q785;
            Q785=makeQuery(id+"F6.imprint","IMPRINT",FACE,{"disambiguationData":[TD([[makeQuery(id+"F6.imprint","IMPRINT",EDGE,{"derivedFrom":sQuery(id+"F6.wireOp",EDGE,"E663.MirrorC")}),-1.0]])]});
            var Q786;
            Q786=makeQuery(id+"F6.imprint","IMPRINT",FACE,{"disambiguationData":[TD([[makeQuery(id+"F6.imprint","IMPRINT",EDGE,{"derivedFrom":sQuery(id+"F6.wireOp",EDGE,"E42.12.0.5")}),1.0]])]});
            var Q787;
            Q787=makeQuery(id+"F6.imprint","IMPRINT",FACE,{"disambiguationData":[TD([[makeQuery(id+"F6.imprint","IMPRINT",EDGE,{"derivedFrom":sQuery(id+"F6.wireOp",EDGE,"E42.11.0.14")}),1.0]])]});
            var Q788;
            Q788=makeQuery(id+"F6.imprint","IMPRINT",FACE,{"disambiguationData":[TD([[makeQuery(id+"F6.imprint","IMPRINT",EDGE,{"derivedFrom":sQuery(id+"F6.wireOp",EDGE,"E716.MirrorC")}),-1.0]])]});
            var Q789;
            Q789=makeQuery(id+"F6.imprint","IMPRINT",FACE,{"disambiguationData":[TD([[makeQuery(id+"F6.imprint","IMPRINT",EDGE,{"derivedFrom":sQuery(id+"F6.wireOp",EDGE,"E42.10.0.22")}),1.0]])]});
            var Q790;
            Q790=makeQuery(id+"F6.imprint","IMPRINT",FACE,{"disambiguationData":[TD([[makeQuery(id+"F6.imprint","IMPRINT",EDGE,{"derivedFrom":sQuery(id+"F6.wireOp",EDGE,"E42.10.0.5")}),1.0]])]});
            var Q791;
            Q791=makeQuery(id+"F6.imprint","IMPRINT",FACE,{"disambiguationData":[TD([[makeQuery(id+"F6.imprint","IMPRINT",EDGE,{"derivedFrom":sQuery(id+"F6.wireOp",EDGE,"E42.14.0.22")}),1.0]])]});
            var Q792;
            Q792=makeQuery(id+"F6.imprint","IMPRINT",FACE,{"disambiguationData":[TD([[makeQuery(id+"F6.imprint","IMPRINT",EDGE,{"derivedFrom":sQuery(id+"F6.wireOp",EDGE,"E42.14.0.5")}),1.0]])]});
            var Q793;
            Q793=makeQuery(id+"F6.imprint","IMPRINT",FACE,{"disambiguationData":[TD([[makeQuery(id+"F6.imprint","IMPRINT",EDGE,{"derivedFrom":sQuery(id+"F6.wireOp",EDGE,"E42.13.0.14")}),1.0]])]});
            var Q794;
            Q794=makeQuery(id+"F6.imprint","IMPRINT",FACE,{"disambiguationData":[TD([[makeQuery(id+"F6.imprint","IMPRINT",EDGE,{"derivedFrom":sQuery(id+"F6.wireOp",EDGE,"E42.12.0.22")}),1.0]])]});
            var Q795;
            Q795=makeQuery(id+"F6.imprint","IMPRINT",FACE,{"disambiguationData":[TD([[makeQuery(id+"F6.imprint","IMPRINT",EDGE,{"derivedFrom":sQuery(id+"F6.wireOp",EDGE,"E455.MirrorC")}),-1.0]])]});
            var Q796;
            Q796=makeQuery(id+"F6.imprint","IMPRINT",FACE,{"disambiguationData":[TD([[makeQuery(id+"F6.imprint","IMPRINT",EDGE,{"derivedFrom":sQuery(id+"F6.wireOp",EDGE,"E42.16.0.22")}),1.0]])]});
            var Q797;
            Q797=makeQuery(id+"F6.imprint","IMPRINT",FACE,{"disambiguationData":[TD([[makeQuery(id+"F6.imprint","IMPRINT",EDGE,{"derivedFrom":sQuery(id+"F6.wireOp",EDGE,"E42.16.0.5")}),1.0]])]});
            var Q798;
            Q798=makeQuery(id+"F6.imprint","IMPRINT",FACE,{"disambiguationData":[TD([[makeQuery(id+"F6.imprint","IMPRINT",EDGE,{"derivedFrom":sQuery(id+"F6.wireOp",EDGE,"E42.15.0.14")}),1.0]])]});
            var Q799;
            Q799=makeQuery(id+"F6.imprint","IMPRINT",FACE,{"disambiguationData":[TD([[makeQuery(id+"F6.imprint","IMPRINT",EDGE,{"derivedFrom":sQuery(id+"F6.wireOp",EDGE,"E403.MirrorC")}),-1.0]])]});
            var Q800;
            Q800=makeQuery(id+"F6.imprint","IMPRINT",FACE,{"disambiguationData":[TD([[makeQuery(id+"F6.imprint","IMPRINT",EDGE,{"derivedFrom":sQuery(id+"F6.wireOp",EDGE,"E42.18.0.22")}),1.0]])]});
            var Q801;
            Q801=makeQuery(id+"F6.imprint","IMPRINT",FACE,{"disambiguationData":[TD([[makeQuery(id+"F6.imprint","IMPRINT",EDGE,{"derivedFrom":sQuery(id+"F6.wireOp",EDGE,"E42.18.0.5")}),1.0]])]});
            var Q802;
            Q802=makeQuery(id+"F6.imprint","IMPRINT",FACE,{"disambiguationData":[TD([[makeQuery(id+"F6.imprint","IMPRINT",EDGE,{"derivedFrom":sQuery(id+"F6.wireOp",EDGE,"E42.17.0.14")}),1.0]])]});
            var Q803;
            Q803=makeQuery(id+"F6.imprint","IMPRINT",FACE,{"disambiguationData":[TD([[makeQuery(id+"F6.imprint","IMPRINT",EDGE,{"derivedFrom":sQuery(id+"F6.wireOp",EDGE,"E42.21.0.14")}),1.0]])]});
            var Q804;
            Q804=makeQuery(id+"F6.imprint","IMPRINT",FACE,{"disambiguationData":[TD([[makeQuery(id+"F6.imprint","IMPRINT",EDGE,{"derivedFrom":sQuery(id+"F6.wireOp",EDGE,"E42.20.0.22")}),1.0]])]});
            var Q805;
            Q805=makeQuery(id+"F6.imprint","IMPRINT",FACE,{"disambiguationData":[TD([[makeQuery(id+"F6.imprint","IMPRINT",EDGE,{"derivedFrom":sQuery(id+"F6.wireOp",EDGE,"E42.20.0.5")}),1.0]])]});
            var Q806;
            Q806=makeQuery(id+"F6.imprint","IMPRINT",FACE,{"disambiguationData":[TD([[makeQuery(id+"F6.imprint","IMPRINT",EDGE,{"derivedFrom":sQuery(id+"F6.wireOp",EDGE,"E42.19.0.14")}),1.0]])]});
            var Q807;
            Q807=makeQuery(id+"F6.imprint","IMPRINT",FACE,{"disambiguationData":[TD([[makeQuery(id+"F6.imprint","IMPRINT",EDGE,{"derivedFrom":sQuery(id+"F6.wireOp",EDGE,"E328.MirrorC")}),-1.0]])]});
            var Q808;
            Q808=makeQuery(id+"F6.imprint","IMPRINT",FACE,{"disambiguationData":[TD([[makeQuery(id+"F6.imprint","IMPRINT",EDGE,{"derivedFrom":sQuery(id+"F6.wireOp",EDGE,"E265.MirrorC")}),-1.0]])]});
            var Q809;
            Q809=makeQuery(id+"F6.imprint","IMPRINT",FACE,{"disambiguationData":[TD([[makeQuery(id+"F6.imprint","IMPRINT",EDGE,{"derivedFrom":sQuery(id+"F6.wireOp",EDGE,"E670.MirrorC")}),-1.0]])]});
            var Q810;
            Q810=makeQuery(id+"F6.imprint","IMPRINT",FACE,{"disambiguationData":[TD([[makeQuery(id+"F6.imprint","IMPRINT",EDGE,{"derivedFrom":sQuery(id+"F6.wireOp",EDGE,"E251.MirrorC")}),-1.0]])]});
            var Q811;
            Q811=makeQuery(id+"F6.imprint","IMPRINT",FACE,{"disambiguationData":[TD([[makeQuery(id+"F6.imprint","IMPRINT",EDGE,{"derivedFrom":sQuery(id+"F6.wireOp",EDGE,"E297.MirrorC")}),-1.0]])]});
            var Q812;
            Q812=makeQuery(id+"F6.imprint","IMPRINT",FACE,{"disambiguationData":[TD([[makeQuery(id+"F6.imprint","IMPRINT",EDGE,{"derivedFrom":sQuery(id+"F6.wireOp",EDGE,"E281.MirrorC")}),-1.0]])]});
            var Q813;
            Q813=makeQuery(id+"F6.imprint","IMPRINT",FACE,{"disambiguationData":[TD([[makeQuery(id+"F6.imprint","IMPRINT",EDGE,{"derivedFrom":sQuery(id+"F6.wireOp",EDGE,"E603.MirrorC")}),-1.0]])]});
            var Q814;
            Q814=makeQuery(id+"F6.imprint","IMPRINT",FACE,{"disambiguationData":[TD([[makeQuery(id+"F6.imprint","IMPRINT",EDGE,{"derivedFrom":sQuery(id+"F6.wireOp",EDGE,"E42.1.0.15")}),1.0]])]});
            var Q815;
            Q815=makeQuery(id+"F6.imprint","IMPRINT",FACE,{"disambiguationData":[TD([[makeQuery(id+"F6.imprint","IMPRINT",EDGE,{"derivedFrom":sQuery(id+"F6.wireOp",EDGE,"E41.0.8.0")}),1.0]])]});
            var Q816;
            Q816=makeQuery(id+"F6.imprint","IMPRINT",FACE,{"disambiguationData":[TD([[makeQuery(id+"F6.imprint","IMPRINT",EDGE,{"derivedFrom":sQuery(id+"F6.wireOp",EDGE,"E655.MirrorC")}),-1.0]])]});
            var Q817;
            Q817=makeQuery(id+"F6.imprint","IMPRINT",FACE,{"disambiguationData":[TD([[makeQuery(id+"F6.imprint","IMPRINT",EDGE,{"derivedFrom":sQuery(id+"F6.wireOp",EDGE,"E42.4.0.6")}),1.0]])]});
            var Q818;
            Q818=makeQuery(id+"F6.imprint","IMPRINT",FACE,{"disambiguationData":[TD([[makeQuery(id+"F6.imprint","IMPRINT",EDGE,{"derivedFrom":sQuery(id+"F6.wireOp",EDGE,"E42.3.0.15")}),1.0]])]});
            var Q819;
            Q819=makeQuery(id+"F6.imprint","IMPRINT",FACE,{"disambiguationData":[TD([[makeQuery(id+"F6.imprint","IMPRINT",EDGE,{"derivedFrom":sQuery(id+"F6.wireOp",EDGE,"E42.2.0.6")}),1.0]])]});
            var Q820;
            Q820=makeQuery(id+"F6.imprint","IMPRINT",FACE,{"disambiguationData":[TD([[makeQuery(id+"F6.imprint","IMPRINT",EDGE,{"derivedFrom":sQuery(id+"F6.wireOp",EDGE,"E357.MirrorC")}),-1.0]])]});
            var Q821;
            Q821=makeQuery(id+"F6.imprint","IMPRINT",FACE,{"disambiguationData":[TD([[makeQuery(id+"F6.imprint","IMPRINT",EDGE,{"derivedFrom":sQuery(id+"F6.wireOp",EDGE,"E409.MirrorC")}),-1.0]])]});
            var Q822;
            Q822=makeQuery(id+"F6.imprint","IMPRINT",FACE,{"disambiguationData":[TD([[makeQuery(id+"F6.imprint","IMPRINT",EDGE,{"derivedFrom":sQuery(id+"F6.wireOp",EDGE,"E42.6.0.6")}),1.0]])]});
            var Q823;
            Q823=makeQuery(id+"F6.imprint","IMPRINT",FACE,{"disambiguationData":[TD([[makeQuery(id+"F6.imprint","IMPRINT",EDGE,{"derivedFrom":sQuery(id+"F6.wireOp",EDGE,"E42.5.0.15")}),1.0]])]});
            var Q824;
            Q824=makeQuery(id+"F6.imprint","IMPRINT",FACE,{"disambiguationData":[TD([[makeQuery(id+"F6.imprint","IMPRINT",EDGE,{"derivedFrom":sQuery(id+"F6.wireOp",EDGE,"E686.MirrorC")}),-1.0]])]});
            var Q825;
            Q825=makeQuery(id+"F6.imprint","IMPRINT",FACE,{"disambiguationData":[TD([[makeQuery(id+"F6.imprint","IMPRINT",EDGE,{"derivedFrom":sQuery(id+"F6.wireOp",EDGE,"E633.MirrorC")}),-1.0]])]});
            var Q826;
            Q826=makeQuery(id+"F6.imprint","IMPRINT",FACE,{"disambiguationData":[TD([[makeQuery(id+"F6.imprint","IMPRINT",EDGE,{"derivedFrom":sQuery(id+"F6.wireOp",EDGE,"E424.MirrorC")}),-1.0]])]});
            var Q827;
            Q827=makeQuery(id+"F6.imprint","IMPRINT",FACE,{"disambiguationData":[TD([[makeQuery(id+"F6.imprint","IMPRINT",EDGE,{"derivedFrom":sQuery(id+"F6.wireOp",EDGE,"E618.MirrorC")}),-1.0]])]});
            var Q828;
            Q828=makeQuery(id+"F6.imprint","IMPRINT",FACE,{"disambiguationData":[TD([[makeQuery(id+"F6.imprint","IMPRINT",EDGE,{"derivedFrom":sQuery(id+"F6.wireOp",EDGE,"E313.MirrorC")}),-1.0]])]});
            var Q829;
            Q829=makeQuery(id+"F6.imprint","IMPRINT",FACE,{"disambiguationData":[TD([[makeQuery(id+"F6.imprint","IMPRINT",EDGE,{"derivedFrom":sQuery(id+"F6.wireOp",EDGE,"E372.MirrorC")}),-1.0]])]});
            var Q830;
            Q830=makeQuery(id+"F6.imprint","IMPRINT",FACE,{"disambiguationData":[TD([[makeQuery(id+"F6.imprint","IMPRINT",EDGE,{"derivedFrom":sQuery(id+"F6.wireOp",EDGE,"E42.26.0.6")}),1.0]])]});
            var Q831;
            Q831=makeQuery(id+"F6.imprint","IMPRINT",FACE,{"disambiguationData":[TD([[makeQuery(id+"F6.imprint","IMPRINT",EDGE,{"derivedFrom":sQuery(id+"F6.wireOp",EDGE,"E42.25.0.15")}),1.0]])]});
            var Q832;
            Q832=makeQuery(id+"F6.imprint","IMPRINT",FACE,{"disambiguationData":[TD([[makeQuery(id+"F6.imprint","IMPRINT",EDGE,{"derivedFrom":sQuery(id+"F6.wireOp",EDGE,"E42.29.0.15")}),1.0]])]});
            var Q833;
            Q833=makeQuery(id+"F6.imprint","IMPRINT",FACE,{"disambiguationData":[TD([[makeQuery(id+"F6.imprint","IMPRINT",EDGE,{"derivedFrom":sQuery(id+"F6.wireOp",EDGE,"E42.28.0.6")}),1.0]])]});
            var Q834;
            Q834=makeQuery(id+"F6.imprint","IMPRINT",FACE,{"disambiguationData":[TD([[makeQuery(id+"F6.imprint","IMPRINT",EDGE,{"derivedFrom":sQuery(id+"F6.wireOp",EDGE,"E42.27.0.15")}),1.0]])]});
            var Q835;
            Q835=makeQuery(id+"F6.imprint","IMPRINT",FACE,{"disambiguationData":[TD([[makeQuery(id+"F6.imprint","IMPRINT",EDGE,{"derivedFrom":sQuery(id+"F6.wireOp",EDGE,"E42.32.0.6")}),1.0]])]});
            var Q836;
            Q836=makeQuery(id+"F6.imprint","IMPRINT",FACE,{"disambiguationData":[TD([[makeQuery(id+"F6.imprint","IMPRINT",EDGE,{"derivedFrom":sQuery(id+"F6.wireOp",EDGE,"E42.31.0.15")}),1.0]])]});
            var Q837;
            Q837=makeQuery(id+"F6.imprint","IMPRINT",FACE,{"disambiguationData":[TD([[makeQuery(id+"F6.imprint","IMPRINT",EDGE,{"derivedFrom":sQuery(id+"F6.wireOp",EDGE,"E42.30.0.6")}),1.0]])]});
            var Q838;
            Q838=makeQuery(id+"F6.imprint","IMPRINT",FACE,{"disambiguationData":[TD([[makeQuery(id+"F6.imprint","IMPRINT",EDGE,{"derivedFrom":sQuery(id+"F6.wireOp",EDGE,"E709.MirrorC")}),-1.0]])]});
            var Q839;
            Q839=makeQuery(id+"F6.imprint","IMPRINT",FACE,{"disambiguationData":[TD([[makeQuery(id+"F6.imprint","IMPRINT",EDGE,{"derivedFrom":sQuery(id+"F6.wireOp",EDGE,"E501.MirrorC")}),-1.0]])]});
            var Q840;
            Q840=makeQuery(id+"F6.imprint","IMPRINT",FACE,{"disambiguationData":[TD([[makeQuery(id+"F6.imprint","IMPRINT",EDGE,{"derivedFrom":sQuery(id+"F6.wireOp",EDGE,"E42.9.0.15")}),1.0]])]});
            var Q841;
            Q841=makeQuery(id+"F6.imprint","IMPRINT",FACE,{"disambiguationData":[TD([[makeQuery(id+"F6.imprint","IMPRINT",EDGE,{"derivedFrom":sQuery(id+"F6.wireOp",EDGE,"E42.8.0.6")}),1.0]])]});
            var Q842;
            Q842=makeQuery(id+"F6.imprint","IMPRINT",FACE,{"disambiguationData":[TD([[makeQuery(id+"F6.imprint","IMPRINT",EDGE,{"derivedFrom":sQuery(id+"F6.wireOp",EDGE,"E42.7.0.15")}),1.0]])]});
            var Q843;
            Q843=makeQuery(id+"F6.imprint","IMPRINT",FACE,{"disambiguationData":[TD([[makeQuery(id+"F6.imprint","IMPRINT",EDGE,{"derivedFrom":sQuery(id+"F6.wireOp",EDGE,"E42.12.0.6")}),1.0]])]});
            var Q844;
            Q844=makeQuery(id+"F6.imprint","IMPRINT",FACE,{"disambiguationData":[TD([[makeQuery(id+"F6.imprint","IMPRINT",EDGE,{"derivedFrom":sQuery(id+"F6.wireOp",EDGE,"E42.11.0.15")}),1.0]])]});
            var Q845;
            Q845=makeQuery(id+"F6.imprint","IMPRINT",FACE,{"disambiguationData":[TD([[makeQuery(id+"F6.imprint","IMPRINT",EDGE,{"derivedFrom":sQuery(id+"F6.wireOp",EDGE,"E42.10.0.6")}),1.0]])]});
            var Q846;
            Q846=makeQuery(id+"F6.imprint","IMPRINT",FACE,{"disambiguationData":[TD([[makeQuery(id+"F6.imprint","IMPRINT",EDGE,{"derivedFrom":sQuery(id+"F6.wireOp",EDGE,"E42.14.0.6")}),1.0]])]});
            var Q847;
            Q847=makeQuery(id+"F6.imprint","IMPRINT",FACE,{"disambiguationData":[TD([[makeQuery(id+"F6.imprint","IMPRINT",EDGE,{"derivedFrom":sQuery(id+"F6.wireOp",EDGE,"E42.13.0.15")}),1.0]])]});
            var Q848;
            Q848=makeQuery(id+"F6.imprint","IMPRINT",FACE,{"disambiguationData":[TD([[makeQuery(id+"F6.imprint","IMPRINT",EDGE,{"derivedFrom":sQuery(id+"F6.wireOp",EDGE,"E725.MirrorC")}),-1.0]])]});
            var Q849;
            Q849=makeQuery(id+"F6.imprint","IMPRINT",FACE,{"disambiguationData":[TD([[makeQuery(id+"F6.imprint","IMPRINT",EDGE,{"derivedFrom":sQuery(id+"F6.wireOp",EDGE,"E42.16.0.6")}),1.0]])]});
            var Q850;
            Q850=makeQuery(id+"F6.imprint","IMPRINT",FACE,{"disambiguationData":[TD([[makeQuery(id+"F6.imprint","IMPRINT",EDGE,{"derivedFrom":sQuery(id+"F6.wireOp",EDGE,"E42.15.0.15")}),1.0]])]});
            var Q851;
            Q851=makeQuery(id+"F6.imprint","IMPRINT",FACE,{"disambiguationData":[TD([[makeQuery(id+"F6.imprint","IMPRINT",EDGE,{"derivedFrom":sQuery(id+"F6.wireOp",EDGE,"E516.MirrorC")}),-1.0]])]});
            var Q852;
            Q852=makeQuery(id+"F6.imprint","IMPRINT",FACE,{"disambiguationData":[TD([[makeQuery(id+"F6.imprint","IMPRINT",EDGE,{"derivedFrom":sQuery(id+"F6.wireOp",EDGE,"E42.18.0.6")}),1.0]])]});
            var Q853;
            Q853=makeQuery(id+"F6.imprint","IMPRINT",FACE,{"disambiguationData":[TD([[makeQuery(id+"F6.imprint","IMPRINT",EDGE,{"derivedFrom":sQuery(id+"F6.wireOp",EDGE,"E42.17.0.15")}),1.0]])]});
            var Q854;
            Q854=makeQuery(id+"F6.imprint","IMPRINT",FACE,{"disambiguationData":[TD([[makeQuery(id+"F6.imprint","IMPRINT",EDGE,{"derivedFrom":sQuery(id+"F6.wireOp",EDGE,"E464.MirrorC")}),-1.0]])]});
            var Q855;
            Q855=makeQuery(id+"F6.imprint","IMPRINT",FACE,{"disambiguationData":[TD([[makeQuery(id+"F6.imprint","IMPRINT",EDGE,{"derivedFrom":sQuery(id+"F6.wireOp",EDGE,"E42.21.0.15")}),1.0]])]});
            var Q856;
            Q856=makeQuery(id+"F6.imprint","IMPRINT",FACE,{"disambiguationData":[TD([[makeQuery(id+"F6.imprint","IMPRINT",EDGE,{"derivedFrom":sQuery(id+"F6.wireOp",EDGE,"E42.20.0.6")}),1.0]])]});
            var Q857;
            Q857=makeQuery(id+"F6.imprint","IMPRINT",FACE,{"disambiguationData":[TD([[makeQuery(id+"F6.imprint","IMPRINT",EDGE,{"derivedFrom":sQuery(id+"F6.wireOp",EDGE,"E42.19.0.15")}),1.0]])]});
            var Q858;
            Q858=makeQuery(id+"F6.imprint","IMPRINT",FACE,{"disambiguationData":[TD([[makeQuery(id+"F6.imprint","IMPRINT",EDGE,{"derivedFrom":sQuery(id+"F6.wireOp",EDGE,"E42.24.0.6")}),1.0]])]});
            var Q859;
            Q859=makeQuery(id+"F6.imprint","IMPRINT",FACE,{"disambiguationData":[TD([[makeQuery(id+"F6.imprint","IMPRINT",EDGE,{"derivedFrom":sQuery(id+"F6.wireOp",EDGE,"E42.23.0.15")}),1.0]])]});
            var Q860;
            Q860=makeQuery(id+"F6.imprint","IMPRINT",FACE,{"disambiguationData":[TD([[makeQuery(id+"F6.imprint","IMPRINT",EDGE,{"derivedFrom":sQuery(id+"F6.wireOp",EDGE,"E42.22.0.6")}),1.0]])]});
            var Q861;
            Q861=makeQuery(id+"F6.imprint","IMPRINT",FACE,{"disambiguationData":[TD([[makeQuery(id+"F6.imprint","IMPRINT",EDGE,{"derivedFrom":sQuery(id+"F6.wireOp",EDGE,"E266.MirrorC")}),-1.0]])]});
            var Q862;
            Q862=makeQuery(id+"F6.imprint","IMPRINT",FACE,{"disambiguationData":[TD([[makeQuery(id+"F6.imprint","IMPRINT",EDGE,{"derivedFrom":sQuery(id+"F6.wireOp",EDGE,"E252.MirrorC")}),-1.0]])]});
            var Q863;
            Q863=makeQuery(id+"F6.imprint","IMPRINT",FACE,{"disambiguationData":[TD([[makeQuery(id+"F6.imprint","IMPRINT",EDGE,{"derivedFrom":sQuery(id+"F6.wireOp",EDGE,"E679.MirrorC")}),-1.0]])]});
            var Q864;
            Q864=makeQuery(id+"F6.imprint","IMPRINT",FACE,{"disambiguationData":[TD([[makeQuery(id+"F6.imprint","IMPRINT",EDGE,{"derivedFrom":sQuery(id+"F6.wireOp",EDGE,"E298.MirrorC")}),-1.0]])]});
            var Q865;
            Q865=makeQuery(id+"F6.imprint","IMPRINT",FACE,{"disambiguationData":[TD([[makeQuery(id+"F6.imprint","IMPRINT",EDGE,{"derivedFrom":sQuery(id+"F6.wireOp",EDGE,"E282.MirrorC")}),-1.0]])]});
            var Q866;
            Q866=makeQuery(id+"F6.imprint","IMPRINT",FACE,{"disambiguationData":[TD([[makeQuery(id+"F6.imprint","IMPRINT",EDGE,{"derivedFrom":sQuery(id+"F6.wireOp",EDGE,"E418.MirrorC")}),-1.0]])]});
            var Q867;
            Q867=makeQuery(id+"F6.imprint","IMPRINT",FACE,{"disambiguationData":[TD([[makeQuery(id+"F6.imprint","IMPRINT",EDGE,{"derivedFrom":sQuery(id+"F6.wireOp",EDGE,"E42.1.0.16")}),1.0]])]});
            var Q868;
            Q868=makeQuery(id+"F6.imprint","IMPRINT",FACE,{"disambiguationData":[TD([[makeQuery(id+"F6.imprint","IMPRINT",EDGE,{"derivedFrom":sQuery(id+"F6.wireOp",EDGE,"E470.MirrorC")}),-1.0]])]});
            var Q869;
            Q869=makeQuery(id+"F6.imprint","IMPRINT",FACE,{"disambiguationData":[TD([[makeQuery(id+"F6.imprint","IMPRINT",EDGE,{"derivedFrom":sQuery(id+"F6.wireOp",EDGE,"E41.0.9.0")}),1.0]])]});
            var Q870;
            Q870=makeQuery(id+"F6.imprint","IMPRINT",FACE,{"disambiguationData":[TD([[makeQuery(id+"F6.imprint","IMPRINT",EDGE,{"derivedFrom":sQuery(id+"F6.wireOp",EDGE,"E42.4.0.7")}),1.0]])]});
            var Q871;
            Q871=makeQuery(id+"F6.imprint","IMPRINT",FACE,{"disambiguationData":[TD([[makeQuery(id+"F6.imprint","IMPRINT",EDGE,{"derivedFrom":sQuery(id+"F6.wireOp",EDGE,"E42.3.0.16")}),1.0]])]});
            var Q872;
            Q872=makeQuery(id+"F6.imprint","IMPRINT",FACE,{"disambiguationData":[TD([[makeQuery(id+"F6.imprint","IMPRINT",EDGE,{"derivedFrom":sQuery(id+"F6.wireOp",EDGE,"E42.2.0.7")}),1.0]])]});
            var Q873;
            Q873=makeQuery(id+"F6.imprint","IMPRINT",FACE,{"disambiguationData":[TD([[makeQuery(id+"F6.imprint","IMPRINT",EDGE,{"derivedFrom":sQuery(id+"F6.wireOp",EDGE,"E42.6.0.7")}),1.0]])]});
            var Q874;
            Q874=makeQuery(id+"F6.imprint","IMPRINT",FACE,{"disambiguationData":[TD([[makeQuery(id+"F6.imprint","IMPRINT",EDGE,{"derivedFrom":sQuery(id+"F6.wireOp",EDGE,"E42.5.0.16")}),1.0]])]});
            var Q875;
            Q875=makeQuery(id+"F6.imprint","IMPRINT",FACE,{"disambiguationData":[TD([[makeQuery(id+"F6.imprint","IMPRINT",EDGE,{"derivedFrom":sQuery(id+"F6.wireOp",EDGE,"E42.9.0.16")}),1.0]])]});
            var Q876;
            Q876=makeQuery(id+"F6.imprint","IMPRINT",FACE,{"disambiguationData":[TD([[makeQuery(id+"F6.imprint","IMPRINT",EDGE,{"derivedFrom":sQuery(id+"F6.wireOp",EDGE,"E42.8.0.7")}),1.0]])]});
            var Q877;
            Q877=makeQuery(id+"F6.imprint","IMPRINT",FACE,{"disambiguationData":[TD([[makeQuery(id+"F6.imprint","IMPRINT",EDGE,{"derivedFrom":sQuery(id+"F6.wireOp",EDGE,"E42.7.0.16")}),1.0]])]});
            var Q878;
            Q878=makeQuery(id+"F6.imprint","IMPRINT",FACE,{"disambiguationData":[TD([[makeQuery(id+"F6.imprint","IMPRINT",EDGE,{"derivedFrom":sQuery(id+"F6.wireOp",EDGE,"E694.MirrorC")}),-1.0]])]});
            var Q879;
            Q879=makeQuery(id+"F6.imprint","IMPRINT",FACE,{"disambiguationData":[TD([[makeQuery(id+"F6.imprint","IMPRINT",EDGE,{"derivedFrom":sQuery(id+"F6.wireOp",EDGE,"E433.MirrorC")}),-1.0]])]});
            var Q880;
            Q880=makeQuery(id+"F6.imprint","IMPRINT",FACE,{"disambiguationData":[TD([[makeQuery(id+"F6.imprint","IMPRINT",EDGE,{"derivedFrom":sQuery(id+"F6.wireOp",EDGE,"E486.MirrorC")}),-1.0]])]});
            var Q881;
            Q881=makeQuery(id+"F6.imprint","IMPRINT",FACE,{"disambiguationData":[TD([[makeQuery(id+"F6.imprint","IMPRINT",EDGE,{"derivedFrom":sQuery(id+"F6.wireOp",EDGE,"E314.MirrorC")}),-1.0]])]});
            var Q882;
            Q882=makeQuery(id+"F6.imprint","IMPRINT",FACE,{"disambiguationData":[TD([[makeQuery(id+"F6.imprint","IMPRINT",EDGE,{"derivedFrom":sQuery(id+"F6.wireOp",EDGE,"E329.MirrorC")}),-1.0]])]});
            var Q883;
            Q883=makeQuery(id+"F6.imprint","IMPRINT",FACE,{"disambiguationData":[TD([[makeQuery(id+"F6.imprint","IMPRINT",EDGE,{"derivedFrom":sQuery(id+"F6.wireOp",EDGE,"E42.29.0.16")}),1.0]])]});
            var Q884;
            Q884=makeQuery(id+"F6.imprint","IMPRINT",FACE,{"disambiguationData":[TD([[makeQuery(id+"F6.imprint","IMPRINT",EDGE,{"derivedFrom":sQuery(id+"F6.wireOp",EDGE,"E42.28.0.7")}),1.0]])]});
            var Q885;
            Q885=makeQuery(id+"F6.imprint","IMPRINT",FACE,{"disambiguationData":[TD([[makeQuery(id+"F6.imprint","IMPRINT",EDGE,{"derivedFrom":sQuery(id+"F6.wireOp",EDGE,"E42.27.0.16")}),1.0]])]});
            var Q886;
            Q886=makeQuery(id+"F6.imprint","IMPRINT",FACE,{"disambiguationData":[TD([[makeQuery(id+"F6.imprint","IMPRINT",EDGE,{"derivedFrom":sQuery(id+"F6.wireOp",EDGE,"E42.32.0.7")}),1.0]])]});
            var Q887;
            Q887=makeQuery(id+"F6.imprint","IMPRINT",FACE,{"disambiguationData":[TD([[makeQuery(id+"F6.imprint","IMPRINT",EDGE,{"derivedFrom":sQuery(id+"F6.wireOp",EDGE,"E42.31.0.16")}),1.0]])]});
            var Q888;
            Q888=makeQuery(id+"F6.imprint","IMPRINT",FACE,{"disambiguationData":[TD([[makeQuery(id+"F6.imprint","IMPRINT",EDGE,{"derivedFrom":sQuery(id+"F6.wireOp",EDGE,"E42.30.0.7")}),1.0]])]});
            var Q889;
            Q889=makeQuery(id+"F6.imprint","IMPRINT",FACE,{"disambiguationData":[TD([[makeQuery(id+"F6.imprint","IMPRINT",EDGE,{"derivedFrom":sQuery(id+"F6.wireOp",EDGE,"E578.MirrorC")}),-1.0]])]});
            var Q890;
            Q890=makeQuery(id+"F6.imprint","IMPRINT",FACE,{"disambiguationData":[TD([[makeQuery(id+"F6.imprint","IMPRINT",EDGE,{"derivedFrom":sQuery(id+"F6.wireOp",EDGE,"E525.MirrorC")}),-1.0]])]});
            var Q891;
            Q891=makeQuery(id+"F6.imprint","IMPRINT",FACE,{"disambiguationData":[TD([[makeQuery(id+"F6.imprint","IMPRINT",EDGE,{"derivedFrom":sQuery(id+"F6.wireOp",EDGE,"E42.12.0.7")}),1.0]])]});
            var Q892;
            Q892=makeQuery(id+"F6.imprint","IMPRINT",FACE,{"disambiguationData":[TD([[makeQuery(id+"F6.imprint","IMPRINT",EDGE,{"derivedFrom":sQuery(id+"F6.wireOp",EDGE,"E42.11.0.16")}),1.0]])]});
            var Q893;
            Q893=makeQuery(id+"F6.imprint","IMPRINT",FACE,{"disambiguationData":[TD([[makeQuery(id+"F6.imprint","IMPRINT",EDGE,{"derivedFrom":sQuery(id+"F6.wireOp",EDGE,"E747.MirrorC")}),-1.0]])]});
            var Q894;
            Q894=makeQuery(id+"F6.imprint","IMPRINT",FACE,{"disambiguationData":[TD([[makeQuery(id+"F6.imprint","IMPRINT",EDGE,{"derivedFrom":sQuery(id+"F6.wireOp",EDGE,"E42.10.0.7")}),1.0]])]});
            var Q895;
            Q895=makeQuery(id+"F6.imprint","IMPRINT",FACE,{"disambiguationData":[TD([[makeQuery(id+"F6.imprint","IMPRINT",EDGE,{"derivedFrom":sQuery(id+"F6.wireOp",EDGE,"E42.14.0.7")}),1.0]])]});
            var Q896;
            Q896=makeQuery(id+"F6.imprint","IMPRINT",FACE,{"disambiguationData":[TD([[makeQuery(id+"F6.imprint","IMPRINT",EDGE,{"derivedFrom":sQuery(id+"F6.wireOp",EDGE,"E42.13.0.16")}),1.0]])]});
            var Q897;
            Q897=makeQuery(id+"F6.imprint","IMPRINT",FACE,{"disambiguationData":[TD([[makeQuery(id+"F6.imprint","IMPRINT",EDGE,{"derivedFrom":sQuery(id+"F6.wireOp",EDGE,"E541.MirrorC")}),-1.0]])]});
            var Q898;
            Q898=makeQuery(id+"F6.imprint","IMPRINT",FACE,{"disambiguationData":[TD([[makeQuery(id+"F6.imprint","IMPRINT",EDGE,{"derivedFrom":sQuery(id+"F6.wireOp",EDGE,"E593.MirrorC")}),-1.0]])]});
            var Q899;
            Q899=makeQuery(id+"F6.imprint","IMPRINT",FACE,{"disambiguationData":[TD([[makeQuery(id+"F6.imprint","IMPRINT",EDGE,{"derivedFrom":sQuery(id+"F6.wireOp",EDGE,"E42.16.0.7")}),1.0]])]});
            var Q900;
            Q900=makeQuery(id+"F6.imprint","IMPRINT",FACE,{"disambiguationData":[TD([[makeQuery(id+"F6.imprint","IMPRINT",EDGE,{"derivedFrom":sQuery(id+"F6.wireOp",EDGE,"E42.15.0.16")}),1.0]])]});
            var Q901;
            Q901=makeQuery(id+"F6.imprint","IMPRINT",FACE,{"disambiguationData":[TD([[makeQuery(id+"F6.imprint","IMPRINT",EDGE,{"derivedFrom":sQuery(id+"F6.wireOp",EDGE,"E42.18.0.7")}),1.0]])]});
            var Q902;
            Q902=makeQuery(id+"F6.imprint","IMPRINT",FACE,{"disambiguationData":[TD([[makeQuery(id+"F6.imprint","IMPRINT",EDGE,{"derivedFrom":sQuery(id+"F6.wireOp",EDGE,"E42.17.0.16")}),1.0]])]});
            var Q903;
            Q903=makeQuery(id+"F6.imprint","IMPRINT",FACE,{"disambiguationData":[TD([[makeQuery(id+"F6.imprint","IMPRINT",EDGE,{"derivedFrom":sQuery(id+"F6.wireOp",EDGE,"E42.21.0.16")}),1.0]])]});
            var Q904;
            Q904=makeQuery(id+"F6.imprint","IMPRINT",FACE,{"disambiguationData":[TD([[makeQuery(id+"F6.imprint","IMPRINT",EDGE,{"derivedFrom":sQuery(id+"F6.wireOp",EDGE,"E42.20.0.7")}),1.0]])]});
            var Q905;
            Q905=makeQuery(id+"F6.imprint","IMPRINT",FACE,{"disambiguationData":[TD([[makeQuery(id+"F6.imprint","IMPRINT",EDGE,{"derivedFrom":sQuery(id+"F6.wireOp",EDGE,"E42.19.0.16")}),1.0]])]});
            var Q906;
            Q906=makeQuery(id+"F6.imprint","IMPRINT",FACE,{"disambiguationData":[TD([[makeQuery(id+"F6.imprint","IMPRINT",EDGE,{"derivedFrom":sQuery(id+"F6.wireOp",EDGE,"E42.24.0.7")}),1.0]])]});
            var Q907;
            Q907=makeQuery(id+"F6.imprint","IMPRINT",FACE,{"disambiguationData":[TD([[makeQuery(id+"F6.imprint","IMPRINT",EDGE,{"derivedFrom":sQuery(id+"F6.wireOp",EDGE,"E42.23.0.16")}),1.0]])]});
            var Q908;
            Q908=makeQuery(id+"F6.imprint","IMPRINT",FACE,{"disambiguationData":[TD([[makeQuery(id+"F6.imprint","IMPRINT",EDGE,{"derivedFrom":sQuery(id+"F6.wireOp",EDGE,"E42.22.0.7")}),1.0]])]});
            var Q909;
            Q909=makeQuery(id+"F6.imprint","IMPRINT",FACE,{"disambiguationData":[TD([[makeQuery(id+"F6.imprint","IMPRINT",EDGE,{"derivedFrom":sQuery(id+"F6.wireOp",EDGE,"E42.26.0.7")}),1.0]])]});
            var Q910;
            Q910=makeQuery(id+"F6.imprint","IMPRINT",FACE,{"disambiguationData":[TD([[makeQuery(id+"F6.imprint","IMPRINT",EDGE,{"derivedFrom":sQuery(id+"F6.wireOp",EDGE,"E42.25.0.16")}),1.0]])]});
            var Q911;
            Q911=makeQuery(id+"F6.imprint","IMPRINT",FACE,{"disambiguationData":[TD([[makeQuery(id+"F6.imprint","IMPRINT",EDGE,{"derivedFrom":sQuery(id+"F6.wireOp",EDGE,"E547.MirrorC")}),-1.0]])]});
            var Q912;
            Q912=makeQuery(id+"F6.imprint","IMPRINT",FACE,{"disambiguationData":[TD([[makeQuery(id+"F6.imprint","IMPRINT",EDGE,{"derivedFrom":sQuery(id+"F6.wireOp",EDGE,"E479.MirrorC")}),-1.0]])]});
            var Q913;
            Q913=makeQuery(id+"F6.imprint","IMPRINT",FACE,{"disambiguationData":[TD([[makeQuery(id+"F6.imprint","IMPRINT",EDGE,{"derivedFrom":sQuery(id+"F6.wireOp",EDGE,"E532.MirrorC")}),-1.0]])]});
            var Q914;
            Q914=makeQuery(id+"F6.imprint","IMPRINT",FACE,{"disambiguationData":[TD([[makeQuery(id+"F6.imprint","IMPRINT",EDGE,{"derivedFrom":sQuery(id+"F6.wireOp",EDGE,"E509.MirrorC")}),-1.0]])]});
            var Q915;
            Q915=makeQuery(id+"F6.imprint","IMPRINT",FACE,{"disambiguationData":[TD([[makeQuery(id+"F6.imprint","IMPRINT",EDGE,{"derivedFrom":sQuery(id+"F6.wireOp",EDGE,"E562.MirrorC")}),-1.0]])]});
            var Q916;
            Q916=makeQuery(id+"F6.imprint","IMPRINT",FACE,{"disambiguationData":[TD([[makeQuery(id+"F6.imprint","IMPRINT",EDGE,{"derivedFrom":sQuery(id+"F6.wireOp",EDGE,"E495.MirrorC")}),-1.0]])]});
            var Q917;
            Q917=makeQuery(id+"F6.imprint","IMPRINT",FACE,{"disambiguationData":[TD([[makeQuery(id+"F6.imprint","IMPRINT",EDGE,{"derivedFrom":sQuery(id+"F6.wireOp",EDGE,"E792.MirrorC")}),-1.0]])]});
            var Q918;
            Q918=makeQuery(id+"F6.imprint","IMPRINT",FACE,{"disambiguationData":[TD([[makeQuery(id+"F6.imprint","IMPRINT",EDGE,{"derivedFrom":sQuery(id+"F6.wireOp",EDGE,"E740.MirrorC")}),-1.0]])]});
            var Q919;
            Q919=makeQuery(id+"F6.imprint","IMPRINT",FACE,{"disambiguationData":[TD([[makeQuery(id+"F6.imprint","IMPRINT",EDGE,{"derivedFrom":sQuery(id+"F6.wireOp",EDGE,"E638.MirrorC")}),-1.0]])]});
            var Q920;
            Q920=makeQuery(id+"F6.imprint","IMPRINT",FACE,{"disambiguationData":[TD([[makeQuery(id+"F6.imprint","IMPRINT",EDGE,{"derivedFrom":sQuery(id+"F6.wireOp",EDGE,"E587.MirrorC")}),-1.0]])]});
            var Q921;
            Q921=makeQuery(id+"F6.imprint","IMPRINT",FACE,{"disambiguationData":[TD([[makeQuery(id+"F6.imprint","IMPRINT",EDGE,{"derivedFrom":sQuery(id+"F6.wireOp",EDGE,"E377.MirrorC")}),-1.0]])]});
            var Q922;
            Q922=makeQuery(id+"F6.imprint","IMPRINT",FACE,{"disambiguationData":[TD([[makeQuery(id+"F6.imprint","IMPRINT",EDGE,{"derivedFrom":sQuery(id+"F6.wireOp",EDGE,"E755.MirrorC")}),-1.0]])]});
            var Q923;
            Q923=makeQuery(id+"F6.imprint","IMPRINT",FACE,{"disambiguationData":[TD([[makeQuery(id+"F6.imprint","IMPRINT",EDGE,{"derivedFrom":sQuery(id+"F6.wireOp",EDGE,"E808.MirrorC")}),-1.0]])]});
            var Q924;
            Q924=makeQuery(id+"F6.imprint","IMPRINT",FACE,{"disambiguationData":[TD([[makeQuery(id+"F6.imprint","IMPRINT",EDGE,{"derivedFrom":sQuery(id+"F6.wireOp",EDGE,"E601.MirrorC")}),-1.0]])]});
            var Q925;
            Q925=makeQuery(id+"F6.imprint","IMPRINT",FACE,{"disambiguationData":[TD([[makeQuery(id+"F6.imprint","IMPRINT",EDGE,{"derivedFrom":sQuery(id+"F6.wireOp",EDGE,"E653.MirrorC")}),-1.0]])]});
            var Q926;
            Q926=makeQuery(id+"F6.imprint","IMPRINT",FACE,{"disambiguationData":[TD([[makeQuery(id+"F6.imprint","IMPRINT",EDGE,{"derivedFrom":sQuery(id+"F6.wireOp",EDGE,"E393.MirrorC")}),-1.0]])]});
            var Q927;
            Q927=makeQuery(id+"F6.imprint","IMPRINT",FACE,{"disambiguationData":[TD([[makeQuery(id+"F6.imprint","IMPRINT",EDGE,{"derivedFrom":sQuery(id+"F6.wireOp",EDGE,"E762.MirrorC")}),-1.0]])]});
            var Q928;
            Q928=makeQuery(id+"F6.imprint","IMPRINT",FACE,{"disambiguationData":[TD([[makeQuery(id+"F6.imprint","IMPRINT",EDGE,{"derivedFrom":sQuery(id+"F6.wireOp",EDGE,"E556.MirrorC")}),-1.0]])]});
            var Q929;
            Q929=makeQuery(id+"F6.imprint","IMPRINT",FACE,{"disambiguationData":[TD([[makeQuery(id+"F6.imprint","IMPRINT",EDGE,{"derivedFrom":sQuery(id+"F6.wireOp",EDGE,"E608.MirrorC")}),-1.0]])]});
            var Q930;
            Q930=makeQuery(id+"F6.imprint","IMPRINT",FACE,{"disambiguationData":[TD([[makeQuery(id+"F6.imprint","IMPRINT",EDGE,{"derivedFrom":sQuery(id+"F6.wireOp",EDGE,"E347.MirrorC")}),-1.0]])]});
            var Q931;
            Q931=makeQuery(id+"F6.imprint","IMPRINT",FACE,{"disambiguationData":[TD([[makeQuery(id+"F6.imprint","IMPRINT",EDGE,{"derivedFrom":sQuery(id+"F6.wireOp",EDGE,"E777.MirrorC")}),-1.0]])]});
            var Q932;
            Q932=makeQuery(id+"F6.imprint","IMPRINT",FACE,{"disambiguationData":[TD([[makeQuery(id+"F6.imprint","IMPRINT",EDGE,{"derivedFrom":sQuery(id+"F6.wireOp",EDGE,"E571.MirrorC")}),-1.0]])]});
            var Q933;
            Q933=makeQuery(id+"F6.imprint","IMPRINT",FACE,{"disambiguationData":[TD([[makeQuery(id+"F6.imprint","IMPRINT",EDGE,{"derivedFrom":sQuery(id+"F6.wireOp",EDGE,"E623.MirrorC")}),-1.0]])]});
            var Q934;
            Q934=makeQuery(id+"F6.imprint","IMPRINT",FACE,{"disambiguationData":[TD([[makeQuery(id+"F6.imprint","IMPRINT",EDGE,{"derivedFrom":sQuery(id+"F6.wireOp",EDGE,"E361.MirrorC")}),-1.0]])]});
            var Q935;
            Q935=makeQuery(id+"F6.imprint","IMPRINT",FACE,{"disambiguationData":[TD([[makeQuery(id+"F6.imprint","IMPRINT",EDGE,{"derivedFrom":sQuery(id+"F6.wireOp",EDGE,"E699.MirrorC")}),-1.0]])]});
            var Q936;
            Q936=makeQuery(id+"F6.imprint","IMPRINT",FACE,{"disambiguationData":[TD([[makeQuery(id+"F6.imprint","IMPRINT",EDGE,{"derivedFrom":sQuery(id+"F6.wireOp",EDGE,"E646.MirrorC")}),-1.0]])]});
            var Q937;
            Q937=makeQuery(id+"F6.imprint","IMPRINT",FACE,{"disambiguationData":[TD([[makeQuery(id+"F6.imprint","IMPRINT",EDGE,{"derivedFrom":sQuery(id+"F6.wireOp",EDGE,"E453.MirrorC")}),-1.0]])]});
            var Q938;
            Q938=makeQuery(id+"F6.imprint","IMPRINT",FACE,{"disambiguationData":[TD([[makeQuery(id+"F6.imprint","IMPRINT",EDGE,{"derivedFrom":sQuery(id+"F6.wireOp",EDGE,"E42.2.0.8")}),1.0]])]});
            var Q939;
            Q939=makeQuery(id+"F6.imprint","IMPRINT",FACE,{"disambiguationData":[TD([[makeQuery(id+"F6.imprint","IMPRINT",EDGE,{"derivedFrom":sQuery(id+"F6.wireOp",EDGE,"E42.1.0.17")}),1.0]])]});
            var Q940;
            Q940=makeQuery(id+"F6.imprint","IMPRINT",FACE,{"disambiguationData":[TD([[makeQuery(id+"F6.imprint","IMPRINT",EDGE,{"derivedFrom":sQuery(id+"F6.wireOp",EDGE,"E41.0.10.0")}),1.0]])]});
            var Q941;
            Q941=makeQuery(id+"F6.imprint","IMPRINT",FACE,{"disambiguationData":[TD([[makeQuery(id+"F6.imprint","IMPRINT",EDGE,{"derivedFrom":sQuery(id+"F6.wireOp",EDGE,"E401.MirrorC")}),-1.0]])]});
            var Q942;
            Q942=makeQuery(id+"F6.imprint","IMPRINT",FACE,{"disambiguationData":[TD([[makeQuery(id+"F6.imprint","IMPRINT",EDGE,{"derivedFrom":sQuery(id+"F6.wireOp",EDGE,"E42.5.0.17")}),1.0]])]});
            var Q943;
            Q943=makeQuery(id+"F6.imprint","IMPRINT",FACE,{"disambiguationData":[TD([[makeQuery(id+"F6.imprint","IMPRINT",EDGE,{"derivedFrom":sQuery(id+"F6.wireOp",EDGE,"E42.4.0.8")}),1.0]])]});
            var Q944;
            Q944=makeQuery(id+"F6.imprint","IMPRINT",FACE,{"disambiguationData":[TD([[makeQuery(id+"F6.imprint","IMPRINT",EDGE,{"derivedFrom":sQuery(id+"F6.wireOp",EDGE,"E42.3.0.17")}),1.0]])]});
            var Q945;
            Q945=makeQuery(id+"F6.imprint","IMPRINT",FACE,{"disambiguationData":[TD([[makeQuery(id+"F6.imprint","IMPRINT",EDGE,{"derivedFrom":sQuery(id+"F6.wireOp",EDGE,"E42.8.0.8")}),1.0]])]});
            var Q946;
            Q946=makeQuery(id+"F6.imprint","IMPRINT",FACE,{"disambiguationData":[TD([[makeQuery(id+"F6.imprint","IMPRINT",EDGE,{"derivedFrom":sQuery(id+"F6.wireOp",EDGE,"E42.7.0.17")}),1.0]])]});
            var Q947;
            Q947=makeQuery(id+"F6.imprint","IMPRINT",FACE,{"disambiguationData":[TD([[makeQuery(id+"F6.imprint","IMPRINT",EDGE,{"derivedFrom":sQuery(id+"F6.wireOp",EDGE,"E42.6.0.8")}),1.0]])]});
            var Q948;
            Q948=makeQuery(id+"F6.imprint","IMPRINT",FACE,{"disambiguationData":[TD([[makeQuery(id+"F6.imprint","IMPRINT",EDGE,{"derivedFrom":sQuery(id+"F6.wireOp",EDGE,"E42.10.0.8")}),1.0]])]});
            var Q949;
            Q949=makeQuery(id+"F6.imprint","IMPRINT",FACE,{"disambiguationData":[TD([[makeQuery(id+"F6.imprint","IMPRINT",EDGE,{"derivedFrom":sQuery(id+"F6.wireOp",EDGE,"E42.9.0.17")}),1.0]])]});
            var Q950;
            Q950=makeQuery(id+"F6.imprint","IMPRINT",FACE,{"disambiguationData":[TD([[makeQuery(id+"F6.imprint","IMPRINT",EDGE,{"derivedFrom":sQuery(id+"F6.wireOp",EDGE,"E42.13.0.17")}),1.0]])]});
            var Q951;
            Q951=makeQuery(id+"F6.imprint","IMPRINT",FACE,{"disambiguationData":[TD([[makeQuery(id+"F6.imprint","IMPRINT",EDGE,{"derivedFrom":sQuery(id+"F6.wireOp",EDGE,"E42.12.0.8")}),1.0]])]});
            var Q952;
            Q952=makeQuery(id+"F6.imprint","IMPRINT",FACE,{"disambiguationData":[TD([[makeQuery(id+"F6.imprint","IMPRINT",EDGE,{"derivedFrom":sQuery(id+"F6.wireOp",EDGE,"E383.MirrorC")}),-1.0]])]});
            var Q953;
            Q953=makeQuery(id+"F6.imprint","IMPRINT",FACE,{"disambiguationData":[TD([[makeQuery(id+"F6.imprint","IMPRINT",EDGE,{"derivedFrom":sQuery(id+"F6.wireOp",EDGE,"E852.MirrorC")}),-1.0]])]});
            var Q954;
            Q954=makeQuery(id+"F6.imprint","IMPRINT",FACE,{"disambiguationData":[TD([[makeQuery(id+"F6.imprint","IMPRINT",EDGE,{"derivedFrom":sQuery(id+"F6.wireOp",EDGE,"E801.MirrorC")}),-1.0]])]});
            var Q955;
            Q955=makeQuery(id+"F6.imprint","IMPRINT",FACE,{"disambiguationData":[TD([[makeQuery(id+"F6.imprint","IMPRINT",EDGE,{"derivedFrom":sQuery(id+"F6.wireOp",EDGE,"E42.11.0.17")}),1.0]])]});
            var Q956;
            Q956=makeQuery(id+"F6.imprint","IMPRINT",FACE,{"disambiguationData":[TD([[makeQuery(id+"F6.imprint","IMPRINT",EDGE,{"derivedFrom":sQuery(id+"F6.wireOp",EDGE,"E42.16.0.8")}),1.0]])]});
            var Q957;
            Q957=makeQuery(id+"F6.imprint","IMPRINT",FACE,{"disambiguationData":[TD([[makeQuery(id+"F6.imprint","IMPRINT",EDGE,{"derivedFrom":sQuery(id+"F6.wireOp",EDGE,"E42.15.0.17")}),1.0]])]});
            var Q958;
            Q958=makeQuery(id+"F6.imprint","IMPRINT",FACE,{"disambiguationData":[TD([[makeQuery(id+"F6.imprint","IMPRINT",EDGE,{"derivedFrom":sQuery(id+"F6.wireOp",EDGE,"E42.14.0.8")}),1.0]])]});
            var Q959;
            Q959=makeQuery(id+"F6.imprint","IMPRINT",FACE,{"disambiguationData":[TD([[makeQuery(id+"F6.imprint","IMPRINT",EDGE,{"derivedFrom":sQuery(id+"F6.wireOp",EDGE,"E662.MirrorC")}),-1.0]])]});
            var Q960;
            Q960=makeQuery(id+"F6.imprint","IMPRINT",FACE,{"disambiguationData":[TD([[makeQuery(id+"F6.imprint","IMPRINT",EDGE,{"derivedFrom":sQuery(id+"F6.wireOp",EDGE,"E714.MirrorC")}),-1.0]])]});
            var Q961;
            Q961=makeQuery(id+"F6.imprint","IMPRINT",FACE,{"disambiguationData":[TD([[makeQuery(id+"F6.imprint","IMPRINT",EDGE,{"derivedFrom":sQuery(id+"F6.wireOp",EDGE,"E416.MirrorC")}),-1.0]])]});
            var Q962;
            Q962=makeQuery(id+"F6.imprint","IMPRINT",FACE,{"disambiguationData":[TD([[makeQuery(id+"F6.imprint","IMPRINT",EDGE,{"derivedFrom":sQuery(id+"F6.wireOp",EDGE,"E315.MirrorC")}),-1.0]])]});
            var Q963;
            Q963=makeQuery(id+"F6.imprint","IMPRINT",FACE,{"disambiguationData":[TD([[makeQuery(id+"F6.imprint","IMPRINT",EDGE,{"derivedFrom":sQuery(id+"F6.wireOp",EDGE,"E330.MirrorC")}),-1.0]])]});
            var Q964;
            Q964=makeQuery(id+"F6.imprint","IMPRINT",FACE,{"disambiguationData":[TD([[makeQuery(id+"F6.imprint","IMPRINT",EDGE,{"derivedFrom":sQuery(id+"F6.wireOp",EDGE,"E816.MirrorC")}),-1.0]])]});
            var Q965;
            Q965=makeQuery(id+"F6.imprint","IMPRINT",FACE,{"disambiguationData":[TD([[makeQuery(id+"F6.imprint","IMPRINT",EDGE,{"derivedFrom":sQuery(id+"F6.wireOp",EDGE,"E868.MirrorC")}),-1.0]])]});
            var Q966;
            Q966=makeQuery(id+"F6.imprint","IMPRINT",FACE,{"disambiguationData":[TD([[makeQuery(id+"F6.imprint","IMPRINT",EDGE,{"derivedFrom":sQuery(id+"F6.wireOp",EDGE,"E398.MirrorC")}),-1.0]])]});
            var Q967;
            Q967=makeQuery(id+"F6.imprint","IMPRINT",FACE,{"disambiguationData":[TD([[makeQuery(id+"F6.imprint","IMPRINT",EDGE,{"derivedFrom":sQuery(id+"F6.wireOp",EDGE,"E299.MirrorC")}),-1.0]])]});
            var Q968;
            Q968=makeQuery(id+"F6.imprint","IMPRINT",FACE,{"disambiguationData":[TD([[makeQuery(id+"F6.imprint","IMPRINT",EDGE,{"derivedFrom":sQuery(id+"F6.wireOp",EDGE,"E283.MirrorC")}),-1.0]])]});
            var Q969;
            Q969=makeQuery(id+"F6.imprint","IMPRINT",FACE,{"disambiguationData":[TD([[makeQuery(id+"F6.imprint","IMPRINT",EDGE,{"derivedFrom":sQuery(id+"F6.wireOp",EDGE,"E267.MirrorC")}),-1.0]])]});
            var Q970;
            Q970=makeQuery(id+"F6.imprint","IMPRINT",FACE,{"disambiguationData":[TD([[makeQuery(id+"F6.imprint","IMPRINT",EDGE,{"derivedFrom":sQuery(id+"F6.wireOp",EDGE,"E253.MirrorC")}),-1.0]])]});
            var Q971;
            Q971=makeQuery(id+"F6.imprint","IMPRINT",FACE,{"disambiguationData":[TD([[makeQuery(id+"F6.imprint","IMPRINT",EDGE,{"derivedFrom":sQuery(id+"F6.wireOp",EDGE,"E668.MirrorC")}),-1.0]])]});
            var Q972;
            Q972=makeQuery(id+"F6.imprint","IMPRINT",FACE,{"disambiguationData":[TD([[makeQuery(id+"F6.imprint","IMPRINT",EDGE,{"derivedFrom":sQuery(id+"F6.wireOp",EDGE,"E771.MirrorC")}),-1.0]])]});
            var Q973;
            Q973=makeQuery(id+"F6.imprint","IMPRINT",FACE,{"disambiguationData":[TD([[makeQuery(id+"F6.imprint","IMPRINT",EDGE,{"derivedFrom":sQuery(id+"F6.wireOp",EDGE,"E422.MirrorC")}),-1.0]])]});
            var Q974;
            Q974=makeQuery(id+"F6.imprint","IMPRINT",FACE,{"disambiguationData":[TD([[makeQuery(id+"F6.imprint","IMPRINT",EDGE,{"derivedFrom":sQuery(id+"F6.wireOp",EDGE,"E616.MirrorC")}),-1.0]])]});
            var Q975;
            Q975=makeQuery(id+"F6.imprint","IMPRINT",FACE,{"disambiguationData":[TD([[makeQuery(id+"F6.imprint","IMPRINT",EDGE,{"derivedFrom":sQuery(id+"F6.wireOp",EDGE,"E355.MirrorC")}),-1.0]])]});
            var Q976;
            Q976=makeQuery(id+"F6.imprint","IMPRINT",FACE,{"disambiguationData":[TD([[makeQuery(id+"F6.imprint","IMPRINT",EDGE,{"derivedFrom":sQuery(id+"F6.wireOp",EDGE,"E407.MirrorC")}),-1.0]])]});
            var Q977;
            Q977=makeQuery(id+"F6.imprint","IMPRINT",FACE,{"disambiguationData":[TD([[makeQuery(id+"F6.imprint","IMPRINT",EDGE,{"derivedFrom":sQuery(id+"F6.wireOp",EDGE,"E822.MirrorC")}),-1.0]])]});
            var Q978;
            Q978=makeQuery(id+"F6.imprint","IMPRINT",FACE,{"disambiguationData":[TD([[makeQuery(id+"F6.imprint","IMPRINT",EDGE,{"derivedFrom":sQuery(id+"F6.wireOp",EDGE,"E631.MirrorC")}),-1.0]])]});
            var Q979;
            Q979=makeQuery(id+"F6.imprint","IMPRINT",FACE,{"disambiguationData":[TD([[makeQuery(id+"F6.imprint","IMPRINT",EDGE,{"derivedFrom":sQuery(id+"F6.wireOp",EDGE,"E684.MirrorC")}),-1.0]])]});
            var Q980;
            Q980=makeQuery(id+"F6.imprint","IMPRINT",FACE,{"disambiguationData":[TD([[makeQuery(id+"F6.imprint","IMPRINT",EDGE,{"derivedFrom":sQuery(id+"F6.wireOp",EDGE,"E42.17.0.17")}),1.0]])]});
            var Q981;
            Q981=makeQuery(id+"F6.imprint","IMPRINT",FACE,{"disambiguationData":[TD([[makeQuery(id+"F6.imprint","IMPRINT",EDGE,{"derivedFrom":sQuery(id+"F6.wireOp",EDGE,"E367.MirrorC")}),-1.0]])]});
            var Q982;
            Q982=makeQuery(id+"F6.imprint","IMPRINT",FACE,{"disambiguationData":[TD([[makeQuery(id+"F6.imprint","IMPRINT",EDGE,{"derivedFrom":sQuery(id+"F6.wireOp",EDGE,"E42.20.0.8")}),1.0]])]});
            var Q983;
            Q983=makeQuery(id+"F6.imprint","IMPRINT",FACE,{"disambiguationData":[TD([[makeQuery(id+"F6.imprint","IMPRINT",EDGE,{"derivedFrom":sQuery(id+"F6.wireOp",EDGE,"E42.19.0.17")}),1.0]])]});
            var Q984;
            Q984=makeQuery(id+"F6.imprint","IMPRINT",FACE,{"disambiguationData":[TD([[makeQuery(id+"F6.imprint","IMPRINT",EDGE,{"derivedFrom":sQuery(id+"F6.wireOp",EDGE,"E386.MirrorC")}),-1.0]])]});
            var Q985;
            Q985=makeQuery(id+"F6.imprint","IMPRINT",FACE,{"disambiguationData":[TD([[makeQuery(id+"F6.imprint","IMPRINT",EDGE,{"derivedFrom":sQuery(id+"F6.wireOp",EDGE,"E42.18.0.8")}),1.0]])]});
            var Q986;
            Q986=makeQuery(id+"F6.imprint","IMPRINT",FACE,{"disambiguationData":[TD([[makeQuery(id+"F6.imprint","IMPRINT",EDGE,{"derivedFrom":sQuery(id+"F6.wireOp",EDGE,"E438.MirrorC")}),-1.0]])]});
            var Q987;
            Q987=makeQuery(id+"F6.imprint","IMPRINT",FACE,{"disambiguationData":[TD([[makeQuery(id+"F6.imprint","IMPRINT",EDGE,{"derivedFrom":sQuery(id+"F6.wireOp",EDGE,"E42.22.0.8")}),1.0]])]});
            var Q988;
            Q988=makeQuery(id+"F6.imprint","IMPRINT",FACE,{"disambiguationData":[TD([[makeQuery(id+"F6.imprint","IMPRINT",EDGE,{"derivedFrom":sQuery(id+"F6.wireOp",EDGE,"E42.21.0.17")}),1.0]])]});
            var Q989;
            Q989=makeQuery(id+"F6.imprint","IMPRINT",FACE,{"disambiguationData":[TD([[makeQuery(id+"F6.imprint","IMPRINT",EDGE,{"derivedFrom":sQuery(id+"F6.wireOp",EDGE,"E42.25.0.17")}),1.0]])]});
            var Q990;
            Q990=makeQuery(id+"F6.imprint","IMPRINT",FACE,{"disambiguationData":[TD([[makeQuery(id+"F6.imprint","IMPRINT",EDGE,{"derivedFrom":sQuery(id+"F6.wireOp",EDGE,"E42.24.0.8")}),1.0]])]});
            var Q991;
            Q991=makeQuery(id+"F6.imprint","IMPRINT",FACE,{"disambiguationData":[TD([[makeQuery(id+"F6.imprint","IMPRINT",EDGE,{"derivedFrom":sQuery(id+"F6.wireOp",EDGE,"E42.23.0.17")}),1.0]])]});
            var Q992;
            Q992=makeQuery(id+"F6.imprint","IMPRINT",FACE,{"disambiguationData":[TD([[makeQuery(id+"F6.imprint","IMPRINT",EDGE,{"derivedFrom":sQuery(id+"F6.wireOp",EDGE,"E42.28.0.8")}),1.0]])]});
            var Q993;
            Q993=makeQuery(id+"F6.imprint","IMPRINT",FACE,{"disambiguationData":[TD([[makeQuery(id+"F6.imprint","IMPRINT",EDGE,{"derivedFrom":sQuery(id+"F6.wireOp",EDGE,"E42.27.0.17")}),1.0]])]});
            var Q994;
            Q994=makeQuery(id+"F6.imprint","IMPRINT",FACE,{"disambiguationData":[TD([[makeQuery(id+"F6.imprint","IMPRINT",EDGE,{"derivedFrom":sQuery(id+"F6.wireOp",EDGE,"E370.MirrorC")}),-1.0]])]});
            var Q995;
            Q995=makeQuery(id+"F6.imprint","IMPRINT",FACE,{"disambiguationData":[TD([[makeQuery(id+"F6.imprint","IMPRINT",EDGE,{"derivedFrom":sQuery(id+"F6.wireOp",EDGE,"E42.26.0.8")}),1.0]])]});
            var Q996;
            Q996=makeQuery(id+"F6.imprint","IMPRINT",FACE,{"disambiguationData":[TD([[makeQuery(id+"F6.imprint","IMPRINT",EDGE,{"derivedFrom":sQuery(id+"F6.wireOp",EDGE,"E837.MirrorC")}),-1.0]])]});
            var Q997;
            Q997=makeQuery(id+"F6.imprint","IMPRINT",FACE,{"disambiguationData":[TD([[makeQuery(id+"F6.imprint","IMPRINT",EDGE,{"derivedFrom":sQuery(id+"F6.wireOp",EDGE,"E42.30.0.8")}),1.0]])]});
            var Q998;
            Q998=makeQuery(id+"F6.imprint","IMPRINT",FACE,{"disambiguationData":[TD([[makeQuery(id+"F6.imprint","IMPRINT",EDGE,{"derivedFrom":sQuery(id+"F6.wireOp",EDGE,"E786.MirrorC")}),-1.0]])]});
            var Q999;
            Q999=makeQuery(id+"F6.imprint","IMPRINT",FACE,{"disambiguationData":[TD([[makeQuery(id+"F6.imprint","IMPRINT",EDGE,{"derivedFrom":sQuery(id+"F6.wireOp",EDGE,"E42.29.0.17")}),1.0]])]});
            var Q1000;
            Q1000=makeQuery(id+"F6.imprint","IMPRINT",FACE,{"disambiguationData":[TD([[makeQuery(id+"F6.imprint","IMPRINT",EDGE,{"derivedFrom":sQuery(id+"F6.wireOp",EDGE,"E42.32.0.8")}),1.0]])]});
            var Q1001;
            Q1001=makeQuery(id+"F6.imprint","IMPRINT",FACE,{"disambiguationData":[TD([[makeQuery(id+"F6.imprint","IMPRINT",EDGE,{"derivedFrom":sQuery(id+"F6.wireOp",EDGE,"E42.31.0.17")}),1.0]])]});
            var Q1002;
            Q1002=makeQuery(id+"F6.imprint","IMPRINT",FACE,{"disambiguationData":[TD([[makeQuery(id+"F6.imprint","IMPRINT",EDGE,{"derivedFrom":sQuery(id+"F6.wireOp",EDGE,"E42.2.0.9")}),1.0]])]});
            var Q1003;
            Q1003=makeQuery(id+"F6.imprint","IMPRINT",FACE,{"disambiguationData":[TD([[makeQuery(id+"F6.imprint","IMPRINT",EDGE,{"derivedFrom":sQuery(id+"F6.wireOp",EDGE,"E42.1.0.18")}),1.0]])]});
            var Q1004;
            Q1004=makeQuery(id+"F6.imprint","IMPRINT",FACE,{"disambiguationData":[TD([[makeQuery(id+"F6.imprint","IMPRINT",EDGE,{"derivedFrom":sQuery(id+"F6.wireOp",EDGE,"E41.0.11.0")}),1.0]])]});
            var Q1005;
            Q1005=makeQuery(id+"F6.imprint","IMPRINT",FACE,{"disambiguationData":[TD([[makeQuery(id+"F6.imprint","IMPRINT",EDGE,{"derivedFrom":sQuery(id+"F6.wireOp",EDGE,"E42.5.0.18")}),1.0]])]});
            var Q1006;
            Q1006=makeQuery(id+"F6.imprint","IMPRINT",FACE,{"disambiguationData":[TD([[makeQuery(id+"F6.imprint","IMPRINT",EDGE,{"derivedFrom":sQuery(id+"F6.wireOp",EDGE,"E42.4.0.9")}),1.0]])]});
            var Q1007;
            Q1007=makeQuery(id+"F6.imprint","IMPRINT",FACE,{"disambiguationData":[TD([[makeQuery(id+"F6.imprint","IMPRINT",EDGE,{"derivedFrom":sQuery(id+"F6.wireOp",EDGE,"E42.3.0.18")}),1.0]])]});
            var Q1008;
            Q1008=makeQuery(id+"F6.imprint","IMPRINT",FACE,{"disambiguationData":[TD([[makeQuery(id+"F6.imprint","IMPRINT",EDGE,{"derivedFrom":sQuery(id+"F6.wireOp",EDGE,"E42.8.0.9")}),1.0]])]});
            var Q1009;
            Q1009=makeQuery(id+"F6.imprint","IMPRINT",FACE,{"disambiguationData":[TD([[makeQuery(id+"F6.imprint","IMPRINT",EDGE,{"derivedFrom":sQuery(id+"F6.wireOp",EDGE,"E42.7.0.18")}),1.0]])]});
            var Q1010;
            Q1010=makeQuery(id+"F6.imprint","IMPRINT",FACE,{"disambiguationData":[TD([[makeQuery(id+"F6.imprint","IMPRINT",EDGE,{"derivedFrom":sQuery(id+"F6.wireOp",EDGE,"E42.6.0.9")}),1.0]])]});
            var Q1011;
            Q1011=makeQuery(id+"F6.imprint","IMPRINT",FACE,{"disambiguationData":[TD([[makeQuery(id+"F6.imprint","IMPRINT",EDGE,{"derivedFrom":sQuery(id+"F6.wireOp",EDGE,"E42.10.0.9")}),1.0]])]});
            var Q1012;
            Q1012=makeQuery(id+"F6.imprint","IMPRINT",FACE,{"disambiguationData":[TD([[makeQuery(id+"F6.imprint","IMPRINT",EDGE,{"derivedFrom":sQuery(id+"F6.wireOp",EDGE,"E42.9.0.18")}),1.0]])]});
            var Q1013;
            Q1013=makeQuery(id+"F6.imprint","IMPRINT",FACE,{"disambiguationData":[TD([[makeQuery(id+"F6.imprint","IMPRINT",EDGE,{"derivedFrom":sQuery(id+"F6.wireOp",EDGE,"E42.13.0.18")}),1.0]])]});
            var Q1014;
            Q1014=makeQuery(id+"F6.imprint","IMPRINT",FACE,{"disambiguationData":[TD([[makeQuery(id+"F6.imprint","IMPRINT",EDGE,{"derivedFrom":sQuery(id+"F6.wireOp",EDGE,"E42.12.0.9")}),1.0]])]});
            var Q1015;
            Q1015=makeQuery(id+"F6.imprint","IMPRINT",FACE,{"disambiguationData":[TD([[makeQuery(id+"F6.imprint","IMPRINT",EDGE,{"derivedFrom":sQuery(id+"F6.wireOp",EDGE,"E42.11.0.18")}),1.0]])]});
            var Q1016;
            Q1016=makeQuery(id+"F6.imprint","IMPRINT",FACE,{"disambiguationData":[TD([[makeQuery(id+"F6.imprint","IMPRINT",EDGE,{"derivedFrom":sQuery(id+"F6.wireOp",EDGE,"E42.16.0.9")}),1.0]])]});
            var Q1017;
            Q1017=makeQuery(id+"F6.imprint","IMPRINT",FACE,{"disambiguationData":[TD([[makeQuery(id+"F6.imprint","IMPRINT",EDGE,{"derivedFrom":sQuery(id+"F6.wireOp",EDGE,"E42.15.0.18")}),1.0]])]});
            var Q1018;
            Q1018=makeQuery(id+"F6.imprint","IMPRINT",FACE,{"disambiguationData":[TD([[makeQuery(id+"F6.imprint","IMPRINT",EDGE,{"derivedFrom":sQuery(id+"F6.wireOp",EDGE,"E42.14.0.9")}),1.0]])]});
            var Q1019;
            Q1019=makeQuery(id+"F6.imprint","IMPRINT",FACE,{"disambiguationData":[TD([[makeQuery(id+"F6.imprint","IMPRINT",EDGE,{"derivedFrom":sQuery(id+"F6.wireOp",EDGE,"E316.MirrorC")}),-1.0]])]});
            var Q1020;
            Q1020=makeQuery(id+"F6.imprint","IMPRINT",FACE,{"disambiguationData":[TD([[makeQuery(id+"F6.imprint","IMPRINT",EDGE,{"derivedFrom":sQuery(id+"F6.wireOp",EDGE,"E331.MirrorC")}),-1.0]])]});
            var Q1021;
            Q1021=makeQuery(id+"F6.imprint","IMPRINT",FACE,{"disambiguationData":[TD([[makeQuery(id+"F6.imprint","IMPRINT",EDGE,{"derivedFrom":sQuery(id+"F6.wireOp",EDGE,"E300.MirrorC")}),-1.0]])]});
            var Q1022;
            Q1022=makeQuery(id+"F6.imprint","IMPRINT",FACE,{"disambiguationData":[TD([[makeQuery(id+"F6.imprint","IMPRINT",EDGE,{"derivedFrom":sQuery(id+"F6.wireOp",EDGE,"E284.MirrorC")}),-1.0]])]});
            var Q1023;
            Q1023=makeQuery(id+"F6.imprint","IMPRINT",FACE,{"disambiguationData":[TD([[makeQuery(id+"F6.imprint","IMPRINT",EDGE,{"derivedFrom":sQuery(id+"F6.wireOp",EDGE,"E268.MirrorC")}),-1.0]])]});
            var Q1024;
            Q1024=makeQuery(id+"F6.imprint","IMPRINT",FACE,{"disambiguationData":[TD([[makeQuery(id+"F6.imprint","IMPRINT",EDGE,{"derivedFrom":sQuery(id+"F6.wireOp",EDGE,"E254.MirrorC")}),-1.0]])]});
            var Q1025;
            Q1025=makeQuery(id+"F6.imprint","IMPRINT",FACE,{"disambiguationData":[TD([[makeQuery(id+"F6.imprint","IMPRINT",EDGE,{"derivedFrom":sQuery(id+"F6.wireOp",EDGE,"E42.17.0.18")}),1.0]])]});
            var Q1026;
            Q1026=makeQuery(id+"F6.imprint","IMPRINT",FACE,{"disambiguationData":[TD([[makeQuery(id+"F6.imprint","IMPRINT",EDGE,{"derivedFrom":sQuery(id+"F6.wireOp",EDGE,"E42.20.0.9")}),1.0]])]});
            var Q1027;
            Q1027=makeQuery(id+"F6.imprint","IMPRINT",FACE,{"disambiguationData":[TD([[makeQuery(id+"F6.imprint","IMPRINT",EDGE,{"derivedFrom":sQuery(id+"F6.wireOp",EDGE,"E42.19.0.18")}),1.0]])]});
            var Q1028;
            Q1028=makeQuery(id+"F6.imprint","IMPRINT",FACE,{"disambiguationData":[TD([[makeQuery(id+"F6.imprint","IMPRINT",EDGE,{"derivedFrom":sQuery(id+"F6.wireOp",EDGE,"E42.18.0.9")}),1.0]])]});
            var Q1029;
            Q1029=makeQuery(id+"F6.imprint","IMPRINT",FACE,{"disambiguationData":[TD([[makeQuery(id+"F6.imprint","IMPRINT",EDGE,{"derivedFrom":sQuery(id+"F6.wireOp",EDGE,"E42.22.0.9")}),1.0]])]});
            var Q1030;
            Q1030=makeQuery(id+"F6.imprint","IMPRINT",FACE,{"disambiguationData":[TD([[makeQuery(id+"F6.imprint","IMPRINT",EDGE,{"derivedFrom":sQuery(id+"F6.wireOp",EDGE,"E42.21.0.18")}),1.0]])]});
            var Q1031;
            Q1031=makeQuery(id+"F6.imprint","IMPRINT",FACE,{"disambiguationData":[TD([[makeQuery(id+"F6.imprint","IMPRINT",EDGE,{"derivedFrom":sQuery(id+"F6.wireOp",EDGE,"E42.25.0.18")}),1.0]])]});
            var Q1032;
            Q1032=makeQuery(id+"F6.imprint","IMPRINT",FACE,{"disambiguationData":[TD([[makeQuery(id+"F6.imprint","IMPRINT",EDGE,{"derivedFrom":sQuery(id+"F6.wireOp",EDGE,"E42.24.0.9")}),1.0]])]});
            var Q1033;
            Q1033=makeQuery(id+"F6.imprint","IMPRINT",FACE,{"disambiguationData":[TD([[makeQuery(id+"F6.imprint","IMPRINT",EDGE,{"derivedFrom":sQuery(id+"F6.wireOp",EDGE,"E42.23.0.18")}),1.0]])]});
            var Q1034;
            Q1034=makeQuery(id+"F6.imprint","IMPRINT",FACE,{"disambiguationData":[TD([[makeQuery(id+"F6.imprint","IMPRINT",EDGE,{"derivedFrom":sQuery(id+"F6.wireOp",EDGE,"E42.28.0.9")}),1.0]])]});
            var Q1035;
            Q1035=makeQuery(id+"F6.imprint","IMPRINT",FACE,{"disambiguationData":[TD([[makeQuery(id+"F6.imprint","IMPRINT",EDGE,{"derivedFrom":sQuery(id+"F6.wireOp",EDGE,"E42.27.0.18")}),1.0]])]});
            var Q1036;
            Q1036=makeQuery(id+"F6.imprint","IMPRINT",FACE,{"disambiguationData":[TD([[makeQuery(id+"F6.imprint","IMPRINT",EDGE,{"derivedFrom":sQuery(id+"F6.wireOp",EDGE,"E42.26.0.9")}),1.0]])]});
            var Q1037;
            Q1037=makeQuery(id+"F6.imprint","IMPRINT",FACE,{"disambiguationData":[TD([[makeQuery(id+"F6.imprint","IMPRINT",EDGE,{"derivedFrom":sQuery(id+"F6.wireOp",EDGE,"E42.30.0.9")}),1.0]])]});
            var Q1038;
            Q1038=makeQuery(id+"F6.imprint","IMPRINT",FACE,{"disambiguationData":[TD([[makeQuery(id+"F6.imprint","IMPRINT",EDGE,{"derivedFrom":sQuery(id+"F6.wireOp",EDGE,"E42.29.0.18")}),1.0]])]});
            var Q1039;
            Q1039=makeQuery(id+"F6.imprint","IMPRINT",FACE,{"disambiguationData":[TD([[makeQuery(id+"F6.imprint","IMPRINT",EDGE,{"derivedFrom":sQuery(id+"F6.wireOp",EDGE,"E42.32.0.9")}),1.0]])]});
            var Q1040;
            Q1040=makeQuery(id+"F6.imprint","IMPRINT",FACE,{"disambiguationData":[TD([[makeQuery(id+"F6.imprint","IMPRINT",EDGE,{"derivedFrom":sQuery(id+"F6.wireOp",EDGE,"E42.31.0.18")}),1.0]])]});
            var Q1041;
            Q1041=makeQuery(id+"F6.imprint","IMPRINT",FACE,{"disambiguationData":[TD([[makeQuery(id+"F6.imprint","IMPRINT",EDGE,{"derivedFrom":sQuery(id+"F6.wireOp",EDGE,"E42.3.0.1")}),1.0]])]});
            var Q1042;
            Q1042=makeQuery(id+"F6.imprint","IMPRINT",FACE,{"disambiguationData":[TD([[makeQuery(id+"F6.imprint","IMPRINT",EDGE,{"derivedFrom":sQuery(id+"F6.wireOp",EDGE,"E42.2.0.10")}),1.0]])]});
            var Q1043;
            Q1043=makeQuery(id+"F6.imprint","IMPRINT",FACE,{"disambiguationData":[TD([[makeQuery(id+"F6.imprint","IMPRINT",EDGE,{"derivedFrom":sQuery(id+"F6.wireOp",EDGE,"E42.1.0.19")}),1.0]])]});
            var Q1044;
            Q1044=makeQuery(id+"F6.imprint","IMPRINT",FACE,{"disambiguationData":[TD([[makeQuery(id+"F6.imprint","IMPRINT",EDGE,{"derivedFrom":sQuery(id+"F6.wireOp",EDGE,"E42.1.0.1")}),1.0]])]});
            var Q1045;
            Q1045=makeQuery(id+"F6.imprint","IMPRINT",FACE,{"disambiguationData":[TD([[makeQuery(id+"F6.imprint","IMPRINT",EDGE,{"derivedFrom":sQuery(id+"F6.wireOp",EDGE,"E42.5.0.19")}),1.0]])]});
            var Q1046;
            Q1046=makeQuery(id+"F6.imprint","IMPRINT",FACE,{"disambiguationData":[TD([[makeQuery(id+"F6.imprint","IMPRINT",EDGE,{"derivedFrom":sQuery(id+"F6.wireOp",EDGE,"E42.5.0.1")}),1.0]])]});
            var Q1047;
            Q1047=makeQuery(id+"F6.imprint","IMPRINT",FACE,{"disambiguationData":[TD([[makeQuery(id+"F6.imprint","IMPRINT",EDGE,{"derivedFrom":sQuery(id+"F6.wireOp",EDGE,"E42.4.0.10")}),1.0]])]});
            var Q1048;
            Q1048=makeQuery(id+"F6.imprint","IMPRINT",FACE,{"disambiguationData":[TD([[makeQuery(id+"F6.imprint","IMPRINT",EDGE,{"derivedFrom":sQuery(id+"F6.wireOp",EDGE,"E42.3.0.19")}),1.0]])]});
            var Q1049;
            Q1049=makeQuery(id+"F6.imprint","IMPRINT",FACE,{"disambiguationData":[TD([[makeQuery(id+"F6.imprint","IMPRINT",EDGE,{"derivedFrom":sQuery(id+"F6.wireOp",EDGE,"E42.8.0.10")}),1.0]])]});
            var Q1050;
            Q1050=makeQuery(id+"F6.imprint","IMPRINT",FACE,{"disambiguationData":[TD([[makeQuery(id+"F6.imprint","IMPRINT",EDGE,{"derivedFrom":sQuery(id+"F6.wireOp",EDGE,"E42.7.0.19")}),1.0]])]});
            var Q1051;
            Q1051=makeQuery(id+"F6.imprint","IMPRINT",FACE,{"disambiguationData":[TD([[makeQuery(id+"F6.imprint","IMPRINT",EDGE,{"derivedFrom":sQuery(id+"F6.wireOp",EDGE,"E42.7.0.1")}),1.0]])]});
            var Q1052;
            Q1052=makeQuery(id+"F6.imprint","IMPRINT",FACE,{"disambiguationData":[TD([[makeQuery(id+"F6.imprint","IMPRINT",EDGE,{"derivedFrom":sQuery(id+"F6.wireOp",EDGE,"E42.6.0.10")}),1.0]])]});
            var Q1053;
            Q1053=makeQuery(id+"F6.imprint","IMPRINT",FACE,{"disambiguationData":[TD([[makeQuery(id+"F6.imprint","IMPRINT",EDGE,{"derivedFrom":sQuery(id+"F6.wireOp",EDGE,"E42.11.0.1")}),1.0]])]});
            var Q1054;
            Q1054=makeQuery(id+"F6.imprint","IMPRINT",FACE,{"disambiguationData":[TD([[makeQuery(id+"F6.imprint","IMPRINT",EDGE,{"derivedFrom":sQuery(id+"F6.wireOp",EDGE,"E42.10.0.10")}),1.0]])]});
            var Q1055;
            Q1055=makeQuery(id+"F6.imprint","IMPRINT",FACE,{"disambiguationData":[TD([[makeQuery(id+"F6.imprint","IMPRINT",EDGE,{"derivedFrom":sQuery(id+"F6.wireOp",EDGE,"E42.9.0.19")}),1.0]])]});
            var Q1056;
            Q1056=makeQuery(id+"F6.imprint","IMPRINT",FACE,{"disambiguationData":[TD([[makeQuery(id+"F6.imprint","IMPRINT",EDGE,{"derivedFrom":sQuery(id+"F6.wireOp",EDGE,"E42.9.0.1")}),1.0]])]});
            var Q1057;
            Q1057=makeQuery(id+"F6.imprint","IMPRINT",FACE,{"disambiguationData":[TD([[makeQuery(id+"F6.imprint","IMPRINT",EDGE,{"derivedFrom":sQuery(id+"F6.wireOp",EDGE,"E42.13.0.19")}),1.0]])]});
            var Q1058;
            Q1058=makeQuery(id+"F6.imprint","IMPRINT",FACE,{"disambiguationData":[TD([[makeQuery(id+"F6.imprint","IMPRINT",EDGE,{"derivedFrom":sQuery(id+"F6.wireOp",EDGE,"E42.13.0.1")}),1.0]])]});
            var Q1059;
            Q1059=makeQuery(id+"F6.imprint","IMPRINT",FACE,{"disambiguationData":[TD([[makeQuery(id+"F6.imprint","IMPRINT",EDGE,{"derivedFrom":sQuery(id+"F6.wireOp",EDGE,"E42.12.0.10")}),1.0]])]});
            var Q1060;
            Q1060=makeQuery(id+"F6.imprint","IMPRINT",FACE,{"disambiguationData":[TD([[makeQuery(id+"F6.imprint","IMPRINT",EDGE,{"derivedFrom":sQuery(id+"F6.wireOp",EDGE,"E42.11.0.19")}),1.0]])]});
            var Q1061;
            Q1061=makeQuery(id+"F6.imprint","IMPRINT",FACE,{"disambiguationData":[TD([[makeQuery(id+"F6.imprint","IMPRINT",EDGE,{"derivedFrom":sQuery(id+"F6.wireOp",EDGE,"E42.16.0.10")}),1.0]])]});
            var Q1062;
            Q1062=makeQuery(id+"F6.imprint","IMPRINT",FACE,{"disambiguationData":[TD([[makeQuery(id+"F6.imprint","IMPRINT",EDGE,{"derivedFrom":sQuery(id+"F6.wireOp",EDGE,"E42.15.0.19")}),1.0]])]});
            var Q1063;
            Q1063=makeQuery(id+"F6.imprint","IMPRINT",FACE,{"disambiguationData":[TD([[makeQuery(id+"F6.imprint","IMPRINT",EDGE,{"derivedFrom":sQuery(id+"F6.wireOp",EDGE,"E42.15.0.1")}),1.0]])]});
            var Q1064;
            Q1064=makeQuery(id+"F6.imprint","IMPRINT",FACE,{"disambiguationData":[TD([[makeQuery(id+"F6.imprint","IMPRINT",EDGE,{"derivedFrom":sQuery(id+"F6.wireOp",EDGE,"E42.14.0.10")}),1.0]])]});
            var Q1065;
            Q1065=makeQuery(id+"F6.imprint","IMPRINT",FACE,{"disambiguationData":[TD([[makeQuery(id+"F6.imprint","IMPRINT",EDGE,{"derivedFrom":sQuery(id+"F6.wireOp",EDGE,"E42.17.0.1")}),1.0]])]});
            var Q1066;
            Q1066=makeQuery(id+"F6.imprint","IMPRINT",FACE,{"disambiguationData":[TD([[makeQuery(id+"F6.imprint","IMPRINT",EDGE,{"derivedFrom":sQuery(id+"F6.wireOp",EDGE,"E42.17.0.19")}),1.0]])]});
            var Q1067;
            Q1067=makeQuery(id+"F6.imprint","IMPRINT",FACE,{"disambiguationData":[TD([[makeQuery(id+"F6.imprint","IMPRINT",EDGE,{"derivedFrom":sQuery(id+"F6.wireOp",EDGE,"E317.MirrorC")}),-1.0]])]});
            var Q1068;
            Q1068=makeQuery(id+"F6.imprint","IMPRINT",FACE,{"disambiguationData":[TD([[makeQuery(id+"F6.imprint","IMPRINT",EDGE,{"derivedFrom":sQuery(id+"F6.wireOp",EDGE,"E332.MirrorC")}),-1.0]])]});
            var Q1069;
            Q1069=makeQuery(id+"F6.imprint","IMPRINT",FACE,{"disambiguationData":[TD([[makeQuery(id+"F6.imprint","IMPRINT",EDGE,{"derivedFrom":sQuery(id+"F6.wireOp",EDGE,"E301.MirrorC")}),-1.0]])]});
            var Q1070;
            Q1070=makeQuery(id+"F6.imprint","IMPRINT",FACE,{"disambiguationData":[TD([[makeQuery(id+"F6.imprint","IMPRINT",EDGE,{"derivedFrom":sQuery(id+"F6.wireOp",EDGE,"E285.MirrorC")}),-1.0]])]});
            var Q1071;
            Q1071=makeQuery(id+"F6.imprint","IMPRINT",FACE,{"disambiguationData":[TD([[makeQuery(id+"F6.imprint","IMPRINT",EDGE,{"derivedFrom":sQuery(id+"F6.wireOp",EDGE,"E269.MirrorC")}),-1.0]])]});
            var Q1072;
            Q1072=makeQuery(id+"F6.imprint","IMPRINT",FACE,{"disambiguationData":[TD([[makeQuery(id+"F6.imprint","IMPRINT",EDGE,{"derivedFrom":sQuery(id+"F6.wireOp",EDGE,"E255.MirrorC")}),-1.0]])]});
            var Q1073;
            Q1073=makeQuery(id+"F6.imprint","IMPRINT",FACE,{"disambiguationData":[TD([[makeQuery(id+"F6.imprint","IMPRINT",EDGE,{"derivedFrom":sQuery(id+"F6.wireOp",EDGE,"E42.20.0.10")}),1.0]])]});
            var Q1074;
            Q1074=makeQuery(id+"F6.imprint","IMPRINT",FACE,{"disambiguationData":[TD([[makeQuery(id+"F6.imprint","IMPRINT",EDGE,{"derivedFrom":sQuery(id+"F6.wireOp",EDGE,"E42.19.0.19")}),1.0]])]});
            var Q1075;
            Q1075=makeQuery(id+"F6.imprint","IMPRINT",FACE,{"disambiguationData":[TD([[makeQuery(id+"F6.imprint","IMPRINT",EDGE,{"derivedFrom":sQuery(id+"F6.wireOp",EDGE,"E42.19.0.1")}),1.0]])]});
            var Q1076;
            Q1076=makeQuery(id+"F6.imprint","IMPRINT",FACE,{"disambiguationData":[TD([[makeQuery(id+"F6.imprint","IMPRINT",EDGE,{"derivedFrom":sQuery(id+"F6.wireOp",EDGE,"E42.18.0.10")}),1.0]])]});
            var Q1077;
            Q1077=makeQuery(id+"F6.imprint","IMPRINT",FACE,{"disambiguationData":[TD([[makeQuery(id+"F6.imprint","IMPRINT",EDGE,{"derivedFrom":sQuery(id+"F6.wireOp",EDGE,"E42.23.0.1")}),1.0]])]});
            var Q1078;
            Q1078=makeQuery(id+"F6.imprint","IMPRINT",FACE,{"disambiguationData":[TD([[makeQuery(id+"F6.imprint","IMPRINT",EDGE,{"derivedFrom":sQuery(id+"F6.wireOp",EDGE,"E42.22.0.10")}),1.0]])]});
            var Q1079;
            Q1079=makeQuery(id+"F6.imprint","IMPRINT",FACE,{"disambiguationData":[TD([[makeQuery(id+"F6.imprint","IMPRINT",EDGE,{"derivedFrom":sQuery(id+"F6.wireOp",EDGE,"E42.21.0.19")}),1.0]])]});
            var Q1080;
            Q1080=makeQuery(id+"F6.imprint","IMPRINT",FACE,{"disambiguationData":[TD([[makeQuery(id+"F6.imprint","IMPRINT",EDGE,{"derivedFrom":sQuery(id+"F6.wireOp",EDGE,"E42.21.0.1")}),1.0]])]});
            var Q1081;
            Q1081=makeQuery(id+"F6.imprint","IMPRINT",FACE,{"disambiguationData":[TD([[makeQuery(id+"F6.imprint","IMPRINT",EDGE,{"derivedFrom":sQuery(id+"F6.wireOp",EDGE,"E42.25.0.19")}),1.0]])]});
            var Q1082;
            Q1082=makeQuery(id+"F6.imprint","IMPRINT",FACE,{"disambiguationData":[TD([[makeQuery(id+"F6.imprint","IMPRINT",EDGE,{"derivedFrom":sQuery(id+"F6.wireOp",EDGE,"E42.25.0.1")}),1.0]])]});
            var Q1083;
            Q1083=makeQuery(id+"F6.imprint","IMPRINT",FACE,{"disambiguationData":[TD([[makeQuery(id+"F6.imprint","IMPRINT",EDGE,{"derivedFrom":sQuery(id+"F6.wireOp",EDGE,"E42.24.0.10")}),1.0]])]});
            var Q1084;
            Q1084=makeQuery(id+"F6.imprint","IMPRINT",FACE,{"disambiguationData":[TD([[makeQuery(id+"F6.imprint","IMPRINT",EDGE,{"derivedFrom":sQuery(id+"F6.wireOp",EDGE,"E42.23.0.19")}),1.0]])]});
            var Q1085;
            Q1085=makeQuery(id+"F6.imprint","IMPRINT",FACE,{"disambiguationData":[TD([[makeQuery(id+"F6.imprint","IMPRINT",EDGE,{"derivedFrom":sQuery(id+"F6.wireOp",EDGE,"E42.28.0.10")}),1.0]])]});
            var Q1086;
            Q1086=makeQuery(id+"F6.imprint","IMPRINT",FACE,{"disambiguationData":[TD([[makeQuery(id+"F6.imprint","IMPRINT",EDGE,{"derivedFrom":sQuery(id+"F6.wireOp",EDGE,"E42.27.0.19")}),1.0]])]});
            var Q1087;
            Q1087=makeQuery(id+"F6.imprint","IMPRINT",FACE,{"disambiguationData":[TD([[makeQuery(id+"F6.imprint","IMPRINT",EDGE,{"derivedFrom":sQuery(id+"F6.wireOp",EDGE,"E42.27.0.1")}),1.0]])]});
            var Q1088;
            Q1088=makeQuery(id+"F6.imprint","IMPRINT",FACE,{"disambiguationData":[TD([[makeQuery(id+"F6.imprint","IMPRINT",EDGE,{"derivedFrom":sQuery(id+"F6.wireOp",EDGE,"E42.26.0.10")}),1.0]])]});
            var Q1089;
            Q1089=makeQuery(id+"F6.imprint","IMPRINT",FACE,{"disambiguationData":[TD([[makeQuery(id+"F6.imprint","IMPRINT",EDGE,{"derivedFrom":sQuery(id+"F6.wireOp",EDGE,"E42.31.0.1")}),1.0]])]});
            var Q1090;
            Q1090=makeQuery(id+"F6.imprint","IMPRINT",FACE,{"disambiguationData":[TD([[makeQuery(id+"F6.imprint","IMPRINT",EDGE,{"derivedFrom":sQuery(id+"F6.wireOp",EDGE,"E42.30.0.10")}),1.0]])]});
            var Q1091;
            Q1091=makeQuery(id+"F6.imprint","IMPRINT",FACE,{"disambiguationData":[TD([[makeQuery(id+"F6.imprint","IMPRINT",EDGE,{"derivedFrom":sQuery(id+"F6.wireOp",EDGE,"E42.29.0.19")}),1.0]])]});
            var Q1092;
            Q1092=makeQuery(id+"F6.imprint","IMPRINT",FACE,{"disambiguationData":[TD([[makeQuery(id+"F6.imprint","IMPRINT",EDGE,{"derivedFrom":sQuery(id+"F6.wireOp",EDGE,"E42.29.0.1")}),1.0]])]});
            var Q1093;
            Q1093=makeQuery(id+"F6.imprint","IMPRINT",FACE,{"disambiguationData":[TD([[makeQuery(id+"F6.imprint","IMPRINT",EDGE,{"derivedFrom":sQuery(id+"F6.wireOp",EDGE,"E42.32.0.10")}),1.0]])]});
            var Q1094;
            Q1094=makeQuery(id+"F6.imprint","IMPRINT",FACE,{"disambiguationData":[TD([[makeQuery(id+"F6.imprint","IMPRINT",EDGE,{"derivedFrom":sQuery(id+"F6.wireOp",EDGE,"E42.31.0.19")}),1.0]])]});
            var Q1095;
            Q1095=makeQuery(id+"F6.imprint","IMPRINT",FACE,{"disambiguationData":[TD([[makeQuery(id+"F6.imprint","IMPRINT",EDGE,{"derivedFrom":sQuery(id+"F6.wireOp",EDGE,"E42.5.0.20")}),1.0]])]});
            var Q1096;
            Q1096=makeQuery(id+"F6.imprint","IMPRINT",FACE,{"disambiguationData":[TD([[makeQuery(id+"F6.imprint","IMPRINT",EDGE,{"derivedFrom":sQuery(id+"F6.wireOp",EDGE,"E42.5.0.2")}),1.0]])]});
            var Q1097;
            Q1097=makeQuery(id+"F6.imprint","IMPRINT",FACE,{"disambiguationData":[TD([[makeQuery(id+"F6.imprint","IMPRINT",EDGE,{"derivedFrom":sQuery(id+"F6.wireOp",EDGE,"E42.4.0.12")}),1.0]])]});
            var Q1098;
            Q1098=makeQuery(id+"F6.imprint","IMPRINT",FACE,{"disambiguationData":[TD([[makeQuery(id+"F6.imprint","IMPRINT",EDGE,{"derivedFrom":sQuery(id+"F6.wireOp",EDGE,"E42.3.0.20")}),1.0]])]});
            var Q1099;
            Q1099=makeQuery(id+"F6.imprint","IMPRINT",FACE,{"disambiguationData":[TD([[makeQuery(id+"F6.imprint","IMPRINT",EDGE,{"derivedFrom":sQuery(id+"F6.wireOp",EDGE,"E42.8.0.12")}),1.0]])]});
            var Q1100;
            Q1100=makeQuery(id+"F6.imprint","IMPRINT",FACE,{"disambiguationData":[TD([[makeQuery(id+"F6.imprint","IMPRINT",EDGE,{"derivedFrom":sQuery(id+"F6.wireOp",EDGE,"E42.7.0.20")}),1.0]])]});
            var Q1101;
            Q1101=makeQuery(id+"F6.imprint","IMPRINT",FACE,{"disambiguationData":[TD([[makeQuery(id+"F6.imprint","IMPRINT",EDGE,{"derivedFrom":sQuery(id+"F6.wireOp",EDGE,"E42.7.0.2")}),1.0]])]});
            var Q1102;
            Q1102=makeQuery(id+"F6.imprint","IMPRINT",FACE,{"disambiguationData":[TD([[makeQuery(id+"F6.imprint","IMPRINT",EDGE,{"derivedFrom":sQuery(id+"F6.wireOp",EDGE,"E42.6.0.12")}),1.0]])]});
            var Q1103;
            Q1103=makeQuery(id+"F6.imprint","IMPRINT",FACE,{"disambiguationData":[TD([[makeQuery(id+"F6.imprint","IMPRINT",EDGE,{"derivedFrom":sQuery(id+"F6.wireOp",EDGE,"E42.11.0.2")}),1.0]])]});
            var Q1104;
            Q1104=makeQuery(id+"F6.imprint","IMPRINT",FACE,{"disambiguationData":[TD([[makeQuery(id+"F6.imprint","IMPRINT",EDGE,{"derivedFrom":sQuery(id+"F6.wireOp",EDGE,"E42.10.0.12")}),1.0]])]});
            var Q1105;
            Q1105=makeQuery(id+"F6.imprint","IMPRINT",FACE,{"disambiguationData":[TD([[makeQuery(id+"F6.imprint","IMPRINT",EDGE,{"derivedFrom":sQuery(id+"F6.wireOp",EDGE,"E42.9.0.20")}),1.0]])]});
            var Q1106;
            Q1106=makeQuery(id+"F6.imprint","IMPRINT",FACE,{"disambiguationData":[TD([[makeQuery(id+"F6.imprint","IMPRINT",EDGE,{"derivedFrom":sQuery(id+"F6.wireOp",EDGE,"E42.9.0.2")}),1.0]])]});
            var Q1107;
            Q1107=makeQuery(id+"F6.imprint","IMPRINT",FACE,{"disambiguationData":[TD([[makeQuery(id+"F6.imprint","IMPRINT",EDGE,{"derivedFrom":sQuery(id+"F6.wireOp",EDGE,"E42.13.0.20")}),1.0]])]});
            var Q1108;
            Q1108=makeQuery(id+"F6.imprint","IMPRINT",FACE,{"disambiguationData":[TD([[makeQuery(id+"F6.imprint","IMPRINT",EDGE,{"derivedFrom":sQuery(id+"F6.wireOp",EDGE,"E42.13.0.2")}),1.0]])]});
            var Q1109;
            Q1109=makeQuery(id+"F6.imprint","IMPRINT",FACE,{"disambiguationData":[TD([[makeQuery(id+"F6.imprint","IMPRINT",EDGE,{"derivedFrom":sQuery(id+"F6.wireOp",EDGE,"E42.12.0.12")}),1.0]])]});
            var Q1110;
            Q1110=makeQuery(id+"F6.imprint","IMPRINT",FACE,{"disambiguationData":[TD([[makeQuery(id+"F6.imprint","IMPRINT",EDGE,{"derivedFrom":sQuery(id+"F6.wireOp",EDGE,"E42.11.0.20")}),1.0]])]});
            var Q1111;
            Q1111=makeQuery(id+"F6.imprint","IMPRINT",FACE,{"disambiguationData":[TD([[makeQuery(id+"F6.imprint","IMPRINT",EDGE,{"derivedFrom":sQuery(id+"F6.wireOp",EDGE,"E42.16.0.12")}),1.0]])]});
            var Q1112;
            Q1112=makeQuery(id+"F6.imprint","IMPRINT",FACE,{"disambiguationData":[TD([[makeQuery(id+"F6.imprint","IMPRINT",EDGE,{"derivedFrom":sQuery(id+"F6.wireOp",EDGE,"E42.15.0.20")}),1.0]])]});
            var Q1113;
            Q1113=makeQuery(id+"F6.imprint","IMPRINT",FACE,{"disambiguationData":[TD([[makeQuery(id+"F6.imprint","IMPRINT",EDGE,{"derivedFrom":sQuery(id+"F6.wireOp",EDGE,"E42.15.0.2")}),1.0]])]});
            var Q1114;
            Q1114=makeQuery(id+"F6.imprint","IMPRINT",FACE,{"disambiguationData":[TD([[makeQuery(id+"F6.imprint","IMPRINT",EDGE,{"derivedFrom":sQuery(id+"F6.wireOp",EDGE,"E42.14.0.12")}),1.0]])]});
            var Q1115;
            Q1115=makeQuery(id+"F6.imprint","IMPRINT",FACE,{"disambiguationData":[TD([[makeQuery(id+"F6.imprint","IMPRINT",EDGE,{"derivedFrom":sQuery(id+"F6.wireOp",EDGE,"E42.17.0.2")}),1.0]])]});
            var Q1116;
            Q1116=makeQuery(id+"F6.imprint","IMPRINT",FACE,{"disambiguationData":[TD([[makeQuery(id+"F6.imprint","IMPRINT",EDGE,{"derivedFrom":sQuery(id+"F6.wireOp",EDGE,"E42.17.0.20")}),1.0]])]});
            var Q1117;
            Q1117=makeQuery(id+"F6.imprint","IMPRINT",FACE,{"disambiguationData":[TD([[makeQuery(id+"F6.imprint","IMPRINT",EDGE,{"derivedFrom":sQuery(id+"F6.wireOp",EDGE,"E42.20.0.12")}),1.0]])]});
            var Q1118;
            Q1118=makeQuery(id+"F6.imprint","IMPRINT",FACE,{"disambiguationData":[TD([[makeQuery(id+"F6.imprint","IMPRINT",EDGE,{"derivedFrom":sQuery(id+"F6.wireOp",EDGE,"E42.19.0.20")}),1.0]])]});
            var Q1119;
            Q1119=makeQuery(id+"F6.imprint","IMPRINT",FACE,{"disambiguationData":[TD([[makeQuery(id+"F6.imprint","IMPRINT",EDGE,{"derivedFrom":sQuery(id+"F6.wireOp",EDGE,"E42.19.0.2")}),1.0]])]});
            var Q1120;
            Q1120=makeQuery(id+"F6.imprint","IMPRINT",FACE,{"disambiguationData":[TD([[makeQuery(id+"F6.imprint","IMPRINT",EDGE,{"derivedFrom":sQuery(id+"F6.wireOp",EDGE,"E42.18.0.12")}),1.0]])]});
            var Q1121;
            Q1121=makeQuery(id+"F6.imprint","IMPRINT",FACE,{"disambiguationData":[TD([[makeQuery(id+"F6.imprint","IMPRINT",EDGE,{"derivedFrom":sQuery(id+"F6.wireOp",EDGE,"E318.MirrorC")}),-1.0]])]});
            var Q1122;
            Q1122=makeQuery(id+"F6.imprint","IMPRINT",FACE,{"disambiguationData":[TD([[makeQuery(id+"F6.imprint","IMPRINT",EDGE,{"derivedFrom":sQuery(id+"F6.wireOp",EDGE,"E333.MirrorC")}),-1.0]])]});
            var Q1123;
            Q1123=makeQuery(id+"F6.imprint","IMPRINT",FACE,{"disambiguationData":[TD([[makeQuery(id+"F6.imprint","IMPRINT",EDGE,{"derivedFrom":sQuery(id+"F6.wireOp",EDGE,"E302.MirrorC")}),-1.0]])]});
            var Q1124;
            Q1124=makeQuery(id+"F6.imprint","IMPRINT",FACE,{"disambiguationData":[TD([[makeQuery(id+"F6.imprint","IMPRINT",EDGE,{"derivedFrom":sQuery(id+"F6.wireOp",EDGE,"E286.MirrorC")}),-1.0]])]});
            var Q1125;
            Q1125=makeQuery(id+"F6.imprint","IMPRINT",FACE,{"disambiguationData":[TD([[makeQuery(id+"F6.imprint","IMPRINT",EDGE,{"derivedFrom":sQuery(id+"F6.wireOp",EDGE,"E270.MirrorC")}),-1.0]])]});
            var Q1126;
            Q1126=makeQuery(id+"F6.imprint","IMPRINT",FACE,{"disambiguationData":[TD([[makeQuery(id+"F6.imprint","IMPRINT",EDGE,{"derivedFrom":sQuery(id+"F6.wireOp",EDGE,"E256.MirrorC")}),-1.0]])]});
            var Q1127;
            Q1127=makeQuery(id+"F6.imprint","IMPRINT",FACE,{"disambiguationData":[TD([[makeQuery(id+"F6.imprint","IMPRINT",EDGE,{"derivedFrom":sQuery(id+"F6.wireOp",EDGE,"E42.3.0.2")}),1.0]])]});
            var Q1128;
            Q1128=makeQuery(id+"F6.imprint","IMPRINT",FACE,{"disambiguationData":[TD([[makeQuery(id+"F6.imprint","IMPRINT",EDGE,{"derivedFrom":sQuery(id+"F6.wireOp",EDGE,"E42.2.0.12")}),1.0]])]});
            var Q1129;
            Q1129=makeQuery(id+"F6.imprint","IMPRINT",FACE,{"disambiguationData":[TD([[makeQuery(id+"F6.imprint","IMPRINT",EDGE,{"derivedFrom":sQuery(id+"F6.wireOp",EDGE,"E42.1.0.20")}),1.0]])]});
            var Q1130;
            Q1130=makeQuery(id+"F6.imprint","IMPRINT",FACE,{"disambiguationData":[TD([[makeQuery(id+"F6.imprint","IMPRINT",EDGE,{"derivedFrom":sQuery(id+"F6.wireOp",EDGE,"E42.1.0.2")}),1.0]])]});
            var Q1131;
            Q1131=makeQuery(id+"F6.imprint","IMPRINT",FACE,{"disambiguationData":[TD([[makeQuery(id+"F6.imprint","IMPRINT",EDGE,{"derivedFrom":sQuery(id+"F6.wireOp",EDGE,"E42.23.0.2")}),1.0]])]});
            var Q1132;
            Q1132=makeQuery(id+"F6.imprint","IMPRINT",FACE,{"disambiguationData":[TD([[makeQuery(id+"F6.imprint","IMPRINT",EDGE,{"derivedFrom":sQuery(id+"F6.wireOp",EDGE,"E42.22.0.12")}),1.0]])]});
            var Q1133;
            Q1133=makeQuery(id+"F6.imprint","IMPRINT",FACE,{"disambiguationData":[TD([[makeQuery(id+"F6.imprint","IMPRINT",EDGE,{"derivedFrom":sQuery(id+"F6.wireOp",EDGE,"E42.21.0.20")}),1.0]])]});
            var Q1134;
            Q1134=makeQuery(id+"F6.imprint","IMPRINT",FACE,{"disambiguationData":[TD([[makeQuery(id+"F6.imprint","IMPRINT",EDGE,{"derivedFrom":sQuery(id+"F6.wireOp",EDGE,"E42.21.0.2")}),1.0]])]});
            var Q1135;
            Q1135=makeQuery(id+"F6.imprint","IMPRINT",FACE,{"disambiguationData":[TD([[makeQuery(id+"F6.imprint","IMPRINT",EDGE,{"derivedFrom":sQuery(id+"F6.wireOp",EDGE,"E42.25.0.20")}),1.0]])]});
            var Q1136;
            Q1136=makeQuery(id+"F6.imprint","IMPRINT",FACE,{"disambiguationData":[TD([[makeQuery(id+"F6.imprint","IMPRINT",EDGE,{"derivedFrom":sQuery(id+"F6.wireOp",EDGE,"E42.25.0.2")}),1.0]])]});
            var Q1137;
            Q1137=makeQuery(id+"F6.imprint","IMPRINT",FACE,{"disambiguationData":[TD([[makeQuery(id+"F6.imprint","IMPRINT",EDGE,{"derivedFrom":sQuery(id+"F6.wireOp",EDGE,"E42.24.0.12")}),1.0]])]});
            var Q1138;
            Q1138=makeQuery(id+"F6.imprint","IMPRINT",FACE,{"disambiguationData":[TD([[makeQuery(id+"F6.imprint","IMPRINT",EDGE,{"derivedFrom":sQuery(id+"F6.wireOp",EDGE,"E42.23.0.20")}),1.0]])]});
            var Q1139;
            Q1139=makeQuery(id+"F6.imprint","IMPRINT",FACE,{"disambiguationData":[TD([[makeQuery(id+"F6.imprint","IMPRINT",EDGE,{"derivedFrom":sQuery(id+"F6.wireOp",EDGE,"E42.28.0.12")}),1.0]])]});
            var Q1140;
            Q1140=makeQuery(id+"F6.imprint","IMPRINT",FACE,{"disambiguationData":[TD([[makeQuery(id+"F6.imprint","IMPRINT",EDGE,{"derivedFrom":sQuery(id+"F6.wireOp",EDGE,"E42.27.0.20")}),1.0]])]});
            var Q1141;
            Q1141=makeQuery(id+"F6.imprint","IMPRINT",FACE,{"disambiguationData":[TD([[makeQuery(id+"F6.imprint","IMPRINT",EDGE,{"derivedFrom":sQuery(id+"F6.wireOp",EDGE,"E42.27.0.2")}),1.0]])]});
            var Q1142;
            Q1142=makeQuery(id+"F6.imprint","IMPRINT",FACE,{"disambiguationData":[TD([[makeQuery(id+"F6.imprint","IMPRINT",EDGE,{"derivedFrom":sQuery(id+"F6.wireOp",EDGE,"E42.26.0.12")}),1.0]])]});
            var Q1143;
            Q1143=makeQuery(id+"F6.imprint","IMPRINT",FACE,{"disambiguationData":[TD([[makeQuery(id+"F6.imprint","IMPRINT",EDGE,{"derivedFrom":sQuery(id+"F6.wireOp",EDGE,"E42.31.0.2")}),1.0]])]});
            var Q1144;
            Q1144=makeQuery(id+"F6.imprint","IMPRINT",FACE,{"disambiguationData":[TD([[makeQuery(id+"F6.imprint","IMPRINT",EDGE,{"derivedFrom":sQuery(id+"F6.wireOp",EDGE,"E42.30.0.12")}),1.0]])]});
            var Q1145;
            Q1145=makeQuery(id+"F6.imprint","IMPRINT",FACE,{"disambiguationData":[TD([[makeQuery(id+"F6.imprint","IMPRINT",EDGE,{"derivedFrom":sQuery(id+"F6.wireOp",EDGE,"E42.29.0.20")}),1.0]])]});
            var Q1146;
            Q1146=makeQuery(id+"F6.imprint","IMPRINT",FACE,{"disambiguationData":[TD([[makeQuery(id+"F6.imprint","IMPRINT",EDGE,{"derivedFrom":sQuery(id+"F6.wireOp",EDGE,"E42.29.0.2")}),1.0]])]});
            var Q1147;
            Q1147=makeQuery(id+"F6.imprint","IMPRINT",FACE,{"disambiguationData":[TD([[makeQuery(id+"F6.imprint","IMPRINT",EDGE,{"derivedFrom":sQuery(id+"F6.wireOp",EDGE,"E42.32.0.12")}),1.0]])]});
            var Q1148;
            Q1148=makeQuery(id+"F6.imprint","IMPRINT",FACE,{"disambiguationData":[TD([[makeQuery(id+"F6.imprint","IMPRINT",EDGE,{"derivedFrom":sQuery(id+"F6.wireOp",EDGE,"E42.31.0.20")}),1.0]])]});
            var Q1149;
            Q1149=makeQuery(id+"F6.imprint","IMPRINT",FACE,{"disambiguationData":[TD([[makeQuery(id+"F6.imprint","IMPRINT",EDGE,{"derivedFrom":sQuery(id+"F6.wireOp",EDGE,"E42.8.0.13")}),1.0]])]});
            var Q1150;
            Q1150=makeQuery(id+"F6.imprint","IMPRINT",FACE,{"disambiguationData":[TD([[makeQuery(id+"F6.imprint","IMPRINT",EDGE,{"derivedFrom":sQuery(id+"F6.wireOp",EDGE,"E42.7.0.21")}),1.0]])]});
            var Q1151;
            Q1151=makeQuery(id+"F6.imprint","IMPRINT",FACE,{"disambiguationData":[TD([[makeQuery(id+"F6.imprint","IMPRINT",EDGE,{"derivedFrom":sQuery(id+"F6.wireOp",EDGE,"E42.7.0.4")}),1.0]])]});
            var Q1152;
            Q1152=makeQuery(id+"F6.imprint","IMPRINT",FACE,{"disambiguationData":[TD([[makeQuery(id+"F6.imprint","IMPRINT",EDGE,{"derivedFrom":sQuery(id+"F6.wireOp",EDGE,"E42.6.0.13")}),1.0]])]});
            var Q1153;
            Q1153=makeQuery(id+"F6.imprint","IMPRINT",FACE,{"disambiguationData":[TD([[makeQuery(id+"F6.imprint","IMPRINT",EDGE,{"derivedFrom":sQuery(id+"F6.wireOp",EDGE,"E42.11.0.4")}),1.0]])]});
            var Q1154;
            Q1154=makeQuery(id+"F6.imprint","IMPRINT",FACE,{"disambiguationData":[TD([[makeQuery(id+"F6.imprint","IMPRINT",EDGE,{"derivedFrom":sQuery(id+"F6.wireOp",EDGE,"E42.10.0.13")}),1.0]])]});
            var Q1155;
            Q1155=makeQuery(id+"F6.imprint","IMPRINT",FACE,{"disambiguationData":[TD([[makeQuery(id+"F6.imprint","IMPRINT",EDGE,{"derivedFrom":sQuery(id+"F6.wireOp",EDGE,"E42.9.0.21")}),1.0]])]});
            var Q1156;
            Q1156=makeQuery(id+"F6.imprint","IMPRINT",FACE,{"disambiguationData":[TD([[makeQuery(id+"F6.imprint","IMPRINT",EDGE,{"derivedFrom":sQuery(id+"F6.wireOp",EDGE,"E42.9.0.4")}),1.0]])]});
            var Q1157;
            Q1157=makeQuery(id+"F6.imprint","IMPRINT",FACE,{"disambiguationData":[TD([[makeQuery(id+"F6.imprint","IMPRINT",EDGE,{"derivedFrom":sQuery(id+"F6.wireOp",EDGE,"E42.13.0.21")}),1.0]])]});
            var Q1158;
            Q1158=makeQuery(id+"F6.imprint","IMPRINT",FACE,{"disambiguationData":[TD([[makeQuery(id+"F6.imprint","IMPRINT",EDGE,{"derivedFrom":sQuery(id+"F6.wireOp",EDGE,"E42.13.0.4")}),1.0]])]});
            var Q1159;
            Q1159=makeQuery(id+"F6.imprint","IMPRINT",FACE,{"disambiguationData":[TD([[makeQuery(id+"F6.imprint","IMPRINT",EDGE,{"derivedFrom":sQuery(id+"F6.wireOp",EDGE,"E42.12.0.13")}),1.0]])]});
            var Q1160;
            Q1160=makeQuery(id+"F6.imprint","IMPRINT",FACE,{"disambiguationData":[TD([[makeQuery(id+"F6.imprint","IMPRINT",EDGE,{"derivedFrom":sQuery(id+"F6.wireOp",EDGE,"E42.11.0.21")}),1.0]])]});
            var Q1161;
            Q1161=makeQuery(id+"F6.imprint","IMPRINT",FACE,{"disambiguationData":[TD([[makeQuery(id+"F6.imprint","IMPRINT",EDGE,{"derivedFrom":sQuery(id+"F6.wireOp",EDGE,"E42.16.0.13")}),1.0]])]});
            var Q1162;
            Q1162=makeQuery(id+"F6.imprint","IMPRINT",FACE,{"disambiguationData":[TD([[makeQuery(id+"F6.imprint","IMPRINT",EDGE,{"derivedFrom":sQuery(id+"F6.wireOp",EDGE,"E42.15.0.21")}),1.0]])]});
            var Q1163;
            Q1163=makeQuery(id+"F6.imprint","IMPRINT",FACE,{"disambiguationData":[TD([[makeQuery(id+"F6.imprint","IMPRINT",EDGE,{"derivedFrom":sQuery(id+"F6.wireOp",EDGE,"E42.15.0.4")}),1.0]])]});
            var Q1164;
            Q1164=makeQuery(id+"F6.imprint","IMPRINT",FACE,{"disambiguationData":[TD([[makeQuery(id+"F6.imprint","IMPRINT",EDGE,{"derivedFrom":sQuery(id+"F6.wireOp",EDGE,"E42.14.0.13")}),1.0]])]});
            var Q1165;
            Q1165=makeQuery(id+"F6.imprint","IMPRINT",FACE,{"disambiguationData":[TD([[makeQuery(id+"F6.imprint","IMPRINT",EDGE,{"derivedFrom":sQuery(id+"F6.wireOp",EDGE,"E42.17.0.4")}),1.0]])]});
            var Q1166;
            Q1166=makeQuery(id+"F6.imprint","IMPRINT",FACE,{"disambiguationData":[TD([[makeQuery(id+"F6.imprint","IMPRINT",EDGE,{"derivedFrom":sQuery(id+"F6.wireOp",EDGE,"E42.17.0.21")}),1.0]])]});
            var Q1167;
            Q1167=makeQuery(id+"F6.imprint","IMPRINT",FACE,{"disambiguationData":[TD([[makeQuery(id+"F6.imprint","IMPRINT",EDGE,{"derivedFrom":sQuery(id+"F6.wireOp",EDGE,"E42.20.0.13")}),1.0]])]});
            var Q1168;
            Q1168=makeQuery(id+"F6.imprint","IMPRINT",FACE,{"disambiguationData":[TD([[makeQuery(id+"F6.imprint","IMPRINT",EDGE,{"derivedFrom":sQuery(id+"F6.wireOp",EDGE,"E42.19.0.21")}),1.0]])]});
            var Q1169;
            Q1169=makeQuery(id+"F6.imprint","IMPRINT",FACE,{"disambiguationData":[TD([[makeQuery(id+"F6.imprint","IMPRINT",EDGE,{"derivedFrom":sQuery(id+"F6.wireOp",EDGE,"E42.19.0.4")}),1.0]])]});
            var Q1170;
            Q1170=makeQuery(id+"F6.imprint","IMPRINT",FACE,{"disambiguationData":[TD([[makeQuery(id+"F6.imprint","IMPRINT",EDGE,{"derivedFrom":sQuery(id+"F6.wireOp",EDGE,"E42.18.0.13")}),1.0]])]});
            var Q1171;
            Q1171=makeQuery(id+"F6.imprint","IMPRINT",FACE,{"disambiguationData":[TD([[makeQuery(id+"F6.imprint","IMPRINT",EDGE,{"derivedFrom":sQuery(id+"F6.wireOp",EDGE,"E42.23.0.4")}),1.0]])]});
            var Q1172;
            Q1172=makeQuery(id+"F6.imprint","IMPRINT",FACE,{"disambiguationData":[TD([[makeQuery(id+"F6.imprint","IMPRINT",EDGE,{"derivedFrom":sQuery(id+"F6.wireOp",EDGE,"E42.22.0.13")}),1.0]])]});
            var Q1173;
            Q1173=makeQuery(id+"F6.imprint","IMPRINT",FACE,{"disambiguationData":[TD([[makeQuery(id+"F6.imprint","IMPRINT",EDGE,{"derivedFrom":sQuery(id+"F6.wireOp",EDGE,"E42.21.0.21")}),1.0]])]});
            var Q1174;
            Q1174=makeQuery(id+"F6.imprint","IMPRINT",FACE,{"disambiguationData":[TD([[makeQuery(id+"F6.imprint","IMPRINT",EDGE,{"derivedFrom":sQuery(id+"F6.wireOp",EDGE,"E42.21.0.4")}),1.0]])]});
            var Q1175;
            Q1175=makeQuery(id+"F6.imprint","IMPRINT",FACE,{"disambiguationData":[TD([[makeQuery(id+"F6.imprint","IMPRINT",EDGE,{"derivedFrom":sQuery(id+"F6.wireOp",EDGE,"E334.MirrorC")}),-1.0]])]});
            var Q1176;
            Q1176=makeQuery(id+"F6.imprint","IMPRINT",FACE,{"disambiguationData":[TD([[makeQuery(id+"F6.imprint","IMPRINT",EDGE,{"derivedFrom":sQuery(id+"F6.wireOp",EDGE,"E303.MirrorC")}),-1.0]])]});
            var Q1177;
            Q1177=makeQuery(id+"F6.imprint","IMPRINT",FACE,{"disambiguationData":[TD([[makeQuery(id+"F6.imprint","IMPRINT",EDGE,{"derivedFrom":sQuery(id+"F6.wireOp",EDGE,"E287.MirrorC")}),-1.0]])]});
            var Q1178;
            Q1178=makeQuery(id+"F6.imprint","IMPRINT",FACE,{"disambiguationData":[TD([[makeQuery(id+"F6.imprint","IMPRINT",EDGE,{"derivedFrom":sQuery(id+"F6.wireOp",EDGE,"E271.MirrorC")}),-1.0]])]});
            var Q1179;
            Q1179=makeQuery(id+"F6.imprint","IMPRINT",FACE,{"disambiguationData":[TD([[makeQuery(id+"F6.imprint","IMPRINT",EDGE,{"derivedFrom":sQuery(id+"F6.wireOp",EDGE,"E257.MirrorC")}),-1.0]])]});
            var Q1180;
            Q1180=makeQuery(id+"F6.imprint","IMPRINT",FACE,{"disambiguationData":[TD([[makeQuery(id+"F6.imprint","IMPRINT",EDGE,{"derivedFrom":sQuery(id+"F6.wireOp",EDGE,"E42.3.0.4")}),1.0]])]});
            var Q1181;
            Q1181=makeQuery(id+"F6.imprint","IMPRINT",FACE,{"disambiguationData":[TD([[makeQuery(id+"F6.imprint","IMPRINT",EDGE,{"derivedFrom":sQuery(id+"F6.wireOp",EDGE,"E42.2.0.13")}),1.0]])]});
            var Q1182;
            Q1182=makeQuery(id+"F6.imprint","IMPRINT",FACE,{"disambiguationData":[TD([[makeQuery(id+"F6.imprint","IMPRINT",EDGE,{"derivedFrom":sQuery(id+"F6.wireOp",EDGE,"E42.1.0.21")}),1.0]])]});
            var Q1183;
            Q1183=makeQuery(id+"F6.imprint","IMPRINT",FACE,{"disambiguationData":[TD([[makeQuery(id+"F6.imprint","IMPRINT",EDGE,{"derivedFrom":sQuery(id+"F6.wireOp",EDGE,"E42.1.0.4")}),1.0]])]});
            var Q1184;
            Q1184=makeQuery(id+"F6.imprint","IMPRINT",FACE,{"disambiguationData":[TD([[makeQuery(id+"F6.imprint","IMPRINT",EDGE,{"derivedFrom":sQuery(id+"F6.wireOp",EDGE,"E42.5.0.21")}),1.0]])]});
            var Q1185;
            Q1185=makeQuery(id+"F6.imprint","IMPRINT",FACE,{"disambiguationData":[TD([[makeQuery(id+"F6.imprint","IMPRINT",EDGE,{"derivedFrom":sQuery(id+"F6.wireOp",EDGE,"E42.5.0.4")}),1.0]])]});
            var Q1186;
            Q1186=makeQuery(id+"F6.imprint","IMPRINT",FACE,{"disambiguationData":[TD([[makeQuery(id+"F6.imprint","IMPRINT",EDGE,{"derivedFrom":sQuery(id+"F6.wireOp",EDGE,"E42.4.0.13")}),1.0]])]});
            var Q1187;
            Q1187=makeQuery(id+"F6.imprint","IMPRINT",FACE,{"disambiguationData":[TD([[makeQuery(id+"F6.imprint","IMPRINT",EDGE,{"derivedFrom":sQuery(id+"F6.wireOp",EDGE,"E42.3.0.21")}),1.0]])]});
            var Q1188;
            Q1188=makeQuery(id+"F6.imprint","IMPRINT",FACE,{"disambiguationData":[TD([[makeQuery(id+"F6.imprint","IMPRINT",EDGE,{"derivedFrom":sQuery(id+"F6.wireOp",EDGE,"E319.MirrorC")}),-1.0]])]});
            var Q1189;
            Q1189=makeQuery(id+"F6.imprint","IMPRINT",FACE,{"disambiguationData":[TD([[makeQuery(id+"F6.imprint","IMPRINT",EDGE,{"derivedFrom":sQuery(id+"F6.wireOp",EDGE,"E42.25.0.21")}),1.0]])]});
            var Q1190;
            Q1190=makeQuery(id+"F6.imprint","IMPRINT",FACE,{"disambiguationData":[TD([[makeQuery(id+"F6.imprint","IMPRINT",EDGE,{"derivedFrom":sQuery(id+"F6.wireOp",EDGE,"E42.25.0.4")}),1.0]])]});
            var Q1191;
            Q1191=makeQuery(id+"F6.imprint","IMPRINT",FACE,{"disambiguationData":[TD([[makeQuery(id+"F6.imprint","IMPRINT",EDGE,{"derivedFrom":sQuery(id+"F6.wireOp",EDGE,"E42.24.0.13")}),1.0]])]});
            var Q1192;
            Q1192=makeQuery(id+"F6.imprint","IMPRINT",FACE,{"disambiguationData":[TD([[makeQuery(id+"F6.imprint","IMPRINT",EDGE,{"derivedFrom":sQuery(id+"F6.wireOp",EDGE,"E42.23.0.21")}),1.0]])]});
            var Q1193;
            Q1193=makeQuery(id+"F6.imprint","IMPRINT",FACE,{"disambiguationData":[TD([[makeQuery(id+"F6.imprint","IMPRINT",EDGE,{"derivedFrom":sQuery(id+"F6.wireOp",EDGE,"E42.28.0.13")}),1.0]])]});
            var Q1194;
            Q1194=makeQuery(id+"F6.imprint","IMPRINT",FACE,{"disambiguationData":[TD([[makeQuery(id+"F6.imprint","IMPRINT",EDGE,{"derivedFrom":sQuery(id+"F6.wireOp",EDGE,"E42.27.0.21")}),1.0]])]});
            var Q1195;
            Q1195=makeQuery(id+"F6.imprint","IMPRINT",FACE,{"disambiguationData":[TD([[makeQuery(id+"F6.imprint","IMPRINT",EDGE,{"derivedFrom":sQuery(id+"F6.wireOp",EDGE,"E42.27.0.4")}),1.0]])]});
            var Q1196;
            Q1196=makeQuery(id+"F6.imprint","IMPRINT",FACE,{"disambiguationData":[TD([[makeQuery(id+"F6.imprint","IMPRINT",EDGE,{"derivedFrom":sQuery(id+"F6.wireOp",EDGE,"E42.26.0.13")}),1.0]])]});
            var Q1197;
            Q1197=makeQuery(id+"F6.imprint","IMPRINT",FACE,{"disambiguationData":[TD([[makeQuery(id+"F6.imprint","IMPRINT",EDGE,{"derivedFrom":sQuery(id+"F6.wireOp",EDGE,"E42.31.0.4")}),1.0]])]});
            var Q1198;
            Q1198=makeQuery(id+"F6.imprint","IMPRINT",FACE,{"disambiguationData":[TD([[makeQuery(id+"F6.imprint","IMPRINT",EDGE,{"derivedFrom":sQuery(id+"F6.wireOp",EDGE,"E42.30.0.13")}),1.0]])]});
            var Q1199;
            Q1199=makeQuery(id+"F6.imprint","IMPRINT",FACE,{"disambiguationData":[TD([[makeQuery(id+"F6.imprint","IMPRINT",EDGE,{"derivedFrom":sQuery(id+"F6.wireOp",EDGE,"E42.29.0.21")}),1.0]])]});
            var Q1200;
            Q1200=makeQuery(id+"F6.imprint","IMPRINT",FACE,{"disambiguationData":[TD([[makeQuery(id+"F6.imprint","IMPRINT",EDGE,{"derivedFrom":sQuery(id+"F6.wireOp",EDGE,"E42.29.0.4")}),1.0]])]});
            var Q1201;
            Q1201=makeQuery(id+"F6.imprint","IMPRINT",FACE,{"disambiguationData":[TD([[makeQuery(id+"F6.imprint","IMPRINT",EDGE,{"derivedFrom":sQuery(id+"F6.wireOp",EDGE,"E42.32.0.13")}),1.0]])]});
            var Q1202;
            Q1202=makeQuery(id+"F6.imprint","IMPRINT",FACE,{"disambiguationData":[TD([[makeQuery(id+"F6.imprint","IMPRINT",EDGE,{"derivedFrom":sQuery(id+"F6.wireOp",EDGE,"E42.31.0.21")}),1.0]])]});
            var Q1203;
            Q1203=makeQuery(id+"F6.imprint","IMPRINT",FACE,{"disambiguationData":[TD([[makeQuery(id+"F6.imprint","IMPRINT",EDGE,{"derivedFrom":sQuery(id+"F6.wireOp",EDGE,"E42.11.0.5")}),1.0]])]});
            var Q1204;
            Q1204=makeQuery(id+"F6.imprint","IMPRINT",FACE,{"disambiguationData":[TD([[makeQuery(id+"F6.imprint","IMPRINT",EDGE,{"derivedFrom":sQuery(id+"F6.wireOp",EDGE,"E42.10.0.14")}),1.0]])]});
            var Q1205;
            Q1205=makeQuery(id+"F6.imprint","IMPRINT",FACE,{"disambiguationData":[TD([[makeQuery(id+"F6.imprint","IMPRINT",EDGE,{"derivedFrom":sQuery(id+"F6.wireOp",EDGE,"E42.9.0.22")}),1.0]])]});
            var Q1206;
            Q1206=makeQuery(id+"F6.imprint","IMPRINT",FACE,{"disambiguationData":[TD([[makeQuery(id+"F6.imprint","IMPRINT",EDGE,{"derivedFrom":sQuery(id+"F6.wireOp",EDGE,"E42.9.0.5")}),1.0]])]});
            var Q1207;
            Q1207=makeQuery(id+"F6.imprint","IMPRINT",FACE,{"disambiguationData":[TD([[makeQuery(id+"F6.imprint","IMPRINT",EDGE,{"derivedFrom":sQuery(id+"F6.wireOp",EDGE,"E42.13.0.22")}),1.0]])]});
            var Q1208;
            Q1208=makeQuery(id+"F6.imprint","IMPRINT",FACE,{"disambiguationData":[TD([[makeQuery(id+"F6.imprint","IMPRINT",EDGE,{"derivedFrom":sQuery(id+"F6.wireOp",EDGE,"E42.13.0.5")}),1.0]])]});
            var Q1209;
            Q1209=makeQuery(id+"F6.imprint","IMPRINT",FACE,{"disambiguationData":[TD([[makeQuery(id+"F6.imprint","IMPRINT",EDGE,{"derivedFrom":sQuery(id+"F6.wireOp",EDGE,"E42.12.0.14")}),1.0]])]});
            var Q1210;
            Q1210=makeQuery(id+"F6.imprint","IMPRINT",FACE,{"disambiguationData":[TD([[makeQuery(id+"F6.imprint","IMPRINT",EDGE,{"derivedFrom":sQuery(id+"F6.wireOp",EDGE,"E42.11.0.22")}),1.0]])]});
            var Q1211;
            Q1211=makeQuery(id+"F6.imprint","IMPRINT",FACE,{"disambiguationData":[TD([[makeQuery(id+"F6.imprint","IMPRINT",EDGE,{"derivedFrom":sQuery(id+"F6.wireOp",EDGE,"E42.16.0.14")}),1.0]])]});
            var Q1212;
            Q1212=makeQuery(id+"F6.imprint","IMPRINT",FACE,{"disambiguationData":[TD([[makeQuery(id+"F6.imprint","IMPRINT",EDGE,{"derivedFrom":sQuery(id+"F6.wireOp",EDGE,"E42.15.0.22")}),1.0]])]});
            var Q1213;
            Q1213=makeQuery(id+"F6.imprint","IMPRINT",FACE,{"disambiguationData":[TD([[makeQuery(id+"F6.imprint","IMPRINT",EDGE,{"derivedFrom":sQuery(id+"F6.wireOp",EDGE,"E42.15.0.5")}),1.0]])]});
            var Q1214;
            Q1214=makeQuery(id+"F6.imprint","IMPRINT",FACE,{"disambiguationData":[TD([[makeQuery(id+"F6.imprint","IMPRINT",EDGE,{"derivedFrom":sQuery(id+"F6.wireOp",EDGE,"E42.14.0.14")}),1.0]])]});
            var Q1215;
            Q1215=makeQuery(id+"F6.imprint","IMPRINT",FACE,{"disambiguationData":[TD([[makeQuery(id+"F6.imprint","IMPRINT",EDGE,{"derivedFrom":sQuery(id+"F6.wireOp",EDGE,"E42.17.0.5")}),1.0]])]});
            var Q1216;
            Q1216=makeQuery(id+"F6.imprint","IMPRINT",FACE,{"disambiguationData":[TD([[makeQuery(id+"F6.imprint","IMPRINT",EDGE,{"derivedFrom":sQuery(id+"F6.wireOp",EDGE,"E42.17.0.22")}),1.0]])]});
            var Q1217;
            Q1217=makeQuery(id+"F6.imprint","IMPRINT",FACE,{"disambiguationData":[TD([[makeQuery(id+"F6.imprint","IMPRINT",EDGE,{"derivedFrom":sQuery(id+"F6.wireOp",EDGE,"E42.20.0.14")}),1.0]])]});
            var Q1218;
            Q1218=makeQuery(id+"F6.imprint","IMPRINT",FACE,{"disambiguationData":[TD([[makeQuery(id+"F6.imprint","IMPRINT",EDGE,{"derivedFrom":sQuery(id+"F6.wireOp",EDGE,"E42.19.0.22")}),1.0]])]});
            var Q1219;
            Q1219=makeQuery(id+"F6.imprint","IMPRINT",FACE,{"disambiguationData":[TD([[makeQuery(id+"F6.imprint","IMPRINT",EDGE,{"derivedFrom":sQuery(id+"F6.wireOp",EDGE,"E42.19.0.5")}),1.0]])]});
            var Q1220;
            Q1220=makeQuery(id+"F6.imprint","IMPRINT",FACE,{"disambiguationData":[TD([[makeQuery(id+"F6.imprint","IMPRINT",EDGE,{"derivedFrom":sQuery(id+"F6.wireOp",EDGE,"E42.18.0.14")}),1.0]])]});
            var Q1221;
            Q1221=makeQuery(id+"F6.imprint","IMPRINT",FACE,{"disambiguationData":[TD([[makeQuery(id+"F6.imprint","IMPRINT",EDGE,{"derivedFrom":sQuery(id+"F6.wireOp",EDGE,"E42.23.0.5")}),1.0]])]});
            var Q1222;
            Q1222=makeQuery(id+"F6.imprint","IMPRINT",FACE,{"disambiguationData":[TD([[makeQuery(id+"F6.imprint","IMPRINT",EDGE,{"derivedFrom":sQuery(id+"F6.wireOp",EDGE,"E42.22.0.14")}),1.0]])]});
            var Q1223;
            Q1223=makeQuery(id+"F6.imprint","IMPRINT",FACE,{"disambiguationData":[TD([[makeQuery(id+"F6.imprint","IMPRINT",EDGE,{"derivedFrom":sQuery(id+"F6.wireOp",EDGE,"E42.21.0.22")}),1.0]])]});
            var Q1224;
            Q1224=makeQuery(id+"F6.imprint","IMPRINT",FACE,{"disambiguationData":[TD([[makeQuery(id+"F6.imprint","IMPRINT",EDGE,{"derivedFrom":sQuery(id+"F6.wireOp",EDGE,"E42.21.0.5")}),1.0]])]});
            var Q1225;
            Q1225=makeQuery(id+"F6.imprint","IMPRINT",FACE,{"disambiguationData":[TD([[makeQuery(id+"F6.imprint","IMPRINT",EDGE,{"derivedFrom":sQuery(id+"F6.wireOp",EDGE,"E42.25.0.22")}),1.0]])]});
            var Q1226;
            Q1226=makeQuery(id+"F6.imprint","IMPRINT",FACE,{"disambiguationData":[TD([[makeQuery(id+"F6.imprint","IMPRINT",EDGE,{"derivedFrom":sQuery(id+"F6.wireOp",EDGE,"E42.25.0.5")}),1.0]])]});
            var Q1227;
            Q1227=makeQuery(id+"F6.imprint","IMPRINT",FACE,{"disambiguationData":[TD([[makeQuery(id+"F6.imprint","IMPRINT",EDGE,{"derivedFrom":sQuery(id+"F6.wireOp",EDGE,"E42.24.0.14")}),1.0]])]});
            var Q1228;
            Q1228=makeQuery(id+"F6.imprint","IMPRINT",FACE,{"disambiguationData":[TD([[makeQuery(id+"F6.imprint","IMPRINT",EDGE,{"derivedFrom":sQuery(id+"F6.wireOp",EDGE,"E42.23.0.22")}),1.0]])]});
            var Q1229;
            Q1229=makeQuery(id+"F6.imprint","IMPRINT",FACE,{"disambiguationData":[TD([[makeQuery(id+"F6.imprint","IMPRINT",EDGE,{"derivedFrom":sQuery(id+"F6.wireOp",EDGE,"E335.MirrorC")}),-1.0]])]});
            var Q1230;
            Q1230=makeQuery(id+"F6.imprint","IMPRINT",FACE,{"disambiguationData":[TD([[makeQuery(id+"F6.imprint","IMPRINT",EDGE,{"derivedFrom":sQuery(id+"F6.wireOp",EDGE,"E304.MirrorC")}),-1.0]])]});
            var Q1231;
            Q1231=makeQuery(id+"F6.imprint","IMPRINT",FACE,{"disambiguationData":[TD([[makeQuery(id+"F6.imprint","IMPRINT",EDGE,{"derivedFrom":sQuery(id+"F6.wireOp",EDGE,"E288.MirrorC")}),-1.0]])]});
            var Q1232;
            Q1232=makeQuery(id+"F6.imprint","IMPRINT",FACE,{"disambiguationData":[TD([[makeQuery(id+"F6.imprint","IMPRINT",EDGE,{"derivedFrom":sQuery(id+"F6.wireOp",EDGE,"E272.MirrorC")}),-1.0]])]});
            var Q1233;
            Q1233=makeQuery(id+"F6.imprint","IMPRINT",FACE,{"disambiguationData":[TD([[makeQuery(id+"F6.imprint","IMPRINT",EDGE,{"derivedFrom":sQuery(id+"F6.wireOp",EDGE,"E258.MirrorC")}),-1.0]])]});
            var Q1234;
            Q1234=makeQuery(id+"F6.imprint","IMPRINT",FACE,{"disambiguationData":[TD([[makeQuery(id+"F6.imprint","IMPRINT",EDGE,{"derivedFrom":sQuery(id+"F6.wireOp",EDGE,"E42.3.0.5")}),1.0]])]});
            var Q1235;
            Q1235=makeQuery(id+"F6.imprint","IMPRINT",FACE,{"disambiguationData":[TD([[makeQuery(id+"F6.imprint","IMPRINT",EDGE,{"derivedFrom":sQuery(id+"F6.wireOp",EDGE,"E42.2.0.14")}),1.0]])]});
            var Q1236;
            Q1236=makeQuery(id+"F6.imprint","IMPRINT",FACE,{"disambiguationData":[TD([[makeQuery(id+"F6.imprint","IMPRINT",EDGE,{"derivedFrom":sQuery(id+"F6.wireOp",EDGE,"E42.1.0.22")}),1.0]])]});
            var Q1237;
            Q1237=makeQuery(id+"F6.imprint","IMPRINT",FACE,{"disambiguationData":[TD([[makeQuery(id+"F6.imprint","IMPRINT",EDGE,{"derivedFrom":sQuery(id+"F6.wireOp",EDGE,"E42.1.0.5")}),1.0]])]});
            var Q1238;
            Q1238=makeQuery(id+"F6.imprint","IMPRINT",FACE,{"disambiguationData":[TD([[makeQuery(id+"F6.imprint","IMPRINT",EDGE,{"derivedFrom":sQuery(id+"F6.wireOp",EDGE,"E42.5.0.22")}),1.0]])]});
            var Q1239;
            Q1239=makeQuery(id+"F6.imprint","IMPRINT",FACE,{"disambiguationData":[TD([[makeQuery(id+"F6.imprint","IMPRINT",EDGE,{"derivedFrom":sQuery(id+"F6.wireOp",EDGE,"E42.5.0.5")}),1.0]])]});
            var Q1240;
            Q1240=makeQuery(id+"F6.imprint","IMPRINT",FACE,{"disambiguationData":[TD([[makeQuery(id+"F6.imprint","IMPRINT",EDGE,{"derivedFrom":sQuery(id+"F6.wireOp",EDGE,"E42.4.0.14")}),1.0]])]});
            var Q1241;
            Q1241=makeQuery(id+"F6.imprint","IMPRINT",FACE,{"disambiguationData":[TD([[makeQuery(id+"F6.imprint","IMPRINT",EDGE,{"derivedFrom":sQuery(id+"F6.wireOp",EDGE,"E42.3.0.22")}),1.0]])]});
            var Q1242;
            Q1242=makeQuery(id+"F6.imprint","IMPRINT",FACE,{"disambiguationData":[TD([[makeQuery(id+"F6.imprint","IMPRINT",EDGE,{"derivedFrom":sQuery(id+"F6.wireOp",EDGE,"E42.8.0.14")}),1.0]])]});
            var Q1243;
            Q1243=makeQuery(id+"F6.imprint","IMPRINT",FACE,{"disambiguationData":[TD([[makeQuery(id+"F6.imprint","IMPRINT",EDGE,{"derivedFrom":sQuery(id+"F6.wireOp",EDGE,"E42.7.0.22")}),1.0]])]});
            var Q1244;
            Q1244=makeQuery(id+"F6.imprint","IMPRINT",FACE,{"disambiguationData":[TD([[makeQuery(id+"F6.imprint","IMPRINT",EDGE,{"derivedFrom":sQuery(id+"F6.wireOp",EDGE,"E42.7.0.5")}),1.0]])]});
            var Q1245;
            Q1245=makeQuery(id+"F6.imprint","IMPRINT",FACE,{"disambiguationData":[TD([[makeQuery(id+"F6.imprint","IMPRINT",EDGE,{"derivedFrom":sQuery(id+"F6.wireOp",EDGE,"E42.6.0.14")}),1.0]])]});
            var Q1246;
            Q1246=makeQuery(id+"F6.imprint","IMPRINT",FACE,{"disambiguationData":[TD([[makeQuery(id+"F6.imprint","IMPRINT",EDGE,{"derivedFrom":sQuery(id+"F6.wireOp",EDGE,"E320.MirrorC")}),-1.0]])]});
            var Q1247;
            Q1247=makeQuery(id+"F6.imprint","IMPRINT",FACE,{"disambiguationData":[TD([[makeQuery(id+"F6.imprint","IMPRINT",EDGE,{"derivedFrom":sQuery(id+"F6.wireOp",EDGE,"E336.MirrorC")}),-1.0]])]});
            var Q1248;
            Q1248=makeQuery(id+"F6.imprint","IMPRINT",FACE,{"disambiguationData":[TD([[makeQuery(id+"F6.imprint","IMPRINT",EDGE,{"derivedFrom":sQuery(id+"F6.wireOp",EDGE,"E42.28.0.14")}),1.0]])]});
            var Q1249;
            Q1249=makeQuery(id+"F6.imprint","IMPRINT",FACE,{"disambiguationData":[TD([[makeQuery(id+"F6.imprint","IMPRINT",EDGE,{"derivedFrom":sQuery(id+"F6.wireOp",EDGE,"E42.27.0.22")}),1.0]])]});
            var Q1250;
            Q1250=makeQuery(id+"F6.imprint","IMPRINT",FACE,{"disambiguationData":[TD([[makeQuery(id+"F6.imprint","IMPRINT",EDGE,{"derivedFrom":sQuery(id+"F6.wireOp",EDGE,"E42.27.0.5")}),1.0]])]});
            var Q1251;
            Q1251=makeQuery(id+"F6.imprint","IMPRINT",FACE,{"disambiguationData":[TD([[makeQuery(id+"F6.imprint","IMPRINT",EDGE,{"derivedFrom":sQuery(id+"F6.wireOp",EDGE,"E42.26.0.14")}),1.0]])]});
            var Q1252;
            Q1252=makeQuery(id+"F6.imprint","IMPRINT",FACE,{"disambiguationData":[TD([[makeQuery(id+"F6.imprint","IMPRINT",EDGE,{"derivedFrom":sQuery(id+"F6.wireOp",EDGE,"E42.31.0.5")}),1.0]])]});
            var Q1253;
            Q1253=makeQuery(id+"F6.imprint","IMPRINT",FACE,{"disambiguationData":[TD([[makeQuery(id+"F6.imprint","IMPRINT",EDGE,{"derivedFrom":sQuery(id+"F6.wireOp",EDGE,"E42.30.0.14")}),1.0]])]});
            var Q1254;
            Q1254=makeQuery(id+"F6.imprint","IMPRINT",FACE,{"disambiguationData":[TD([[makeQuery(id+"F6.imprint","IMPRINT",EDGE,{"derivedFrom":sQuery(id+"F6.wireOp",EDGE,"E42.29.0.22")}),1.0]])]});
            var Q1255;
            Q1255=makeQuery(id+"F6.imprint","IMPRINT",FACE,{"disambiguationData":[TD([[makeQuery(id+"F6.imprint","IMPRINT",EDGE,{"derivedFrom":sQuery(id+"F6.wireOp",EDGE,"E42.29.0.5")}),1.0]])]});
            var Q1256;
            Q1256=makeQuery(id+"F6.imprint","IMPRINT",FACE,{"disambiguationData":[TD([[makeQuery(id+"F6.imprint","IMPRINT",EDGE,{"derivedFrom":sQuery(id+"F6.wireOp",EDGE,"E42.32.0.14")}),1.0]])]});
            var Q1257;
            Q1257=makeQuery(id+"F6.imprint","IMPRINT",FACE,{"disambiguationData":[TD([[makeQuery(id+"F6.imprint","IMPRINT",EDGE,{"derivedFrom":sQuery(id+"F6.wireOp",EDGE,"E42.31.0.22")}),1.0]])]});
            var Q1258;
            Q1258=makeQuery(id+"F6.imprint","IMPRINT",FACE,{"disambiguationData":[TD([[makeQuery(id+"F6.imprint","IMPRINT",EDGE,{"derivedFrom":sQuery(id+"F6.wireOp",EDGE,"E42.13.0.6")}),1.0]])]});
            var Q1259;
            Q1259=makeQuery(id+"F6.imprint","IMPRINT",FACE,{"disambiguationData":[TD([[makeQuery(id+"F6.imprint","IMPRINT",EDGE,{"derivedFrom":sQuery(id+"F6.wireOp",EDGE,"E42.12.0.15")}),1.0]])]});
            var Q1260;
            Q1260=makeQuery(id+"F6.imprint","IMPRINT",FACE,{"disambiguationData":[TD([[makeQuery(id+"F6.imprint","IMPRINT",EDGE,{"derivedFrom":sQuery(id+"F6.wireOp",EDGE,"E42.16.0.15")}),1.0]])]});
            var Q1261;
            Q1261=makeQuery(id+"F6.imprint","IMPRINT",FACE,{"disambiguationData":[TD([[makeQuery(id+"F6.imprint","IMPRINT",EDGE,{"derivedFrom":sQuery(id+"F6.wireOp",EDGE,"E42.15.0.6")}),1.0]])]});
            var Q1262;
            Q1262=makeQuery(id+"F6.imprint","IMPRINT",FACE,{"disambiguationData":[TD([[makeQuery(id+"F6.imprint","IMPRINT",EDGE,{"derivedFrom":sQuery(id+"F6.wireOp",EDGE,"E42.14.0.15")}),1.0]])]});
            var Q1263;
            Q1263=makeQuery(id+"F6.imprint","IMPRINT",FACE,{"disambiguationData":[TD([[makeQuery(id+"F6.imprint","IMPRINT",EDGE,{"derivedFrom":sQuery(id+"F6.wireOp",EDGE,"E42.17.0.6")}),1.0]])]});
            var Q1264;
            Q1264=makeQuery(id+"F6.imprint","IMPRINT",FACE,{"disambiguationData":[TD([[makeQuery(id+"F6.imprint","IMPRINT",EDGE,{"derivedFrom":sQuery(id+"F6.wireOp",EDGE,"E42.20.0.15")}),1.0]])]});
            var Q1265;
            Q1265=makeQuery(id+"F6.imprint","IMPRINT",FACE,{"disambiguationData":[TD([[makeQuery(id+"F6.imprint","IMPRINT",EDGE,{"derivedFrom":sQuery(id+"F6.wireOp",EDGE,"E42.19.0.6")}),1.0]])]});
            var Q1266;
            Q1266=makeQuery(id+"F6.imprint","IMPRINT",FACE,{"disambiguationData":[TD([[makeQuery(id+"F6.imprint","IMPRINT",EDGE,{"derivedFrom":sQuery(id+"F6.wireOp",EDGE,"E42.18.0.15")}),1.0]])]});
            var Q1267;
            Q1267=makeQuery(id+"F6.imprint","IMPRINT",FACE,{"disambiguationData":[TD([[makeQuery(id+"F6.imprint","IMPRINT",EDGE,{"derivedFrom":sQuery(id+"F6.wireOp",EDGE,"E42.23.0.6")}),1.0]])]});
            var Q1268;
            Q1268=makeQuery(id+"F6.imprint","IMPRINT",FACE,{"disambiguationData":[TD([[makeQuery(id+"F6.imprint","IMPRINT",EDGE,{"derivedFrom":sQuery(id+"F6.wireOp",EDGE,"E42.22.0.15")}),1.0]])]});
            var Q1269;
            Q1269=makeQuery(id+"F6.imprint","IMPRINT",FACE,{"disambiguationData":[TD([[makeQuery(id+"F6.imprint","IMPRINT",EDGE,{"derivedFrom":sQuery(id+"F6.wireOp",EDGE,"E42.21.0.6")}),1.0]])]});
            var Q1270;
            Q1270=makeQuery(id+"F6.imprint","IMPRINT",FACE,{"disambiguationData":[TD([[makeQuery(id+"F6.imprint","IMPRINT",EDGE,{"derivedFrom":sQuery(id+"F6.wireOp",EDGE,"E42.25.0.6")}),1.0]])]});
            var Q1271;
            Q1271=makeQuery(id+"F6.imprint","IMPRINT",FACE,{"disambiguationData":[TD([[makeQuery(id+"F6.imprint","IMPRINT",EDGE,{"derivedFrom":sQuery(id+"F6.wireOp",EDGE,"E42.24.0.15")}),1.0]])]});
            var Q1272;
            Q1272=makeQuery(id+"F6.imprint","IMPRINT",FACE,{"disambiguationData":[TD([[makeQuery(id+"F6.imprint","IMPRINT",EDGE,{"derivedFrom":sQuery(id+"F6.wireOp",EDGE,"E42.28.0.15")}),1.0]])]});
            var Q1273;
            Q1273=makeQuery(id+"F6.imprint","IMPRINT",FACE,{"disambiguationData":[TD([[makeQuery(id+"F6.imprint","IMPRINT",EDGE,{"derivedFrom":sQuery(id+"F6.wireOp",EDGE,"E42.27.0.6")}),1.0]])]});
            var Q1274;
            Q1274=makeQuery(id+"F6.imprint","IMPRINT",FACE,{"disambiguationData":[TD([[makeQuery(id+"F6.imprint","IMPRINT",EDGE,{"derivedFrom":sQuery(id+"F6.wireOp",EDGE,"E42.26.0.15")}),1.0]])]});
            var Q1275;
            Q1275=makeQuery(id+"F6.imprint","IMPRINT",FACE,{"disambiguationData":[TD([[makeQuery(id+"F6.imprint","IMPRINT",EDGE,{"derivedFrom":sQuery(id+"F6.wireOp",EDGE,"E244.MirrorC")}),-1.0]])]});
            var Q1276;
            Q1276=makeQuery(id+"F6.imprint","IMPRINT",FACE,{"disambiguationData":[TD([[makeQuery(id+"F6.imprint","IMPRINT",EDGE,{"derivedFrom":sQuery(id+"F6.wireOp",EDGE,"E305.MirrorC")}),-1.0]])]});
            var Q1277;
            Q1277=makeQuery(id+"F6.imprint","IMPRINT",FACE,{"disambiguationData":[TD([[makeQuery(id+"F6.imprint","IMPRINT",EDGE,{"derivedFrom":sQuery(id+"F6.wireOp",EDGE,"E289.MirrorC")}),-1.0]])]});
            var Q1278;
            Q1278=makeQuery(id+"F6.imprint","IMPRINT",FACE,{"disambiguationData":[TD([[makeQuery(id+"F6.imprint","IMPRINT",EDGE,{"derivedFrom":sQuery(id+"F6.wireOp",EDGE,"E273.MirrorC")}),-1.0]])]});
            var Q1279;
            Q1279=makeQuery(id+"F6.imprint","IMPRINT",FACE,{"disambiguationData":[TD([[makeQuery(id+"F6.imprint","IMPRINT",EDGE,{"derivedFrom":sQuery(id+"F6.wireOp",EDGE,"E259.MirrorC")}),-1.0]])]});
            var Q1280;
            Q1280=makeQuery(id+"F6.imprint","IMPRINT",FACE,{"disambiguationData":[TD([[makeQuery(id+"F6.imprint","IMPRINT",EDGE,{"derivedFrom":sQuery(id+"F6.wireOp",EDGE,"E42.3.0.6")}),1.0]])]});
            var Q1281;
            Q1281=makeQuery(id+"F6.imprint","IMPRINT",FACE,{"disambiguationData":[TD([[makeQuery(id+"F6.imprint","IMPRINT",EDGE,{"derivedFrom":sQuery(id+"F6.wireOp",EDGE,"E42.2.0.15")}),1.0]])]});
            var Q1282;
            Q1282=makeQuery(id+"F6.imprint","IMPRINT",FACE,{"disambiguationData":[TD([[makeQuery(id+"F6.imprint","IMPRINT",EDGE,{"derivedFrom":sQuery(id+"F6.wireOp",EDGE,"E42.1.0.6")}),1.0]])]});
            var Q1283;
            Q1283=makeQuery(id+"F6.imprint","IMPRINT",FACE,{"disambiguationData":[TD([[makeQuery(id+"F6.imprint","IMPRINT",EDGE,{"derivedFrom":sQuery(id+"F6.wireOp",EDGE,"E42.5.0.6")}),1.0]])]});
            var Q1284;
            Q1284=makeQuery(id+"F6.imprint","IMPRINT",FACE,{"disambiguationData":[TD([[makeQuery(id+"F6.imprint","IMPRINT",EDGE,{"derivedFrom":sQuery(id+"F6.wireOp",EDGE,"E42.4.0.15")}),1.0]])]});
            var Q1285;
            Q1285=makeQuery(id+"F6.imprint","IMPRINT",FACE,{"disambiguationData":[TD([[makeQuery(id+"F6.imprint","IMPRINT",EDGE,{"derivedFrom":sQuery(id+"F6.wireOp",EDGE,"E42.8.0.15")}),1.0]])]});
            var Q1286;
            Q1286=makeQuery(id+"F6.imprint","IMPRINT",FACE,{"disambiguationData":[TD([[makeQuery(id+"F6.imprint","IMPRINT",EDGE,{"derivedFrom":sQuery(id+"F6.wireOp",EDGE,"E42.7.0.6")}),1.0]])]});
            var Q1287;
            Q1287=makeQuery(id+"F6.imprint","IMPRINT",FACE,{"disambiguationData":[TD([[makeQuery(id+"F6.imprint","IMPRINT",EDGE,{"derivedFrom":sQuery(id+"F6.wireOp",EDGE,"E42.6.0.15")}),1.0]])]});
            var Q1288;
            Q1288=makeQuery(id+"F6.imprint","IMPRINT",FACE,{"disambiguationData":[TD([[makeQuery(id+"F6.imprint","IMPRINT",EDGE,{"derivedFrom":sQuery(id+"F6.wireOp",EDGE,"E42.11.0.6")}),1.0]])]});
            var Q1289;
            Q1289=makeQuery(id+"F6.imprint","IMPRINT",FACE,{"disambiguationData":[TD([[makeQuery(id+"F6.imprint","IMPRINT",EDGE,{"derivedFrom":sQuery(id+"F6.wireOp",EDGE,"E42.10.0.15")}),1.0]])]});
            var Q1290;
            Q1290=makeQuery(id+"F6.imprint","IMPRINT",FACE,{"disambiguationData":[TD([[makeQuery(id+"F6.imprint","IMPRINT",EDGE,{"derivedFrom":sQuery(id+"F6.wireOp",EDGE,"E42.9.0.6")}),1.0]])]});
            var Q1291;
            Q1291=makeQuery(id+"F6.imprint","IMPRINT",FACE,{"disambiguationData":[TD([[makeQuery(id+"F6.imprint","IMPRINT",EDGE,{"derivedFrom":sQuery(id+"F6.wireOp",EDGE,"E42.31.0.6")}),1.0]])]});
            var Q1292;
            Q1292=makeQuery(id+"F6.imprint","IMPRINT",FACE,{"disambiguationData":[TD([[makeQuery(id+"F6.imprint","IMPRINT",EDGE,{"derivedFrom":sQuery(id+"F6.wireOp",EDGE,"E42.30.0.15")}),1.0]])]});
            var Q1293;
            Q1293=makeQuery(id+"F6.imprint","IMPRINT",FACE,{"disambiguationData":[TD([[makeQuery(id+"F6.imprint","IMPRINT",EDGE,{"derivedFrom":sQuery(id+"F6.wireOp",EDGE,"E42.29.0.6")}),1.0]])]});
            var Q1294;
            Q1294=makeQuery(id+"F6.imprint","IMPRINT",FACE,{"disambiguationData":[TD([[makeQuery(id+"F6.imprint","IMPRINT",EDGE,{"derivedFrom":sQuery(id+"F6.wireOp",EDGE,"E42.32.0.15")}),1.0]])]});
            var Q1295;
            Q1295=makeQuery(id+"F6.imprint","IMPRINT",FACE,{"disambiguationData":[TD([[makeQuery(id+"F6.imprint","IMPRINT",EDGE,{"derivedFrom":sQuery(id+"F6.wireOp",EDGE,"E873.MirrorC")}),-1.0]])]});
            var Q1296;
            Q1296=makeQuery(id+"F6.imprint","IMPRINT",FACE,{"disambiguationData":[TD([[makeQuery(id+"F6.imprint","IMPRINT",EDGE,{"derivedFrom":sQuery(id+"F6.wireOp",EDGE,"E854.MirrorC")}),-1.0]])]});
            var Q1297;
            Q1297=makeQuery(id+"F6.imprint","IMPRINT",FACE,{"disambiguationData":[TD([[makeQuery(id+"F6.imprint","IMPRINT",EDGE,{"derivedFrom":sQuery(id+"F6.wireOp",EDGE,"E888.MirrorC")}),-1.0]])]});
            var Q1298;
            Q1298=makeQuery(id+"F6.imprint","IMPRINT",FACE,{"disambiguationData":[TD([[makeQuery(id+"F6.imprint","IMPRINT",EDGE,{"derivedFrom":sQuery(id+"F6.wireOp",EDGE,"E870.MirrorC")}),-1.0]])]});
            var Q1299;
            Q1299=makeQuery(id+"F6.imprint","IMPRINT",FACE,{"disambiguationData":[TD([[makeQuery(id+"F6.imprint","IMPRINT",EDGE,{"derivedFrom":sQuery(id+"F6.wireOp",EDGE,"E842.MirrorC")}),-1.0]])]});
            var Q1300;
            Q1300=makeQuery(id+"F6.imprint","IMPRINT",FACE,{"disambiguationData":[TD([[makeQuery(id+"F6.imprint","IMPRINT",EDGE,{"derivedFrom":sQuery(id+"F6.wireOp",EDGE,"E895.MirrorC")}),-1.0]])]});
            var Q1301;
            Q1301=makeQuery(id+"F6.imprint","IMPRINT",FACE,{"disambiguationData":[TD([[makeQuery(id+"F6.imprint","IMPRINT",EDGE,{"derivedFrom":sQuery(id+"F6.wireOp",EDGE,"E726.MirrorC")}),-1.0]])]});
            var Q1302;
            Q1302=makeQuery(id+"F6.imprint","IMPRINT",FACE,{"disambiguationData":[TD([[makeQuery(id+"F6.imprint","IMPRINT",EDGE,{"derivedFrom":sQuery(id+"F6.wireOp",EDGE,"E824.MirrorC")}),-1.0]])]});
            var Q1303;
            Q1303=makeQuery(id+"F6.imprint","IMPRINT",FACE,{"disambiguationData":[TD([[makeQuery(id+"F6.imprint","IMPRINT",EDGE,{"derivedFrom":sQuery(id+"F6.wireOp",EDGE,"E857.MirrorC")}),-1.0]])]});
            var Q1304;
            Q1304=makeQuery(id+"F6.imprint","IMPRINT",FACE,{"disambiguationData":[TD([[makeQuery(id+"F6.imprint","IMPRINT",EDGE,{"derivedFrom":sQuery(id+"F6.wireOp",EDGE,"E839.MirrorC")}),-1.0]])]});
            var Q1305;
            Q1305=makeQuery(id+"F6.imprint","IMPRINT",FACE,{"disambiguationData":[TD([[makeQuery(id+"F6.imprint","IMPRINT",EDGE,{"derivedFrom":sQuery(id+"F6.wireOp",EDGE,"E741.MirrorC")}),-1.0]])]});
            var Q1306;
            Q1306=makeQuery(id+"F6.imprint","IMPRINT",FACE,{"disambiguationData":[TD([[makeQuery(id+"F6.imprint","IMPRINT",EDGE,{"derivedFrom":sQuery(id+"F6.wireOp",EDGE,"E756.MirrorC")}),-1.0]])]});
            var Q1307;
            Q1307=makeQuery(id+"F6.imprint","IMPRINT",FACE,{"disambiguationData":[TD([[makeQuery(id+"F6.imprint","IMPRINT",EDGE,{"derivedFrom":sQuery(id+"F6.wireOp",EDGE,"E885.MirrorC")}),-1.0]])]});
            var Q1308;
            Q1308=makeQuery(id+"F6.imprint","IMPRINT",FACE,{"disambiguationData":[TD([[makeQuery(id+"F6.imprint","IMPRINT",EDGE,{"derivedFrom":sQuery(id+"F6.wireOp",EDGE,"E901.MirrorC")}),-1.0]])]});
            var Q1309;
            Q1309=makeQuery(id+"F6.imprint","IMPRINT",FACE,{"disambiguationData":[TD([[makeQuery(id+"F6.imprint","IMPRINT",EDGE,{"derivedFrom":sQuery(id+"F6.wireOp",EDGE,"E802.MirrorC")}),-1.0]])]});
            var Q1310;
            Q1310=makeQuery(id+"F6.imprint","IMPRINT",FACE,{"disambiguationData":[TD([[makeQuery(id+"F6.imprint","IMPRINT",EDGE,{"derivedFrom":sQuery(id+"F6.wireOp",EDGE,"E817.MirrorC")}),-1.0]])]});
            var Q1311;
            Q1311=makeQuery(id+"F6.imprint","IMPRINT",FACE,{"disambiguationData":[TD([[makeQuery(id+"F6.imprint","IMPRINT",EDGE,{"derivedFrom":sQuery(id+"F6.wireOp",EDGE,"E772.MirrorC")}),-1.0]])]});
            var Q1312;
            Q1312=makeQuery(id+"F6.imprint","IMPRINT",FACE,{"disambiguationData":[TD([[makeQuery(id+"F6.imprint","IMPRINT",EDGE,{"derivedFrom":sQuery(id+"F6.wireOp",EDGE,"E787.MirrorC")}),-1.0]])]});
            var Q1313;
            Q1313=makeQuery(id+"F6.imprint","IMPRINT",FACE,{"disambiguationData":[TD([[makeQuery(id+"F6.imprint","IMPRINT",EDGE,{"derivedFrom":sQuery(id+"F6.wireOp",EDGE,"E862.MirrorC")}),-1.0]])]});
            var Q1314;
            Q1314=makeQuery(id+"F6.imprint","IMPRINT",FACE,{"disambiguationData":[TD([[makeQuery(id+"F6.imprint","IMPRINT",EDGE,{"derivedFrom":sQuery(id+"F6.wireOp",EDGE,"E877.MirrorC")}),-1.0]])]});
            var Q1315;
            Q1315=makeQuery(id+"F6.imprint","IMPRINT",FACE,{"disambiguationData":[TD([[makeQuery(id+"F6.imprint","IMPRINT",EDGE,{"derivedFrom":sQuery(id+"F6.wireOp",EDGE,"E831.MirrorC")}),-1.0]])]});
            var Q1316;
            Q1316=makeQuery(id+"F6.imprint","IMPRINT",FACE,{"disambiguationData":[TD([[makeQuery(id+"F6.imprint","IMPRINT",EDGE,{"derivedFrom":sQuery(id+"F6.wireOp",EDGE,"E847.MirrorC")}),-1.0]])]});
            var Q1317;
            Q1317=makeQuery(id+"F6.imprint","IMPRINT",FACE,{"disambiguationData":[TD([[makeQuery(id+"F6.imprint","IMPRINT",EDGE,{"derivedFrom":sQuery(id+"F6.wireOp",EDGE,"E893.MirrorC")}),-1.0]])]});
            var Q1318;
            Q1318=makeQuery(id+"F6.imprint","IMPRINT",FACE,{"disambiguationData":[TD([[makeQuery(id+"F6.imprint","IMPRINT",EDGE,{"derivedFrom":sQuery(id+"F6.wireOp",EDGE,"E41.0.3.0")}),1.0]])]});
            var Q1319;
            Q1319=makeQuery(id+"F6.imprint","IMPRINT",FACE,{"disambiguationData":[TD([[makeQuery(id+"F6.imprint","IMPRINT",EDGE,{"derivedFrom":sQuery(id+"F6.wireOp",EDGE,"E41.0.2.0")}),1.0]])]});
            var Q1320;
            Q1320=makeQuery(id+"F6.imprint","IMPRINT",FACE,{"disambiguationData":[TD([[makeQuery(id+"F6.imprint","IMPRINT",EDGE,{"derivedFrom":sQuery(id+"F6.wireOp",EDGE,"E42.3.0.26")}),1.0]])]});
            var Q1321;
            Q1321=makeQuery(id+"F6.imprint","IMPRINT",FACE,{"disambiguationData":[TD([[makeQuery(id+"F6.imprint","IMPRINT",EDGE,{"derivedFrom":sQuery(id+"F6.wireOp",EDGE,"E42.5.0.26")}),1.0]])]});
            var Q1322;
            Q1322=makeQuery(id+"F6.imprint","IMPRINT",FACE,{"disambiguationData":[TD([[makeQuery(id+"F6.imprint","IMPRINT",EDGE,{"derivedFrom":sQuery(id+"F6.wireOp",EDGE,"E42.9.0.26")}),1.0]])]});
            var Q1323;
            Q1323=makeQuery(id+"F6.imprint","IMPRINT",FACE,{"disambiguationData":[TD([[makeQuery(id+"F6.imprint","IMPRINT",EDGE,{"derivedFrom":sQuery(id+"F6.wireOp",EDGE,"E42.7.0.26")}),1.0]])]});
            var Q1324;
            Q1324=makeQuery(id+"F6.imprint","IMPRINT",FACE,{"disambiguationData":[TD([[makeQuery(id+"F6.imprint","IMPRINT",EDGE,{"derivedFrom":sQuery(id+"F6.wireOp",EDGE,"E42.11.0.26")}),1.0]])]});
            var Q1325;
            Q1325=makeQuery(id+"F6.imprint","IMPRINT",FACE,{"disambiguationData":[TD([[makeQuery(id+"F6.imprint","IMPRINT",EDGE,{"derivedFrom":sQuery(id+"F6.wireOp",EDGE,"E42.13.0.26")}),1.0]])]});
            var Q1326;
            Q1326=makeQuery(id+"F6.imprint","IMPRINT",FACE,{"disambiguationData":[TD([[makeQuery(id+"F6.imprint","IMPRINT",EDGE,{"derivedFrom":sQuery(id+"F6.wireOp",EDGE,"E42.15.0.26")}),1.0]])]});
            var Q1327;
            Q1327=makeQuery(id+"F6.imprint","IMPRINT",FACE,{"disambiguationData":[TD([[makeQuery(id+"F6.imprint","IMPRINT",EDGE,{"derivedFrom":sQuery(id+"F6.wireOp",EDGE,"E42.17.0.26")}),1.0]])]});
            var Q1328;
            Q1328=makeQuery(id+"F6.imprint","IMPRINT",FACE,{"disambiguationData":[TD([[makeQuery(id+"F6.imprint","IMPRINT",EDGE,{"derivedFrom":sQuery(id+"F6.wireOp",EDGE,"E199.MirrorC")}),-1.0]])]});
            var Q1329;
            Q1329=makeQuery(id+"F6.imprint","IMPRINT",FACE,{"disambiguationData":[TD([[makeQuery(id+"F6.imprint","IMPRINT",EDGE,{"derivedFrom":sQuery(id+"F6.wireOp",EDGE,"E174.MirrorC")}),-1.0]])]});
            var Q1330;
            Q1330=makeQuery(id+"F6.imprint","IMPRINT",FACE,{"disambiguationData":[TD([[makeQuery(id+"F6.imprint","IMPRINT",EDGE,{"derivedFrom":sQuery(id+"F6.wireOp",EDGE,"E150.MirrorC")}),-1.0]])]});
            var Q1331;
            Q1331=makeQuery(id+"F6.imprint","IMPRINT",FACE,{"disambiguationData":[TD([[makeQuery(id+"F6.imprint","IMPRINT",EDGE,{"derivedFrom":sQuery(id+"F6.wireOp",EDGE,"E125.MirrorC")}),-1.0]])]});
            var Q1332;
            Q1332=makeQuery(id+"F6.imprint","IMPRINT",FACE,{"disambiguationData":[TD([[makeQuery(id+"F6.imprint","IMPRINT",EDGE,{"derivedFrom":sQuery(id+"F6.wireOp",EDGE,"E223.MirrorC")}),-1.0]])]});
            var Q1333;
            Q1333=makeQuery(id+"F6.imprint","IMPRINT",FACE,{"disambiguationData":[TD([[makeQuery(id+"F6.imprint","IMPRINT",EDGE,{"derivedFrom":sQuery(id+"F6.wireOp",EDGE,"E42.1.0.26")}),1.0]])]});
            var Q1334;
            Q1334=makeQuery(id+"F6.imprint","IMPRINT",FACE,{"disambiguationData":[TD([[makeQuery(id+"F6.imprint","IMPRINT",EDGE,{"derivedFrom":sQuery(id+"F6.wireOp",EDGE,"E42.21.0.26")}),1.0]])]});
            var Q1335;
            Q1335=makeQuery(id+"F6.imprint","IMPRINT",FACE,{"disambiguationData":[TD([[makeQuery(id+"F6.imprint","IMPRINT",EDGE,{"derivedFrom":sQuery(id+"F6.wireOp",EDGE,"E42.19.0.26")}),1.0]])]});
            var Q1336;
            Q1336=makeQuery(id+"F6.imprint","IMPRINT",FACE,{"disambiguationData":[TD([[makeQuery(id+"F6.imprint","IMPRINT",EDGE,{"derivedFrom":sQuery(id+"F6.wireOp",EDGE,"E42.23.0.26")}),1.0]])]});
            var Q1337;
            Q1337=makeQuery(id+"F6.imprint","IMPRINT",FACE,{"disambiguationData":[TD([[makeQuery(id+"F6.imprint","IMPRINT",EDGE,{"derivedFrom":sQuery(id+"F6.wireOp",EDGE,"E42.25.0.26")}),1.0]])]});
            var Q1338;
            Q1338=makeQuery(id+"F6.imprint","IMPRINT",FACE,{"disambiguationData":[TD([[makeQuery(id+"F6.imprint","IMPRINT",EDGE,{"derivedFrom":sQuery(id+"F6.wireOp",EDGE,"E42.29.0.26")}),1.0]])]});
            var Q1339;
            Q1339=makeQuery(id+"F6.imprint","IMPRINT",FACE,{"disambiguationData":[TD([[makeQuery(id+"F6.imprint","IMPRINT",EDGE,{"derivedFrom":sQuery(id+"F6.wireOp",EDGE,"E42.27.0.26")}),1.0]])]});
            var Q1340;
            Q1340=makeQuery(id+"F6.imprint","IMPRINT",FACE,{"disambiguationData":[TD([[makeQuery(id+"F6.imprint","IMPRINT",EDGE,{"derivedFrom":sQuery(id+"F6.wireOp",EDGE,"E42.31.0.26")}),1.0]])]});
            var Q1341;
            Q1341=makeQuery(id+"F6.imprint","IMPRINT",FACE,{"disambiguationData":[TD([[makeQuery(id+"F6.imprint","IMPRINT",EDGE,{"derivedFrom":sQuery(id+"F6.wireOp",EDGE,"E105.MirrorC")}),-1.0]])]});
            var Q1342;
            Q1342=makeQuery(id+"F6.imprint","IMPRINT",FACE,{"disambiguationData":[TD([[makeQuery(id+"F6.imprint","IMPRINT",EDGE,{"derivedFrom":sQuery(id+"F6.wireOp",EDGE,"E80.MirrorC")}),-1.0]])]});
            var Q1343;
            Q1343=makeQuery(id+"F6.imprint","IMPRINT",FACE,{"disambiguationData":[TD([[makeQuery(id+"F6.imprint","IMPRINT",EDGE,{"derivedFrom":sQuery(id+"F6.wireOp",EDGE,"E54.MirrorC")}),-1.0]])]});
            var Q1344;
            Q1344=makeQuery(id+"F6.imprint","IMPRINT",FACE,{"disambiguationData":[TD([[makeQuery(id+"F6.imprint","IMPRINT",EDGE,{"derivedFrom":sQuery(id+"F6.wireOp",EDGE,"E172.MirrorC")}),-1.0]])]});
            var Q1345;
            Q1345=makeQuery(id+"F6.imprint","IMPRINT",FACE,{"disambiguationData":[TD([[makeQuery(id+"F6.imprint","IMPRINT",EDGE,{"derivedFrom":sQuery(id+"F6.wireOp",EDGE,"E148.MirrorC")}),-1.0]])]});
            var Q1346;
            Q1346=makeQuery(id+"F6.imprint","IMPRINT",FACE,{"disambiguationData":[TD([[makeQuery(id+"F6.imprint","IMPRINT",EDGE,{"derivedFrom":sQuery(id+"F6.wireOp",EDGE,"E123.MirrorC")}),-1.0]])]});
            var Q1347;
            Q1347=makeQuery(id+"F6.imprint","IMPRINT",FACE,{"disambiguationData":[TD([[makeQuery(id+"F6.imprint","IMPRINT",EDGE,{"derivedFrom":sQuery(id+"F6.wireOp",EDGE,"E221.MirrorC")}),-1.0]])]});
            var Q1348;
            Q1348=makeQuery(id+"F6.imprint","IMPRINT",FACE,{"disambiguationData":[TD([[makeQuery(id+"F6.imprint","IMPRINT",EDGE,{"derivedFrom":sQuery(id+"F6.wireOp",EDGE,"E197.MirrorC")}),-1.0]])]});
            var Q1349;
            Q1349=makeQuery(id+"F6.imprint","IMPRINT",FACE,{"disambiguationData":[TD([[makeQuery(id+"F6.imprint","IMPRINT",EDGE,{"derivedFrom":sQuery(id+"F6.wireOp",EDGE,"E42.3.0.24")}),1.0]])]});
            var Q1350;
            Q1350=makeQuery(id+"F6.imprint","IMPRINT",FACE,{"disambiguationData":[TD([[makeQuery(id+"F6.imprint","IMPRINT",EDGE,{"derivedFrom":sQuery(id+"F6.wireOp",EDGE,"E42.1.0.24")}),1.0]])]});
            var Q1351;
            Q1351=makeQuery(id+"F6.imprint","IMPRINT",FACE,{"disambiguationData":[TD([[makeQuery(id+"F6.imprint","IMPRINT",EDGE,{"derivedFrom":sQuery(id+"F6.wireOp",EDGE,"E42.5.0.24")}),1.0]])]});
            var Q1352;
            Q1352=makeQuery(id+"F6.imprint","IMPRINT",FACE,{"disambiguationData":[TD([[makeQuery(id+"F6.imprint","IMPRINT",EDGE,{"derivedFrom":sQuery(id+"F6.wireOp",EDGE,"E42.25.0.24")}),1.0]])]});
            var Q1353;
            Q1353=makeQuery(id+"F6.imprint","IMPRINT",FACE,{"disambiguationData":[TD([[makeQuery(id+"F6.imprint","IMPRINT",EDGE,{"derivedFrom":sQuery(id+"F6.wireOp",EDGE,"E42.27.0.24")}),1.0]])]});
            var Q1354;
            Q1354=makeQuery(id+"F6.imprint","IMPRINT",FACE,{"disambiguationData":[TD([[makeQuery(id+"F6.imprint","IMPRINT",EDGE,{"derivedFrom":sQuery(id+"F6.wireOp",EDGE,"E42.31.0.24")}),1.0]])]});
            var Q1355;
            Q1355=makeQuery(id+"F6.imprint","IMPRINT",FACE,{"disambiguationData":[TD([[makeQuery(id+"F6.imprint","IMPRINT",EDGE,{"derivedFrom":sQuery(id+"F6.wireOp",EDGE,"E42.29.0.24")}),1.0]])]});
            var Q1356;
            Q1356=makeQuery(id+"F6.imprint","IMPRINT",FACE,{"disambiguationData":[TD([[makeQuery(id+"F6.imprint","IMPRINT",EDGE,{"derivedFrom":sQuery(id+"F6.wireOp",EDGE,"E101.MirrorC")}),-1.0]])]});
            var Q1357;
            Q1357=makeQuery(id+"F6.imprint","IMPRINT",FACE,{"disambiguationData":[TD([[makeQuery(id+"F6.imprint","IMPRINT",EDGE,{"derivedFrom":sQuery(id+"F6.wireOp",EDGE,"E76.MirrorC")}),-1.0]])]});
            var Q1358;
            Q1358=makeQuery(id+"F6.imprint","IMPRINT",FACE,{"disambiguationData":[TD([[makeQuery(id+"F6.imprint","IMPRINT",EDGE,{"derivedFrom":sQuery(id+"F6.wireOp",EDGE,"E52.MirrorC")}),-1.0]])]});
            var Q1359;
            Q1359=makeQuery(id+"F6.imprint","IMPRINT",FACE,{"disambiguationData":[TD([[makeQuery(id+"F6.imprint","IMPRINT",EDGE,{"derivedFrom":sQuery(id+"F6.wireOp",EDGE,"E42.7.0.24")}),1.0]])]});
            var Q1360;
            Q1360=makeQuery(id+"F6.imprint","IMPRINT",FACE,{"disambiguationData":[TD([[makeQuery(id+"F6.imprint","IMPRINT",EDGE,{"derivedFrom":sQuery(id+"F6.wireOp",EDGE,"E42.11.0.24")}),1.0]])]});
            var Q1361;
            Q1361=makeQuery(id+"F6.imprint","IMPRINT",FACE,{"disambiguationData":[TD([[makeQuery(id+"F6.imprint","IMPRINT",EDGE,{"derivedFrom":sQuery(id+"F6.wireOp",EDGE,"E42.9.0.24")}),1.0]])]});
            var Q1362;
            Q1362=makeQuery(id+"F6.imprint","IMPRINT",FACE,{"disambiguationData":[TD([[makeQuery(id+"F6.imprint","IMPRINT",EDGE,{"derivedFrom":sQuery(id+"F6.wireOp",EDGE,"E42.13.0.24")}),1.0]])]});
            var Q1363;
            Q1363=makeQuery(id+"F6.imprint","IMPRINT",FACE,{"disambiguationData":[TD([[makeQuery(id+"F6.imprint","IMPRINT",EDGE,{"derivedFrom":sQuery(id+"F6.wireOp",EDGE,"E42.15.0.24")}),1.0]])]});
            var Q1364;
            Q1364=makeQuery(id+"F6.imprint","IMPRINT",FACE,{"disambiguationData":[TD([[makeQuery(id+"F6.imprint","IMPRINT",EDGE,{"derivedFrom":sQuery(id+"F6.wireOp",EDGE,"E42.17.0.24")}),1.0]])]});
            var Q1365;
            Q1365=makeQuery(id+"F6.imprint","IMPRINT",FACE,{"disambiguationData":[TD([[makeQuery(id+"F6.imprint","IMPRINT",EDGE,{"derivedFrom":sQuery(id+"F6.wireOp",EDGE,"E42.19.0.24")}),1.0]])]});
            var Q1366;
            Q1366=makeQuery(id+"F6.imprint","IMPRINT",FACE,{"disambiguationData":[TD([[makeQuery(id+"F6.imprint","IMPRINT",EDGE,{"derivedFrom":sQuery(id+"F6.wireOp",EDGE,"E42.23.0.24")}),1.0]])]});
            var Q1367;
            Q1367=makeQuery(id+"F6.imprint","IMPRINT",FACE,{"disambiguationData":[TD([[makeQuery(id+"F6.imprint","IMPRINT",EDGE,{"derivedFrom":sQuery(id+"F6.wireOp",EDGE,"E42.21.0.24")}),1.0]])]});
            var Q1368;
            Q1368=makeQuery(id+"F6.imprint","IMPRINT",FACE,{"disambiguationData":[TD([[makeQuery(id+"F6.imprint","IMPRINT",EDGE,{"derivedFrom":sQuery(id+"F6.wireOp",EDGE,"E173.MirrorC")}),-1.0]])]});
            var Q1369;
            Q1369=makeQuery(id+"F6.imprint","IMPRINT",FACE,{"disambiguationData":[TD([[makeQuery(id+"F6.imprint","IMPRINT",EDGE,{"derivedFrom":sQuery(id+"F6.wireOp",EDGE,"E149.MirrorC")}),-1.0]])]});
            var Q1370;
            Q1370=makeQuery(id+"F6.imprint","IMPRINT",FACE,{"disambiguationData":[TD([[makeQuery(id+"F6.imprint","IMPRINT",EDGE,{"derivedFrom":sQuery(id+"F6.wireOp",EDGE,"E124.MirrorC")}),-1.0]])]});
            var Q1371;
            Q1371=makeQuery(id+"F6.imprint","IMPRINT",FACE,{"disambiguationData":[TD([[makeQuery(id+"F6.imprint","IMPRINT",EDGE,{"derivedFrom":sQuery(id+"F6.wireOp",EDGE,"E222.MirrorC")}),-1.0]])]});
            var Q1372;
            Q1372=makeQuery(id+"F6.imprint","IMPRINT",FACE,{"disambiguationData":[TD([[makeQuery(id+"F6.imprint","IMPRINT",EDGE,{"derivedFrom":sQuery(id+"F6.wireOp",EDGE,"E198.MirrorC")}),-1.0]])]});
            var Q1373;
            Q1373=makeQuery(id+"F6.imprint","IMPRINT",FACE,{"disambiguationData":[TD([[makeQuery(id+"F6.imprint","IMPRINT",EDGE,{"derivedFrom":sQuery(id+"F6.wireOp",EDGE,"E42.3.0.25")}),1.0]])]});
            var Q1374;
            Q1374=makeQuery(id+"F6.imprint","IMPRINT",FACE,{"disambiguationData":[TD([[makeQuery(id+"F6.imprint","IMPRINT",EDGE,{"derivedFrom":sQuery(id+"F6.wireOp",EDGE,"E42.5.0.25")}),1.0]])]});
            var Q1375;
            Q1375=makeQuery(id+"F6.imprint","IMPRINT",FACE,{"disambiguationData":[TD([[makeQuery(id+"F6.imprint","IMPRINT",EDGE,{"derivedFrom":sQuery(id+"F6.wireOp",EDGE,"E42.7.0.25")}),1.0]])]});
            var Q1376;
            Q1376=makeQuery(id+"F6.imprint","IMPRINT",FACE,{"disambiguationData":[TD([[makeQuery(id+"F6.imprint","IMPRINT",EDGE,{"derivedFrom":sQuery(id+"F6.wireOp",EDGE,"E42.27.0.25")}),1.0]])]});
            var Q1377;
            Q1377=makeQuery(id+"F6.imprint","IMPRINT",FACE,{"disambiguationData":[TD([[makeQuery(id+"F6.imprint","IMPRINT",EDGE,{"derivedFrom":sQuery(id+"F6.wireOp",EDGE,"E42.31.0.25")}),1.0]])]});
            var Q1378;
            Q1378=makeQuery(id+"F6.imprint","IMPRINT",FACE,{"disambiguationData":[TD([[makeQuery(id+"F6.imprint","IMPRINT",EDGE,{"derivedFrom":sQuery(id+"F6.wireOp",EDGE,"E42.29.0.25")}),1.0]])]});
            var Q1379;
            Q1379=makeQuery(id+"F6.imprint","IMPRINT",FACE,{"disambiguationData":[TD([[makeQuery(id+"F6.imprint","IMPRINT",EDGE,{"derivedFrom":sQuery(id+"F6.wireOp",EDGE,"E102.MirrorC")}),-1.0]])]});
            var Q1380;
            Q1380=makeQuery(id+"F6.imprint","IMPRINT",FACE,{"disambiguationData":[TD([[makeQuery(id+"F6.imprint","IMPRINT",EDGE,{"derivedFrom":sQuery(id+"F6.wireOp",EDGE,"E79.MirrorC")}),-1.0]])]});
            var Q1381;
            Q1381=makeQuery(id+"F6.imprint","IMPRINT",FACE,{"disambiguationData":[TD([[makeQuery(id+"F6.imprint","IMPRINT",EDGE,{"derivedFrom":sQuery(id+"F6.wireOp",EDGE,"E53.MirrorC")}),-1.0]])]});
            var Q1382;
            Q1382=makeQuery(id+"F6.imprint","IMPRINT",FACE,{"disambiguationData":[TD([[makeQuery(id+"F6.imprint","IMPRINT",EDGE,{"derivedFrom":sQuery(id+"F6.wireOp",EDGE,"E42.11.0.25")}),1.0]])]});
            var Q1383;
            Q1383=makeQuery(id+"F6.imprint","IMPRINT",FACE,{"disambiguationData":[TD([[makeQuery(id+"F6.imprint","IMPRINT",EDGE,{"derivedFrom":sQuery(id+"F6.wireOp",EDGE,"E42.9.0.25")}),1.0]])]});
            var Q1384;
            Q1384=makeQuery(id+"F6.imprint","IMPRINT",FACE,{"disambiguationData":[TD([[makeQuery(id+"F6.imprint","IMPRINT",EDGE,{"derivedFrom":sQuery(id+"F6.wireOp",EDGE,"E42.13.0.25")}),1.0]])]});
            var Q1385;
            Q1385=makeQuery(id+"F6.imprint","IMPRINT",FACE,{"disambiguationData":[TD([[makeQuery(id+"F6.imprint","IMPRINT",EDGE,{"derivedFrom":sQuery(id+"F6.wireOp",EDGE,"E42.15.0.25")}),1.0]])]});
            var Q1386;
            Q1386=makeQuery(id+"F6.imprint","IMPRINT",FACE,{"disambiguationData":[TD([[makeQuery(id+"F6.imprint","IMPRINT",EDGE,{"derivedFrom":sQuery(id+"F6.wireOp",EDGE,"E42.17.0.25")}),1.0]])]});
            var Q1387;
            Q1387=makeQuery(id+"F6.imprint","IMPRINT",FACE,{"disambiguationData":[TD([[makeQuery(id+"F6.imprint","IMPRINT",EDGE,{"derivedFrom":sQuery(id+"F6.wireOp",EDGE,"E42.19.0.25")}),1.0]])]});
            var Q1388;
            Q1388=makeQuery(id+"F6.imprint","IMPRINT",FACE,{"disambiguationData":[TD([[makeQuery(id+"F6.imprint","IMPRINT",EDGE,{"derivedFrom":sQuery(id+"F6.wireOp",EDGE,"E42.23.0.25")}),1.0]])]});
            var Q1389;
            Q1389=makeQuery(id+"F6.imprint","IMPRINT",FACE,{"disambiguationData":[TD([[makeQuery(id+"F6.imprint","IMPRINT",EDGE,{"derivedFrom":sQuery(id+"F6.wireOp",EDGE,"E42.21.0.25")}),1.0]])]});
            var Q1390;
            Q1390=makeQuery(id+"F6.imprint","IMPRINT",FACE,{"disambiguationData":[TD([[makeQuery(id+"F6.imprint","IMPRINT",EDGE,{"derivedFrom":sQuery(id+"F6.wireOp",EDGE,"E42.25.0.25")}),1.0]])]});
            var Q1391;
            Q1391=makeQuery(id+"F6.imprint","IMPRINT",FACE,{"disambiguationData":[TD([[makeQuery(id+"F6.imprint","IMPRINT",EDGE,{"derivedFrom":sQuery(id+"F6.wireOp",EDGE,"E175.MirrorC")}),-1.0]])]});
            var Q1392;
            Q1392=makeQuery(id+"F6.imprint","IMPRINT",FACE,{"disambiguationData":[TD([[makeQuery(id+"F6.imprint","IMPRINT",EDGE,{"derivedFrom":sQuery(id+"F6.wireOp",EDGE,"E151.MirrorC")}),-1.0]])]});
            var Q1393;
            Q1393=makeQuery(id+"F6.imprint","IMPRINT",FACE,{"disambiguationData":[TD([[makeQuery(id+"F6.imprint","IMPRINT",EDGE,{"derivedFrom":sQuery(id+"F6.wireOp",EDGE,"E126.MirrorC")}),-1.0]])]});
            var Q1394;
            Q1394=makeQuery(id+"F6.imprint","IMPRINT",FACE,{"disambiguationData":[TD([[makeQuery(id+"F6.imprint","IMPRINT",EDGE,{"derivedFrom":sQuery(id+"F6.wireOp",EDGE,"E106.MirrorC")}),-1.0]])]});
            var Q1395;
            Q1395=makeQuery(id+"F6.imprint","IMPRINT",FACE,{"disambiguationData":[TD([[makeQuery(id+"F6.imprint","IMPRINT",EDGE,{"derivedFrom":sQuery(id+"F6.wireOp",EDGE,"E224.MirrorC")}),-1.0]])]});
            var Q1396;
            Q1396=makeQuery(id+"F6.imprint","IMPRINT",FACE,{"disambiguationData":[TD([[makeQuery(id+"F6.imprint","IMPRINT",EDGE,{"derivedFrom":sQuery(id+"F6.wireOp",EDGE,"E200.MirrorC")}),-1.0]])]});
            var Q1397;
            Q1397=makeQuery(id+"F6.imprint","IMPRINT",FACE,{"disambiguationData":[TD([[makeQuery(id+"F6.imprint","IMPRINT",EDGE,{"derivedFrom":sQuery(id+"F6.wireOp",EDGE,"E81.MirrorC")}),-1.0]])]});
            var Q1398;
            Q1398=makeQuery(id+"F6.imprint","IMPRINT",FACE,{"disambiguationData":[TD([[makeQuery(id+"F6.imprint","IMPRINT",EDGE,{"derivedFrom":sQuery(id+"F6.wireOp",EDGE,"E55.MirrorC")}),-1.0]])]});
            var Q1399;
            Q1399=makeQuery(id+"F6.imprint","IMPRINT",FACE,{"disambiguationData":[TD([[makeQuery(id+"F6.imprint","IMPRINT",EDGE,{"derivedFrom":sQuery(id+"F6.wireOp",EDGE,"E176.MirrorC")}),-1.0]])]});
            var Q1400;
            Q1400=makeQuery(id+"F6.imprint","IMPRINT",FACE,{"disambiguationData":[TD([[makeQuery(id+"F6.imprint","IMPRINT",EDGE,{"derivedFrom":sQuery(id+"F6.wireOp",EDGE,"E152.MirrorC")}),-1.0]])]});
            var Q1401;
            Q1401=makeQuery(id+"F6.imprint","IMPRINT",FACE,{"disambiguationData":[TD([[makeQuery(id+"F6.imprint","IMPRINT",EDGE,{"derivedFrom":sQuery(id+"F6.wireOp",EDGE,"E127.MirrorC")}),-1.0]])]});
            var Q1402;
            Q1402=makeQuery(id+"F6.imprint","IMPRINT",FACE,{"disambiguationData":[TD([[makeQuery(id+"F6.imprint","IMPRINT",EDGE,{"derivedFrom":sQuery(id+"F6.wireOp",EDGE,"E107.MirrorC")}),-1.0]])]});
            var Q1403;
            Q1403=makeQuery(id+"F6.imprint","IMPRINT",FACE,{"disambiguationData":[TD([[makeQuery(id+"F6.imprint","IMPRINT",EDGE,{"derivedFrom":sQuery(id+"F6.wireOp",EDGE,"E226.MirrorC")}),-1.0]])]});
            var Q1404;
            Q1404=makeQuery(id+"F6.imprint","IMPRINT",FACE,{"disambiguationData":[TD([[makeQuery(id+"F6.imprint","IMPRINT",EDGE,{"derivedFrom":sQuery(id+"F6.wireOp",EDGE,"E203.MirrorC")}),-1.0]])]});
            var Q1405;
            Q1405=makeQuery(id+"F6.imprint","IMPRINT",FACE,{"disambiguationData":[TD([[makeQuery(id+"F6.imprint","IMPRINT",EDGE,{"derivedFrom":sQuery(id+"F6.wireOp",EDGE,"E82.MirrorC")}),-1.0]])]});
            var Q1406;
            Q1406=makeQuery(id+"F6.imprint","IMPRINT",FACE,{"disambiguationData":[TD([[makeQuery(id+"F6.imprint","IMPRINT",EDGE,{"derivedFrom":sQuery(id+"F6.wireOp",EDGE,"E59.MirrorC")}),-1.0]])]});
            var Q1407;
            Q1407=makeQuery(id+"F6.imprint","IMPRINT",FACE,{"disambiguationData":[TD([[makeQuery(id+"F6.imprint","IMPRINT",EDGE,{"derivedFrom":sQuery(id+"F6.wireOp",EDGE,"E180.MirrorC")}),-1.0]])]});
            var Q1408;
            Q1408=makeQuery(id+"F6.imprint","IMPRINT",FACE,{"disambiguationData":[TD([[makeQuery(id+"F6.imprint","IMPRINT",EDGE,{"derivedFrom":sQuery(id+"F6.wireOp",EDGE,"E155.MirrorC")}),-1.0]])]});
            var Q1409;
            Q1409=makeQuery(id+"F6.imprint","IMPRINT",FACE,{"disambiguationData":[TD([[makeQuery(id+"F6.imprint","IMPRINT",EDGE,{"derivedFrom":sQuery(id+"F6.wireOp",EDGE,"E133.MirrorC")}),-1.0]])]});
            var Q1410;
            Q1410=makeQuery(id+"F6.imprint","IMPRINT",FACE,{"disambiguationData":[TD([[makeQuery(id+"F6.imprint","IMPRINT",EDGE,{"derivedFrom":sQuery(id+"F6.wireOp",EDGE,"E108.MirrorC")}),-1.0]])]});
            var Q1411;
            Q1411=makeQuery(id+"F6.imprint","IMPRINT",FACE,{"disambiguationData":[TD([[makeQuery(id+"F6.imprint","IMPRINT",EDGE,{"derivedFrom":sQuery(id+"F6.wireOp",EDGE,"E228.MirrorC")}),-1.0]])]});
            var Q1412;
            Q1412=makeQuery(id+"F6.imprint","IMPRINT",FACE,{"disambiguationData":[TD([[makeQuery(id+"F6.imprint","IMPRINT",EDGE,{"derivedFrom":sQuery(id+"F6.wireOp",EDGE,"E204.MirrorC")}),-1.0]])]});
            var Q1413;
            Q1413=makeQuery(id+"F6.imprint","IMPRINT",FACE,{"disambiguationData":[TD([[makeQuery(id+"F6.imprint","IMPRINT",EDGE,{"derivedFrom":sQuery(id+"F6.wireOp",EDGE,"E83.MirrorC")}),-1.0]])]});
            var Q1414;
            Q1414=makeQuery(id+"F6.imprint","IMPRINT",FACE,{"disambiguationData":[TD([[makeQuery(id+"F6.imprint","IMPRINT",EDGE,{"derivedFrom":sQuery(id+"F6.wireOp",EDGE,"E60.MirrorC")}),-1.0]])]});
            var Q1415;
            Q1415=makeQuery(id+"F6.imprint","IMPRINT",FACE,{"disambiguationData":[TD([[makeQuery(id+"F6.imprint","IMPRINT",EDGE,{"derivedFrom":sQuery(id+"F6.wireOp",EDGE,"E181.MirrorC")}),-1.0]])]});
            var Q1416;
            Q1416=makeQuery(id+"F6.imprint","IMPRINT",FACE,{"disambiguationData":[TD([[makeQuery(id+"F6.imprint","IMPRINT",EDGE,{"derivedFrom":sQuery(id+"F6.wireOp",EDGE,"E156.MirrorC")}),-1.0]])]});
            var Q1417;
            Q1417=makeQuery(id+"F6.imprint","IMPRINT",FACE,{"disambiguationData":[TD([[makeQuery(id+"F6.imprint","IMPRINT",EDGE,{"derivedFrom":sQuery(id+"F6.wireOp",EDGE,"E134.MirrorC")}),-1.0]])]});
            var Q1418;
            Q1418=makeQuery(id+"F6.imprint","IMPRINT",FACE,{"disambiguationData":[TD([[makeQuery(id+"F6.imprint","IMPRINT",EDGE,{"derivedFrom":sQuery(id+"F6.wireOp",EDGE,"E109.MirrorC")}),-1.0]])]});
            var Q1419;
            Q1419=makeQuery(id+"F6.imprint","IMPRINT",FACE,{"disambiguationData":[TD([[makeQuery(id+"F6.imprint","IMPRINT",EDGE,{"derivedFrom":sQuery(id+"F6.wireOp",EDGE,"E230.MirrorC")}),-1.0]])]});
            var Q1420;
            Q1420=makeQuery(id+"F6.imprint","IMPRINT",FACE,{"disambiguationData":[TD([[makeQuery(id+"F6.imprint","IMPRINT",EDGE,{"derivedFrom":sQuery(id+"F6.wireOp",EDGE,"E205.MirrorC")}),-1.0]])]});
            var Q1421;
            Q1421=makeQuery(id+"F6.imprint","IMPRINT",FACE,{"disambiguationData":[TD([[makeQuery(id+"F6.imprint","IMPRINT",EDGE,{"derivedFrom":sQuery(id+"F6.wireOp",EDGE,"E86.MirrorC")}),-1.0]])]});
            var Q1422;
            Q1422=makeQuery(id+"F6.imprint","IMPRINT",FACE,{"disambiguationData":[TD([[makeQuery(id+"F6.imprint","IMPRINT",EDGE,{"derivedFrom":sQuery(id+"F6.wireOp",EDGE,"E61.MirrorC")}),-1.0]])]});
            var Q1423;
            Q1423=makeQuery(id+"F6.imprint","IMPRINT",FACE,{"disambiguationData":[TD([[makeQuery(id+"F6.imprint","IMPRINT",EDGE,{"derivedFrom":sQuery(id+"F6.wireOp",EDGE,"E182.MirrorC")}),-1.0]])]});
            var Q1424;
            Q1424=makeQuery(id+"F6.imprint","IMPRINT",FACE,{"disambiguationData":[TD([[makeQuery(id+"F6.imprint","IMPRINT",EDGE,{"derivedFrom":sQuery(id+"F6.wireOp",EDGE,"E159.MirrorC")}),-1.0]])]});
            var Q1425;
            Q1425=makeQuery(id+"F6.imprint","IMPRINT",FACE,{"disambiguationData":[TD([[makeQuery(id+"F6.imprint","IMPRINT",EDGE,{"derivedFrom":sQuery(id+"F6.wireOp",EDGE,"E135.MirrorC")}),-1.0]])]});
            var Q1426;
            Q1426=makeQuery(id+"F6.imprint","IMPRINT",FACE,{"disambiguationData":[TD([[makeQuery(id+"F6.imprint","IMPRINT",EDGE,{"derivedFrom":sQuery(id+"F6.wireOp",EDGE,"E110.MirrorC")}),-1.0]])]});
            var Q1427;
            Q1427=makeQuery(id+"F6.imprint","IMPRINT",FACE,{"disambiguationData":[TD([[makeQuery(id+"F6.imprint","IMPRINT",EDGE,{"derivedFrom":sQuery(id+"F6.wireOp",EDGE,"E231.MirrorC")}),-1.0]])]});
            var Q1428;
            Q1428=makeQuery(id+"F6.imprint","IMPRINT",FACE,{"disambiguationData":[TD([[makeQuery(id+"F6.imprint","IMPRINT",EDGE,{"derivedFrom":sQuery(id+"F6.wireOp",EDGE,"E206.MirrorC")}),-1.0]])]});
            var Q1429;
            Q1429=makeQuery(id+"F6.imprint","IMPRINT",FACE,{"disambiguationData":[TD([[makeQuery(id+"F6.imprint","IMPRINT",EDGE,{"derivedFrom":sQuery(id+"F6.wireOp",EDGE,"E42.2.0.23")}),1.0]])]});
            var Q1430;
            Q1430=makeQuery(id+"F6.imprint","IMPRINT",FACE,{"disambiguationData":[TD([[makeQuery(id+"F6.imprint","IMPRINT",EDGE,{"derivedFrom":sQuery(id+"F6.wireOp",EDGE,"E42.6.0.23")}),1.0]])]});
            var Q1431;
            Q1431=makeQuery(id+"F6.imprint","IMPRINT",FACE,{"disambiguationData":[TD([[makeQuery(id+"F6.imprint","IMPRINT",EDGE,{"derivedFrom":sQuery(id+"F6.wireOp",EDGE,"E42.4.0.23")}),1.0]])]});
            var Q1432;
            Q1432=makeQuery(id+"F6.imprint","IMPRINT",FACE,{"disambiguationData":[TD([[makeQuery(id+"F6.imprint","IMPRINT",EDGE,{"derivedFrom":sQuery(id+"F6.wireOp",EDGE,"E42.26.0.23")}),1.0]])]});
            var Q1433;
            Q1433=makeQuery(id+"F6.imprint","IMPRINT",FACE,{"disambiguationData":[TD([[makeQuery(id+"F6.imprint","IMPRINT",EDGE,{"derivedFrom":sQuery(id+"F6.wireOp",EDGE,"E42.24.0.23")}),1.0]])]});
            var Q1434;
            Q1434=makeQuery(id+"F6.imprint","IMPRINT",FACE,{"disambiguationData":[TD([[makeQuery(id+"F6.imprint","IMPRINT",EDGE,{"derivedFrom":sQuery(id+"F6.wireOp",EDGE,"E42.28.0.23")}),1.0]])]});
            var Q1435;
            Q1435=makeQuery(id+"F6.imprint","IMPRINT",FACE,{"disambiguationData":[TD([[makeQuery(id+"F6.imprint","IMPRINT",EDGE,{"derivedFrom":sQuery(id+"F6.wireOp",EDGE,"E42.30.0.23")}),1.0]])]});
            var Q1436;
            Q1436=makeQuery(id+"F6.imprint","IMPRINT",FACE,{"disambiguationData":[TD([[makeQuery(id+"F6.imprint","IMPRINT",EDGE,{"derivedFrom":sQuery(id+"F6.wireOp",EDGE,"E87.MirrorC")}),-1.0]])]});
            var Q1437;
            Q1437=makeQuery(id+"F6.imprint","IMPRINT",FACE,{"disambiguationData":[TD([[makeQuery(id+"F6.imprint","IMPRINT",EDGE,{"derivedFrom":sQuery(id+"F6.wireOp",EDGE,"E62.MirrorC")}),-1.0]])]});
            var Q1438;
            Q1438=makeQuery(id+"F6.imprint","IMPRINT",FACE,{"disambiguationData":[TD([[makeQuery(id+"F6.imprint","IMPRINT",EDGE,{"derivedFrom":sQuery(id+"F6.wireOp",EDGE,"E42.32.0.23")}),1.0]])]});
            var Q1439;
            Q1439=makeQuery(id+"F6.imprint","IMPRINT",FACE,{"disambiguationData":[TD([[makeQuery(id+"F6.imprint","IMPRINT",EDGE,{"derivedFrom":sQuery(id+"F6.wireOp",EDGE,"E42.8.0.23")}),1.0]])]});
            var Q1440;
            Q1440=makeQuery(id+"F6.imprint","IMPRINT",FACE,{"disambiguationData":[TD([[makeQuery(id+"F6.imprint","IMPRINT",EDGE,{"derivedFrom":sQuery(id+"F6.wireOp",EDGE,"E42.10.0.23")}),1.0]])]});
            var Q1441;
            Q1441=makeQuery(id+"F6.imprint","IMPRINT",FACE,{"disambiguationData":[TD([[makeQuery(id+"F6.imprint","IMPRINT",EDGE,{"derivedFrom":sQuery(id+"F6.wireOp",EDGE,"E42.14.0.23")}),1.0]])]});
            var Q1442;
            Q1442=makeQuery(id+"F6.imprint","IMPRINT",FACE,{"disambiguationData":[TD([[makeQuery(id+"F6.imprint","IMPRINT",EDGE,{"derivedFrom":sQuery(id+"F6.wireOp",EDGE,"E42.12.0.23")}),1.0]])]});
            var Q1443;
            Q1443=makeQuery(id+"F6.imprint","IMPRINT",FACE,{"disambiguationData":[TD([[makeQuery(id+"F6.imprint","IMPRINT",EDGE,{"derivedFrom":sQuery(id+"F6.wireOp",EDGE,"E42.16.0.23")}),1.0]])]});
            var Q1444;
            Q1444=makeQuery(id+"F6.imprint","IMPRINT",FACE,{"disambiguationData":[TD([[makeQuery(id+"F6.imprint","IMPRINT",EDGE,{"derivedFrom":sQuery(id+"F6.wireOp",EDGE,"E42.18.0.23")}),1.0]])]});
            var Q1445;
            Q1445=makeQuery(id+"F6.imprint","IMPRINT",FACE,{"disambiguationData":[TD([[makeQuery(id+"F6.imprint","IMPRINT",EDGE,{"derivedFrom":sQuery(id+"F6.wireOp",EDGE,"E42.20.0.23")}),1.0]])]});
            var Q1446;
            Q1446=makeQuery(id+"F6.imprint","IMPRINT",FACE,{"disambiguationData":[TD([[makeQuery(id+"F6.imprint","IMPRINT",EDGE,{"derivedFrom":sQuery(id+"F6.wireOp",EDGE,"E42.22.0.23")}),1.0]])]});
            var Q1447;
            Q1447=makeQuery(id+"F6.imprint","IMPRINT",FACE,{"disambiguationData":[TD([[makeQuery(id+"F6.imprint","IMPRINT",EDGE,{"derivedFrom":sQuery(id+"F6.wireOp",EDGE,"E183.MirrorC")}),-1.0]])]});
            var Q1448;
            Q1448=makeQuery(id+"F6.imprint","IMPRINT",FACE,{"disambiguationData":[TD([[makeQuery(id+"F6.imprint","IMPRINT",EDGE,{"derivedFrom":sQuery(id+"F6.wireOp",EDGE,"E160.MirrorC")}),-1.0]])]});
            var Q1449;
            Q1449=makeQuery(id+"F6.imprint","IMPRINT",FACE,{"disambiguationData":[TD([[makeQuery(id+"F6.imprint","IMPRINT",EDGE,{"derivedFrom":sQuery(id+"F6.wireOp",EDGE,"E136.MirrorC")}),-1.0]])]});
            var Q1450;
            Q1450=makeQuery(id+"F6.imprint","IMPRINT",FACE,{"disambiguationData":[TD([[makeQuery(id+"F6.imprint","IMPRINT",EDGE,{"derivedFrom":sQuery(id+"F6.wireOp",EDGE,"E113.MirrorC")}),-1.0]])]});
            var Q1451;
            Q1451=makeQuery(id+"F6.imprint","IMPRINT",FACE,{"disambiguationData":[TD([[makeQuery(id+"F6.imprint","IMPRINT",EDGE,{"derivedFrom":sQuery(id+"F6.wireOp",EDGE,"E232.MirrorC")}),-1.0]])]});
            var Q1452;
            Q1452=makeQuery(id+"F6.imprint","IMPRINT",FACE,{"disambiguationData":[TD([[makeQuery(id+"F6.imprint","IMPRINT",EDGE,{"derivedFrom":sQuery(id+"F6.wireOp",EDGE,"E208.MirrorC")}),-1.0]])]});
            var Q1453;
            Q1453=makeQuery(id+"F6.imprint","IMPRINT",FACE,{"disambiguationData":[TD([[makeQuery(id+"F6.imprint","IMPRINT",EDGE,{"derivedFrom":sQuery(id+"F6.wireOp",EDGE,"E42.2.0.24")}),1.0]])]});
            var Q1454;
            Q1454=makeQuery(id+"F6.imprint","IMPRINT",FACE,{"disambiguationData":[TD([[makeQuery(id+"F6.imprint","IMPRINT",EDGE,{"derivedFrom":sQuery(id+"F6.wireOp",EDGE,"E42.6.0.24")}),1.0]])]});
            var Q1455;
            Q1455=makeQuery(id+"F6.imprint","IMPRINT",FACE,{"disambiguationData":[TD([[makeQuery(id+"F6.imprint","IMPRINT",EDGE,{"derivedFrom":sQuery(id+"F6.wireOp",EDGE,"E42.4.0.24")}),1.0]])]});
            var Q1456;
            Q1456=makeQuery(id+"F6.imprint","IMPRINT",FACE,{"disambiguationData":[TD([[makeQuery(id+"F6.imprint","IMPRINT",EDGE,{"derivedFrom":sQuery(id+"F6.wireOp",EDGE,"E42.8.0.24")}),1.0]])]});
            var Q1457;
            Q1457=makeQuery(id+"F6.imprint","IMPRINT",FACE,{"disambiguationData":[TD([[makeQuery(id+"F6.imprint","IMPRINT",EDGE,{"derivedFrom":sQuery(id+"F6.wireOp",EDGE,"E42.28.0.24")}),1.0]])]});
            var Q1458;
            Q1458=makeQuery(id+"F6.imprint","IMPRINT",FACE,{"disambiguationData":[TD([[makeQuery(id+"F6.imprint","IMPRINT",EDGE,{"derivedFrom":sQuery(id+"F6.wireOp",EDGE,"E42.30.0.24")}),1.0]])]});
            var Q1459;
            Q1459=makeQuery(id+"F6.imprint","IMPRINT",FACE,{"disambiguationData":[TD([[makeQuery(id+"F6.imprint","IMPRINT",EDGE,{"derivedFrom":sQuery(id+"F6.wireOp",EDGE,"E88.MirrorC")}),-1.0]])]});
            var Q1460;
            Q1460=makeQuery(id+"F6.imprint","IMPRINT",FACE,{"disambiguationData":[TD([[makeQuery(id+"F6.imprint","IMPRINT",EDGE,{"derivedFrom":sQuery(id+"F6.wireOp",EDGE,"E63.MirrorC")}),-1.0]])]});
            var Q1461;
            Q1461=makeQuery(id+"F6.imprint","IMPRINT",FACE,{"disambiguationData":[TD([[makeQuery(id+"F6.imprint","IMPRINT",EDGE,{"derivedFrom":sQuery(id+"F6.wireOp",EDGE,"E42.32.0.24")}),1.0]])]});
            var Q1462;
            Q1462=makeQuery(id+"F6.imprint","IMPRINT",FACE,{"disambiguationData":[TD([[makeQuery(id+"F6.imprint","IMPRINT",EDGE,{"derivedFrom":sQuery(id+"F6.wireOp",EDGE,"E42.10.0.24")}),1.0]])]});
            var Q1463;
            Q1463=makeQuery(id+"F6.imprint","IMPRINT",FACE,{"disambiguationData":[TD([[makeQuery(id+"F6.imprint","IMPRINT",EDGE,{"derivedFrom":sQuery(id+"F6.wireOp",EDGE,"E42.14.0.24")}),1.0]])]});
            var Q1464;
            Q1464=makeQuery(id+"F6.imprint","IMPRINT",FACE,{"disambiguationData":[TD([[makeQuery(id+"F6.imprint","IMPRINT",EDGE,{"derivedFrom":sQuery(id+"F6.wireOp",EDGE,"E42.12.0.24")}),1.0]])]});
            var Q1465;
            Q1465=makeQuery(id+"F6.imprint","IMPRINT",FACE,{"disambiguationData":[TD([[makeQuery(id+"F6.imprint","IMPRINT",EDGE,{"derivedFrom":sQuery(id+"F6.wireOp",EDGE,"E42.16.0.24")}),1.0]])]});
            var Q1466;
            Q1466=makeQuery(id+"F6.imprint","IMPRINT",FACE,{"disambiguationData":[TD([[makeQuery(id+"F6.imprint","IMPRINT",EDGE,{"derivedFrom":sQuery(id+"F6.wireOp",EDGE,"E42.18.0.24")}),1.0]])]});
            var Q1467;
            Q1467=makeQuery(id+"F6.imprint","IMPRINT",FACE,{"disambiguationData":[TD([[makeQuery(id+"F6.imprint","IMPRINT",EDGE,{"derivedFrom":sQuery(id+"F6.wireOp",EDGE,"E42.20.0.24")}),1.0]])]});
            var Q1468;
            Q1468=makeQuery(id+"F6.imprint","IMPRINT",FACE,{"disambiguationData":[TD([[makeQuery(id+"F6.imprint","IMPRINT",EDGE,{"derivedFrom":sQuery(id+"F6.wireOp",EDGE,"E42.22.0.24")}),1.0]])]});
            var Q1469;
            Q1469=makeQuery(id+"F6.imprint","IMPRINT",FACE,{"disambiguationData":[TD([[makeQuery(id+"F6.imprint","IMPRINT",EDGE,{"derivedFrom":sQuery(id+"F6.wireOp",EDGE,"E42.26.0.24")}),1.0]])]});
            var Q1470;
            Q1470=makeQuery(id+"F6.imprint","IMPRINT",FACE,{"disambiguationData":[TD([[makeQuery(id+"F6.imprint","IMPRINT",EDGE,{"derivedFrom":sQuery(id+"F6.wireOp",EDGE,"E42.24.0.24")}),1.0]])]});
            var Q1471;
            Q1471=makeQuery(id+"F6.imprint","IMPRINT",FACE,{"disambiguationData":[TD([[makeQuery(id+"F6.imprint","IMPRINT",EDGE,{"derivedFrom":sQuery(id+"F6.wireOp",EDGE,"E42.2.0.25")}),1.0]])]});
            var Q1472;
            Q1472=makeQuery(id+"F6.imprint","IMPRINT",FACE,{"disambiguationData":[TD([[makeQuery(id+"F6.imprint","IMPRINT",EDGE,{"derivedFrom":sQuery(id+"F6.wireOp",EDGE,"E42.4.0.25")}),1.0]])]});
            var Q1473;
            Q1473=makeQuery(id+"F6.imprint","IMPRINT",FACE,{"disambiguationData":[TD([[makeQuery(id+"F6.imprint","IMPRINT",EDGE,{"derivedFrom":sQuery(id+"F6.wireOp",EDGE,"E42.6.0.25")}),1.0]])]});
            var Q1474;
            Q1474=makeQuery(id+"F6.imprint","IMPRINT",FACE,{"disambiguationData":[TD([[makeQuery(id+"F6.imprint","IMPRINT",EDGE,{"derivedFrom":sQuery(id+"F6.wireOp",EDGE,"E42.10.0.25")}),1.0]])]});
            var Q1475;
            Q1475=makeQuery(id+"F6.imprint","IMPRINT",FACE,{"disambiguationData":[TD([[makeQuery(id+"F6.imprint","IMPRINT",EDGE,{"derivedFrom":sQuery(id+"F6.wireOp",EDGE,"E42.8.0.25")}),1.0]])]});
            var Q1476;
            Q1476=makeQuery(id+"F6.imprint","IMPRINT",FACE,{"disambiguationData":[TD([[makeQuery(id+"F6.imprint","IMPRINT",EDGE,{"derivedFrom":sQuery(id+"F6.wireOp",EDGE,"E42.12.0.25")}),1.0]])]});
            var Q1477;
            Q1477=makeQuery(id+"F6.imprint","IMPRINT",FACE,{"disambiguationData":[TD([[makeQuery(id+"F6.imprint","IMPRINT",EDGE,{"derivedFrom":sQuery(id+"F6.wireOp",EDGE,"E42.14.0.25")}),1.0]])]});
            var Q1478;
            Q1478=makeQuery(id+"F6.imprint","IMPRINT",FACE,{"disambiguationData":[TD([[makeQuery(id+"F6.imprint","IMPRINT",EDGE,{"derivedFrom":sQuery(id+"F6.wireOp",EDGE,"E137.MirrorC")}),-1.0]])]});
            var Q1479;
            Q1479=makeQuery(id+"F6.imprint","IMPRINT",FACE,{"disambiguationData":[TD([[makeQuery(id+"F6.imprint","IMPRINT",EDGE,{"derivedFrom":sQuery(id+"F6.wireOp",EDGE,"E114.MirrorC")}),-1.0]])]});
            var Q1480;
            Q1480=makeQuery(id+"F6.imprint","IMPRINT",FACE,{"disambiguationData":[TD([[makeQuery(id+"F6.imprint","IMPRINT",EDGE,{"derivedFrom":sQuery(id+"F6.wireOp",EDGE,"E233.MirrorC")}),-1.0]])]});
            var Q1481;
            Q1481=makeQuery(id+"F6.imprint","IMPRINT",FACE,{"disambiguationData":[TD([[makeQuery(id+"F6.imprint","IMPRINT",EDGE,{"derivedFrom":sQuery(id+"F6.wireOp",EDGE,"E209.MirrorC")}),-1.0]])]});
            var Q1482;
            Q1482=makeQuery(id+"F6.imprint","IMPRINT",FACE,{"disambiguationData":[TD([[makeQuery(id+"F6.imprint","IMPRINT",EDGE,{"derivedFrom":sQuery(id+"F6.wireOp",EDGE,"E185.MirrorC")}),-1.0]])]});
            var Q1483;
            Q1483=makeQuery(id+"F6.imprint","IMPRINT",FACE,{"disambiguationData":[TD([[makeQuery(id+"F6.imprint","IMPRINT",EDGE,{"derivedFrom":sQuery(id+"F6.wireOp",EDGE,"E161.MirrorC")}),-1.0]])]});
            var Q1484;
            Q1484=makeQuery(id+"F6.imprint","IMPRINT",FACE,{"disambiguationData":[TD([[makeQuery(id+"F6.imprint","IMPRINT",EDGE,{"derivedFrom":sQuery(id+"F6.wireOp",EDGE,"E91.MirrorC")}),-1.0]])]});
            var Q1485;
            Q1485=makeQuery(id+"F6.imprint","IMPRINT",FACE,{"disambiguationData":[TD([[makeQuery(id+"F6.imprint","IMPRINT",EDGE,{"derivedFrom":sQuery(id+"F6.wireOp",EDGE,"E42.16.0.25")}),1.0]])]});
            var Q1486;
            Q1486=makeQuery(id+"F6.imprint","IMPRINT",FACE,{"disambiguationData":[TD([[makeQuery(id+"F6.imprint","IMPRINT",EDGE,{"derivedFrom":sQuery(id+"F6.wireOp",EDGE,"E42.18.0.25")}),1.0]])]});
            var Q1487;
            Q1487=makeQuery(id+"F6.imprint","IMPRINT",FACE,{"disambiguationData":[TD([[makeQuery(id+"F6.imprint","IMPRINT",EDGE,{"derivedFrom":sQuery(id+"F6.wireOp",EDGE,"E42.22.0.25")}),1.0]])]});
            var Q1488;
            Q1488=makeQuery(id+"F6.imprint","IMPRINT",FACE,{"disambiguationData":[TD([[makeQuery(id+"F6.imprint","IMPRINT",EDGE,{"derivedFrom":sQuery(id+"F6.wireOp",EDGE,"E42.20.0.25")}),1.0]])]});
            var Q1489;
            Q1489=makeQuery(id+"F6.imprint","IMPRINT",FACE,{"disambiguationData":[TD([[makeQuery(id+"F6.imprint","IMPRINT",EDGE,{"derivedFrom":sQuery(id+"F6.wireOp",EDGE,"E42.24.0.25")}),1.0]])]});
            var Q1490;
            Q1490=makeQuery(id+"F6.imprint","IMPRINT",FACE,{"disambiguationData":[TD([[makeQuery(id+"F6.imprint","IMPRINT",EDGE,{"derivedFrom":sQuery(id+"F6.wireOp",EDGE,"E42.26.0.25")}),1.0]])]});
            var Q1491;
            Q1491=makeQuery(id+"F6.imprint","IMPRINT",FACE,{"disambiguationData":[TD([[makeQuery(id+"F6.imprint","IMPRINT",EDGE,{"derivedFrom":sQuery(id+"F6.wireOp",EDGE,"E42.30.0.25")}),1.0]])]});
            var Q1492;
            Q1492=makeQuery(id+"F6.imprint","IMPRINT",FACE,{"disambiguationData":[TD([[makeQuery(id+"F6.imprint","IMPRINT",EDGE,{"derivedFrom":sQuery(id+"F6.wireOp",EDGE,"E42.28.0.25")}),1.0]])]});
            var Q1493;
            Q1493=makeQuery(id+"F6.imprint","IMPRINT",FACE,{"disambiguationData":[TD([[makeQuery(id+"F6.imprint","IMPRINT",EDGE,{"derivedFrom":sQuery(id+"F6.wireOp",EDGE,"E64.MirrorC")}),-1.0]])]});
            var Q1494;
            Q1494=makeQuery(id+"F6.imprint","IMPRINT",FACE,{"disambiguationData":[TD([[makeQuery(id+"F6.imprint","IMPRINT",EDGE,{"derivedFrom":sQuery(id+"F6.wireOp",EDGE,"E42.2.0.26")}),1.0]])]});
            var Q1495;
            Q1495=makeQuery(id+"F6.imprint","IMPRINT",FACE,{"disambiguationData":[TD([[makeQuery(id+"F6.imprint","IMPRINT",EDGE,{"derivedFrom":sQuery(id+"F6.wireOp",EDGE,"E42.4.0.26")}),1.0]])]});
            var Q1496;
            Q1496=makeQuery(id+"F6.imprint","IMPRINT",FACE,{"disambiguationData":[TD([[makeQuery(id+"F6.imprint","IMPRINT",EDGE,{"derivedFrom":sQuery(id+"F6.wireOp",EDGE,"E42.6.0.26")}),1.0]])]});
            var Q1497;
            Q1497=makeQuery(id+"F6.imprint","IMPRINT",FACE,{"disambiguationData":[TD([[makeQuery(id+"F6.imprint","IMPRINT",EDGE,{"derivedFrom":sQuery(id+"F6.wireOp",EDGE,"E42.10.0.26")}),1.0]])]});
            var Q1498;
            Q1498=makeQuery(id+"F6.imprint","IMPRINT",FACE,{"disambiguationData":[TD([[makeQuery(id+"F6.imprint","IMPRINT",EDGE,{"derivedFrom":sQuery(id+"F6.wireOp",EDGE,"E42.8.0.26")}),1.0]])]});
            var Q1499;
            Q1499=makeQuery(id+"F6.imprint","IMPRINT",FACE,{"disambiguationData":[TD([[makeQuery(id+"F6.imprint","IMPRINT",EDGE,{"derivedFrom":sQuery(id+"F6.wireOp",EDGE,"E42.12.0.26")}),1.0]])]});
            var Q1500;
            Q1500=makeQuery(id+"F6.imprint","IMPRINT",FACE,{"disambiguationData":[TD([[makeQuery(id+"F6.imprint","IMPRINT",EDGE,{"derivedFrom":sQuery(id+"F6.wireOp",EDGE,"E42.14.0.26")}),1.0]])]});
            var Q1501;
            Q1501=makeQuery(id+"F6.imprint","IMPRINT",FACE,{"disambiguationData":[TD([[makeQuery(id+"F6.imprint","IMPRINT",EDGE,{"derivedFrom":sQuery(id+"F6.wireOp",EDGE,"E42.16.0.26")}),1.0]])]});
            var Q1502;
            Q1502=makeQuery(id+"F6.imprint","IMPRINT",FACE,{"disambiguationData":[TD([[makeQuery(id+"F6.imprint","IMPRINT",EDGE,{"derivedFrom":sQuery(id+"F6.wireOp",EDGE,"E138.MirrorC")}),-1.0]])]});
            var Q1503;
            Q1503=makeQuery(id+"F6.imprint","IMPRINT",FACE,{"disambiguationData":[TD([[makeQuery(id+"F6.imprint","IMPRINT",EDGE,{"derivedFrom":sQuery(id+"F6.wireOp",EDGE,"E115.MirrorC")}),-1.0]])]});
            var Q1504;
            Q1504=makeQuery(id+"F6.imprint","IMPRINT",FACE,{"disambiguationData":[TD([[makeQuery(id+"F6.imprint","IMPRINT",EDGE,{"derivedFrom":sQuery(id+"F6.wireOp",EDGE,"E236.MirrorC")}),-1.0]])]});
            var Q1505;
            Q1505=makeQuery(id+"F6.imprint","IMPRINT",FACE,{"disambiguationData":[TD([[makeQuery(id+"F6.imprint","IMPRINT",EDGE,{"derivedFrom":sQuery(id+"F6.wireOp",EDGE,"E210.MirrorC")}),-1.0]])]});
            var Q1506;
            Q1506=makeQuery(id+"F6.imprint","IMPRINT",FACE,{"disambiguationData":[TD([[makeQuery(id+"F6.imprint","IMPRINT",EDGE,{"derivedFrom":sQuery(id+"F6.wireOp",EDGE,"E189.MirrorC")}),-1.0]])]});
            var Q1507;
            Q1507=makeQuery(id+"F6.imprint","IMPRINT",FACE,{"disambiguationData":[TD([[makeQuery(id+"F6.imprint","IMPRINT",EDGE,{"derivedFrom":sQuery(id+"F6.wireOp",EDGE,"E162.MirrorC")}),-1.0]])]});
            var Q1508;
            Q1508=makeQuery(id+"F6.imprint","IMPRINT",FACE,{"disambiguationData":[TD([[makeQuery(id+"F6.imprint","IMPRINT",EDGE,{"derivedFrom":sQuery(id+"F6.wireOp",EDGE,"E42.18.0.26")}),1.0]])]});
            var Q1509;
            Q1509=makeQuery(id+"F6.imprint","IMPRINT",FACE,{"disambiguationData":[TD([[makeQuery(id+"F6.imprint","IMPRINT",EDGE,{"derivedFrom":sQuery(id+"F6.wireOp",EDGE,"E42.22.0.26")}),1.0]])]});
            var Q1510;
            Q1510=makeQuery(id+"F6.imprint","IMPRINT",FACE,{"disambiguationData":[TD([[makeQuery(id+"F6.imprint","IMPRINT",EDGE,{"derivedFrom":sQuery(id+"F6.wireOp",EDGE,"E42.20.0.26")}),1.0]])]});
            var Q1511;
            Q1511=makeQuery(id+"F6.imprint","IMPRINT",FACE,{"disambiguationData":[TD([[makeQuery(id+"F6.imprint","IMPRINT",EDGE,{"derivedFrom":sQuery(id+"F6.wireOp",EDGE,"E42.24.0.26")}),1.0]])]});
            var Q1512;
            Q1512=makeQuery(id+"F6.imprint","IMPRINT",FACE,{"disambiguationData":[TD([[makeQuery(id+"F6.imprint","IMPRINT",EDGE,{"derivedFrom":sQuery(id+"F6.wireOp",EDGE,"E42.26.0.26")}),1.0]])]});
            var Q1513;
            Q1513=makeQuery(id+"F6.imprint","IMPRINT",FACE,{"disambiguationData":[TD([[makeQuery(id+"F6.imprint","IMPRINT",EDGE,{"derivedFrom":sQuery(id+"F6.wireOp",EDGE,"E42.30.0.26")}),1.0]])]});
            var Q1514;
            Q1514=makeQuery(id+"F6.imprint","IMPRINT",FACE,{"disambiguationData":[TD([[makeQuery(id+"F6.imprint","IMPRINT",EDGE,{"derivedFrom":sQuery(id+"F6.wireOp",EDGE,"E42.28.0.26")}),1.0]])]});
            var Q1515;
            Q1515=makeQuery(id+"F6.imprint","IMPRINT",FACE,{"disambiguationData":[TD([[makeQuery(id+"F6.imprint","IMPRINT",EDGE,{"derivedFrom":sQuery(id+"F6.wireOp",EDGE,"E65.MirrorC")}),-1.0]])]});
            var Q1516;
            Q1516=makeQuery(id+"F6.imprint","IMPRINT",FACE,{"disambiguationData":[TD([[makeQuery(id+"F6.imprint","IMPRINT",EDGE,{"derivedFrom":sQuery(id+"F6.wireOp",EDGE,"E42.32.0.26")}),1.0]])]});
            var Q1517;
            Q1517=makeQuery(id+"F6.imprint","IMPRINT",FACE,{"disambiguationData":[TD([[makeQuery(id+"F6.imprint","IMPRINT",EDGE,{"derivedFrom":sQuery(id+"F6.wireOp",EDGE,"E92.MirrorC")}),-1.0]])]});
            var Q1518;
            Q1518=makeQuery(id+"F6.imprint","IMPRINT",FACE,{"disambiguationData":[TD([[makeQuery(id+"F6.imprint","IMPRINT",EDGE,{"derivedFrom":sQuery(id+"F6.wireOp",EDGE,"E139.MirrorC")}),-1.0]])]});
            var Q1519;
            Q1519=makeQuery(id+"F6.imprint","IMPRINT",FACE,{"disambiguationData":[TD([[makeQuery(id+"F6.imprint","IMPRINT",EDGE,{"derivedFrom":sQuery(id+"F6.wireOp",EDGE,"E116.MirrorC")}),-1.0]])]});
            var Q1520;
            Q1520=makeQuery(id+"F6.imprint","IMPRINT",FACE,{"disambiguationData":[TD([[makeQuery(id+"F6.imprint","IMPRINT",EDGE,{"derivedFrom":sQuery(id+"F6.wireOp",EDGE,"E238.MirrorC")}),-1.0]])]});
            var Q1521;
            Q1521=makeQuery(id+"F6.imprint","IMPRINT",FACE,{"disambiguationData":[TD([[makeQuery(id+"F6.imprint","IMPRINT",EDGE,{"derivedFrom":sQuery(id+"F6.wireOp",EDGE,"E212.MirrorC")}),-1.0]])]});
            var Q1522;
            Q1522=makeQuery(id+"F6.imprint","IMPRINT",FACE,{"disambiguationData":[TD([[makeQuery(id+"F6.imprint","IMPRINT",EDGE,{"derivedFrom":sQuery(id+"F6.wireOp",EDGE,"E190.MirrorC")}),-1.0]])]});
            var Q1523;
            Q1523=makeQuery(id+"F6.imprint","IMPRINT",FACE,{"disambiguationData":[TD([[makeQuery(id+"F6.imprint","IMPRINT",EDGE,{"derivedFrom":sQuery(id+"F6.wireOp",EDGE,"E163.MirrorC")}),-1.0]])]});
            var Q1524;
            Q1524=makeQuery(id+"F6.imprint","IMPRINT",FACE,{"disambiguationData":[TD([[makeQuery(id+"F6.imprint","IMPRINT",EDGE,{"derivedFrom":sQuery(id+"F6.wireOp",EDGE,"E66.MirrorC")}),-1.0]])]});
            var Q1525;
            Q1525=makeQuery(id+"F6.imprint","IMPRINT",FACE,{"disambiguationData":[TD([[makeQuery(id+"F6.imprint","IMPRINT",EDGE,{"derivedFrom":sQuery(id+"F6.wireOp",EDGE,"E94.MirrorC")}),-1.0]])]});
            var Q1526;
            Q1526=makeQuery(id+"F6.imprint","IMPRINT",FACE,{"disambiguationData":[TD([[makeQuery(id+"F6.imprint","IMPRINT",EDGE,{"derivedFrom":sQuery(id+"F6.wireOp",EDGE,"E140.MirrorC")}),-1.0]])]});
            var Q1527;
            Q1527=makeQuery(id+"F6.imprint","IMPRINT",FACE,{"disambiguationData":[TD([[makeQuery(id+"F6.imprint","IMPRINT",EDGE,{"derivedFrom":sQuery(id+"F6.wireOp",EDGE,"E118.MirrorC")}),-1.0]])]});
            var Q1528;
            Q1528=makeQuery(id+"F6.imprint","IMPRINT",FACE,{"disambiguationData":[TD([[makeQuery(id+"F6.imprint","IMPRINT",EDGE,{"derivedFrom":sQuery(id+"F6.wireOp",EDGE,"E239.MirrorC")}),-1.0]])]});
            var Q1529;
            Q1529=makeQuery(id+"F6.imprint","IMPRINT",FACE,{"disambiguationData":[TD([[makeQuery(id+"F6.imprint","IMPRINT",EDGE,{"derivedFrom":sQuery(id+"F6.wireOp",EDGE,"E213.MirrorC")}),-1.0]])]});
            var Q1530;
            Q1530=makeQuery(id+"F6.imprint","IMPRINT",FACE,{"disambiguationData":[TD([[makeQuery(id+"F6.imprint","IMPRINT",EDGE,{"derivedFrom":sQuery(id+"F6.wireOp",EDGE,"E191.MirrorC")}),-1.0]])]});
            var Q1531;
            Q1531=makeQuery(id+"F6.imprint","IMPRINT",FACE,{"disambiguationData":[TD([[makeQuery(id+"F6.imprint","IMPRINT",EDGE,{"derivedFrom":sQuery(id+"F6.wireOp",EDGE,"E164.MirrorC")}),-1.0]])]});
            var Q1532;
            Q1532=makeQuery(id+"F6.imprint","IMPRINT",FACE,{"disambiguationData":[TD([[makeQuery(id+"F6.imprint","IMPRINT",EDGE,{"derivedFrom":sQuery(id+"F6.wireOp",EDGE,"E69.MirrorC")}),-1.0]])]});
            var Q1533;
            Q1533=makeQuery(id+"F6.imprint","IMPRINT",FACE,{"disambiguationData":[TD([[makeQuery(id+"F6.imprint","IMPRINT",EDGE,{"derivedFrom":sQuery(id+"F6.wireOp",EDGE,"E48.MirrorC")}),-1.0]])]});
            var Q1534;
            Q1534=makeQuery(id+"F6.imprint","IMPRINT",FACE,{"disambiguationData":[TD([[makeQuery(id+"F6.imprint","IMPRINT",EDGE,{"derivedFrom":sQuery(id+"F6.wireOp",EDGE,"E95.MirrorC")}),-1.0]])]});
            var Q1535;
            Q1535=makeQuery(id+"F6.imprint","IMPRINT",FACE,{"disambiguationData":[TD([[makeQuery(id+"F6.imprint","IMPRINT",EDGE,{"derivedFrom":sQuery(id+"F6.wireOp",EDGE,"E143.MirrorC")}),-1.0]])]});
            var Q1536;
            Q1536=makeQuery(id+"F6.imprint","IMPRINT",FACE,{"disambiguationData":[TD([[makeQuery(id+"F6.imprint","IMPRINT",EDGE,{"derivedFrom":sQuery(id+"F6.wireOp",EDGE,"E120.MirrorC")}),-1.0]])]});
            var Q1537;
            Q1537=makeQuery(id+"F6.imprint","IMPRINT",FACE,{"disambiguationData":[TD([[makeQuery(id+"F6.imprint","IMPRINT",EDGE,{"derivedFrom":sQuery(id+"F6.wireOp",EDGE,"E240.MirrorC")}),-1.0]])]});
            var Q1538;
            Q1538=makeQuery(id+"F6.imprint","IMPRINT",FACE,{"disambiguationData":[TD([[makeQuery(id+"F6.imprint","IMPRINT",EDGE,{"derivedFrom":sQuery(id+"F6.wireOp",EDGE,"E214.MirrorC")}),-1.0]])]});
            var Q1539;
            Q1539=makeQuery(id+"F6.imprint","IMPRINT",FACE,{"disambiguationData":[TD([[makeQuery(id+"F6.imprint","IMPRINT",EDGE,{"derivedFrom":sQuery(id+"F6.wireOp",EDGE,"E192.MirrorC")}),-1.0]])]});
            var Q1540;
            Q1540=makeQuery(id+"F6.imprint","IMPRINT",FACE,{"disambiguationData":[TD([[makeQuery(id+"F6.imprint","IMPRINT",EDGE,{"derivedFrom":sQuery(id+"F6.wireOp",EDGE,"E167.MirrorC")}),-1.0]])]});
            var Q1541;
            Q1541=makeQuery(id+"F6.imprint","IMPRINT",FACE,{"disambiguationData":[TD([[makeQuery(id+"F6.imprint","IMPRINT",EDGE,{"derivedFrom":sQuery(id+"F6.wireOp",EDGE,"E70.MirrorC")}),-1.0]])]});
            var Q1542;
            Q1542=makeQuery(id+"F6.imprint","IMPRINT",FACE,{"disambiguationData":[TD([[makeQuery(id+"F6.imprint","IMPRINT",EDGE,{"derivedFrom":sQuery(id+"F6.wireOp",EDGE,"E49.MirrorC")}),-1.0]])]});
            var Q1543;
            Q1543=makeQuery(id+"F6.imprint","IMPRINT",FACE,{"disambiguationData":[TD([[makeQuery(id+"F6.imprint","IMPRINT",EDGE,{"derivedFrom":sQuery(id+"F6.wireOp",EDGE,"E96.MirrorC")}),-1.0]])]});
            var Q1544;
            Q1544=makeQuery(id+"F6.imprint","IMPRINT",FACE,{"disambiguationData":[TD([[makeQuery(id+"F6.imprint","IMPRINT",EDGE,{"derivedFrom":sQuery(id+"F6.wireOp",EDGE,"E146.MirrorC")}),-1.0]])]});
            var Q1545;
            Q1545=makeQuery(id+"F6.imprint","IMPRINT",FACE,{"disambiguationData":[TD([[makeQuery(id+"F6.imprint","IMPRINT",EDGE,{"derivedFrom":sQuery(id+"F6.wireOp",EDGE,"E121.MirrorC")}),-1.0]])]});
            var Q1546;
            Q1546=makeQuery(id+"F6.imprint","IMPRINT",FACE,{"disambiguationData":[TD([[makeQuery(id+"F6.imprint","IMPRINT",EDGE,{"derivedFrom":sQuery(id+"F6.wireOp",EDGE,"E242.MirrorC")}),-1.0]])]});
            var Q1547;
            Q1547=makeQuery(id+"F6.imprint","IMPRINT",FACE,{"disambiguationData":[TD([[makeQuery(id+"F6.imprint","IMPRINT",EDGE,{"derivedFrom":sQuery(id+"F6.wireOp",EDGE,"E216.MirrorC")}),-1.0]])]});
            var Q1548;
            Q1548=makeQuery(id+"F6.imprint","IMPRINT",FACE,{"disambiguationData":[TD([[makeQuery(id+"F6.imprint","IMPRINT",EDGE,{"derivedFrom":sQuery(id+"F6.wireOp",EDGE,"E193.MirrorC")}),-1.0]])]});
            var Q1549;
            Q1549=makeQuery(id+"F6.imprint","IMPRINT",FACE,{"disambiguationData":[TD([[makeQuery(id+"F6.imprint","IMPRINT",EDGE,{"derivedFrom":sQuery(id+"F6.wireOp",EDGE,"E168.MirrorC")}),-1.0]])]});
            var Q1550;
            Q1550=makeQuery(id+"F6.imprint","IMPRINT",FACE,{"disambiguationData":[TD([[makeQuery(id+"F6.imprint","IMPRINT",EDGE,{"derivedFrom":sQuery(id+"F6.wireOp",EDGE,"E147.MirrorC")}),-1.0]])]});
            var Q1551;
            Q1551=makeQuery(id+"F6.imprint","IMPRINT",FACE,{"disambiguationData":[TD([[makeQuery(id+"F6.imprint","IMPRINT",EDGE,{"derivedFrom":sQuery(id+"F6.wireOp",EDGE,"E122.MirrorC")}),-1.0]])]});
            var Q1552;
            Q1552=makeQuery(id+"F6.imprint","IMPRINT",FACE,{"disambiguationData":[TD([[makeQuery(id+"F6.imprint","IMPRINT",EDGE,{"derivedFrom":sQuery(id+"F6.wireOp",EDGE,"E71.MirrorC")}),-1.0]])]});
            var Q1553;
            Q1553=makeQuery(id+"F6.imprint","IMPRINT",FACE,{"disambiguationData":[TD([[makeQuery(id+"F6.imprint","IMPRINT",EDGE,{"derivedFrom":sQuery(id+"F6.wireOp",EDGE,"E50.MirrorC")}),-1.0]])]});
            var Q1554;
            Q1554=makeQuery(id+"F6.imprint","IMPRINT",FACE,{"disambiguationData":[TD([[makeQuery(id+"F6.imprint","IMPRINT",EDGE,{"derivedFrom":sQuery(id+"F6.wireOp",EDGE,"E97.MirrorC")}),-1.0]])]});
            var Q1555;
            Q1555=makeQuery(id+"F6.imprint","IMPRINT",FACE,{"disambiguationData":[TD([[makeQuery(id+"F6.imprint","IMPRINT",EDGE,{"derivedFrom":sQuery(id+"F6.wireOp",EDGE,"E42.13.0.23")}),1.0]])]});
            var Q1556;
            Q1556=makeQuery(id+"F6.imprint","IMPRINT",FACE,{"disambiguationData":[TD([[makeQuery(id+"F6.imprint","IMPRINT",EDGE,{"derivedFrom":sQuery(id+"F6.wireOp",EDGE,"E42.11.0.23")}),1.0]])]});
            var Q1557;
            Q1557=makeQuery(id+"F6.imprint","IMPRINT",FACE,{"disambiguationData":[TD([[makeQuery(id+"F6.imprint","IMPRINT",EDGE,{"derivedFrom":sQuery(id+"F6.wireOp",EDGE,"E42.15.0.23")}),1.0]])]});
            var Q1558;
            Q1558=makeQuery(id+"F6.imprint","IMPRINT",FACE,{"disambiguationData":[TD([[makeQuery(id+"F6.imprint","IMPRINT",EDGE,{"derivedFrom":sQuery(id+"F6.wireOp",EDGE,"E42.17.0.23")}),1.0]])]});
            var Q1559;
            Q1559=makeQuery(id+"F6.imprint","IMPRINT",FACE,{"disambiguationData":[TD([[makeQuery(id+"F6.imprint","IMPRINT",EDGE,{"derivedFrom":sQuery(id+"F6.wireOp",EDGE,"E42.19.0.23")}),1.0]])]});
            var Q1560;
            Q1560=makeQuery(id+"F6.imprint","IMPRINT",FACE,{"disambiguationData":[TD([[makeQuery(id+"F6.imprint","IMPRINT",EDGE,{"derivedFrom":sQuery(id+"F6.wireOp",EDGE,"E42.21.0.23")}),1.0]])]});
            var Q1561;
            Q1561=makeQuery(id+"F6.imprint","IMPRINT",FACE,{"disambiguationData":[TD([[makeQuery(id+"F6.imprint","IMPRINT",EDGE,{"derivedFrom":sQuery(id+"F6.wireOp",EDGE,"E42.25.0.23")}),1.0]])]});
            var Q1562;
            Q1562=makeQuery(id+"F6.imprint","IMPRINT",FACE,{"disambiguationData":[TD([[makeQuery(id+"F6.imprint","IMPRINT",EDGE,{"derivedFrom":sQuery(id+"F6.wireOp",EDGE,"E42.23.0.23")}),1.0]])]});
            var Q1563;
            Q1563=makeQuery(id+"F6.imprint","IMPRINT",FACE,{"disambiguationData":[TD([[makeQuery(id+"F6.imprint","IMPRINT",EDGE,{"derivedFrom":sQuery(id+"F6.wireOp",EDGE,"E42.27.0.23")}),1.0]])]});
            var Q1564;
            Q1564=makeQuery(id+"F6.imprint","IMPRINT",FACE,{"disambiguationData":[TD([[makeQuery(id+"F6.imprint","IMPRINT",EDGE,{"derivedFrom":sQuery(id+"F6.wireOp",EDGE,"E220.MirrorC")}),-1.0]])]});
            var Q1565;
            Q1565=makeQuery(id+"F6.imprint","IMPRINT",FACE,{"disambiguationData":[TD([[makeQuery(id+"F6.imprint","IMPRINT",EDGE,{"derivedFrom":sQuery(id+"F6.wireOp",EDGE,"E196.MirrorC")}),-1.0]])]});
            var Q1566;
            Q1566=makeQuery(id+"F6.imprint","IMPRINT",FACE,{"disambiguationData":[TD([[makeQuery(id+"F6.imprint","IMPRINT",EDGE,{"derivedFrom":sQuery(id+"F6.wireOp",EDGE,"E169.MirrorC")}),-1.0]])]});
            var Q1567;
            Q1567=makeQuery(id+"F6.imprint","IMPRINT",FACE,{"disambiguationData":[TD([[makeQuery(id+"F6.imprint","IMPRINT",EDGE,{"derivedFrom":sQuery(id+"F6.wireOp",EDGE,"E42.1.0.23")}),1.0]])]});
            var Q1568;
            Q1568=makeQuery(id+"F6.imprint","IMPRINT",FACE,{"disambiguationData":[TD([[makeQuery(id+"F6.imprint","IMPRINT",EDGE,{"derivedFrom":sQuery(id+"F6.wireOp",EDGE,"E42.5.0.23")}),1.0]])]});
            var Q1569;
            Q1569=makeQuery(id+"F6.imprint","IMPRINT",FACE,{"disambiguationData":[TD([[makeQuery(id+"F6.imprint","IMPRINT",EDGE,{"derivedFrom":sQuery(id+"F6.wireOp",EDGE,"E42.3.0.23")}),1.0]])]});
            var Q1570;
            Q1570=makeQuery(id+"F6.imprint","IMPRINT",FACE,{"disambiguationData":[TD([[makeQuery(id+"F6.imprint","IMPRINT",EDGE,{"derivedFrom":sQuery(id+"F6.wireOp",EDGE,"E42.7.0.23")}),1.0]])]});
            var Q1571;
            Q1571=makeQuery(id+"F6.imprint","IMPRINT",FACE,{"disambiguationData":[TD([[makeQuery(id+"F6.imprint","IMPRINT",EDGE,{"derivedFrom":sQuery(id+"F6.wireOp",EDGE,"E42.9.0.23")}),1.0]])]});
            var Q1572;
            Q1572=makeQuery(id+"F6.imprint","IMPRINT",FACE,{"disambiguationData":[TD([[makeQuery(id+"F6.imprint","IMPRINT",EDGE,{"derivedFrom":sQuery(id+"F6.wireOp",EDGE,"E42.29.0.23")}),1.0]])]});
            var Q1573;
            Q1573=makeQuery(id+"F6.imprint","IMPRINT",FACE,{"disambiguationData":[TD([[makeQuery(id+"F6.imprint","IMPRINT",EDGE,{"derivedFrom":sQuery(id+"F6.wireOp",EDGE,"E75.MirrorC")}),-1.0]])]});
            var Q1574;
            Q1574=makeQuery(id+"F6.imprint","IMPRINT",FACE,{"disambiguationData":[TD([[makeQuery(id+"F6.imprint","IMPRINT",EDGE,{"derivedFrom":sQuery(id+"F6.wireOp",EDGE,"E42.31.0.23")}),1.0]])]});
            var Q1575;
            Q1575=makeQuery(id+"F6.imprint","IMPRINT",FACE,{"disambiguationData":[TD([[makeQuery(id+"F6.imprint","IMPRINT",EDGE,{"derivedFrom":sQuery(id+"F6.wireOp",EDGE,"E100.MirrorC")}),-1.0]])]});
            var Q1576;
            Q1576=makeQuery(id+"F6.imprint","IMPRINT",FACE,{"disambiguationData":[TD([[makeQuery(id+"F6.imprint","IMPRINT",EDGE,{"derivedFrom":sQuery(id+"F6.wireOp",EDGE,"E41.0.1.0")}),1.0]])]});
            var Q1577;
            Q1577=makeQuery(id+"F6.imprint","IMPRINT",FACE,{"disambiguationData":[TD([[makeQuery(id+"F6.imprint","IMPRINT",EDGE,{"derivedFrom":sQuery(id+"F6.wireOp",EDGE,"E37")}),1.0]])]});
            var Q1578;
            Q1578=makeQuery(id+"F6.imprint","IMPRINT",FACE,{"disambiguationData":[TD([[makeQuery(id+"F6.imprint","IMPRINT",EDGE,{"derivedFrom":sQuery(id+"F6.wireOp",EDGE,"E40.0.1.0")}),1.0]])]});
            var Q1579;
            Q1579=makeQuery(id+"F6.imprint","IMPRINT",FACE,{"disambiguationData":[TD([[makeQuery(id+"F6.imprint","IMPRINT",EDGE,{"derivedFrom":sQuery(id+"F6.wireOp",EDGE,"E42.5.0.3")}),-1.0]])]});
            var Q1580;
            Q1580=makeQuery(id+"F6.imprint","IMPRINT",FACE,{"disambiguationData":[TD([[makeQuery(id+"F6.imprint","IMPRINT",EDGE,{"derivedFrom":sQuery(id+"F6.wireOp",EDGE,"E42.20.0.3")}),-1.0]])]});
            var Q1581;
            Q1581=makeQuery(id+"F6.imprint","IMPRINT",FACE,{"disambiguationData":[TD([[makeQuery(id+"F6.imprint","IMPRINT",EDGE,{"derivedFrom":sQuery(id+"F6.wireOp",EDGE,"E42.4.0.3")}),-1.0]])]});
            var Q1582;
            Q1582=makeQuery(id+"F6.imprint","IMPRINT",FACE,{"disambiguationData":[TD([[makeQuery(id+"F6.imprint","IMPRINT",EDGE,{"derivedFrom":sQuery(id+"F6.wireOp",EDGE,"E42.13.0.3")}),-1.0]])]});
            var Q1583;
            Q1583=makeQuery(id+"F6.imprint","IMPRINT",FACE,{"disambiguationData":[TD([[makeQuery(id+"F6.imprint","IMPRINT",EDGE,{"derivedFrom":sQuery(id+"F6.wireOp",EDGE,"E42.18.0.3")}),-1.0]])]});
            var Q1584;
            Q1584=makeQuery(id+"F6.imprint","IMPRINT",FACE,{"disambiguationData":[TD([[makeQuery(id+"F6.imprint","IMPRINT",EDGE,{"derivedFrom":sQuery(id+"F6.wireOp",EDGE,"E42.31.0.3")}),-1.0]])]});
            var Q1585;
            Q1585=makeQuery(id+"F6.imprint","IMPRINT",FACE,{"disambiguationData":[TD([[makeQuery(id+"F6.imprint","IMPRINT",EDGE,{"derivedFrom":sQuery(id+"F6.wireOp",EDGE,"E42.27.0.3")}),-1.0]])]});
            var Q1586;
            Q1586=makeQuery(id+"F6.imprint","IMPRINT",FACE,{"disambiguationData":[TD([[makeQuery(id+"F6.imprint","IMPRINT",EDGE,{"derivedFrom":sQuery(id+"F6.wireOp",EDGE,"E42.28.0.3")}),-1.0]])]});
            var Q1587;
            Q1587=makeQuery(id+"F6.imprint","IMPRINT",FACE,{"disambiguationData":[TD([[makeQuery(id+"F6.imprint","IMPRINT",EDGE,{"derivedFrom":sQuery(id+"F6.wireOp",EDGE,"E42.3.0.3")}),-1.0]])]});
            var Q1588;
            Q1588=makeQuery(id+"F6.imprint","IMPRINT",FACE,{"disambiguationData":[TD([[makeQuery(id+"F6.imprint","IMPRINT",EDGE,{"derivedFrom":sQuery(id+"F6.wireOp",EDGE,"E42.26.0.3")}),-1.0]])]});
            var Q1589;
            Q1589=makeQuery(id+"F6.imprint","IMPRINT",FACE,{"disambiguationData":[TD([[makeQuery(id+"F6.imprint","IMPRINT",EDGE,{"derivedFrom":sQuery(id+"F6.wireOp",EDGE,"E42.23.0.3")}),-1.0]])]});
            var Q1590;
            Q1590=makeQuery(id+"F6.imprint","IMPRINT",FACE,{"disambiguationData":[TD([[makeQuery(id+"F6.imprint","IMPRINT",EDGE,{"derivedFrom":sQuery(id+"F6.wireOp",EDGE,"E42.10.0.3")}),-1.0]])]});
            var Q1591;
            Q1591=makeQuery(id+"F6.imprint","IMPRINT",FACE,{"disambiguationData":[TD([[makeQuery(id+"F6.imprint","IMPRINT",EDGE,{"derivedFrom":sQuery(id+"F6.wireOp",EDGE,"E42.30.0.3")}),-1.0]])]});
            var Q1592;
            Q1592=makeQuery(id+"F6.imprint","IMPRINT",FACE,{"disambiguationData":[TD([[makeQuery(id+"F6.imprint","IMPRINT",EDGE,{"derivedFrom":sQuery(id+"F6.wireOp",EDGE,"E42.1.0.3")}),-1.0]])]});
            var Q1593;
            Q1593=makeQuery(id+"F6.imprint","IMPRINT",FACE,{"disambiguationData":[TD([[makeQuery(id+"F6.imprint","IMPRINT",EDGE,{"derivedFrom":sQuery(id+"F6.wireOp",EDGE,"E42.22.0.3")}),-1.0]])]});
            var Q1594;
            Q1594=makeQuery(id+"F6.imprint","IMPRINT",FACE,{"disambiguationData":[TD([[makeQuery(id+"F6.imprint","IMPRINT",EDGE,{"derivedFrom":sQuery(id+"F6.wireOp",EDGE,"E42.32.0.3")}),-1.0]])]});
            var Q1595;
            Q1595=makeQuery(id+"F6.imprint","IMPRINT",FACE,{"disambiguationData":[TD([[makeQuery(id+"F6.imprint","IMPRINT",EDGE,{"derivedFrom":sQuery(id+"F6.wireOp",EDGE,"E42.16.0.3")}),-1.0]])]});
            var Q1596;
            Q1596=makeQuery(id+"F6.imprint","IMPRINT",FACE,{"disambiguationData":[TD([[makeQuery(id+"F6.imprint","IMPRINT",EDGE,{"derivedFrom":sQuery(id+"F6.wireOp",EDGE,"E42.12.0.3")}),-1.0]])]});
            var Q1597;
            Q1597=makeQuery(id+"F6.imprint","IMPRINT",FACE,{"disambiguationData":[TD([[makeQuery(id+"F6.imprint","IMPRINT",EDGE,{"derivedFrom":sQuery(id+"F6.wireOp",EDGE,"E42.15.0.3")}),-1.0]])]});
            var Q1598;
            Q1598=makeQuery(id+"F6.imprint","IMPRINT",FACE,{"disambiguationData":[TD([[makeQuery(id+"F6.imprint","IMPRINT",EDGE,{"derivedFrom":sQuery(id+"F6.wireOp",EDGE,"E42.21.0.3")}),-1.0]])]});
            var Q1599;
            Q1599=makeQuery(id+"F6.imprint","IMPRINT",FACE,{"disambiguationData":[TD([[makeQuery(id+"F6.imprint","IMPRINT",EDGE,{"derivedFrom":sQuery(id+"F6.wireOp",EDGE,"E42.17.0.3")}),-1.0]])]});
            var Q1600;
            Q1600=makeQuery(id+"F6.imprint","IMPRINT",FACE,{"disambiguationData":[TD([[makeQuery(id+"F6.imprint","IMPRINT",EDGE,{"derivedFrom":sQuery(id+"F6.wireOp",EDGE,"E42.29.0.3")}),-1.0]])]});
            var Q1601;
            Q1601=makeQuery(id+"F6.imprint","IMPRINT",FACE,{"disambiguationData":[TD([[makeQuery(id+"F6.imprint","IMPRINT",EDGE,{"derivedFrom":sQuery(id+"F6.wireOp",EDGE,"E42.24.0.3")}),-1.0]])]});
            var Q1602;
            Q1602=makeQuery(id+"F6.imprint","IMPRINT",FACE,{"disambiguationData":[TD([[makeQuery(id+"F6.imprint","IMPRINT",EDGE,{"derivedFrom":sQuery(id+"F6.wireOp",EDGE,"E42.14.0.3")}),-1.0]])]});
            var Q1603;
            Q1603=makeQuery(id+"F6.imprint","IMPRINT",FACE,{"disambiguationData":[TD([[makeQuery(id+"F6.imprint","IMPRINT",EDGE,{"derivedFrom":sQuery(id+"F6.wireOp",EDGE,"E42.1.0.25")}),1.0]])]});
            var Q1604;
            Q1604=makeQuery(id+"F6.imprint","IMPRINT",FACE,{"disambiguationData":[TD([[makeQuery(id+"F6.imprint","IMPRINT",EDGE,{"derivedFrom":sQuery(id+"F6.wireOp",EDGE,"E42.6.0.3")}),-1.0]])]});
            var Q1605;
            Q1605=makeQuery(id+"F6.imprint","IMPRINT",FACE,{"disambiguationData":[TD([[makeQuery(id+"F6.imprint","IMPRINT",EDGE,{"derivedFrom":sQuery(id+"F6.wireOp",EDGE,"E42.8.0.3")}),-1.0]])]});
            var Q1606;
            Q1606=makeQuery(id+"F6.imprint","IMPRINT",FACE,{"disambiguationData":[TD([[makeQuery(id+"F6.imprint","IMPRINT",EDGE,{"derivedFrom":sQuery(id+"F6.wireOp",EDGE,"E42.19.0.3")}),-1.0]])]});
            var Q1607;
            Q1607=makeQuery(id+"F6.imprint","IMPRINT",FACE,{"disambiguationData":[TD([[makeQuery(id+"F6.imprint","IMPRINT",EDGE,{"derivedFrom":sQuery(id+"F6.wireOp",EDGE,"E42.9.0.3")}),-1.0]])]});
            var Q1608;
            Q1608=makeQuery(id+"F6.imprint","IMPRINT",FACE,{"disambiguationData":[TD([[makeQuery(id+"F6.imprint","IMPRINT",EDGE,{"derivedFrom":sQuery(id+"F6.wireOp",EDGE,"E42.7.0.3")}),-1.0]])]});
            var Q1609;
            Q1609=makeQuery(id+"F6.imprint","IMPRINT",FACE,{"disambiguationData":[TD([[makeQuery(id+"F6.imprint","IMPRINT",EDGE,{"derivedFrom":sQuery(id+"F6.wireOp",EDGE,"E40.0.12.0")}),-1.0]])]});
            var Q1610;
            Q1610=makeQuery(id+"F6.imprint","IMPRINT",FACE,{"disambiguationData":[TD([[makeQuery(id+"F6.imprint","IMPRINT",EDGE,{"derivedFrom":sQuery(id+"F6.wireOp",EDGE,"E42.25.0.3")}),-1.0]])]});
            var Q1611;
            Q1611=makeQuery(id+"F6.imprint","IMPRINT",FACE,{"disambiguationData":[TD([[makeQuery(id+"F6.imprint","IMPRINT",EDGE,{"derivedFrom":sQuery(id+"F6.wireOp",EDGE,"E42.2.0.3")}),-1.0]])]});
            var Q1612;
            Q1612=makeQuery(id+"F6.imprint","IMPRINT",FACE,{"disambiguationData":[TD([[makeQuery(id+"F6.imprint","IMPRINT",EDGE,{"derivedFrom":sQuery(id+"F6.wireOp",EDGE,"E42.32.0.25")}),1.0]])]});
            var Q1613;
            Q1613=makeQuery(id+"F6.imprint","IMPRINT",FACE,{"disambiguationData":[TD([[makeQuery(id+"F6.imprint","IMPRINT",EDGE,{"derivedFrom":sQuery(id+"F6.wireOp",EDGE,"E45.MirrorC")}),-1.0]])]});
            var Q1614;
            Q1614=makeQuery(id+"F6.imprint","IMPRINT",FACE,{"disambiguationData":[TD([[makeQuery(id+"F6.imprint","IMPRINT",EDGE,{"derivedFrom":sQuery(id+"F6.wireOp",EDGE,"E42.11.0.3")}),-1.0]])]});
            var Q1615;
            Q1615=makeQuery(id+"F6.imprint","IMPRINT",FACE,{"disambiguationData":[TD([[makeQuery(id+"F6.imprint","IMPRINT",EDGE,{"derivedFrom":sQuery(id+"F6.wireOp",EDGE,"E51.MirrorC")}),-1.0]])]});
            var Q1616;
            Q1616=makeQuery(id+"F6.imprint","IMPRINT",FACE,{"disambiguationData":[TD([[makeQuery(id+"F6.imprint","IMPRINT",EDGE,{"derivedFrom":sQuery(id+"F6.wireOp",EDGE,"E38")}),1.0]])]});
            extrude(context, id + "F7", {"entities" : qUnion([Q0, Q1, Q2, Q3, Q4, Q5, Q6, Q7, Q8, Q9, Q10, Q11, Q12, Q13, Q14, Q15, Q16, Q17, Q18, Q19, Q20, Q21, Q22, Q23, Q24, Q25, Q26, Q27, Q28, Q29, Q30, Q31, Q32, Q33, Q34, Q35, Q36, Q37, Q38, Q39, Q40, Q41, Q42, Q43, Q44, Q45, Q46, Q47, Q48, Q49, Q50, Q51, Q52, Q53, Q54, Q55, Q56, Q57, Q58, Q59, Q60, Q61, Q62, Q63, Q64, Q65, Q66, Q67, Q68, Q69, Q70, Q71, Q72, Q73, Q74, Q75, Q76, Q77, Q78, Q79, Q80, Q81, Q82, Q83, Q84, Q85, Q86, Q87, Q88, Q89, Q90, Q91, Q92, Q93, Q94, Q95, Q96, Q97, Q98, Q99, Q100, Q101, Q102, Q103, Q104, Q105, Q106, Q107, Q108, Q109, Q110, Q111, Q112, Q113, Q114, Q115, Q116, Q117, Q118, Q119, Q120, Q121, Q122, Q123, Q124, Q125, Q126, Q127, Q128, Q129, Q130, Q131, Q132, Q133, Q134, Q135, Q136, Q137, Q138, Q139, Q140, Q141, Q142, Q143, Q144, Q145, Q146, Q147, Q148, Q149, Q150, Q151, Q152, Q153, Q154, Q155, Q156, Q157, Q158, Q159, Q160, Q161, Q162, Q163, Q164, Q165, Q166, Q167, Q168, Q169, Q170, Q171, Q172, Q173, Q174, Q175, Q176, Q177, Q178, Q179, Q180, Q181, Q182, Q183, Q184, Q185, Q186, Q187, Q188, Q189, Q190, Q191, Q192, Q193, Q194, Q195, Q196, Q197, Q198, Q199, Q200, Q201, Q202, Q203, Q204, Q205, Q206, Q207, Q208, Q209, Q210, Q211, Q212, Q213, Q214, Q215, Q216, Q217, Q218, Q219, Q220, Q221, Q222, Q223, Q224, Q225, Q226, Q227, Q228, Q229, Q230, Q231, Q232, Q233, Q234, Q235, Q236, Q237, Q238, Q239, Q240, Q241, Q242, Q243, Q244, Q245, Q246, Q247, Q248, Q249, Q250, Q251, Q252, Q253, Q254, Q255, Q256, Q257, Q258, Q259, Q260, Q261, Q262, Q263, Q264, Q265, Q266, Q267, Q268, Q269, Q270, Q271, Q272, Q273, Q274, Q275, Q276, Q277, Q278, Q279, Q280, Q281, Q282, Q283, Q284, Q285, Q286, Q287, Q288, Q289, Q290, Q291, Q292, Q293, Q294, Q295, Q296, Q297, Q298, Q299, Q300, Q301, Q302, Q303, Q304, Q305, Q306, Q307, Q308, Q309, Q310, Q311, Q312, Q313, Q314, Q315, Q316, Q317, Q318, Q319, Q320, Q321, Q322, Q323, Q324, Q325, Q326, Q327, Q328, Q329, Q330, Q331, Q332, Q333, Q334, Q335, Q336, Q337, Q338, Q339, Q340, Q341, Q342, Q343, Q344, Q345, Q346, Q347, Q348, Q349, Q350, Q351, Q352, Q353, Q354, Q355, Q356, Q357, Q358, Q359, Q360, Q361, Q362, Q363, Q364, Q365, Q366, Q367, Q368, Q369, Q370, Q371, Q372, Q373, Q374, Q375, Q376, Q377, Q378, Q379, Q380, Q381, Q382, Q383, Q384, Q385, Q386, Q387, Q388, Q389, Q390, Q391, Q392, Q393, Q394, Q395, Q396, Q397, Q398, Q399, Q400, Q401, Q402, Q403, Q404, Q405, Q406, Q407, Q408, Q409, Q410, Q411, Q412, Q413, Q414, Q415, Q416, Q417, Q418, Q419, Q420, Q421, Q422, Q423, Q424, Q425, Q426, Q427, Q428, Q429, Q430, Q431, Q432, Q433, Q434, Q435, Q436, Q437, Q438, Q439, Q440, Q441, Q442, Q443, Q444, Q445, Q446, Q447, Q448, Q449, Q450, Q451, Q452, Q453, Q454, Q455, Q456, Q457, Q458, Q459, Q460, Q461, Q462, Q463, Q464, Q465, Q466, Q467, Q468, Q469, Q470, Q471, Q472, Q473, Q474, Q475, Q476, Q477, Q478, Q479, Q480, Q481, Q482, Q483, Q484, Q485, Q486, Q487, Q488, Q489, Q490, Q491, Q492, Q493, Q494, Q495, Q496, Q497, Q498, Q499, Q500, Q501, Q502, Q503, Q504, Q505, Q506, Q507, Q508, Q509, Q510, Q511, Q512, Q513, Q514, Q515, Q516, Q517, Q518, Q519, Q520, Q521, Q522, Q523, Q524, Q525, Q526, Q527, Q528, Q529, Q530, Q531, Q532, Q533, Q534, Q535, Q536, Q537, Q538, Q539, Q540, Q541, Q542, Q543, Q544, Q545, Q546, Q547, Q548, Q549, Q550, Q551, Q552, Q553, Q554, Q555, Q556, Q557, Q558, Q559, Q560, Q561, Q562, Q563, Q564, Q565, Q566, Q567, Q568, Q569, Q570, Q571, Q572, Q573, Q574, Q575, Q576, Q577, Q578, Q579, Q580, Q581, Q582, Q583, Q584, Q585, Q586, Q587, Q588, Q589, Q590, Q591, Q592, Q593, Q594, Q595, Q596, Q597, Q598, Q599, Q600, Q601, Q602, Q603, Q604, Q605, Q606, Q607, Q608, Q609, Q610, Q611, Q612, Q613, Q614, Q615, Q616, Q617, Q618, Q619, Q620, Q621, Q622, Q623, Q624, Q625, Q626, Q627, Q628, Q629, Q630, Q631, Q632, Q633, Q634, Q635, Q636, Q637, Q638, Q639, Q640, Q641, Q642, Q643, Q644, Q645, Q646, Q647, Q648, Q649, Q650, Q651, Q652, Q653, Q654, Q655, Q656, Q657, Q658, Q659, Q660, Q661, Q662, Q663, Q664, Q665, Q666, Q667, Q668, Q669, Q670, Q671, Q672, Q673, Q674, Q675, Q676, Q677, Q678, Q679, Q680, Q681, Q682, Q683, Q684, Q685, Q686, Q687, Q688, Q689, Q690, Q691, Q692, Q693, Q694, Q695, Q696, Q697, Q698, Q699, Q700, Q701, Q702, Q703, Q704, Q705, Q706, Q707, Q708, Q709, Q710, Q711, Q712, Q713, Q714, Q715, Q716, Q717, Q718, Q719, Q720, Q721, Q722, Q723, Q724, Q725, Q726, Q727, Q728, Q729, Q730, Q731, Q732, Q733, Q734, Q735, Q736, Q737, Q738, Q739, Q740, Q741, Q742, Q743, Q744, Q745, Q746, Q747, Q748, Q749, Q750, Q751, Q752, Q753, Q754, Q755, Q756, Q757, Q758, Q759, Q760, Q761, Q762, Q763, Q764, Q765, Q766, Q767, Q768, Q769, Q770, Q771, Q772, Q773, Q774, Q775, Q776, Q777, Q778, Q779, Q780, Q781, Q782, Q783, Q784, Q785, Q786, Q787, Q788, Q789, Q790, Q791, Q792, Q793, Q794, Q795, Q796, Q797, Q798, Q799, Q800, Q801, Q802, Q803, Q804, Q805, Q806, Q807, Q808, Q809, Q810, Q811, Q812, Q813, Q814, Q815, Q816, Q817, Q818, Q819, Q820, Q821, Q822, Q823, Q824, Q825, Q826, Q827, Q828, Q829, Q830, Q831, Q832, Q833, Q834, Q835, Q836, Q837, Q838, Q839, Q840, Q841, Q842, Q843, Q844, Q845, Q846, Q847, Q848, Q849, Q850, Q851, Q852, Q853, Q854, Q855, Q856, Q857, Q858, Q859, Q860, Q861, Q862, Q863, Q864, Q865, Q866, Q867, Q868, Q869, Q870, Q871, Q872, Q873, Q874, Q875, Q876, Q877, Q878, Q879, Q880, Q881, Q882, Q883, Q884, Q885, Q886, Q887, Q888, Q889, Q890, Q891, Q892, Q893, Q894, Q895, Q896, Q897, Q898, Q899, Q900, Q901, Q902, Q903, Q904, Q905, Q906, Q907, Q908, Q909, Q910, Q911, Q912, Q913, Q914, Q915, Q916, Q917, Q918, Q919, Q920, Q921, Q922, Q923, Q924, Q925, Q926, Q927, Q928, Q929, Q930, Q931, Q932, Q933, Q934, Q935, Q936, Q937, Q938, Q939, Q940, Q941, Q942, Q943, Q944, Q945, Q946, Q947, Q948, Q949, Q950, Q951, Q952, Q953, Q954, Q955, Q956, Q957, Q958, Q959, Q960, Q961, Q962, Q963, Q964, Q965, Q966, Q967, Q968, Q969, Q970, Q971, Q972, Q973, Q974, Q975, Q976, Q977, Q978, Q979, Q980, Q981, Q982, Q983, Q984, Q985, Q986, Q987, Q988, Q989, Q990, Q991, Q992, Q993, Q994, Q995, Q996, Q997, Q998, Q999, Q1000, Q1001, Q1002, Q1003, Q1004, Q1005, Q1006, Q1007, Q1008, Q1009, Q1010, Q1011, Q1012, Q1013, Q1014, Q1015, Q1016, Q1017, Q1018, Q1019, Q1020, Q1021, Q1022, Q1023, Q1024, Q1025, Q1026, Q1027, Q1028, Q1029, Q1030, Q1031, Q1032, Q1033, Q1034, Q1035, Q1036, Q1037, Q1038, Q1039, Q1040, Q1041, Q1042, Q1043, Q1044, Q1045, Q1046, Q1047, Q1048, Q1049, Q1050, Q1051, Q1052, Q1053, Q1054, Q1055, Q1056, Q1057, Q1058, Q1059, Q1060, Q1061, Q1062, Q1063, Q1064, Q1065, Q1066, Q1067, Q1068, Q1069, Q1070, Q1071, Q1072, Q1073, Q1074, Q1075, Q1076, Q1077, Q1078, Q1079, Q1080, Q1081, Q1082, Q1083, Q1084, Q1085, Q1086, Q1087, Q1088, Q1089, Q1090, Q1091, Q1092, Q1093, Q1094, Q1095, Q1096, Q1097, Q1098, Q1099, Q1100, Q1101, Q1102, Q1103, Q1104, Q1105, Q1106, Q1107, Q1108, Q1109, Q1110, Q1111, Q1112, Q1113, Q1114, Q1115, Q1116, Q1117, Q1118, Q1119, Q1120, Q1121, Q1122, Q1123, Q1124, Q1125, Q1126, Q1127, Q1128, Q1129, Q1130, Q1131, Q1132, Q1133, Q1134, Q1135, Q1136, Q1137, Q1138, Q1139, Q1140, Q1141, Q1142, Q1143, Q1144, Q1145, Q1146, Q1147, Q1148, Q1149, Q1150, Q1151, Q1152, Q1153, Q1154, Q1155, Q1156, Q1157, Q1158, Q1159, Q1160, Q1161, Q1162, Q1163, Q1164, Q1165, Q1166, Q1167, Q1168, Q1169, Q1170, Q1171, Q1172, Q1173, Q1174, Q1175, Q1176, Q1177, Q1178, Q1179, Q1180, Q1181, Q1182, Q1183, Q1184, Q1185, Q1186, Q1187, Q1188, Q1189, Q1190, Q1191, Q1192, Q1193, Q1194, Q1195, Q1196, Q1197, Q1198, Q1199, Q1200, Q1201, Q1202, Q1203, Q1204, Q1205, Q1206, Q1207, Q1208, Q1209, Q1210, Q1211, Q1212, Q1213, Q1214, Q1215, Q1216, Q1217, Q1218, Q1219, Q1220, Q1221, Q1222, Q1223, Q1224, Q1225, Q1226, Q1227, Q1228, Q1229, Q1230, Q1231, Q1232, Q1233, Q1234, Q1235, Q1236, Q1237, Q1238, Q1239, Q1240, Q1241, Q1242, Q1243, Q1244, Q1245, Q1246, Q1247, Q1248, Q1249, Q1250, Q1251, Q1252, Q1253, Q1254, Q1255, Q1256, Q1257, Q1258, Q1259, Q1260, Q1261, Q1262, Q1263, Q1264, Q1265, Q1266, Q1267, Q1268, Q1269, Q1270, Q1271, Q1272, Q1273, Q1274, Q1275, Q1276, Q1277, Q1278, Q1279, Q1280, Q1281, Q1282, Q1283, Q1284, Q1285, Q1286, Q1287, Q1288, Q1289, Q1290, Q1291, Q1292, Q1293, Q1294, Q1295, Q1296, Q1297, Q1298, Q1299, Q1300, Q1301, Q1302, Q1303, Q1304, Q1305, Q1306, Q1307, Q1308, Q1309, Q1310, Q1311, Q1312, Q1313, Q1314, Q1315, Q1316, Q1317, Q1318, Q1319, Q1320, Q1321, Q1322, Q1323, Q1324, Q1325, Q1326, Q1327, Q1328, Q1329, Q1330, Q1331, Q1332, Q1333, Q1334, Q1335, Q1336, Q1337, Q1338, Q1339, Q1340, Q1341, Q1342, Q1343, Q1344, Q1345, Q1346, Q1347, Q1348, Q1349, Q1350, Q1351, Q1352, Q1353, Q1354, Q1355, Q1356, Q1357, Q1358, Q1359, Q1360, Q1361, Q1362, Q1363, Q1364, Q1365, Q1366, Q1367, Q1368, Q1369, Q1370, Q1371, Q1372, Q1373, Q1374, Q1375, Q1376, Q1377, Q1378, Q1379, Q1380, Q1381, Q1382, Q1383, Q1384, Q1385, Q1386, Q1387, Q1388, Q1389, Q1390, Q1391, Q1392, Q1393, Q1394, Q1395, Q1396, Q1397, Q1398, Q1399, Q1400, Q1401, Q1402, Q1403, Q1404, Q1405, Q1406, Q1407, Q1408, Q1409, Q1410, Q1411, Q1412, Q1413, Q1414, Q1415, Q1416, Q1417, Q1418, Q1419, Q1420, Q1421, Q1422, Q1423, Q1424, Q1425, Q1426, Q1427, Q1428, Q1429, Q1430, Q1431, Q1432, Q1433, Q1434, Q1435, Q1436, Q1437, Q1438, Q1439, Q1440, Q1441, Q1442, Q1443, Q1444, Q1445, Q1446, Q1447, Q1448, Q1449, Q1450, Q1451, Q1452, Q1453, Q1454, Q1455, Q1456, Q1457, Q1458, Q1459, Q1460, Q1461, Q1462, Q1463, Q1464, Q1465, Q1466, Q1467, Q1468, Q1469, Q1470, Q1471, Q1472, Q1473, Q1474, Q1475, Q1476, Q1477, Q1478, Q1479, Q1480, Q1481, Q1482, Q1483, Q1484, Q1485, Q1486, Q1487, Q1488, Q1489, Q1490, Q1491, Q1492, Q1493, Q1494, Q1495, Q1496, Q1497, Q1498, Q1499, Q1500, Q1501, Q1502, Q1503, Q1504, Q1505, Q1506, Q1507, Q1508, Q1509, Q1510, Q1511, Q1512, Q1513, Q1514, Q1515, Q1516, Q1517, Q1518, Q1519, Q1520, Q1521, Q1522, Q1523, Q1524, Q1525, Q1526, Q1527, Q1528, Q1529, Q1530, Q1531, Q1532, Q1533, Q1534, Q1535, Q1536, Q1537, Q1538, Q1539, Q1540, Q1541, Q1542, Q1543, Q1544, Q1545, Q1546, Q1547, Q1548, Q1549, Q1550, Q1551, Q1552, Q1553, Q1554, Q1555, Q1556, Q1557, Q1558, Q1559, Q1560, Q1561, Q1562, Q1563, Q1564, Q1565, Q1566, Q1567, Q1568, Q1569, Q1570, Q1571, Q1572, Q1573, Q1574, Q1575, Q1576, Q1577, Q1578, Q1579, Q1580, Q1581, Q1582, Q1583, Q1584, Q1585, Q1586, Q1587, Q1588, Q1589, Q1590, Q1591, Q1592, Q1593, Q1594, Q1595, Q1596, Q1597, Q1598, Q1599, Q1600, Q1601, Q1602, Q1603, Q1604, Q1605, Q1606, Q1607, Q1608, Q1609, Q1610, Q1611, Q1612, Q1613, Q1614, Q1615, Q1616]), "operationType" : NewBodyOperationType.REMOVE, "oppositeDirection" : true, "depth" : 25 * mm});
        }
        {
            var Q0;
            Q0=makeQuery(id+"F5.boolean.opBoolean","INTERSECT",EDGE,{"derivedFrom":[makeQuery(id+"F1.opExtrude","SWEPT_FACE",FACE,{"disambiguationData":[OSD([sQuery(id+"F0.wireOp",EDGE,"E0")])]}),makeQuery(id+"F5.opExtrude","CAP_FACE",FACE,{"disambiguationData":[OSD([sQuery(id+"F4.wireOp",EDGE,"E22"),sQuery(id+"F4.wireOp",EDGE,"E23"),sQuery(id+"F4.wireOp",EDGE,"E24"),sQuery(id+"F4.wireOp",EDGE,"E25"),sQuery(id+"F4.wireOp",EDGE,"E33"),sQuery(id+"F4.wireOp",EDGE,"E34.1.0.0"),sQuery(id+"F4.wireOp",EDGE,"E34.2.0.0"),sQuery(id+"F4.wireOp",EDGE,"E34.3.0.0"),sQuery(id+"F4.wireOp",EDGE,"E34.4.0.0"),sQuery(id+"F4.wireOp",EDGE,"E34.5.0.0"),sQuery(id+"F4.wireOp",EDGE,"E34.6.0.0"),sQuery(id+"F4.wireOp",EDGE,"E34.7.0.0"),sQuery(id+"F4.wireOp",EDGE,"E34.8.0.0"),sQuery(id+"F4.wireOp",EDGE,"E34.9.0.0"),sQuery(id+"F4.wireOp",EDGE,"E34.10.0.0"),sQuery(id+"F4.wireOp",EDGE,"E34.11.0.0"),sQuery(id+"F4.wireOp",EDGE,"E34.12.0.0"),sQuery(id+"F4.wireOp",EDGE,"E34.13.0.0"),sQuery(id+"F4.wireOp",EDGE,"E34.14.0.0")])],"isStart":false})]});
            var Q1;
            Q1=makeQuery(id+"F3.boolean.opBoolean","INTERSECT",EDGE,{"derivedFrom":[makeQuery(id+"F1.opExtrude","SWEPT_FACE",FACE,{"disambiguationData":[OSD([sQuery(id+"F0.wireOp",EDGE,"E0")])]}),makeQuery(id+"F3.opExtrude","CAP_FACE",FACE,{"disambiguationData":[OSD([sQuery(id+"F2.wireOp",EDGE,"E7"),sQuery(id+"F2.wireOp",EDGE,"E8"),sQuery(id+"F2.wireOp",EDGE,"E9"),sQuery(id+"F2.wireOp",EDGE,"E10"),sQuery(id+"F2.wireOp",EDGE,"E18"),sQuery(id+"F2.wireOp",EDGE,"E19.1.0.0"),sQuery(id+"F2.wireOp",EDGE,"E19.2.0.0"),sQuery(id+"F2.wireOp",EDGE,"E19.3.0.0"),sQuery(id+"F2.wireOp",EDGE,"E19.4.0.0"),sQuery(id+"F2.wireOp",EDGE,"E19.5.0.0"),sQuery(id+"F2.wireOp",EDGE,"E19.6.0.0"),sQuery(id+"F2.wireOp",EDGE,"E19.7.0.0"),sQuery(id+"F2.wireOp",EDGE,"E19.8.0.0"),sQuery(id+"F2.wireOp",EDGE,"E19.9.0.0"),sQuery(id+"F2.wireOp",EDGE,"E19.10.0.0"),sQuery(id+"F2.wireOp",EDGE,"E19.11.0.0"),sQuery(id+"F2.wireOp",EDGE,"E19.12.0.0"),sQuery(id+"F2.wireOp",EDGE,"E19.13.0.0"),sQuery(id+"F2.wireOp",EDGE,"E19.14.0.0")])],"isStart":false})]});
            fillet(context, id + "F8", {"entities" : qUnion([Q0, Q1]), "radius" : 2 * mm, "tangentPropagation" : true, "allowEdgeOverflow" : false});
        }
        {
            var Q0;
            Q0=makeQuery(id+"F1.opExtrude","CAP_EDGE",EDGE,{"disambiguationData":[OSD([sQuery(id+"F0.wireOp",EDGE,"E2"),sQuery(id+"F0.wireOp",EDGE,"E4")])],"isStart":true});
            var Q1;
            Q1=makeQuery(id+"F1.opExtrude","CAP_EDGE",EDGE,{"disambiguationData":[OSD([sQuery(id+"F0.wireOp",EDGE,"E2"),sQuery(id+"F0.wireOp",EDGE,"E4")])],"isStart":false});
            fillet(context, id + "F9", {"entities" : qUnion([Q0, Q1]), "radius" : 4 * mm, "tangentPropagation" : true, "allowEdgeOverflow" : false});
        }
    });
